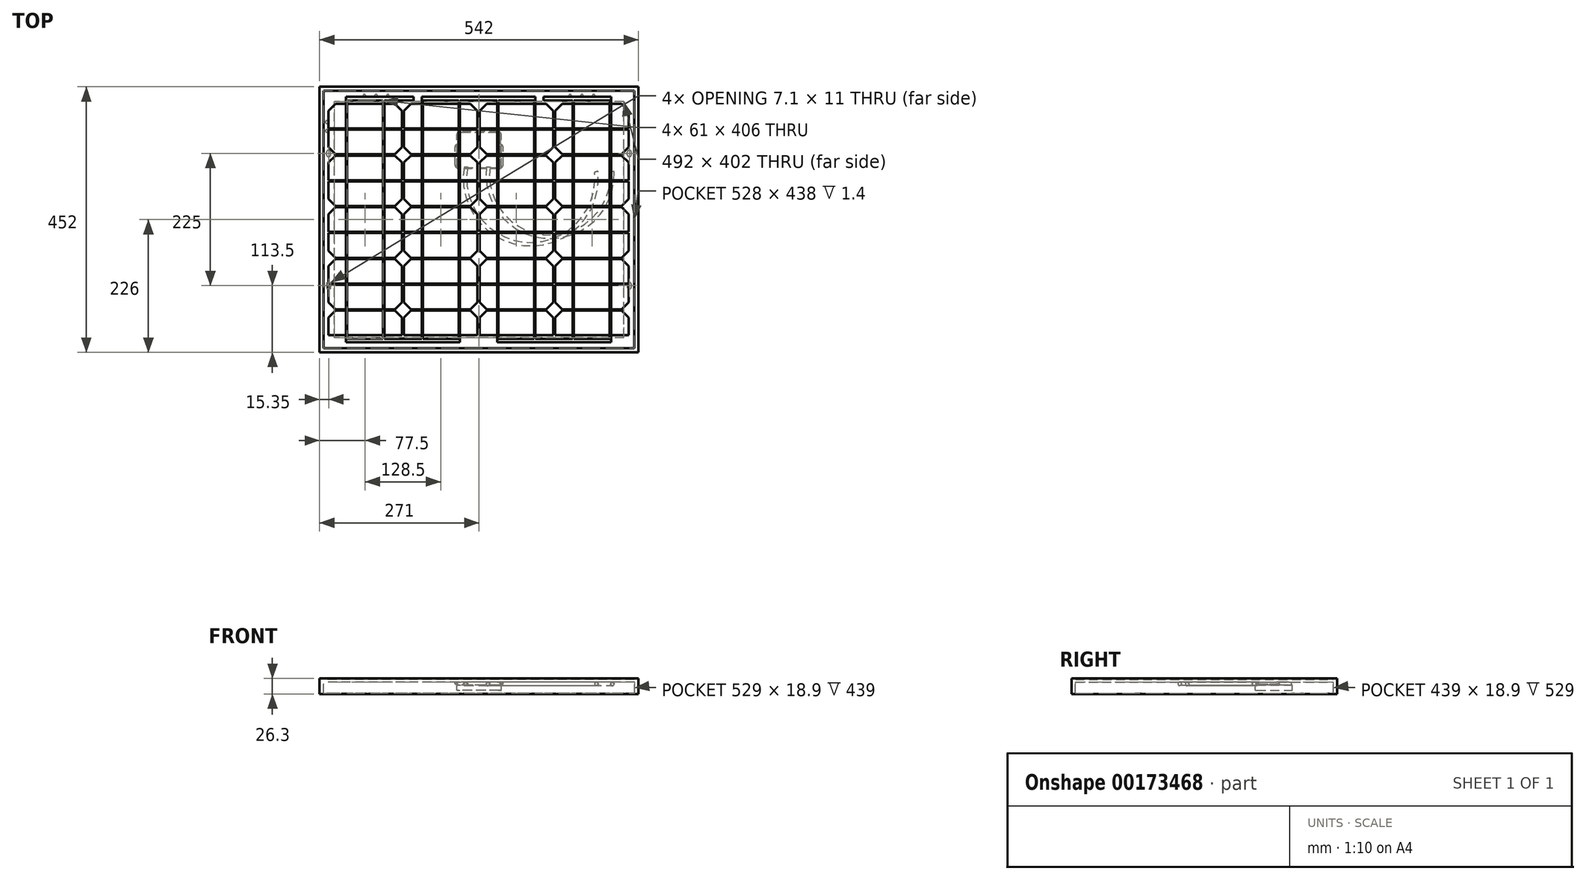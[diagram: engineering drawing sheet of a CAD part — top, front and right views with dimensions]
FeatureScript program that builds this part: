
annotation { "Feature Type Name" : "Feature", "Feature Type Description" : "" }
export const myFeature = defineFeature(function(context is Context, id is Id, definition is map)
    precondition{}
    {
        {
            var Q0;
            Q0=qCreatedBy(makeId("Top.planeOp"),FACE);
            var sketch = newSketch(context, id + "F0", { "sketchPlane" : qUnion([Q0])});
            skLineSegment(sketch, "E0.bottom", {"start": v(271, -226) * mm, "end": v(-271, -226) * mm});
            skLineSegment(sketch, "E0.top", {"start": v(271, 226) * mm, "end": v(-271, 226) * mm});
            skLineSegment(sketch, "E0.left", {"start": v(271, -226) * mm, "end": v(271, 226) * mm});
            skLineSegment(sketch, "E0.right", {"start": v(-271, -226) * mm, "end": v(-271, 226) * mm});
            skPoint(sketch, "E0.middle", {"position": v(0, 0) * mm});
            skSolve(sketch);
        }
        {
            var Q0;
            Q0 = qSketchRegion(id + "F0", true);
            extrude(context, id + "F1", {"entities" : qUnion([Q0]), "endBound" : BoundingType.SYMMETRIC, "depth" : 6.1 * mm});
        }
        {
            var Q0;
            Q0=makeQuery(id+"F1.opExtrude","CAP_FACE",FACE,{"disambiguationData":[OSD([sQuery(id+"F0.wireOp",EDGE,"E0.bottom"),sQuery(id+"F0.wireOp",EDGE,"E0.top"),sQuery(id+"F0.wireOp",EDGE,"E0.left"),sQuery(id+"F0.wireOp",EDGE,"E0.right")])],"isStart":false});
            var sketch = newSketch(context, id + "F2", { "sketchPlane" : qUnion([Q0])});
            skLineSegment(sketch, "E1.0", {"start": v(-271, -226) * mm, "end": v(-271, 226) * mm});
            skLineSegment(sketch, "E1.1", {"start": v(271, -226) * mm, "end": v(-271, -226) * mm});
            skLineSegment(sketch, "E1.2", {"start": v(271, 226) * mm, "end": v(-271, 226) * mm});
            skLineSegment(sketch, "E1.3", {"start": v(271, -226) * mm, "end": v(271, 226) * mm});
            skLineSegment(sketch, "E1.4", {"start": v(271, -226) * mm, "end": v(271, 226) * mm});
            skLineSegment(sketch, "E1.5", {"start": v(271, -226) * mm, "end": v(-271, -226) * mm});
            skLineSegment(sketch, "E1.6", {"start": v(271, 226) * mm, "end": v(-271, 226) * mm});
            skLineSegment(sketch, "E1.7", {"start": v(-271, -226) * mm, "end": v(-271, 226) * mm});
            skLineSegment(sketch, "E1.9", {"start": v(271, -226) * mm, "end": v(271, 226) * mm});
            skLineSegment(sketch, "E1.11", {"start": v(271, 226) * mm, "end": v(-271, 226) * mm});
            skLineSegment(sketch, "E1.12", {"start": v(271, -226) * mm, "end": v(-271, -226) * mm});
            skLineSegment(sketch, "E1.15", {"start": v(-271, -226) * mm, "end": v(-271, 226) * mm});
            skLineSegment(sketch, "E2.0", {"start": v(264, 219) * mm, "end": v(-264, 219) * mm});
            skLineSegment(sketch, "E2.1", {"start": v(264, -219) * mm, "end": v(264, 219) * mm});
            skLineSegment(sketch, "E2.2", {"start": v(264, -219) * mm, "end": v(-264, -219) * mm});
            skLineSegment(sketch, "E2.3", {"start": v(-264, -219) * mm, "end": v(-264, 219) * mm});
            skSolve(sketch);
        }
        {
            var Q0;
            Q0=makeQuery(id+"F2.imprint","IMPRINT",FACE,{"disambiguationData":[TD([[makeQuery(id+"F2.imprint","IMPRINT",EDGE,{"derivedFrom":sQuery(id+"F2.wireOp",EDGE,"E2.0")}),1.0]])]});
            extrude(context, id + "F3", {"entities" : qUnion([Q0]), "operationType" : NewBodyOperationType.REMOVE, "oppositeDirection" : true, "depth" : 1.4 * mm});
        }
        {
            var Q0;
            Q0=makeQuery(id+"F1.opExtrude","CAP_FACE",FACE,{"disambiguationData":[OSD([sQuery(id+"F0.wireOp",EDGE,"E0.bottom"),sQuery(id+"F0.wireOp",EDGE,"E0.top"),sQuery(id+"F0.wireOp",EDGE,"E0.left"),sQuery(id+"F0.wireOp",EDGE,"E0.right")])],"isStart":true});
            var sketch = newSketch(context, id + "F4", { "sketchPlane" : qUnion([Q0])});
            skLineSegment(sketch, "E3.0", {"start": v(-271, 226) * mm, "end": v(-271, -226) * mm});
            skLineSegment(sketch, "E3.1", {"start": v(271, 226) * mm, "end": v(-271, 226) * mm});
            skLineSegment(sketch, "E3.2", {"start": v(271, -226) * mm, "end": v(-271, -226) * mm});
            skLineSegment(sketch, "E3.3", {"start": v(271, 226) * mm, "end": v(271, -226) * mm});
            skLineSegment(sketch, "E3.4", {"start": v(271, 226) * mm, "end": v(271, -226) * mm});
            skLineSegment(sketch, "E3.5", {"start": v(-271, 226) * mm, "end": v(-271, -226) * mm});
            skLineSegment(sketch, "E3.6", {"start": v(271, -226) * mm, "end": v(-271, -226) * mm});
            skLineSegment(sketch, "E3.7", {"start": v(271, 226) * mm, "end": v(-271, 226) * mm});
            skLineSegment(sketch, "E3.8", {"start": v(-271, 226) * mm, "end": v(-271, -226) * mm});
            skLineSegment(sketch, "E3.9", {"start": v(271, -226) * mm, "end": v(-271, -226) * mm});
            skLineSegment(sketch, "E3.11", {"start": v(271, 226) * mm, "end": v(271, -226) * mm});
            skLineSegment(sketch, "E3.17", {"start": v(271, 226) * mm, "end": v(-271, 226) * mm});
            skLineSegment(sketch, "E4.0", {"start": v(264.5, 219.5) * mm, "end": v(-264.5, 219.5) * mm});
            skLineSegment(sketch, "E4.1", {"start": v(264.5, 219.5) * mm, "end": v(264.5, -219.5) * mm});
            skLineSegment(sketch, "E4.2", {"start": v(264.5, -219.5) * mm, "end": v(-264.5, -219.5) * mm});
            skLineSegment(sketch, "E4.3", {"start": v(-264.5, 219.5) * mm, "end": v(-264.5, -219.5) * mm});
            skSolve(sketch);
        }
        {
            var Q0;
            Q0 = qSketchRegion(id + "F4", true);
            extrude(context, id + "F5", {"entities" : qUnion([Q0]), "operationType" : NewBodyOperationType.ADD, "depth" : 18.9 * mm});
        }
        {
            var Q0;
            Q0=makeQuery(id+"F5.opExtrude","CAP_FACE",FACE,{"disambiguationData":[OSD([sQuery(id+"F4.wireOp",EDGE,"E3.8"),sQuery(id+"F4.wireOp",EDGE,"E3.9"),sQuery(id+"F4.wireOp",EDGE,"E3.11"),sQuery(id+"F4.wireOp",EDGE,"E3.17"),sQuery(id+"F4.wireOp",EDGE,"E4.0"),sQuery(id+"F4.wireOp",EDGE,"E4.1"),sQuery(id+"F4.wireOp",EDGE,"E4.2"),sQuery(id+"F4.wireOp",EDGE,"E4.3")])],"isStart":false});
            var sketch = newSketch(context, id + "F6", { "sketchPlane" : qUnion([Q0])});
            skLineSegment(sketch, "E5.0", {"start": v(271, 226) * mm, "end": v(-271, 226) * mm});
            skLineSegment(sketch, "E6.0", {"start": v(-271, 226) * mm, "end": v(-271, -226) * mm});
            skLineSegment(sketch, "E7.0", {"start": v(271, 226) * mm, "end": v(271, -226) * mm});
            skLineSegment(sketch, "E8.0", {"start": v(271, -226) * mm, "end": v(-271, -226) * mm});
            skLineSegment(sketch, "E9.0", {"start": v(246, 201) * mm, "end": v(-246, 201) * mm});
            skLineSegment(sketch, "E9.1", {"start": v(246, 201) * mm, "end": v(246, -201) * mm});
            skLineSegment(sketch, "E9.2", {"start": v(246, -201) * mm, "end": v(-246, -201) * mm});
            skLineSegment(sketch, "E9.3", {"start": v(-246, 201) * mm, "end": v(-246, -201) * mm});
            skSolve(sketch);
        }
        {
            var Q0;
            Q0 = qSketchRegion(id + "F6", true);
            extrude(context, id + "F7", {"entities" : qUnion([Q0]), "operationType" : NewBodyOperationType.ADD, "depth" : 1.1 * mm});
        }
        {
            var Q0;
            Q0=makeQuery(id+"F1.opExtrude","CAP_FACE",FACE,{"disambiguationData":[OSD([sQuery(id+"F0.wireOp",EDGE,"E0.bottom"),sQuery(id+"F0.wireOp",EDGE,"E0.top"),sQuery(id+"F0.wireOp",EDGE,"E0.left"),sQuery(id+"F0.wireOp",EDGE,"E0.right")])],"isStart":true});
            var sketch = newSketch(context, id + "F8", { "sketchPlane" : qUnion([Q0])});
            skLineSegment(sketch, "E10", {"start": v(0, 0) * mm, "end": v(0, -313.5) * mm, "construction": true});
            skPoint(sketch, "E10.endSnap0", {"position": v(0, -264.5) * mm});
            skLineSegment(sketch, "E11", {"start": v(31, -148) * mm, "end": v(-31, -148) * mm});
            skLineSegment(sketch, "E12", {"start": v(36, -88) * mm, "end": v(-36, -88) * mm});
            skLineSegment(sketch, "E13", {"start": v(41, -93) * mm, "end": v(41, -123) * mm});
            skLineSegment(sketch, "E14", {"start": v(173, 36) * mm, "end": v(173, 36) * mm});
            skLineSegment(sketch, "E15", {"start": v(36, -143) * mm, "end": v(36, -128.92) * mm});
            skPoint(sketch, "E16.visualSharp", {"position": v(41, -88) * mm});
            skArc(sketch, "E16.filletArc", {"start": v(41, -93) * mm, "mid": v(39.54, -89.46) * mm, "end": v(36, -88) * mm});
            skPoint(sketch, "E17.visualSharp", {"position": v(41, -128) * mm});
            skArc(sketch, "E17.filletArc", {"start": v(36.83, -127.93) * mm, "mid": v(39.82, -126.23) * mm, "end": v(41, -123) * mm});
            skPoint(sketch, "E18.visualSharp", {"position": v(36, -128) * mm});
            skArc(sketch, "E18.filletArc", {"start": v(36.83, -127.93) * mm, "mid": v(36.24, -128.27) * mm, "end": v(36, -128.92) * mm});
            skPoint(sketch, "E19.visualSharp", {"position": v(36, -148) * mm});
            skArc(sketch, "E19.filletArc", {"start": v(31, -148) * mm, "mid": v(34.54, -146.54) * mm, "end": v(36, -143) * mm});
            skArc(sketch, "E20.MirrorCS", {"start": v(-41, -93) * mm, "mid": v(-39.54, -89.46) * mm, "end": v(-36, -88) * mm});
            skLineSegment(sketch, "E21.MirrorCS", {"start": v(-41, -93) * mm, "end": v(-41, -123) * mm});
            skArc(sketch, "E22.MirrorCS", {"start": v(-36.83, -127.93) * mm, "mid": v(-39.82, -126.23) * mm, "end": v(-41, -123) * mm});
            skLineSegment(sketch, "E23.MirrorCS", {"start": v(-36, -143) * mm, "end": v(-36, -128.92) * mm});
            skArc(sketch, "E24.MirrorCS", {"start": v(-31, -148) * mm, "mid": v(-34.54, -146.54) * mm, "end": v(-36, -143) * mm});
            skPoint(sketch, "E25.orphan", {"position": v(-41, -88) * mm});
            skPoint(sketch, "E26.orphan", {"position": v(-36, -148) * mm});
            skArc(sketch, "E27.MirrorCS", {"start": v(-36.83, -127.93) * mm, "mid": v(-36.24, -128.27) * mm, "end": v(-36, -128.92) * mm});
            skSolve(sketch);
        }
        {
            var Q0;
            Q0 = qSketchRegion(id + "F8", true);
            extrude(context, id + "F9", {"entities" : qUnion([Q0]), "depth" : 5 * mm});
        }
        {
            var Q0;
            Q0=makeQuery(id+"F9.opExtrude","CAP_FACE",FACE,{"disambiguationData":[OSD([sQuery(id+"F8.wireOp",EDGE,"E11"),sQuery(id+"F8.wireOp",EDGE,"E12"),sQuery(id+"F8.wireOp",EDGE,"E13"),sQuery(id+"F8.wireOp",EDGE,"E15"),sQuery(id+"F8.wireOp",EDGE,"E16.filletArc"),sQuery(id+"F8.wireOp",EDGE,"E17.filletArc"),sQuery(id+"F8.wireOp",EDGE,"E18.filletArc"),sQuery(id+"F8.wireOp",EDGE,"E19.filletArc"),sQuery(id+"F8.wireOp",EDGE,"E20.MirrorCS"),sQuery(id+"F8.wireOp",EDGE,"E21.MirrorCS"),sQuery(id+"F8.wireOp",EDGE,"E22.MirrorCS"),sQuery(id+"F8.wireOp",EDGE,"E23.MirrorCS"),sQuery(id+"F8.wireOp",EDGE,"E24.MirrorCS"),sQuery(id+"F8.wireOp",EDGE,"E27.MirrorCS")])],"isStart":false});
            var sketch = newSketch(context, id + "F10", { "sketchPlane" : qUnion([Q0])});
            skLineSegment(sketch, "E28", {"start": v(0, -88) * mm, "end": v(0, -148) * mm, "construction": true});
            skLineSegment(sketch, "E29", {"start": v(-41, -118) * mm, "end": v(41, -118) * mm, "construction": true});
            skPoint(sketch, "E29.startSnap0", {"position": v(0, -118) * mm});
            skLineSegment(sketch, "E30.bottom", {"start": v(34.75, -86.35) * mm, "end": v(-34.75, -86.35) * mm});
            skLineSegment(sketch, "E30.top", {"start": v(32.75, -149.65) * mm, "end": v(-32.75, -149.65) * mm});
            skLineSegment(sketch, "E30.left", {"start": v(37.75, -89.35) * mm, "end": v(37.75, -144.65) * mm});
            skLineSegment(sketch, "E30.right", {"start": v(-37.75, -89.35) * mm, "end": v(-37.75, -144.65) * mm});
            skPoint(sketch, "E31.visualSharp", {"position": v(-37.75, -149.65) * mm});
            skArc(sketch, "E31.filletArc", {"start": v(-37.75, -144.65) * mm, "mid": v(-36.29, -148.19) * mm, "end": v(-32.75, -149.65) * mm});
            skPoint(sketch, "E32.visualSharp", {"position": v(37.75, -149.65) * mm});
            skArc(sketch, "E32.filletArc", {"start": v(32.75, -149.65) * mm, "mid": v(36.29, -148.19) * mm, "end": v(37.75, -144.65) * mm});
            skPoint(sketch, "E33.visualSharp", {"position": v(-37.75, -86.35) * mm});
            skArc(sketch, "E33.filletArc", {"start": v(-34.75, -86.35) * mm, "mid": v(-36.87, -87.23) * mm, "end": v(-37.75, -89.35) * mm});
            skPoint(sketch, "E34.visualSharp", {"position": v(37.75, -86.35) * mm});
            skArc(sketch, "E34.filletArc", {"start": v(37.75, -89.35) * mm, "mid": v(36.87, -87.23) * mm, "end": v(34.75, -86.35) * mm});
            skSolve(sketch);
        }
        {
            var Q0;
            Q0 = qSketchRegion(id + "F10", true);
            extrude(context, id + "F11", {"entities" : qUnion([Q0]), "operationType" : NewBodyOperationType.ADD, "depth" : 8.9 * mm});
        }
        {
            var Q0;
            Q0=makeQuery(id+"F7.opExtrude","CAP_FACE",FACE,{"disambiguationData":[OSD([sQuery(id+"F6.wireOp",EDGE,"E5.0"),sQuery(id+"F6.wireOp",EDGE,"E6.0"),sQuery(id+"F6.wireOp",EDGE,"E7.0"),sQuery(id+"F6.wireOp",EDGE,"E8.0"),sQuery(id+"F6.wireOp",EDGE,"E9.0"),sQuery(id+"F6.wireOp",EDGE,"E9.1"),sQuery(id+"F6.wireOp",EDGE,"E9.2"),sQuery(id+"F6.wireOp",EDGE,"E9.3")])],"isStart":false});
            var sketch = newSketch(context, id + "F12", { "sketchPlane" : qUnion([Q0])});
            skLineSegment(sketch, "E35", {"start": v(-271, -210.7) * mm, "end": v(271, -210.7) * mm, "construction": true});
            skLineSegment(sketch, "E36", {"start": v(-206, -201) * mm, "end": v(-206, -226) * mm, "construction": true});
            skLineSegment(sketch, "E37", {"start": v(0, -226) * mm, "end": v(0, -185.65) * mm, "construction": true});
            skPoint(sketch, "E37.endSnap0", {"position": v(0, -201) * mm});
            skCircle(sketch, "E38", {"center": v(-195, -210.7) * mm, "radius": 2.25 * mm});
            skCircle(sketch, "E39", {"center": v(-175, -210.7) * mm, "radius": 2.25 * mm});
            skCircle(sketch, "E40", {"center": v(-155, -210.7) * mm, "radius": 2.25 * mm});
            skLineSegment(sketch, "E41", {"start": v(-144, -201) * mm, "end": v(-144, -226) * mm, "construction": true});
            skLineSegment(sketch, "E42.MirrorCS", {"start": v(144, -201) * mm, "end": v(144, -226) * mm, "construction": true});
            skCircle(sketch, "E43.MirrorC", {"center": v(155, -210.7) * mm, "radius": 2.25 * mm});
            skCircle(sketch, "E44.MirrorC", {"center": v(175, -210.7) * mm, "radius": 2.25 * mm});
            skCircle(sketch, "E45.MirrorC", {"center": v(195, -210.7) * mm, "radius": 2.25 * mm});
            skLineSegment(sketch, "E46.MirrorCS", {"start": v(206, -201) * mm, "end": v(206, -226) * mm, "construction": true});
            skLineSegment(sketch, "E47", {"start": v(255.65, 226) * mm, "end": v(255.65, -226) * mm, "construction": true});
            skLineSegment(sketch, "E48.bottom", {"start": v(255.66, 107) * mm, "end": v(255.64, 107) * mm});
            skLineSegment(sketch, "E48.top", {"start": v(255.66, 118) * mm, "end": v(255.64, 118) * mm});
            skLineSegment(sketch, "E48.left", {"start": v(259.2, 110.54) * mm, "end": v(259.2, 114.46) * mm});
            skLineSegment(sketch, "E48.right", {"start": v(252.1, 110.54) * mm, "end": v(252.1, 114.46) * mm});
            skPoint(sketch, "E48.middle", {"position": v(255.65, 112.5) * mm});
            skLineSegment(sketch, "E49", {"start": v(0, 0) * mm, "end": v(148.89, 0) * mm, "construction": true});
            skPoint(sketch, "E50.visualSharp", {"position": v(252.1, 118) * mm});
            skArc(sketch, "E50.filletArc", {"start": v(255.64, 118) * mm, "mid": v(253.14, 116.96) * mm, "end": v(252.1, 114.46) * mm});
            skPoint(sketch, "E51.visualSharp", {"position": v(259.2, 118) * mm});
            skArc(sketch, "E51.filletArc", {"start": v(259.2, 114.46) * mm, "mid": v(258.16, 116.96) * mm, "end": v(255.66, 118) * mm});
            skPoint(sketch, "E52.visualSharp", {"position": v(259.2, 107) * mm});
            skArc(sketch, "E52.filletArc", {"start": v(255.66, 107) * mm, "mid": v(258.16, 108.04) * mm, "end": v(259.2, 110.54) * mm});
            skPoint(sketch, "E53.visualSharp", {"position": v(252.1, 107) * mm});
            skArc(sketch, "E53.filletArc", {"start": v(252.1, 110.54) * mm, "mid": v(253.14, 108.04) * mm, "end": v(255.64, 107) * mm});
            skLineSegment(sketch, "E54.MirrorCS", {"start": v(252.1, -110.54) * mm, "end": v(252.1, -114.46) * mm});
            skArc(sketch, "E55.MirrorCS", {"start": v(255.64, -118) * mm, "mid": v(253.14, -116.96) * mm, "end": v(252.1, -114.46) * mm});
            skArc(sketch, "E56.MirrorCS", {"start": v(259.2, -114.46) * mm, "mid": v(258.16, -116.96) * mm, "end": v(255.66, -118) * mm});
            skLineSegment(sketch, "E57.MirrorCS", {"start": v(259.2, -110.54) * mm, "end": v(259.2, -114.46) * mm});
            skArc(sketch, "E58.MirrorCS", {"start": v(255.66, -107) * mm, "mid": v(258.16, -108.04) * mm, "end": v(259.2, -110.54) * mm});
            skArc(sketch, "E59.MirrorCS", {"start": v(252.1, -110.54) * mm, "mid": v(253.14, -108.04) * mm, "end": v(255.64, -107) * mm});
            skArc(sketch, "E60.MirrorCS", {"start": v(-252.1, -110.54) * mm, "mid": v(-253.14, -108.04) * mm, "end": v(-255.64, -107) * mm});
            skArc(sketch, "E61.MirrorCS", {"start": v(-259.2, -114.46) * mm, "mid": v(-258.16, -116.96) * mm, "end": v(-255.66, -118) * mm});
            skLineSegment(sketch, "E62.MirrorCS", {"start": v(-252.1, -110.54) * mm, "end": v(-252.1, -114.46) * mm});
            skArc(sketch, "E63.MirrorCS", {"start": v(-255.66, -107) * mm, "mid": v(-258.16, -108.04) * mm, "end": v(-259.2, -110.54) * mm});
            skArc(sketch, "E64.MirrorCS", {"start": v(-255.64, -118) * mm, "mid": v(-253.14, -116.96) * mm, "end": v(-252.1, -114.46) * mm});
            skLineSegment(sketch, "E65.MirrorCS", {"start": v(-259.2, -110.54) * mm, "end": v(-259.2, -114.46) * mm});
            skLineSegment(sketch, "E66.MirrorCS", {"start": v(-255.66, 107) * mm, "end": v(-255.64, 107) * mm});
            skLineSegment(sketch, "E67.MirrorCS", {"start": v(-255.66, 118) * mm, "end": v(-255.64, 118) * mm});
            skLineSegment(sketch, "E68.MirrorCS", {"start": v(-252.1, 110.54) * mm, "end": v(-252.1, 114.46) * mm});
            skArc(sketch, "E69.MirrorCS", {"start": v(-255.66, 107) * mm, "mid": v(-258.16, 108.04) * mm, "end": v(-259.2, 110.54) * mm});
            skPoint(sketch, "E70.MirrorP", {"position": v(-255.65, 112.5) * mm});
            skPoint(sketch, "E71.MirrorP", {"position": v(-252.1, 118) * mm});
            skPoint(sketch, "E72.MirrorP", {"position": v(-259.2, 107) * mm});
            skPoint(sketch, "E73.MirrorP", {"position": v(-259.2, 118) * mm});
            skArc(sketch, "E74.MirrorCS", {"start": v(-255.64, 118) * mm, "mid": v(-253.14, 116.96) * mm, "end": v(-252.1, 114.46) * mm});
            skArc(sketch, "E75.MirrorCS", {"start": v(-259.2, 114.46) * mm, "mid": v(-258.16, 116.96) * mm, "end": v(-255.66, 118) * mm});
            skPoint(sketch, "E76.MirrorP", {"position": v(-252.1, 107) * mm});
            skLineSegment(sketch, "E77.MirrorCS", {"start": v(-259.2, 110.54) * mm, "end": v(-259.2, 114.46) * mm});
            skArc(sketch, "E78.MirrorCS", {"start": v(-252.1, 110.54) * mm, "mid": v(-253.14, 108.04) * mm, "end": v(-255.64, 107) * mm});
            skLineSegment(sketch, "E79", {"start": v(-271, -166) * mm, "end": v(-246, -166) * mm, "construction": true});
            skLineSegment(sketch, "E80", {"start": v(-258.5, -226) * mm, "end": v(-258.5, -121.19) * mm, "construction": true});
            skPoint(sketch, "E80.startSnap0", {"position": v(-258.5, -166) * mm});
            skCircle(sketch, "E81", {"center": v(-258.5, -166) * mm, "radius": 2.5 * mm});
            skCircle(sketch, "E82", {"center": v(-258.5, -151) * mm, "radius": 2.5 * mm});
            skLineSegment(sketch, "E83.MirrorCS", {"start": v(-255.66, -107) * mm, "end": v(-255.64, -107) * mm});
            skLineSegment(sketch, "E84.MirrorCS", {"start": v(-255.66, -118) * mm, "end": v(-255.64, -118) * mm});
            skPoint(sketch, "E85.MirrorP", {"position": v(-259.2, -107) * mm});
            skPoint(sketch, "E86.MirrorP", {"position": v(-259.2, -118) * mm});
            skPoint(sketch, "E87.MirrorP", {"position": v(-252.1, -107) * mm});
            skPoint(sketch, "E88.MirrorP", {"position": v(-252.1, -118) * mm});
            skPoint(sketch, "E89.MirrorP", {"position": v(-255.65, -112.5) * mm});
            skLineSegment(sketch, "E90.MirrorCS", {"start": v(255.66, -107) * mm, "end": v(255.64, -107) * mm});
            skLineSegment(sketch, "E91.MirrorCS", {"start": v(255.66, -118) * mm, "end": v(255.64, -118) * mm});
            skPoint(sketch, "E92.MirrorP", {"position": v(259.2, -118) * mm});
            skPoint(sketch, "E93.MirrorP", {"position": v(252.1, -118) * mm});
            skPoint(sketch, "E94.MirrorP", {"position": v(259.2, -107) * mm});
            skPoint(sketch, "E95.MirrorP", {"position": v(255.65, -112.5) * mm});
            skPoint(sketch, "E96.MirrorP", {"position": v(252.1, -107) * mm});
            skSolve(sketch);
        }
        {
            var Q0;
            Q0 = qSketchRegion(id + "F12", true);
            extrude(context, id + "F13", {"entities" : qUnion([Q0]), "operationType" : NewBodyOperationType.REMOVE, "oppositeDirection" : true, "depth" : 3 * mm});
        }
        {
            var Q0;
            {var subQ2=sQuery(id+"F8.wireOp",EDGE,"E22.MirrorCS");var subQ3=sQuery(id+"F8.wireOp",EDGE,"E21.MirrorCS");var subQ4=sQuery(id+"F8.wireOp",EDGE,"E20.MirrorCS");Q0=makeQuery(id+"F11.boolean.opBoolean","SPLIT",FACE,{"disambiguationData":[TD([makeQuery(id+"F9.opExtrude","SWEPT_FACE",FACE,{"disambiguationData":[OSD([subQ4])]})])],"derivedFrom":makeQuery(id+"F9.opExtrude","CAP_FACE",FACE,{"disambiguationData":[OSD([sQuery(id+"F8.wireOp",EDGE,"E11"),sQuery(id+"F8.wireOp",EDGE,"E12"),sQuery(id+"F8.wireOp",EDGE,"E13"),sQuery(id+"F8.wireOp",EDGE,"E15"),sQuery(id+"F8.wireOp",EDGE,"E16.filletArc"),sQuery(id+"F8.wireOp",EDGE,"E17.filletArc"),sQuery(id+"F8.wireOp",EDGE,"E18.filletArc"),sQuery(id+"F8.wireOp",EDGE,"E19.filletArc"),subQ4,subQ3,subQ2,sQuery(id+"F8.wireOp",EDGE,"E23.MirrorCS"),sQuery(id+"F8.wireOp",EDGE,"E24.MirrorCS"),sQuery(id+"F8.wireOp",EDGE,"E27.MirrorCS")])],"isStart":false})});}
            var sketch = newSketch(context, id + "F14", { "sketchPlane" : qUnion([Q0])});
            skLineSegment(sketch, "E97.0", {"start": v(-41, -93) * mm, "end": v(-41, -123) * mm});
            skArc(sketch, "E98.0", {"start": v(-41, -93) * mm, "mid": v(-39.54, -89.46) * mm, "end": v(-36, -88) * mm});
            skArc(sketch, "E99.0", {"start": v(-36.83, -127.93) * mm, "mid": v(-39.82, -126.23) * mm, "end": v(-41, -123) * mm});
            skArc(sketch, "E100.0", {"start": v(41, -93) * mm, "mid": v(39.54, -89.46) * mm, "end": v(36, -88) * mm});
            skLineSegment(sketch, "E101.0", {"start": v(41, -93) * mm, "end": v(41, -123) * mm});
            skArc(sketch, "E102.0", {"start": v(36.83, -127.93) * mm, "mid": v(39.82, -126.23) * mm, "end": v(41, -123) * mm});
            skPoint(sketch, "E103.0", {"position": v(36.24, -128.27) * mm});
            skArc(sketch, "E104.0", {"start": v(36.83, -127.93) * mm, "mid": v(36.24, -128.27) * mm, "end": v(36, -128.92) * mm});
            skArc(sketch, "E105.0", {"start": v(-36.83, -127.93) * mm, "mid": v(-36.24, -128.27) * mm, "end": v(-36, -128.92) * mm});
            skLineSegment(sketch, "E106", {"start": v(-36, -88) * mm, "end": v(-36, -128.92) * mm});
            skLineSegment(sketch, "E107", {"start": v(36, -88) * mm, "end": v(36, -128.92) * mm});
            skSolve(sketch);
        }
        {
            var Q0;
            Q0 = qSketchRegion(id + "F14", true);
            extrude(context, id + "F15", {"entities" : qUnion([Q0]), "operationType" : NewBodyOperationType.REMOVE, "oppositeDirection" : true, "depth" : 1.9 * mm});
        }
        {
            var Q0;
            Q0=makeQuery(id+"F15.boolean.opBoolean","COPY",FACE,{"derivedFrom":makeQuery(id+"F15.opExtrude","CAP_FACE",FACE,{"disambiguationData":[OSD([sQuery(id+"F14.wireOp",EDGE,"E100.0"),sQuery(id+"F14.wireOp",EDGE,"E101.0"),sQuery(id+"F14.wireOp",EDGE,"E102.0"),sQuery(id+"F14.wireOp",EDGE,"E104.0"),sQuery(id+"F14.wireOp",EDGE,"E107")])],"isStart":false})});
            var sketch = newSketch(context, id + "F16", { "sketchPlane" : qUnion([Q0])});
            skArc(sketch, "E108", {"start": v(199.7, -81.44) * mm, "mid": v(83.96, 42.04) * mm, "end": v(-22.28, -89.7) * mm});
            skArc(sketch, "E109", {"start": v(226.85, -81.44) * mm, "mid": v(116.67, 29.56) * mm, "end": v(15.5, -89.7) * mm});
            skSolve(sketch);
        }
        {
            var Q0;
            Q0=qCreatedBy(makeId("Front.planeOp"),FACE);
            var Q1;
            Q1=makeQuery(id+"F11.opExtrude","CAP_EDGE",EDGE,{"disambiguationData":[OSD([sQuery(id+"F10.wireOp",EDGE,"E30.bottom")])],"isStart":false});
            cPlane(context, id + "F17", {"entities" : qUnion([Q0, Q1]), "cplaneType" : CPlaneType.LINE_ANGLE, "offset" : 25 * mm, "angle" : 0 * degree, "width" : 150 * mm, "height" : 150 * mm});
        }
        {
            var Q0;
            Q0=qCreatedBy(id+"F17.planeOp",FACE);
            var sketch = newSketch(context, id + "F18", { "sketchPlane" : qUnion([Q0])});
            skCircle(sketch, "E110", {"center": v(22.63, -6.06) * mm, "radius": 2.95 * mm});
            skCircle(sketch, "E111", {"center": v(-15.33, -6.24) * mm, "radius": 2.95 * mm});
            skSolve(sketch);
        }
        {
            var Q0;
            Q0=makeQuery(id+"F18.imprint","IMPRINT",FACE,{"disambiguationData":[TD([[makeQuery(id+"F18.imprint","IMPRINT",EDGE,{"derivedFrom":sQuery(id+"F18.wireOp",EDGE,"E110")}),1.0]])]});
            var Q1;
            Q1=sQuery(id+"F16.wireOp",EDGE,"E108");
            sweep(context, id + "F19", {"profiles" : qUnion([Q0]), "path" : qUnion([Q1])});
        }
        {
            var Q0;
            Q0=makeQuery(id+"F18.imprint","IMPRINT",FACE,{"disambiguationData":[TD([[makeQuery(id+"F18.imprint","IMPRINT",EDGE,{"derivedFrom":sQuery(id+"F18.wireOp",EDGE,"E111")}),1.0]])]});
            var Q1;
            Q1=sQuery(id+"F16.wireOp",EDGE,"E109");
            sweep(context, id + "F20", {"profiles" : qUnion([Q0]), "path" : qUnion([Q1])});
        }
        {
            var Q0;
            Q0=makeQuery(id+"F3.boolean.opBoolean","COPY",FACE,{"derivedFrom":makeQuery(id+"F3.opExtrude","CAP_FACE",FACE,{"disambiguationData":[OSD([sQuery(id+"F2.wireOp",EDGE,"E2.0"),sQuery(id+"F2.wireOp",EDGE,"E2.1"),sQuery(id+"F2.wireOp",EDGE,"E2.2"),sQuery(id+"F2.wireOp",EDGE,"E2.3")])],"isStart":false})});
            var sketch = newSketch(context, id + "F21", { "sketchPlane" : qUnion([Q0])});
            skLineSegment(sketch, "E112.0", {"start": v(264, 219) * mm, "end": v(-264, 219) * mm});
            skLineSegment(sketch, "E113.0", {"start": v(-264, -219) * mm, "end": v(-264, 219) * mm});
            skLineSegment(sketch, "E114.0", {"start": v(264, -219) * mm, "end": v(-264, -219) * mm});
            skLineSegment(sketch, "E115.0", {"start": v(264, -219) * mm, "end": v(264, 219) * mm});
            skSolve(sketch);
        }
        {
            var Q0;
            Q0 = qSketchRegion(id + "F21", true);
            extrude(context, id + "F22", {"entities" : qUnion([Q0]), "depth" : 1 * mm});
        }
        {
            var Q0;
            Q0=makeQuery(id+"F22.opExtrude","CAP_FACE",FACE,{"disambiguationData":[OSD([sQuery(id+"F21.wireOp",EDGE,"E112.0"),sQuery(id+"F21.wireOp",EDGE,"E113.0"),sQuery(id+"F21.wireOp",EDGE,"E114.0"),sQuery(id+"F21.wireOp",EDGE,"E115.0")])],"isStart":false});
            var sketch = newSketch(context, id + "F23", { "sketchPlane" : qUnion([Q0])});
            skLineSegment(sketch, "E116.bottom", {"start": v(-244, 197) * mm, "end": v(-143, 197) * mm});
            skLineSegment(sketch, "E116.top", {"start": v(-244, 111) * mm, "end": v(-143, 111) * mm});
            skLineSegment(sketch, "E116.left", {"start": v(-256, 185) * mm, "end": v(-256, 155) * mm});
            skLineSegment(sketch, "E116.right", {"start": v(-131, 185) * mm, "end": v(-131, 155) * mm});
            skLineSegment(sketch, "E117", {"start": v(-244, 197) * mm, "end": v(-256, 185) * mm});
            skLineSegment(sketch, "E118", {"start": v(-143, 197) * mm, "end": v(-131, 185) * mm});
            skLineSegment(sketch, "E119", {"start": v(-131, 123) * mm, "end": v(-143, 111) * mm});
            skLineSegment(sketch, "E120", {"start": v(-244, 111) * mm, "end": v(-256, 123) * mm});
            skPoint(sketch, "E121.orphan", {"position": v(-131, 197) * mm});
            skPoint(sketch, "E122.orphan", {"position": v(-131, 111) * mm});
            skLineSegment(sketch, "E123", {"start": v(-256, 155) * mm, "end": v(-131, 155) * mm});
            skLineSegment(sketch, "E124", {"start": v(-256, 153) * mm, "end": v(-131, 153) * mm});
            skLineSegment(sketch, "E125.trimOffspring", {"start": v(-131, 153) * mm, "end": v(-131, 123) * mm});
            skLineSegment(sketch, "E126.trimOffspring", {"start": v(-256, 153) * mm, "end": v(-256, 123) * mm});
            skLineSegment(sketch, "E127", {"start": v(-129.25, 235.4) * mm, "end": v(-129.25, -233.44) * mm, "construction": true});
            skLineSegment(sketch, "E128", {"start": v(-282.26, 110) * mm, "end": v(303.4, 110) * mm, "construction": true});
            skLineSegment(sketch, "E129.MirrorCS", {"start": v(-14.5, 197) * mm, "end": v(-2.5, 185) * mm});
            skLineSegment(sketch, "E130.MirrorCS", {"start": v(-14.5, 197) * mm, "end": v(-115.5, 197) * mm});
            skLineSegment(sketch, "E131.MirrorCS", {"start": v(-115.5, 197) * mm, "end": v(-127.5, 185) * mm});
            skLineSegment(sketch, "E132.MirrorCS", {"start": v(-127.5, 185) * mm, "end": v(-127.5, 155) * mm});
            skLineSegment(sketch, "E133.MirrorCS", {"start": v(-2.5, 153) * mm, "end": v(-127.5, 153) * mm});
            skLineSegment(sketch, "E134.MirrorCS", {"start": v(-2.5, 155) * mm, "end": v(-127.5, 155) * mm});
            skLineSegment(sketch, "E135.MirrorCS", {"start": v(-2.5, 185) * mm, "end": v(-2.5, 155) * mm});
            skLineSegment(sketch, "E136.MirrorCS", {"start": v(-2.5, 153) * mm, "end": v(-2.5, 123) * mm});
            skLineSegment(sketch, "E137.MirrorCS", {"start": v(-14.5, 111) * mm, "end": v(-2.5, 123) * mm});
            skLineSegment(sketch, "E138.MirrorCS", {"start": v(-14.5, 111) * mm, "end": v(-115.5, 111) * mm});
            skLineSegment(sketch, "E139.MirrorCS", {"start": v(-127.5, 123) * mm, "end": v(-115.5, 111) * mm});
            skLineSegment(sketch, "E140.MirrorCS", {"start": v(-127.5, 153) * mm, "end": v(-127.5, 123) * mm});
            skLineSegment(sketch, "E141", {"start": v(-0.75, 235.4) * mm, "end": v(-0.75, -250.7) * mm, "construction": true});
            skLineSegment(sketch, "E142.MirrorCS", {"start": v(13, 197) * mm, "end": v(1, 185) * mm});
            skLineSegment(sketch, "E143.MirrorCS", {"start": v(1, 185) * mm, "end": v(1, 155) * mm});
            skLineSegment(sketch, "E144.MirrorCS", {"start": v(1, 155) * mm, "end": v(126, 155) * mm});
            skLineSegment(sketch, "E145.MirrorCS", {"start": v(1, 153) * mm, "end": v(1, 123) * mm});
            skLineSegment(sketch, "E146.MirrorCS", {"start": v(13, 111) * mm, "end": v(1, 123) * mm});
            skLineSegment(sketch, "E147.MirrorCS", {"start": v(13, 111) * mm, "end": v(114, 111) * mm});
            skLineSegment(sketch, "E148.MirrorCS", {"start": v(126, 123) * mm, "end": v(114, 111) * mm});
            skLineSegment(sketch, "E149.MirrorCS", {"start": v(126, 153) * mm, "end": v(126, 123) * mm});
            skLineSegment(sketch, "E150.MirrorCS", {"start": v(1, 153) * mm, "end": v(126, 153) * mm});
            skLineSegment(sketch, "E151.MirrorCS", {"start": v(126, 185) * mm, "end": v(126, 155) * mm});
            skLineSegment(sketch, "E152.MirrorCS", {"start": v(114, 197) * mm, "end": v(126, 185) * mm});
            skLineSegment(sketch, "E153.MirrorCS", {"start": v(13, 197) * mm, "end": v(114, 197) * mm});
            skLineSegment(sketch, "E154.MirrorCS", {"start": v(127.75, 235.4) * mm, "end": v(127.75, -233.44) * mm, "construction": true});
            skLineSegment(sketch, "E155.MirrorCS", {"start": v(141.5, 197) * mm, "end": v(129.5, 185) * mm});
            skLineSegment(sketch, "E156.MirrorCS", {"start": v(129.5, 185) * mm, "end": v(129.5, 155) * mm});
            skLineSegment(sketch, "E157.MirrorCS", {"start": v(254.5, 155) * mm, "end": v(129.5, 155) * mm});
            skLineSegment(sketch, "E158.MirrorCS", {"start": v(254.5, 153) * mm, "end": v(129.5, 153) * mm});
            skLineSegment(sketch, "E159.MirrorCS", {"start": v(129.5, 153) * mm, "end": v(129.5, 123) * mm});
            skLineSegment(sketch, "E160.MirrorCS", {"start": v(129.5, 123) * mm, "end": v(141.5, 111) * mm});
            skLineSegment(sketch, "E161.MirrorCS", {"start": v(242.5, 111) * mm, "end": v(141.5, 111) * mm});
            skLineSegment(sketch, "E162.MirrorCS", {"start": v(242.5, 197) * mm, "end": v(141.5, 197) * mm});
            skLineSegment(sketch, "E163.MirrorCS", {"start": v(242.5, 197) * mm, "end": v(254.5, 185) * mm});
            skLineSegment(sketch, "E164.MirrorCS", {"start": v(242.5, 111) * mm, "end": v(254.5, 123) * mm});
            skLineSegment(sketch, "E165.MirrorCS", {"start": v(254.5, 153) * mm, "end": v(254.5, 123) * mm});
            skLineSegment(sketch, "E166.MirrorCS", {"start": v(254.5, 185) * mm, "end": v(254.5, 155) * mm});
            skLineSegment(sketch, "E167.MirrorCS", {"start": v(-244, 109) * mm, "end": v(-256, 97) * mm});
            skLineSegment(sketch, "E168.MirrorCS", {"start": v(-131, 97) * mm, "end": v(-143, 109) * mm});
            skLineSegment(sketch, "E169.MirrorCS", {"start": v(-143, 23) * mm, "end": v(-131, 35) * mm});
            skLineSegment(sketch, "E170.MirrorCS", {"start": v(-244, 23) * mm, "end": v(-256, 35) * mm});
            skLineSegment(sketch, "E171.MirrorCS", {"start": v(-115.5, 23) * mm, "end": v(-127.5, 35) * mm});
            skLineSegment(sketch, "E172.MirrorCS", {"start": v(-14.5, 23) * mm, "end": v(-2.5, 35) * mm});
            skLineSegment(sketch, "E173.MirrorCS", {"start": v(-127.5, 97) * mm, "end": v(-115.5, 109) * mm});
            skLineSegment(sketch, "E174.MirrorCS", {"start": v(1, 65) * mm, "end": v(126, 65) * mm});
            skLineSegment(sketch, "E175.MirrorCS", {"start": v(129.5, 97) * mm, "end": v(141.5, 109) * mm});
            skLineSegment(sketch, "E176.MirrorCS", {"start": v(242.5, 23) * mm, "end": v(254.5, 35) * mm});
            skLineSegment(sketch, "E177.MirrorCS", {"start": v(-14.5, 109) * mm, "end": v(-2.5, 97) * mm});
            skLineSegment(sketch, "E178.MirrorCS", {"start": v(-256, 65) * mm, "end": v(-131, 65) * mm});
            skLineSegment(sketch, "E179.MirrorCS", {"start": v(-256, 67) * mm, "end": v(-131, 67) * mm});
            skPoint(sketch, "E180.MirrorP", {"position": v(-131, 109) * mm});
            skLineSegment(sketch, "E181.MirrorCS", {"start": v(114, 23) * mm, "end": v(126, 35) * mm});
            skLineSegment(sketch, "E182.MirrorCS", {"start": v(-14.5, 109) * mm, "end": v(-115.5, 109) * mm});
            skLineSegment(sketch, "E183.MirrorCS", {"start": v(-131, 67) * mm, "end": v(-131, 97) * mm});
            skLineSegment(sketch, "E184.MirrorCS", {"start": v(-256, 67) * mm, "end": v(-256, 97) * mm});
            skLineSegment(sketch, "E185.MirrorCS", {"start": v(-131, 35) * mm, "end": v(-131, 65) * mm});
            skLineSegment(sketch, "E186.MirrorCS", {"start": v(242.5, 109) * mm, "end": v(141.5, 109) * mm});
            skLineSegment(sketch, "E187.MirrorCS", {"start": v(-256, 35) * mm, "end": v(-256, 65) * mm});
            skLineSegment(sketch, "E188.MirrorCS", {"start": v(-244, 109) * mm, "end": v(-143, 109) * mm});
            skLineSegment(sketch, "E189.MirrorCS", {"start": v(13, 109) * mm, "end": v(114, 109) * mm});
            skLineSegment(sketch, "E190.MirrorCS", {"start": v(129.5, 35) * mm, "end": v(129.5, 65) * mm});
            skLineSegment(sketch, "E191.MirrorCS", {"start": v(13, 23) * mm, "end": v(1, 35) * mm});
            skLineSegment(sketch, "E192.MirrorCS", {"start": v(-244, 23) * mm, "end": v(-143, 23) * mm});
            skLineSegment(sketch, "E193.MirrorCS", {"start": v(254.5, 67) * mm, "end": v(254.5, 97) * mm});
            skLineSegment(sketch, "E194.MirrorCS", {"start": v(254.5, 67) * mm, "end": v(129.5, 67) * mm});
            skLineSegment(sketch, "E195.MirrorCS", {"start": v(-2.5, 67) * mm, "end": v(-2.5, 97) * mm});
            skPoint(sketch, "E196.MirrorP", {"position": v(-131, 23) * mm});
            skLineSegment(sketch, "E197.MirrorCS", {"start": v(254.5, 35) * mm, "end": v(254.5, 65) * mm});
            skLineSegment(sketch, "E198.MirrorCS", {"start": v(-14.5, 23) * mm, "end": v(-115.5, 23) * mm});
            skLineSegment(sketch, "E199.MirrorCS", {"start": v(-2.5, 35) * mm, "end": v(-2.5, 65) * mm});
            skLineSegment(sketch, "E200.MirrorCS", {"start": v(129.5, 67) * mm, "end": v(129.5, 97) * mm});
            skLineSegment(sketch, "E201.MirrorCS", {"start": v(1, 67) * mm, "end": v(1, 97) * mm});
            skLineSegment(sketch, "E202.MirrorCS", {"start": v(1, 67) * mm, "end": v(126, 67) * mm});
            skLineSegment(sketch, "E203.MirrorCS", {"start": v(-2.5, 67) * mm, "end": v(-127.5, 67) * mm});
            skLineSegment(sketch, "E204.MirrorCS", {"start": v(141.5, 23) * mm, "end": v(129.5, 35) * mm});
            skLineSegment(sketch, "E205.MirrorCS", {"start": v(13, 23) * mm, "end": v(114, 23) * mm});
            skLineSegment(sketch, "E206.MirrorCS", {"start": v(-127.5, 35) * mm, "end": v(-127.5, 65) * mm});
            skLineSegment(sketch, "E207.MirrorCS", {"start": v(13, 109) * mm, "end": v(1, 97) * mm});
            skLineSegment(sketch, "E208.MirrorCS", {"start": v(242.5, 109) * mm, "end": v(254.5, 97) * mm});
            skLineSegment(sketch, "E209.MirrorCS", {"start": v(254.5, 65) * mm, "end": v(129.5, 65) * mm});
            skLineSegment(sketch, "E210.MirrorCS", {"start": v(-127.5, 67) * mm, "end": v(-127.5, 97) * mm});
            skLineSegment(sketch, "E211.MirrorCS", {"start": v(-2.5, 65) * mm, "end": v(-127.5, 65) * mm});
            skLineSegment(sketch, "E212.MirrorCS", {"start": v(126, 67) * mm, "end": v(126, 97) * mm});
            skLineSegment(sketch, "E213.MirrorCS", {"start": v(242.5, 23) * mm, "end": v(141.5, 23) * mm});
            skLineSegment(sketch, "E214.MirrorCS", {"start": v(126, 35) * mm, "end": v(126, 65) * mm});
            skLineSegment(sketch, "E215.MirrorCS", {"start": v(126, 97) * mm, "end": v(114, 109) * mm});
            skLineSegment(sketch, "E216.MirrorCS", {"start": v(1, 35) * mm, "end": v(1, 65) * mm});
            skLineSegment(sketch, "E217.0", {"start": v(-282.26, 22) * mm, "end": v(303.4, 22) * mm, "construction": true});
            skLineSegment(sketch, "E218.MirrorCS", {"start": v(-131, -79) * mm, "end": v(-143, -67) * mm});
            skLineSegment(sketch, "E219.MirrorCS", {"start": v(-143, -153) * mm, "end": v(-131, -141) * mm});
            skLineSegment(sketch, "E220.MirrorCS", {"start": v(-244, -153) * mm, "end": v(-256, -141) * mm});
            skLineSegment(sketch, "E221.MirrorCS", {"start": v(-14.5, -153) * mm, "end": v(-2.5, -141) * mm});
            skLineSegment(sketch, "E222.MirrorCS", {"start": v(126, -53) * mm, "end": v(114, -65) * mm});
            skLineSegment(sketch, "E223.MirrorCS", {"start": v(242.5, -65) * mm, "end": v(254.5, -53) * mm});
            skLineSegment(sketch, "E224.MirrorCS", {"start": v(13, -67) * mm, "end": v(1, -79) * mm});
            skLineSegment(sketch, "E225.MirrorCS", {"start": v(129.5, -79) * mm, "end": v(141.5, -67) * mm});
            skLineSegment(sketch, "E226.MirrorCS", {"start": v(242.5, 21) * mm, "end": v(254.5, 9) * mm});
            skLineSegment(sketch, "E227.MirrorCS", {"start": v(13, 21) * mm, "end": v(1, 9) * mm});
            skLineSegment(sketch, "E228.MirrorCS", {"start": v(-14.5, -67) * mm, "end": v(-2.5, -79) * mm});
            skLineSegment(sketch, "E229.MirrorCS", {"start": v(-127.5, -53) * mm, "end": v(-115.5, -65) * mm});
            skLineSegment(sketch, "E230.MirrorCS", {"start": v(13, -65) * mm, "end": v(1, -53) * mm});
            skLineSegment(sketch, "E231.MirrorCS", {"start": v(129.5, -53) * mm, "end": v(141.5, -65) * mm});
            skLineSegment(sketch, "E232.MirrorCS", {"start": v(141.5, 21) * mm, "end": v(129.5, 9) * mm});
            skLineSegment(sketch, "E233.MirrorCS", {"start": v(13, -153) * mm, "end": v(1, -141) * mm});
            skLineSegment(sketch, "E234.MirrorCS", {"start": v(-14.5, 21) * mm, "end": v(-2.5, 9) * mm});
            skLineSegment(sketch, "E235.MirrorCS", {"start": v(126, -79) * mm, "end": v(114, -67) * mm});
            skLineSegment(sketch, "E236.MirrorCS", {"start": v(114, 21) * mm, "end": v(126, 9) * mm});
            skLineSegment(sketch, "E237.MirrorCS", {"start": v(-131, -53) * mm, "end": v(-143, -65) * mm});
            skLineSegment(sketch, "E238.MirrorCS", {"start": v(114, -153) * mm, "end": v(126, -141) * mm});
            skLineSegment(sketch, "E239.MirrorCS", {"start": v(141.5, -153) * mm, "end": v(129.5, -141) * mm});
            skLineSegment(sketch, "E240.MirrorCS", {"start": v(-115.5, 21) * mm, "end": v(-127.5, 9) * mm});
            skLineSegment(sketch, "E241.MirrorCS", {"start": v(1, -21) * mm, "end": v(126, -21) * mm});
            skLineSegment(sketch, "E242.MirrorCS", {"start": v(-115.5, -153) * mm, "end": v(-127.5, -141) * mm});
            skLineSegment(sketch, "E243.MirrorCS", {"start": v(-127.5, -79) * mm, "end": v(-115.5, -67) * mm});
            skLineSegment(sketch, "E244.MirrorCS", {"start": v(-143, 21) * mm, "end": v(-131, 9) * mm});
            skLineSegment(sketch, "E245.MirrorCS", {"start": v(-14.5, -65) * mm, "end": v(-2.5, -53) * mm});
            skLineSegment(sketch, "E246.MirrorCS", {"start": v(1, -111) * mm, "end": v(126, -111) * mm});
            skLineSegment(sketch, "E247.MirrorCS", {"start": v(242.5, -67) * mm, "end": v(254.5, -79) * mm});
            skLineSegment(sketch, "E248.MirrorCS", {"start": v(242.5, -153) * mm, "end": v(254.5, -141) * mm});
            skLineSegment(sketch, "E249.MirrorCS", {"start": v(-127.5, 9) * mm, "end": v(-127.5, -21) * mm});
            skLineSegment(sketch, "E250.MirrorCS", {"start": v(-131, 9) * mm, "end": v(-131, -21) * mm});
            skPoint(sketch, "E251.MirrorP", {"position": v(-131, -67) * mm});
            skLineSegment(sketch, "E252.MirrorCS", {"start": v(-131, -141) * mm, "end": v(-131, -111) * mm});
            skLineSegment(sketch, "E253.MirrorCS", {"start": v(-256, -141) * mm, "end": v(-256, -111) * mm});
            skLineSegment(sketch, "E254.MirrorCS", {"start": v(-244, -67) * mm, "end": v(-143, -67) * mm});
            skLineSegment(sketch, "E255.MirrorCS", {"start": v(-244, -153) * mm, "end": v(-143, -153) * mm});
            skLineSegment(sketch, "E256.MirrorCS", {"start": v(-14.5, -153) * mm, "end": v(-115.5, -153) * mm});
            skLineSegment(sketch, "E257.MirrorCS", {"start": v(-256, -111) * mm, "end": v(-131, -111) * mm});
            skLineSegment(sketch, "E258.MirrorCS", {"start": v(126, -141) * mm, "end": v(126, -111) * mm});
            skLineSegment(sketch, "E259.MirrorCS", {"start": v(-244, -65) * mm, "end": v(-256, -53) * mm});
            skLineSegment(sketch, "E260.MirrorCS", {"start": v(-131, -23) * mm, "end": v(-131, -53) * mm});
            skLineSegment(sketch, "E261.MirrorCS", {"start": v(-2.5, 9) * mm, "end": v(-2.5, -21) * mm});
            skLineSegment(sketch, "E262.MirrorCS", {"start": v(1, -141) * mm, "end": v(1, -111) * mm});
            skLineSegment(sketch, "E263.MirrorCS", {"start": v(13, 21) * mm, "end": v(114, 21) * mm});
            skLineSegment(sketch, "E264.MirrorCS", {"start": v(254.5, -111) * mm, "end": v(129.5, -111) * mm});
            skLineSegment(sketch, "E265.MirrorCS", {"start": v(126, 9) * mm, "end": v(126, -21) * mm});
            skLineSegment(sketch, "E266.MirrorCS", {"start": v(1, -109) * mm, "end": v(1, -79) * mm});
            skLineSegment(sketch, "E267.MirrorCS", {"start": v(1, -109) * mm, "end": v(126, -109) * mm});
            skLineSegment(sketch, "E268.MirrorCS", {"start": v(129.5, -109) * mm, "end": v(129.5, -79) * mm});
            skLineSegment(sketch, "E269.MirrorCS", {"start": v(254.5, -141) * mm, "end": v(254.5, -111) * mm});
            skLineSegment(sketch, "E270.MirrorCS", {"start": v(-14.5, -65) * mm, "end": v(-115.5, -65) * mm});
            skLineSegment(sketch, "E271.MirrorCS", {"start": v(-14.5, 21) * mm, "end": v(-115.5, 21) * mm});
            skLineSegment(sketch, "E272.MirrorCS", {"start": v(129.5, 9) * mm, "end": v(129.5, -21) * mm});
            skLineSegment(sketch, "E273.MirrorCS", {"start": v(-2.5, -109) * mm, "end": v(-2.5, -79) * mm});
            skPoint(sketch, "E274.MirrorP", {"position": v(-131, 21) * mm});
            skLineSegment(sketch, "E275.MirrorCS", {"start": v(-244, -65) * mm, "end": v(-143, -65) * mm});
            skLineSegment(sketch, "E276.MirrorCS", {"start": v(129.5, -141) * mm, "end": v(129.5, -111) * mm});
            skLineSegment(sketch, "E277.MirrorCS", {"start": v(242.5, 21) * mm, "end": v(141.5, 21) * mm});
            skLineSegment(sketch, "E278.MirrorCS", {"start": v(254.5, -109) * mm, "end": v(254.5, -79) * mm});
            skLineSegment(sketch, "E279.MirrorCS", {"start": v(254.5, -109) * mm, "end": v(129.5, -109) * mm});
            skLineSegment(sketch, "E280.MirrorCS", {"start": v(13, -65) * mm, "end": v(114, -65) * mm});
            skLineSegment(sketch, "E281.MirrorCS", {"start": v(254.5, 9) * mm, "end": v(254.5, -21) * mm});
            skLineSegment(sketch, "E282.MirrorCS", {"start": v(-2.5, -141) * mm, "end": v(-2.5, -111) * mm});
            skLineSegment(sketch, "E283.MirrorCS", {"start": v(-256, -109) * mm, "end": v(-131, -109) * mm});
            skLineSegment(sketch, "E284.MirrorCS", {"start": v(-127.5, -23) * mm, "end": v(-127.5, -53) * mm});
            skPoint(sketch, "E285.MirrorP", {"position": v(-131, -65) * mm});
            skLineSegment(sketch, "E286.MirrorCS", {"start": v(-2.5, -23) * mm, "end": v(-127.5, -23) * mm});
            skLineSegment(sketch, "E287.MirrorCS", {"start": v(-14.5, -67) * mm, "end": v(-115.5, -67) * mm});
            skLineSegment(sketch, "E288.MirrorCS", {"start": v(-131, -109) * mm, "end": v(-131, -79) * mm});
            skLineSegment(sketch, "E289.MirrorCS", {"start": v(1, 9) * mm, "end": v(1, -21) * mm});
            skLineSegment(sketch, "E290.MirrorCS", {"start": v(129.5, -23) * mm, "end": v(129.5, -53) * mm});
            skLineSegment(sketch, "E291.MirrorCS", {"start": v(126, -23) * mm, "end": v(126, -53) * mm});
            skLineSegment(sketch, "E292.MirrorCS", {"start": v(-256, -109) * mm, "end": v(-256, -79) * mm});
            skLineSegment(sketch, "E293.MirrorCS", {"start": v(242.5, -153) * mm, "end": v(141.5, -153) * mm});
            skPoint(sketch, "E294.MirrorP", {"position": v(-131, -153) * mm});
            skLineSegment(sketch, "E295.MirrorCS", {"start": v(254.5, -23) * mm, "end": v(254.5, -53) * mm});
            skLineSegment(sketch, "E296.MirrorCS", {"start": v(-127.5, -141) * mm, "end": v(-127.5, -111) * mm});
            skLineSegment(sketch, "E297.MirrorCS", {"start": v(1, -23) * mm, "end": v(1, -53) * mm});
            skLineSegment(sketch, "E298.MirrorCS", {"start": v(13, -153) * mm, "end": v(114, -153) * mm});
            skLineSegment(sketch, "E299.MirrorCS", {"start": v(-244, 21) * mm, "end": v(-143, 21) * mm});
            skLineSegment(sketch, "E300.MirrorCS", {"start": v(-244, -67) * mm, "end": v(-256, -79) * mm});
            skLineSegment(sketch, "E301.MirrorCS", {"start": v(-2.5, -109) * mm, "end": v(-127.5, -109) * mm});
            skLineSegment(sketch, "E302.MirrorCS", {"start": v(242.5, -65) * mm, "end": v(141.5, -65) * mm});
            skLineSegment(sketch, "E303.MirrorCS", {"start": v(1, -23) * mm, "end": v(126, -23) * mm});
            skLineSegment(sketch, "E304.MirrorCS", {"start": v(254.5, -21) * mm, "end": v(129.5, -21) * mm});
            skLineSegment(sketch, "E305.MirrorCS", {"start": v(254.5, -23) * mm, "end": v(129.5, -23) * mm});
            skLineSegment(sketch, "E306.MirrorCS", {"start": v(-2.5, -111) * mm, "end": v(-127.5, -111) * mm});
            skLineSegment(sketch, "E307.MirrorCS", {"start": v(-256, -23) * mm, "end": v(-131, -23) * mm});
            skLineSegment(sketch, "E308.MirrorCS", {"start": v(-256, -21) * mm, "end": v(-131, -21) * mm});
            skLineSegment(sketch, "E309.MirrorCS", {"start": v(13, -67) * mm, "end": v(114, -67) * mm});
            skLineSegment(sketch, "E310.MirrorCS", {"start": v(-2.5, -21) * mm, "end": v(-127.5, -21) * mm});
            skLineSegment(sketch, "E311.MirrorCS", {"start": v(-127.5, -109) * mm, "end": v(-127.5, -79) * mm});
            skLineSegment(sketch, "E312.MirrorCS", {"start": v(126, -109) * mm, "end": v(126, -79) * mm});
            skLineSegment(sketch, "E313.MirrorCS", {"start": v(-2.5, -23) * mm, "end": v(-2.5, -53) * mm});
            skLineSegment(sketch, "E314.MirrorCS", {"start": v(242.5, -67) * mm, "end": v(141.5, -67) * mm});
            skLineSegment(sketch, "E315.MirrorCS", {"start": v(-244, 21) * mm, "end": v(-256, 9) * mm});
            skLineSegment(sketch, "E316.MirrorCS", {"start": v(-256, 9) * mm, "end": v(-256, -21) * mm});
            skLineSegment(sketch, "E317.MirrorCS", {"start": v(-256, -23) * mm, "end": v(-256, -53) * mm});
            skLineSegment(sketch, "E318.MirrorCS", {"start": v(-282.26, -66) * mm, "end": v(303.4, -66) * mm, "construction": true});
            skLineSegment(sketch, "E319.0", {"start": v(-282.26, -154) * mm, "end": v(303.4, -154) * mm, "construction": true});
            skLineSegment(sketch, "E320.MirrorCS", {"start": v(-256, -167) * mm, "end": v(-256, -197) * mm});
            skLineSegment(sketch, "E321.MirrorCS", {"start": v(-244, -155) * mm, "end": v(-256, -167) * mm});
            skLineSegment(sketch, "E322.MirrorCS", {"start": v(-256, -197) * mm, "end": v(-131, -197) * mm});
            skLineSegment(sketch, "E323.MirrorCS", {"start": v(-244, -155) * mm, "end": v(-143, -155) * mm});
            skLineSegment(sketch, "E324.MirrorCS", {"start": v(-143, -155) * mm, "end": v(-131, -167) * mm});
            skLineSegment(sketch, "E325.MirrorCS", {"start": v(1, -197) * mm, "end": v(126, -197) * mm});
            skLineSegment(sketch, "E326.MirrorCS", {"start": v(1, -167) * mm, "end": v(1, -197) * mm});
            skLineSegment(sketch, "E327.MirrorCS", {"start": v(242.5, -155) * mm, "end": v(254.5, -167) * mm});
            skLineSegment(sketch, "E328.MirrorCS", {"start": v(13, -155) * mm, "end": v(1, -167) * mm});
            skLineSegment(sketch, "E329.MirrorCS", {"start": v(13, -155) * mm, "end": v(114, -155) * mm});
            skLineSegment(sketch, "E330.MirrorCS", {"start": v(254.5, -197) * mm, "end": v(129.5, -197) * mm});
            skLineSegment(sketch, "E331.MirrorCS", {"start": v(114, -155) * mm, "end": v(126, -167) * mm});
            skLineSegment(sketch, "E332.MirrorCS", {"start": v(-2.5, -167) * mm, "end": v(-2.5, -197) * mm});
            skLineSegment(sketch, "E333.MirrorCS", {"start": v(141.5, -155) * mm, "end": v(129.5, -167) * mm});
            skLineSegment(sketch, "E334.MirrorCS", {"start": v(254.5, -167) * mm, "end": v(254.5, -197) * mm});
            skLineSegment(sketch, "E335.MirrorCS", {"start": v(-127.5, -167) * mm, "end": v(-127.5, -197) * mm});
            skLineSegment(sketch, "E336.MirrorCS", {"start": v(-14.5, -155) * mm, "end": v(-2.5, -167) * mm});
            skLineSegment(sketch, "E337.MirrorCS", {"start": v(-131, -167) * mm, "end": v(-131, -197) * mm});
            skLineSegment(sketch, "E338.MirrorCS", {"start": v(-2.5, -197) * mm, "end": v(-127.5, -197) * mm});
            skLineSegment(sketch, "E339.MirrorCS", {"start": v(-115.5, -155) * mm, "end": v(-127.5, -167) * mm});
            skPoint(sketch, "E340.MirrorP", {"position": v(-131, -155) * mm});
            skLineSegment(sketch, "E341.MirrorCS", {"start": v(242.5, -155) * mm, "end": v(141.5, -155) * mm});
            skLineSegment(sketch, "E342.MirrorCS", {"start": v(-14.5, -155) * mm, "end": v(-115.5, -155) * mm});
            skLineSegment(sketch, "E343.MirrorCS", {"start": v(129.5, -167) * mm, "end": v(129.5, -197) * mm});
            skLineSegment(sketch, "E344.MirrorCS", {"start": v(126, -167) * mm, "end": v(126, -197) * mm});
            skPoint(sketch, "E345.MirrorCS.end.orphan", {"position": v(-256, -229) * mm});
            skPoint(sketch, "E345.MirrorCS.start.orphan", {"position": v(-256, -199) * mm});
            skPoint(sketch, "E346.MirrorCS.end.orphan", {"position": v(-127.5, -199) * mm});
            skPoint(sketch, "E346.MirrorCS.start.orphan", {"position": v(-2.5, -199) * mm});
            skPoint(sketch, "E347.MirrorCS.end.orphan", {"position": v(126, -199) * mm});
            skPoint(sketch, "E347.MirrorCS.start.orphan", {"position": v(1, -199) * mm});
            skPoint(sketch, "E348.MirrorCS.end.orphan", {"position": v(129.5, -199) * mm});
            skPoint(sketch, "E348.MirrorCS.start.orphan", {"position": v(254.5, -199) * mm});
            skSolve(sketch);
        }
        {
            var Q0;
            Q0 = qSketchRegion(id + "F23", true);
            extrude(context, id + "F24", {"entities" : qUnion([Q0]), "depth" : .5 * mm});
        }
        {
            var Q0;
            Q0=makeQuery(id+"F24.opExtrude","CAP_FACE",FACE,{"disambiguationData":[OSD([sQuery(id+"F23.wireOp",EDGE,"E116.bottom"),sQuery(id+"F23.wireOp",EDGE,"E116.left"),sQuery(id+"F23.wireOp",EDGE,"E116.right"),sQuery(id+"F23.wireOp",EDGE,"E117"),sQuery(id+"F23.wireOp",EDGE,"E118"),sQuery(id+"F23.wireOp",EDGE,"E123")])],"isStart":false});
            var sketch = newSketch(context, id + "F25", { "sketchPlane" : qUnion([Q0])});
            skLineSegment(sketch, "E349.0", {"start": v(-244, 197) * mm, "end": v(-143, 197) * mm});
            skLineSegment(sketch, "E350.0", {"start": v(-244, 197) * mm, "end": v(-256, 185) * mm});
            skLineSegment(sketch, "E351.0", {"start": v(-256, 185) * mm, "end": v(-256, 155) * mm});
            skLineSegment(sketch, "E352.0", {"start": v(-143, 197) * mm, "end": v(-131, 185) * mm});
            skLineSegment(sketch, "E353.0", {"start": v(-131, 185) * mm, "end": v(-131, 155) * mm});
            skLineSegment(sketch, "E354.0", {"start": v(-255.8, 155) * mm, "end": v(-255.75, 155) * mm});
            skLineSegment(sketch, "E355.0", {"start": v(-243.92, 196.8) * mm, "end": v(-246.02, 194.7) * mm});
            skLineSegment(sketch, "E356.0", {"start": v(-243.92, 196.8) * mm, "end": v(-143.08, 196.8) * mm});
            skLineSegment(sketch, "E357.0", {"start": v(-255.8, 184.7) * mm, "end": v(-255.8, 182.7) * mm});
            skLineSegment(sketch, "E358.0", {"start": v(-131.2, 184.92) * mm, "end": v(-131.2, 184.7) * mm});
            skLineSegment(sketch, "E358.1", {"start": v(-143.08, 196.8) * mm, "end": v(-138.98, 192.7) * mm});
            skLineSegment(sketch, "E359.0", {"start": v(-255.75, 184.7) * mm, "end": v(-255.75, 182.75) * mm});
            skLineSegment(sketch, "E360.0", {"start": v(-243.9, 196.75) * mm, "end": v(-143.1, 196.75) * mm});
            skLineSegment(sketch, "E361.trimOffspring", {"start": v(-243.9, 196.75) * mm, "end": v(-245.9, 194.75) * mm});
            skLineSegment(sketch, "E362.0", {"start": v(-143.1, 196.75) * mm, "end": v(-141.1, 194.75) * mm});
            skLineSegment(sketch, "E363.0", {"start": v(-131.25, 184.9) * mm, "end": v(-131.25, 184.75) * mm});
            skLineSegment(sketch, "E364", {"start": v(-245.9, 194.75) * mm, "end": v(-141.1, 194.75) * mm});
            skLineSegment(sketch, "E365.0", {"start": v(-246.02, 194.7) * mm, "end": v(-141.05, 194.7) * mm});
            skLineSegment(sketch, "E366.0", {"start": v(-247.97, 192.75) * mm, "end": v(-139.1, 192.75) * mm});
            skLineSegment(sketch, "E367.1.0.0", {"start": v(-249.9, 190.75) * mm, "end": v(-137.03, 190.75) * mm});
            skLineSegment(sketch, "E367.1.0.1", {"start": v(-250.02, 190.7) * mm, "end": v(-137.05, 190.7) * mm});
            skLineSegment(sketch, "E367.2.0.0", {"start": v(-251.97, 188.75) * mm, "end": v(-135.1, 188.75) * mm});
            skLineSegment(sketch, "E367.2.0.1", {"start": v(-251.95, 188.7) * mm, "end": v(-134.98, 188.7) * mm});
            skLineSegment(sketch, "E367.3.0.0", {"start": v(-253.9, 186.75) * mm, "end": v(-133.03, 186.75) * mm});
            skLineSegment(sketch, "E367.3.0.1", {"start": v(-254.02, 186.7) * mm, "end": v(-133.05, 186.7) * mm});
            skLineSegment(sketch, "E367.4.0.0", {"start": v(-255.75, 184.75) * mm, "end": v(-131.25, 184.75) * mm});
            skLineSegment(sketch, "E367.4.0.1", {"start": v(-255.75, 184.7) * mm, "end": v(-131.2, 184.7) * mm});
            skLineSegment(sketch, "E367.5.0.0", {"start": v(-255.75, 182.75) * mm, "end": v(-131.2, 182.75) * mm});
            skLineSegment(sketch, "E367.5.0.1", {"start": v(-255.8, 182.7) * mm, "end": v(-131.25, 182.7) * mm});
            skLineSegment(sketch, "E367.6.0.0", {"start": v(-255.8, 180.75) * mm, "end": v(-131.25, 180.75) * mm});
            skLineSegment(sketch, "E367.6.0.1", {"start": v(-255.75, 180.7) * mm, "end": v(-131.2, 180.7) * mm});
            skLineSegment(sketch, "E367.7.0.0", {"start": v(-255.75, 178.75) * mm, "end": v(-131.2, 178.75) * mm});
            skLineSegment(sketch, "E367.7.0.1", {"start": v(-255.8, 178.7) * mm, "end": v(-131.25, 178.7) * mm});
            skLineSegment(sketch, "E367.8.0.0", {"start": v(-255.8, 176.75) * mm, "end": v(-131.25, 176.75) * mm});
            skLineSegment(sketch, "E367.8.0.1", {"start": v(-255.75, 176.7) * mm, "end": v(-131.2, 176.7) * mm});
            skLineSegment(sketch, "E367.9.0.0", {"start": v(-255.75, 174.75) * mm, "end": v(-131.2, 174.75) * mm});
            skLineSegment(sketch, "E367.9.0.1", {"start": v(-255.8, 174.7) * mm, "end": v(-131.25, 174.7) * mm});
            skLineSegment(sketch, "E367.10.0.0", {"start": v(-255.8, 172.75) * mm, "end": v(-131.25, 172.75) * mm});
            skLineSegment(sketch, "E367.10.0.1", {"start": v(-255.75, 172.7) * mm, "end": v(-131.2, 172.7) * mm});
            skLineSegment(sketch, "E367.11.0.0", {"start": v(-255.75, 170.75) * mm, "end": v(-131.2, 170.75) * mm});
            skLineSegment(sketch, "E367.11.0.1", {"start": v(-255.8, 170.7) * mm, "end": v(-131.25, 170.7) * mm});
            skLineSegment(sketch, "E367.12.0.0", {"start": v(-255.8, 168.75) * mm, "end": v(-131.25, 168.75) * mm});
            skLineSegment(sketch, "E367.12.0.1", {"start": v(-255.75, 168.7) * mm, "end": v(-131.2, 168.7) * mm});
            skLineSegment(sketch, "E367.13.0.0", {"start": v(-255.75, 166.75) * mm, "end": v(-131.2, 166.75) * mm});
            skLineSegment(sketch, "E367.13.0.1", {"start": v(-255.8, 166.7) * mm, "end": v(-131.25, 166.7) * mm});
            skLineSegment(sketch, "E367.14.0.0", {"start": v(-255.8, 164.75) * mm, "end": v(-131.25, 164.75) * mm});
            skLineSegment(sketch, "E367.14.0.1", {"start": v(-255.75, 164.7) * mm, "end": v(-131.2, 164.7) * mm});
            skLineSegment(sketch, "E367.15.0.0", {"start": v(-255.75, 162.75) * mm, "end": v(-131.2, 162.75) * mm});
            skLineSegment(sketch, "E367.15.0.1", {"start": v(-255.8, 162.7) * mm, "end": v(-131.25, 162.7) * mm});
            skLineSegment(sketch, "E367.16.0.0", {"start": v(-255.8, 160.75) * mm, "end": v(-131.25, 160.75) * mm});
            skLineSegment(sketch, "E367.16.0.1", {"start": v(-255.75, 160.7) * mm, "end": v(-131.25, 160.7) * mm});
            skLineSegment(sketch, "E367.17.0.0", {"start": v(-255.75, 158.75) * mm, "end": v(-131.2, 158.75) * mm});
            skLineSegment(sketch, "E367.17.0.1", {"start": v(-255.8, 158.7) * mm, "end": v(-131.25, 158.7) * mm});
            skLineSegment(sketch, "E367.18.0.0", {"start": v(-255.8, 156.75) * mm, "end": v(-131.25, 156.75) * mm});
            skLineSegment(sketch, "E367.18.0.1", {"start": v(-255.75, 156.7) * mm, "end": v(-131.2, 156.7) * mm});
            skLineSegment(sketch, "E368.trimOffspring", {"start": v(-247.95, 192.7) * mm, "end": v(-138.98, 192.7) * mm});
            skLineSegment(sketch, "E369.trimOffspring", {"start": v(-141.05, 194.7) * mm, "end": v(-139.1, 192.75) * mm});
            skLineSegment(sketch, "E370.trimOffspring", {"start": v(-137.05, 190.7) * mm, "end": v(-135.1, 188.75) * mm});
            skLineSegment(sketch, "E371.trimOffspring", {"start": v(-137.03, 190.75) * mm, "end": v(-134.98, 188.7) * mm});
            skLineSegment(sketch, "E372.trimOffspring", {"start": v(-133.05, 186.7) * mm, "end": v(-131.25, 184.9) * mm});
            skLineSegment(sketch, "E373.trimOffspring", {"start": v(-133.03, 186.75) * mm, "end": v(-131.2, 184.92) * mm});
            skLineSegment(sketch, "E374.trimOffspring", {"start": v(-131.2, 182.75) * mm, "end": v(-131.2, 180.7) * mm});
            skLineSegment(sketch, "E375.trimOffspring", {"start": v(-131.25, 182.7) * mm, "end": v(-131.25, 180.75) * mm});
            skLineSegment(sketch, "E376.trimOffspring", {"start": v(-131.2, 178.75) * mm, "end": v(-131.2, 176.7) * mm});
            skLineSegment(sketch, "E377.trimOffspring", {"start": v(-131.25, 178.7) * mm, "end": v(-131.25, 176.75) * mm});
            skLineSegment(sketch, "E378.trimOffspring", {"start": v(-131.2, 174.75) * mm, "end": v(-131.2, 172.7) * mm});
            skLineSegment(sketch, "E379.trimOffspring", {"start": v(-131.25, 174.7) * mm, "end": v(-131.25, 172.75) * mm});
            skLineSegment(sketch, "E380.trimOffspring", {"start": v(-131.25, 170.7) * mm, "end": v(-131.25, 168.75) * mm});
            skLineSegment(sketch, "E381.trimOffspring", {"start": v(-131.2, 170.75) * mm, "end": v(-131.2, 168.7) * mm});
            skLineSegment(sketch, "E382.trimOffspring", {"start": v(-131.2, 166.75) * mm, "end": v(-131.2, 164.7) * mm});
            skLineSegment(sketch, "E383.trimOffspring", {"start": v(-131.25, 166.7) * mm, "end": v(-131.25, 164.75) * mm});
            skLineSegment(sketch, "E384.trimOffspring", {"start": v(-131.2, 162.75) * mm, "end": v(-131.2, 160.75) * mm});
            skLineSegment(sketch, "E385.trimOffspring", {"start": v(-131.25, 162.7) * mm, "end": v(-131.25, 160.75) * mm});
            skLineSegment(sketch, "E386.trimOffspring", {"start": v(-131.25, 158.7) * mm, "end": v(-131.25, 156.75) * mm});
            skLineSegment(sketch, "E387.trimOffspring", {"start": v(-131.2, 158.75) * mm, "end": v(-131.2, 156.7) * mm});
            skLineSegment(sketch, "E388", {"start": v(-131.2, 160.75) * mm, "end": v(-131.2, 160.7) * mm});
            skLineSegment(sketch, "E389", {"start": v(-131.2, 160.7) * mm, "end": v(-131.25, 160.7) * mm});
            skLineSegment(sketch, "E390.trimOffspring", {"start": v(-255.75, 156.7) * mm, "end": v(-255.75, 155) * mm});
            skLineSegment(sketch, "E391.trimOffspring", {"start": v(-255.8, 156.75) * mm, "end": v(-255.8, 155) * mm});
            skLineSegment(sketch, "E392.trimOffspring", {"start": v(-255.75, 160.7) * mm, "end": v(-255.75, 158.75) * mm});
            skLineSegment(sketch, "E393.trimOffspring", {"start": v(-255.8, 160.75) * mm, "end": v(-255.8, 158.7) * mm});
            skLineSegment(sketch, "E394.trimOffspring", {"start": v(-255.75, 164.7) * mm, "end": v(-255.75, 162.75) * mm});
            skLineSegment(sketch, "E395.trimOffspring", {"start": v(-255.8, 164.75) * mm, "end": v(-255.8, 162.75) * mm});
            skLineSegment(sketch, "E396.trimOffspring", {"start": v(-255.8, 168.75) * mm, "end": v(-255.8, 166.75) * mm});
            skLineSegment(sketch, "E397.trimOffspring", {"start": v(-255.75, 168.7) * mm, "end": v(-255.75, 166.75) * mm});
            skLineSegment(sketch, "E398.trimOffspring", {"start": v(-255.75, 172.7) * mm, "end": v(-255.75, 170.75) * mm});
            skLineSegment(sketch, "E399.trimOffspring", {"start": v(-255.8, 172.75) * mm, "end": v(-255.8, 170.7) * mm});
            skLineSegment(sketch, "E400.trimOffspring", {"start": v(-255.75, 176.7) * mm, "end": v(-255.75, 174.7) * mm});
            skLineSegment(sketch, "E401.trimOffspring", {"start": v(-255.8, 176.75) * mm, "end": v(-255.8, 174.7) * mm});
            skLineSegment(sketch, "E402.trimOffspring", {"start": v(-255.75, 180.7) * mm, "end": v(-255.75, 178.75) * mm});
            skLineSegment(sketch, "E403.trimOffspring", {"start": v(-255.8, 180.75) * mm, "end": v(-255.8, 178.75) * mm});
            skLineSegment(sketch, "E404", {"start": v(-255.8, 184.7) * mm, "end": v(-255.8, 184.75) * mm});
            skLineSegment(sketch, "E405", {"start": v(-255.8, 184.75) * mm, "end": v(-255.75, 184.75) * mm});
            skLineSegment(sketch, "E406.trimOffspring", {"start": v(-251.97, 188.75) * mm, "end": v(-254.02, 186.7) * mm});
            skLineSegment(sketch, "E407.trimOffspring", {"start": v(-251.95, 188.7) * mm, "end": v(-253.9, 186.75) * mm});
            skLineSegment(sketch, "E408.trimOffspring", {"start": v(-247.95, 192.7) * mm, "end": v(-249.9, 190.75) * mm});
            skLineSegment(sketch, "E409.trimOffspring", {"start": v(-247.97, 192.75) * mm, "end": v(-250.02, 190.7) * mm});
            skLineSegment(sketch, "E410", {"start": v(-255.8, 166.75) * mm, "end": v(-255.8, 166.7) * mm});
            skLineSegment(sketch, "E411", {"start": v(-255.8, 162.75) * mm, "end": v(-255.8, 162.7) * mm});
            skLineSegment(sketch, "E412", {"start": v(-255.8, 178.75) * mm, "end": v(-255.8, 178.7) * mm});
            skLineSegment(sketch, "E413.0.1.0", {"start": v(-255.75, 96.7) * mm, "end": v(-131.2, 96.7) * mm});
            skLineSegment(sketch, "E413.0.1.1", {"start": v(-255.8, 82.7) * mm, "end": v(-131.25, 82.7) * mm});
            skLineSegment(sketch, "E413.0.1.2", {"start": v(-255.8, 94.7) * mm, "end": v(-131.25, 94.7) * mm});
            skLineSegment(sketch, "E413.0.1.3", {"start": v(-255.75, 80.7) * mm, "end": v(-131.2, 80.7) * mm});
            skLineSegment(sketch, "E413.0.1.4", {"start": v(-255.8, 78.7) * mm, "end": v(-131.25, 78.7) * mm});
            skLineSegment(sketch, "E413.0.1.5", {"start": v(-254.02, 98.7) * mm, "end": v(-133.05, 98.7) * mm});
            skLineSegment(sketch, "E413.0.1.6", {"start": v(-255.75, 92.7) * mm, "end": v(-131.2, 92.7) * mm});
            skLineSegment(sketch, "E413.0.1.7", {"start": v(-246.02, 106.7) * mm, "end": v(-141.05, 106.7) * mm});
            skLineSegment(sketch, "E413.0.1.8", {"start": v(-255.75, 72.7) * mm, "end": v(-131.25, 72.7) * mm});
            skLineSegment(sketch, "E413.0.1.9", {"start": v(-251.95, 100.7) * mm, "end": v(-134.98, 100.7) * mm});
            skLineSegment(sketch, "E413.0.1.10", {"start": v(-247.95, 104.7) * mm, "end": v(-138.98, 104.7) * mm});
            skLineSegment(sketch, "E413.0.1.11", {"start": v(-255.75, 76.7) * mm, "end": v(-131.2, 76.7) * mm});
            skLineSegment(sketch, "E413.0.1.12", {"start": v(-255.8, 74.7) * mm, "end": v(-131.25, 74.7) * mm});
            skLineSegment(sketch, "E413.0.1.13", {"start": v(-255.8, 90.7) * mm, "end": v(-131.25, 90.7) * mm});
            skLineSegment(sketch, "E413.0.1.14", {"start": v(-255.75, 88.7) * mm, "end": v(-131.2, 88.7) * mm});
            skLineSegment(sketch, "E413.0.1.15", {"start": v(-255.8, 86.7) * mm, "end": v(-131.25, 86.7) * mm});
            skLineSegment(sketch, "E413.0.1.16", {"start": v(-255.8, 70.7) * mm, "end": v(-131.25, 70.7) * mm});
            skLineSegment(sketch, "E413.0.1.17", {"start": v(-250.02, 102.7) * mm, "end": v(-137.05, 102.7) * mm});
            skLineSegment(sketch, "E413.0.1.18", {"start": v(-255.75, 68.7) * mm, "end": v(-131.2, 68.7) * mm});
            skLineSegment(sketch, "E413.0.1.19", {"start": v(-255.75, 84.7) * mm, "end": v(-131.2, 84.7) * mm});
            skLineSegment(sketch, "E413.0.1.20", {"start": v(-243.9, 108.75) * mm, "end": v(-143.1, 108.75) * mm});
            skLineSegment(sketch, "E413.0.1.21", {"start": v(-255.75, 82.75) * mm, "end": v(-131.2, 82.75) * mm});
            skLineSegment(sketch, "E413.0.1.22", {"start": v(-255.8, 80.75) * mm, "end": v(-131.25, 80.75) * mm});
            skLineSegment(sketch, "E413.0.1.23", {"start": v(-255.75, 78.75) * mm, "end": v(-131.2, 78.75) * mm});
            skLineSegment(sketch, "E413.0.1.24", {"start": v(-255.75, 96.75) * mm, "end": v(-131.25, 96.75) * mm});
            skLineSegment(sketch, "E413.0.1.25", {"start": v(-255.75, 94.75) * mm, "end": v(-131.2, 94.75) * mm});
            skLineSegment(sketch, "E413.0.1.26", {"start": v(-255.8, 92.75) * mm, "end": v(-131.25, 92.75) * mm});
            skLineSegment(sketch, "E413.0.1.27", {"start": v(-255.8, 72.75) * mm, "end": v(-131.25, 72.75) * mm});
            skLineSegment(sketch, "E413.0.1.28", {"start": v(-255.8, 88.75) * mm, "end": v(-131.25, 88.75) * mm});
            skLineSegment(sketch, "E413.0.1.29", {"start": v(-249.9, 102.75) * mm, "end": v(-137.03, 102.75) * mm});
            skLineSegment(sketch, "E413.0.1.30", {"start": v(-255.75, 86.75) * mm, "end": v(-131.2, 86.75) * mm});
            skLineSegment(sketch, "E413.0.1.31", {"start": v(-255.8, 68.75) * mm, "end": v(-131.25, 68.75) * mm});
            skLineSegment(sketch, "E413.0.1.32", {"start": v(-253.9, 98.75) * mm, "end": v(-133.03, 98.75) * mm});
            skLineSegment(sketch, "E413.0.1.33", {"start": v(-255.8, 76.75) * mm, "end": v(-131.25, 76.75) * mm});
            skLineSegment(sketch, "E413.0.1.34", {"start": v(-255.75, 90.75) * mm, "end": v(-131.2, 90.75) * mm});
            skLineSegment(sketch, "E413.0.1.35", {"start": v(-255.75, 74.75) * mm, "end": v(-131.2, 74.75) * mm});
            skLineSegment(sketch, "E413.0.1.36", {"start": v(-245.9, 106.75) * mm, "end": v(-141.1, 106.75) * mm});
            skLineSegment(sketch, "E413.0.1.37", {"start": v(-255.75, 70.75) * mm, "end": v(-131.2, 70.75) * mm});
            skLineSegment(sketch, "E413.0.1.38", {"start": v(-247.97, 104.75) * mm, "end": v(-139.1, 104.75) * mm});
            skLineSegment(sketch, "E413.0.1.39", {"start": v(-243.92, 108.8) * mm, "end": v(-143.08, 108.8) * mm});
            skLineSegment(sketch, "E413.0.1.40", {"start": v(-131, 97) * mm, "end": v(-131, 67) * mm});
            skLineSegment(sketch, "E413.0.1.41", {"start": v(-251.97, 100.75) * mm, "end": v(-135.1, 100.75) * mm});
            skLineSegment(sketch, "E413.0.1.42", {"start": v(-255.8, 84.75) * mm, "end": v(-131.25, 84.75) * mm});
            skLineSegment(sketch, "E413.0.1.43", {"start": v(-137.03, 102.75) * mm, "end": v(-134.98, 100.7) * mm});
            skLineSegment(sketch, "E413.0.1.44", {"start": v(-137.05, 102.7) * mm, "end": v(-135.1, 100.75) * mm});
            skLineSegment(sketch, "E413.0.1.45", {"start": v(-247.97, 104.75) * mm, "end": v(-250.02, 102.7) * mm});
            skLineSegment(sketch, "E413.0.1.46", {"start": v(-244, 109) * mm, "end": v(-256, 97) * mm});
            skLineSegment(sketch, "E413.0.1.47", {"start": v(-244, 109) * mm, "end": v(-143, 109) * mm});
            skLineSegment(sketch, "E413.0.1.48", {"start": v(-143, 109) * mm, "end": v(-131, 97) * mm});
            skLineSegment(sketch, "E413.0.1.49", {"start": v(-247.95, 104.7) * mm, "end": v(-249.9, 102.75) * mm});
            skLineSegment(sketch, "E413.0.1.50", {"start": v(-255.8, 92.75) * mm, "end": v(-255.8, 90.75) * mm});
            skLineSegment(sketch, "E413.0.1.51", {"start": v(-251.97, 100.75) * mm, "end": v(-254.02, 98.7) * mm});
            skLineSegment(sketch, "E413.0.1.52", {"start": v(-141.05, 106.7) * mm, "end": v(-139.1, 104.75) * mm});
            skLineSegment(sketch, "E413.0.1.53", {"start": v(-255.8, 88.75) * mm, "end": v(-255.8, 86.7) * mm});
            skLineSegment(sketch, "E413.0.1.54", {"start": v(-133.03, 98.75) * mm, "end": v(-131.2, 96.92) * mm});
            skLineSegment(sketch, "E413.0.1.55", {"start": v(-131.2, 70.75) * mm, "end": v(-131.2, 68.7) * mm});
            skLineSegment(sketch, "E413.0.1.56", {"start": v(-131.25, 74.7) * mm, "end": v(-131.25, 72.75) * mm});
            skLineSegment(sketch, "E413.0.1.57", {"start": v(-133.05, 98.7) * mm, "end": v(-131.25, 96.9) * mm});
            skLineSegment(sketch, "E413.0.1.58", {"start": v(-251.95, 100.7) * mm, "end": v(-253.9, 98.75) * mm});
            skLineSegment(sketch, "E413.0.1.59", {"start": v(-131.25, 94.7) * mm, "end": v(-131.25, 92.75) * mm});
            skLineSegment(sketch, "E413.0.1.60", {"start": v(-255.8, 68.75) * mm, "end": v(-255.8, 67) * mm});
            skLineSegment(sketch, "E413.0.1.61", {"start": v(-255.8, 72.75) * mm, "end": v(-255.8, 70.7) * mm});
            skLineSegment(sketch, "E413.0.1.62", {"start": v(-131.25, 86.7) * mm, "end": v(-131.25, 84.75) * mm});
            skLineSegment(sketch, "E413.0.1.63", {"start": v(-243.92, 108.8) * mm, "end": v(-246.02, 106.7) * mm});
            skLineSegment(sketch, "E413.0.1.64", {"start": v(-143.08, 108.8) * mm, "end": v(-138.98, 104.7) * mm});
            skLineSegment(sketch, "E413.0.1.65", {"start": v(-131.25, 78.7) * mm, "end": v(-131.25, 76.75) * mm});
            skLineSegment(sketch, "E413.0.1.66", {"start": v(-255.8, 84.75) * mm, "end": v(-255.8, 82.7) * mm});
            skLineSegment(sketch, "E413.0.1.67", {"start": v(-131.25, 90.7) * mm, "end": v(-131.25, 88.75) * mm});
            skLineSegment(sketch, "E413.0.1.68", {"start": v(-131.25, 82.7) * mm, "end": v(-131.25, 80.75) * mm});
            skLineSegment(sketch, "E413.0.1.69", {"start": v(-255.8, 76.75) * mm, "end": v(-255.8, 74.75) * mm});
            skLineSegment(sketch, "E413.0.1.70", {"start": v(-131.2, 82.75) * mm, "end": v(-131.2, 80.7) * mm});
            skLineSegment(sketch, "E413.0.1.71", {"start": v(-255.8, 67) * mm, "end": v(-255.75, 67) * mm});
            skLineSegment(sketch, "E413.0.1.72", {"start": v(-256, 97) * mm, "end": v(-256, 67) * mm});
            skLineSegment(sketch, "E413.0.1.73", {"start": v(-255.75, 96.7) * mm, "end": v(-255.75, 94.75) * mm});
            skLineSegment(sketch, "E413.0.1.74", {"start": v(-131.25, 70.7) * mm, "end": v(-131.25, 68.75) * mm});
            skLineSegment(sketch, "E413.0.1.75", {"start": v(-255.75, 92.7) * mm, "end": v(-255.75, 90.75) * mm});
            skLineSegment(sketch, "E413.0.1.76", {"start": v(-131.2, 74.75) * mm, "end": v(-131.2, 72.75) * mm});
            skLineSegment(sketch, "E413.0.1.77", {"start": v(-255.75, 88.7) * mm, "end": v(-255.75, 86.7) * mm});
            skLineSegment(sketch, "E413.0.1.78", {"start": v(-255.75, 68.7) * mm, "end": v(-255.75, 67) * mm});
            skLineSegment(sketch, "E413.0.1.79", {"start": v(-131.2, 90.75) * mm, "end": v(-131.2, 88.7) * mm});
            skLineSegment(sketch, "E413.0.1.80", {"start": v(-255.75, 76.7) * mm, "end": v(-255.75, 74.75) * mm});
            skLineSegment(sketch, "E413.0.1.81", {"start": v(-131.2, 86.75) * mm, "end": v(-131.2, 84.7) * mm});
            skLineSegment(sketch, "E413.0.1.82", {"start": v(-143.1, 108.75) * mm, "end": v(-141.1, 106.75) * mm});
            skLineSegment(sketch, "E413.0.1.83", {"start": v(-255.75, 84.7) * mm, "end": v(-255.75, 82.75) * mm});
            skLineSegment(sketch, "E413.0.1.84", {"start": v(-131.2, 94.75) * mm, "end": v(-131.2, 92.7) * mm});
            skLineSegment(sketch, "E413.0.1.85", {"start": v(-255.75, 72.7) * mm, "end": v(-255.75, 70.75) * mm});
            skLineSegment(sketch, "E413.0.1.86", {"start": v(-255.8, 80.75) * mm, "end": v(-255.8, 78.75) * mm});
            skLineSegment(sketch, "E413.0.1.87", {"start": v(-255.8, 96.7) * mm, "end": v(-255.8, 94.7) * mm});
            skLineSegment(sketch, "E413.0.1.88", {"start": v(-243.9, 108.75) * mm, "end": v(-245.9, 106.75) * mm});
            skLineSegment(sketch, "E413.0.1.89", {"start": v(-131.2, 78.75) * mm, "end": v(-131.2, 76.7) * mm});
            skLineSegment(sketch, "E413.0.1.90", {"start": v(-255.8, 74.75) * mm, "end": v(-255.8, 74.7) * mm});
            skLineSegment(sketch, "E413.0.1.91", {"start": v(-255.8, 90.75) * mm, "end": v(-255.8, 90.7) * mm});
            skLineSegment(sketch, "E413.0.1.92", {"start": v(-255.75, 80.7) * mm, "end": v(-255.75, 78.75) * mm});
            skLineSegment(sketch, "E413.0.1.93", {"start": v(-255.8, 78.75) * mm, "end": v(-255.8, 78.7) * mm});
            skLineSegment(sketch, "E413.0.1.94", {"start": v(-131.2, 96.92) * mm, "end": v(-131.2, 96.7) * mm});
            skLineSegment(sketch, "E413.0.1.95", {"start": v(-255.8, 96.75) * mm, "end": v(-255.75, 96.75) * mm});
            skLineSegment(sketch, "E413.0.1.96", {"start": v(-131.2, 72.7) * mm, "end": v(-131.25, 72.7) * mm});
            skLineSegment(sketch, "E413.0.1.97", {"start": v(-131.25, 96.9) * mm, "end": v(-131.25, 96.75) * mm});
            skLineSegment(sketch, "E413.0.1.98", {"start": v(-255.8, 96.7) * mm, "end": v(-255.8, 96.75) * mm});
            skLineSegment(sketch, "E413.0.1.99", {"start": v(-131.2, 72.75) * mm, "end": v(-131.2, 72.7) * mm});
            skLineSegment(sketch, "E413.0.2.0", {"start": v(-255.75, 8.7) * mm, "end": v(-131.2, 8.7) * mm});
            skLineSegment(sketch, "E413.0.2.1", {"start": v(-255.8, -5.3) * mm, "end": v(-131.25, -5.3) * mm});
            skLineSegment(sketch, "E413.0.2.2", {"start": v(-255.8, 6.7) * mm, "end": v(-131.25, 6.7) * mm});
            skLineSegment(sketch, "E413.0.2.3", {"start": v(-255.75, -7.3) * mm, "end": v(-131.2, -7.3) * mm});
            skLineSegment(sketch, "E413.0.2.4", {"start": v(-255.8, -9.3) * mm, "end": v(-131.25, -9.3) * mm});
            skLineSegment(sketch, "E413.0.2.5", {"start": v(-254.02, 10.7) * mm, "end": v(-133.05, 10.7) * mm});
            skLineSegment(sketch, "E413.0.2.6", {"start": v(-255.75, 4.7) * mm, "end": v(-131.2, 4.7) * mm});
            skLineSegment(sketch, "E413.0.2.7", {"start": v(-246.02, 18.7) * mm, "end": v(-141.05, 18.7) * mm});
            skLineSegment(sketch, "E413.0.2.8", {"start": v(-255.75, -15.3) * mm, "end": v(-131.25, -15.3) * mm});
            skLineSegment(sketch, "E413.0.2.9", {"start": v(-251.95, 12.7) * mm, "end": v(-134.98, 12.7) * mm});
            skLineSegment(sketch, "E413.0.2.10", {"start": v(-247.95, 16.7) * mm, "end": v(-138.98, 16.7) * mm});
            skLineSegment(sketch, "E413.0.2.11", {"start": v(-255.75, -11.3) * mm, "end": v(-131.2, -11.3) * mm});
            skLineSegment(sketch, "E413.0.2.12", {"start": v(-255.8, -13.3) * mm, "end": v(-131.25, -13.3) * mm});
            skLineSegment(sketch, "E413.0.2.13", {"start": v(-255.8, 2.7) * mm, "end": v(-131.25, 2.7) * mm});
            skLineSegment(sketch, "E413.0.2.14", {"start": v(-255.75, 0.7) * mm, "end": v(-131.2, 0.7) * mm});
            skLineSegment(sketch, "E413.0.2.15", {"start": v(-255.8, -1.3) * mm, "end": v(-131.25, -1.3) * mm});
            skLineSegment(sketch, "E413.0.2.16", {"start": v(-255.8, -17.3) * mm, "end": v(-131.25, -17.3) * mm});
            skLineSegment(sketch, "E413.0.2.17", {"start": v(-250.02, 14.7) * mm, "end": v(-137.05, 14.7) * mm});
            skLineSegment(sketch, "E413.0.2.18", {"start": v(-255.75, -19.3) * mm, "end": v(-131.2, -19.3) * mm});
            skLineSegment(sketch, "E413.0.2.19", {"start": v(-255.75, -3.3) * mm, "end": v(-131.2, -3.3) * mm});
            skLineSegment(sketch, "E413.0.2.20", {"start": v(-243.9, 20.75) * mm, "end": v(-143.1, 20.75) * mm});
            skLineSegment(sketch, "E413.0.2.21", {"start": v(-255.75, -5.25) * mm, "end": v(-131.2, -5.25) * mm});
            skLineSegment(sketch, "E413.0.2.22", {"start": v(-255.8, -7.25) * mm, "end": v(-131.25, -7.25) * mm});
            skLineSegment(sketch, "E413.0.2.23", {"start": v(-255.75, -9.25) * mm, "end": v(-131.2, -9.25) * mm});
            skLineSegment(sketch, "E413.0.2.24", {"start": v(-255.75, 8.75) * mm, "end": v(-131.25, 8.75) * mm});
            skLineSegment(sketch, "E413.0.2.25", {"start": v(-255.75, 6.75) * mm, "end": v(-131.2, 6.75) * mm});
            skLineSegment(sketch, "E413.0.2.26", {"start": v(-255.8, 4.75) * mm, "end": v(-131.25, 4.75) * mm});
            skLineSegment(sketch, "E413.0.2.27", {"start": v(-255.8, -15.25) * mm, "end": v(-131.25, -15.25) * mm});
            skLineSegment(sketch, "E413.0.2.28", {"start": v(-255.8, 0.75) * mm, "end": v(-131.25, 0.75) * mm});
            skLineSegment(sketch, "E413.0.2.29", {"start": v(-249.9, 14.75) * mm, "end": v(-137.03, 14.75) * mm});
            skLineSegment(sketch, "E413.0.2.30", {"start": v(-255.75, -1.25) * mm, "end": v(-131.2, -1.25) * mm});
            skLineSegment(sketch, "E413.0.2.31", {"start": v(-255.8, -19.25) * mm, "end": v(-131.25, -19.25) * mm});
            skLineSegment(sketch, "E413.0.2.32", {"start": v(-253.9, 10.75) * mm, "end": v(-133.03, 10.75) * mm});
            skLineSegment(sketch, "E413.0.2.33", {"start": v(-255.8, -11.25) * mm, "end": v(-131.25, -11.25) * mm});
            skLineSegment(sketch, "E413.0.2.34", {"start": v(-255.75, 2.75) * mm, "end": v(-131.2, 2.75) * mm});
            skLineSegment(sketch, "E413.0.2.35", {"start": v(-255.75, -13.25) * mm, "end": v(-131.2, -13.25) * mm});
            skLineSegment(sketch, "E413.0.2.36", {"start": v(-245.9, 18.75) * mm, "end": v(-141.1, 18.75) * mm});
            skLineSegment(sketch, "E413.0.2.37", {"start": v(-255.75, -17.25) * mm, "end": v(-131.2, -17.25) * mm});
            skLineSegment(sketch, "E413.0.2.38", {"start": v(-247.97, 16.75) * mm, "end": v(-139.1, 16.75) * mm});
            skLineSegment(sketch, "E413.0.2.39", {"start": v(-243.92, 20.8) * mm, "end": v(-143.08, 20.8) * mm});
            skLineSegment(sketch, "E413.0.2.40", {"start": v(-131, 9) * mm, "end": v(-131, -21) * mm});
            skLineSegment(sketch, "E413.0.2.41", {"start": v(-251.97, 12.75) * mm, "end": v(-135.1, 12.75) * mm});
            skLineSegment(sketch, "E413.0.2.42", {"start": v(-255.8, -3.25) * mm, "end": v(-131.25, -3.25) * mm});
            skLineSegment(sketch, "E413.0.2.43", {"start": v(-137.03, 14.75) * mm, "end": v(-134.98, 12.7) * mm});
            skLineSegment(sketch, "E413.0.2.44", {"start": v(-137.05, 14.7) * mm, "end": v(-135.1, 12.75) * mm});
            skLineSegment(sketch, "E413.0.2.45", {"start": v(-247.97, 16.75) * mm, "end": v(-250.02, 14.7) * mm});
            skLineSegment(sketch, "E413.0.2.46", {"start": v(-244, 21) * mm, "end": v(-256, 9) * mm});
            skLineSegment(sketch, "E413.0.2.47", {"start": v(-244, 21) * mm, "end": v(-143, 21) * mm});
            skLineSegment(sketch, "E413.0.2.48", {"start": v(-143, 21) * mm, "end": v(-131, 9) * mm});
            skLineSegment(sketch, "E413.0.2.49", {"start": v(-247.95, 16.7) * mm, "end": v(-249.9, 14.75) * mm});
            skLineSegment(sketch, "E413.0.2.50", {"start": v(-255.8, 4.75) * mm, "end": v(-255.8, 2.75) * mm});
            skLineSegment(sketch, "E413.0.2.51", {"start": v(-251.97, 12.75) * mm, "end": v(-254.02, 10.7) * mm});
            skLineSegment(sketch, "E413.0.2.52", {"start": v(-141.05, 18.7) * mm, "end": v(-139.1, 16.75) * mm});
            skLineSegment(sketch, "E413.0.2.53", {"start": v(-255.8, 0.75) * mm, "end": v(-255.8, -1.3) * mm});
            skLineSegment(sketch, "E413.0.2.54", {"start": v(-133.03, 10.75) * mm, "end": v(-131.2, 8.92) * mm});
            skLineSegment(sketch, "E413.0.2.55", {"start": v(-131.2, -17.25) * mm, "end": v(-131.2, -19.3) * mm});
            skLineSegment(sketch, "E413.0.2.56", {"start": v(-131.25, -13.3) * mm, "end": v(-131.25, -15.25) * mm});
            skLineSegment(sketch, "E413.0.2.57", {"start": v(-133.05, 10.7) * mm, "end": v(-131.25, 8.9) * mm});
            skLineSegment(sketch, "E413.0.2.58", {"start": v(-251.95, 12.7) * mm, "end": v(-253.9, 10.75) * mm});
            skLineSegment(sketch, "E413.0.2.59", {"start": v(-131.25, 6.7) * mm, "end": v(-131.25, 4.75) * mm});
            skLineSegment(sketch, "E413.0.2.60", {"start": v(-255.8, -19.25) * mm, "end": v(-255.8, -21) * mm});
            skLineSegment(sketch, "E413.0.2.61", {"start": v(-255.8, -15.25) * mm, "end": v(-255.8, -17.3) * mm});
            skLineSegment(sketch, "E413.0.2.62", {"start": v(-131.25, -1.3) * mm, "end": v(-131.25, -3.25) * mm});
            skLineSegment(sketch, "E413.0.2.63", {"start": v(-243.92, 20.8) * mm, "end": v(-246.02, 18.7) * mm});
            skLineSegment(sketch, "E413.0.2.64", {"start": v(-143.08, 20.8) * mm, "end": v(-138.98, 16.7) * mm});
            skLineSegment(sketch, "E413.0.2.65", {"start": v(-131.25, -9.3) * mm, "end": v(-131.25, -11.25) * mm});
            skLineSegment(sketch, "E413.0.2.66", {"start": v(-255.8, -3.25) * mm, "end": v(-255.8, -5.3) * mm});
            skLineSegment(sketch, "E413.0.2.67", {"start": v(-131.25, 2.7) * mm, "end": v(-131.25, 0.75) * mm});
            skLineSegment(sketch, "E413.0.2.68", {"start": v(-131.25, -5.3) * mm, "end": v(-131.25, -7.25) * mm});
            skLineSegment(sketch, "E413.0.2.69", {"start": v(-255.8, -11.25) * mm, "end": v(-255.8, -13.25) * mm});
            skLineSegment(sketch, "E413.0.2.70", {"start": v(-131.2, -5.25) * mm, "end": v(-131.2, -7.3) * mm});
            skLineSegment(sketch, "E413.0.2.71", {"start": v(-255.8, -21) * mm, "end": v(-255.75, -21) * mm});
            skLineSegment(sketch, "E413.0.2.72", {"start": v(-256, 9) * mm, "end": v(-256, -21) * mm});
            skLineSegment(sketch, "E413.0.2.73", {"start": v(-255.75, 8.7) * mm, "end": v(-255.75, 6.75) * mm});
            skLineSegment(sketch, "E413.0.2.74", {"start": v(-131.25, -17.3) * mm, "end": v(-131.25, -19.25) * mm});
            skLineSegment(sketch, "E413.0.2.75", {"start": v(-255.75, 4.7) * mm, "end": v(-255.75, 2.75) * mm});
            skLineSegment(sketch, "E413.0.2.76", {"start": v(-131.2, -13.25) * mm, "end": v(-131.2, -15.25) * mm});
            skLineSegment(sketch, "E413.0.2.77", {"start": v(-255.75, 0.7) * mm, "end": v(-255.75, -1.3) * mm});
            skLineSegment(sketch, "E413.0.2.78", {"start": v(-255.75, -19.3) * mm, "end": v(-255.75, -21) * mm});
            skLineSegment(sketch, "E413.0.2.79", {"start": v(-131.2, 2.75) * mm, "end": v(-131.2, 0.7) * mm});
            skLineSegment(sketch, "E413.0.2.80", {"start": v(-255.75, -11.3) * mm, "end": v(-255.75, -13.25) * mm});
            skLineSegment(sketch, "E413.0.2.81", {"start": v(-131.2, -1.25) * mm, "end": v(-131.2, -3.3) * mm});
            skLineSegment(sketch, "E413.0.2.82", {"start": v(-143.1, 20.75) * mm, "end": v(-141.1, 18.75) * mm});
            skLineSegment(sketch, "E413.0.2.83", {"start": v(-255.75, -3.3) * mm, "end": v(-255.75, -5.25) * mm});
            skLineSegment(sketch, "E413.0.2.84", {"start": v(-131.2, 6.75) * mm, "end": v(-131.2, 4.7) * mm});
            skLineSegment(sketch, "E413.0.2.85", {"start": v(-255.75, -15.3) * mm, "end": v(-255.75, -17.25) * mm});
            skLineSegment(sketch, "E413.0.2.86", {"start": v(-255.8, -7.25) * mm, "end": v(-255.8, -9.25) * mm});
            skLineSegment(sketch, "E413.0.2.87", {"start": v(-255.8, 8.7) * mm, "end": v(-255.8, 6.7) * mm});
            skLineSegment(sketch, "E413.0.2.88", {"start": v(-243.9, 20.75) * mm, "end": v(-245.9, 18.75) * mm});
            skLineSegment(sketch, "E413.0.2.89", {"start": v(-131.2, -9.25) * mm, "end": v(-131.2, -11.3) * mm});
            skLineSegment(sketch, "E413.0.2.90", {"start": v(-255.8, -13.25) * mm, "end": v(-255.8, -13.3) * mm});
            skLineSegment(sketch, "E413.0.2.91", {"start": v(-255.8, 2.75) * mm, "end": v(-255.8, 2.7) * mm});
            skLineSegment(sketch, "E413.0.2.92", {"start": v(-255.75, -7.3) * mm, "end": v(-255.75, -9.25) * mm});
            skLineSegment(sketch, "E413.0.2.93", {"start": v(-255.8, -9.25) * mm, "end": v(-255.8, -9.3) * mm});
            skLineSegment(sketch, "E413.0.2.94", {"start": v(-131.2, 8.92) * mm, "end": v(-131.2, 8.7) * mm});
            skLineSegment(sketch, "E413.0.2.95", {"start": v(-255.8, 8.75) * mm, "end": v(-255.75, 8.75) * mm});
            skLineSegment(sketch, "E413.0.2.96", {"start": v(-131.2, -15.3) * mm, "end": v(-131.25, -15.3) * mm});
            skLineSegment(sketch, "E413.0.2.97", {"start": v(-131.25, 8.9) * mm, "end": v(-131.25, 8.75) * mm});
            skLineSegment(sketch, "E413.0.2.98", {"start": v(-255.8, 8.7) * mm, "end": v(-255.8, 8.75) * mm});
            skLineSegment(sketch, "E413.0.2.99", {"start": v(-131.2, -15.25) * mm, "end": v(-131.2, -15.3) * mm});
            skLineSegment(sketch, "E413.0.3.0", {"start": v(-255.75, -79.3) * mm, "end": v(-131.2, -79.3) * mm});
            skLineSegment(sketch, "E413.0.3.1", {"start": v(-255.8, -93.3) * mm, "end": v(-131.25, -93.3) * mm});
            skLineSegment(sketch, "E413.0.3.2", {"start": v(-255.8, -81.3) * mm, "end": v(-131.25, -81.3) * mm});
            skLineSegment(sketch, "E413.0.3.3", {"start": v(-255.75, -95.3) * mm, "end": v(-131.2, -95.3) * mm});
            skLineSegment(sketch, "E413.0.3.4", {"start": v(-255.8, -97.3) * mm, "end": v(-131.25, -97.3) * mm});
            skLineSegment(sketch, "E413.0.3.5", {"start": v(-254.02, -77.3) * mm, "end": v(-133.05, -77.3) * mm});
            skLineSegment(sketch, "E413.0.3.6", {"start": v(-255.75, -83.3) * mm, "end": v(-131.2, -83.3) * mm});
            skLineSegment(sketch, "E413.0.3.7", {"start": v(-246.02, -69.3) * mm, "end": v(-141.05, -69.3) * mm});
            skLineSegment(sketch, "E413.0.3.8", {"start": v(-255.75, -103.3) * mm, "end": v(-131.25, -103.3) * mm});
            skLineSegment(sketch, "E413.0.3.9", {"start": v(-251.95, -75.3) * mm, "end": v(-134.98, -75.3) * mm});
            skLineSegment(sketch, "E413.0.3.10", {"start": v(-247.95, -71.3) * mm, "end": v(-138.98, -71.3) * mm});
            skLineSegment(sketch, "E413.0.3.11", {"start": v(-255.75, -99.3) * mm, "end": v(-131.2, -99.3) * mm});
            skLineSegment(sketch, "E413.0.3.12", {"start": v(-255.8, -101.3) * mm, "end": v(-131.25, -101.3) * mm});
            skLineSegment(sketch, "E413.0.3.13", {"start": v(-255.8, -85.3) * mm, "end": v(-131.25, -85.3) * mm});
            skLineSegment(sketch, "E413.0.3.14", {"start": v(-255.75, -87.3) * mm, "end": v(-131.2, -87.3) * mm});
            skLineSegment(sketch, "E413.0.3.15", {"start": v(-255.8, -89.3) * mm, "end": v(-131.25, -89.3) * mm});
            skLineSegment(sketch, "E413.0.3.16", {"start": v(-255.8, -105.3) * mm, "end": v(-131.25, -105.3) * mm});
            skLineSegment(sketch, "E413.0.3.17", {"start": v(-250.02, -73.3) * mm, "end": v(-137.05, -73.3) * mm});
            skLineSegment(sketch, "E413.0.3.18", {"start": v(-255.75, -107.3) * mm, "end": v(-131.2, -107.3) * mm});
            skLineSegment(sketch, "E413.0.3.19", {"start": v(-255.75, -91.3) * mm, "end": v(-131.2, -91.3) * mm});
            skLineSegment(sketch, "E413.0.3.20", {"start": v(-243.9, -67.25) * mm, "end": v(-143.1, -67.25) * mm});
            skLineSegment(sketch, "E413.0.3.21", {"start": v(-255.75, -93.25) * mm, "end": v(-131.2, -93.25) * mm});
            skLineSegment(sketch, "E413.0.3.22", {"start": v(-255.8, -95.25) * mm, "end": v(-131.25, -95.25) * mm});
            skLineSegment(sketch, "E413.0.3.23", {"start": v(-255.75, -97.25) * mm, "end": v(-131.2, -97.25) * mm});
            skLineSegment(sketch, "E413.0.3.24", {"start": v(-255.75, -79.25) * mm, "end": v(-131.25, -79.25) * mm});
            skLineSegment(sketch, "E413.0.3.25", {"start": v(-255.75, -81.25) * mm, "end": v(-131.2, -81.25) * mm});
            skLineSegment(sketch, "E413.0.3.26", {"start": v(-255.8, -83.25) * mm, "end": v(-131.25, -83.25) * mm});
            skLineSegment(sketch, "E413.0.3.27", {"start": v(-255.8, -103.25) * mm, "end": v(-131.25, -103.25) * mm});
            skLineSegment(sketch, "E413.0.3.28", {"start": v(-255.8, -87.25) * mm, "end": v(-131.25, -87.25) * mm});
            skLineSegment(sketch, "E413.0.3.29", {"start": v(-249.9, -73.25) * mm, "end": v(-137.03, -73.25) * mm});
            skLineSegment(sketch, "E413.0.3.30", {"start": v(-255.75, -89.25) * mm, "end": v(-131.2, -89.25) * mm});
            skLineSegment(sketch, "E413.0.3.31", {"start": v(-255.8, -107.25) * mm, "end": v(-131.25, -107.25) * mm});
            skLineSegment(sketch, "E413.0.3.32", {"start": v(-253.9, -77.25) * mm, "end": v(-133.03, -77.25) * mm});
            skLineSegment(sketch, "E413.0.3.33", {"start": v(-255.8, -99.25) * mm, "end": v(-131.25, -99.25) * mm});
            skLineSegment(sketch, "E413.0.3.34", {"start": v(-255.75, -85.25) * mm, "end": v(-131.2, -85.25) * mm});
            skLineSegment(sketch, "E413.0.3.35", {"start": v(-255.75, -101.25) * mm, "end": v(-131.2, -101.25) * mm});
            skLineSegment(sketch, "E413.0.3.36", {"start": v(-245.9, -69.25) * mm, "end": v(-141.1, -69.25) * mm});
            skLineSegment(sketch, "E413.0.3.37", {"start": v(-255.75, -105.25) * mm, "end": v(-131.2, -105.25) * mm});
            skLineSegment(sketch, "E413.0.3.38", {"start": v(-247.97, -71.25) * mm, "end": v(-139.1, -71.25) * mm});
            skLineSegment(sketch, "E413.0.3.39", {"start": v(-243.92, -67.2) * mm, "end": v(-143.08, -67.2) * mm});
            skLineSegment(sketch, "E413.0.3.40", {"start": v(-131, -79) * mm, "end": v(-131, -109) * mm});
            skLineSegment(sketch, "E413.0.3.41", {"start": v(-251.97, -75.25) * mm, "end": v(-135.1, -75.25) * mm});
            skLineSegment(sketch, "E413.0.3.42", {"start": v(-255.8, -91.25) * mm, "end": v(-131.25, -91.25) * mm});
            skLineSegment(sketch, "E413.0.3.43", {"start": v(-137.03, -73.25) * mm, "end": v(-134.98, -75.3) * mm});
            skLineSegment(sketch, "E413.0.3.44", {"start": v(-137.05, -73.3) * mm, "end": v(-135.1, -75.25) * mm});
            skLineSegment(sketch, "E413.0.3.45", {"start": v(-247.97, -71.25) * mm, "end": v(-250.02, -73.3) * mm});
            skLineSegment(sketch, "E413.0.3.46", {"start": v(-244, -67) * mm, "end": v(-256, -79) * mm});
            skLineSegment(sketch, "E413.0.3.47", {"start": v(-244, -67) * mm, "end": v(-143, -67) * mm});
            skLineSegment(sketch, "E413.0.3.48", {"start": v(-143, -67) * mm, "end": v(-131, -79) * mm});
            skLineSegment(sketch, "E413.0.3.49", {"start": v(-247.95, -71.3) * mm, "end": v(-249.9, -73.25) * mm});
            skLineSegment(sketch, "E413.0.3.50", {"start": v(-255.8, -83.25) * mm, "end": v(-255.8, -85.25) * mm});
            skLineSegment(sketch, "E413.0.3.51", {"start": v(-251.97, -75.25) * mm, "end": v(-254.02, -77.3) * mm});
            skLineSegment(sketch, "E413.0.3.52", {"start": v(-141.05, -69.3) * mm, "end": v(-139.1, -71.25) * mm});
            skLineSegment(sketch, "E413.0.3.53", {"start": v(-255.8, -87.25) * mm, "end": v(-255.8, -89.3) * mm});
            skLineSegment(sketch, "E413.0.3.54", {"start": v(-133.03, -77.25) * mm, "end": v(-131.2, -79.08) * mm});
            skLineSegment(sketch, "E413.0.3.55", {"start": v(-131.2, -105.25) * mm, "end": v(-131.2, -107.3) * mm});
            skLineSegment(sketch, "E413.0.3.56", {"start": v(-131.25, -101.3) * mm, "end": v(-131.25, -103.25) * mm});
            skLineSegment(sketch, "E413.0.3.57", {"start": v(-133.05, -77.3) * mm, "end": v(-131.25, -79.1) * mm});
            skLineSegment(sketch, "E413.0.3.58", {"start": v(-251.95, -75.3) * mm, "end": v(-253.9, -77.25) * mm});
            skLineSegment(sketch, "E413.0.3.59", {"start": v(-131.25, -81.3) * mm, "end": v(-131.25, -83.25) * mm});
            skLineSegment(sketch, "E413.0.3.60", {"start": v(-255.8, -107.25) * mm, "end": v(-255.8, -109) * mm});
            skLineSegment(sketch, "E413.0.3.61", {"start": v(-255.8, -103.25) * mm, "end": v(-255.8, -105.3) * mm});
            skLineSegment(sketch, "E413.0.3.62", {"start": v(-131.25, -89.3) * mm, "end": v(-131.25, -91.25) * mm});
            skLineSegment(sketch, "E413.0.3.63", {"start": v(-243.92, -67.2) * mm, "end": v(-246.02, -69.3) * mm});
            skLineSegment(sketch, "E413.0.3.64", {"start": v(-143.08, -67.2) * mm, "end": v(-138.98, -71.3) * mm});
            skLineSegment(sketch, "E413.0.3.65", {"start": v(-131.25, -97.3) * mm, "end": v(-131.25, -99.25) * mm});
            skLineSegment(sketch, "E413.0.3.66", {"start": v(-255.8, -91.25) * mm, "end": v(-255.8, -93.3) * mm});
            skLineSegment(sketch, "E413.0.3.67", {"start": v(-131.25, -85.3) * mm, "end": v(-131.25, -87.25) * mm});
            skLineSegment(sketch, "E413.0.3.68", {"start": v(-131.25, -93.3) * mm, "end": v(-131.25, -95.25) * mm});
            skLineSegment(sketch, "E413.0.3.69", {"start": v(-255.8, -99.25) * mm, "end": v(-255.8, -101.25) * mm});
            skLineSegment(sketch, "E413.0.3.70", {"start": v(-131.2, -93.25) * mm, "end": v(-131.2, -95.3) * mm});
            skLineSegment(sketch, "E413.0.3.71", {"start": v(-255.8, -109) * mm, "end": v(-255.75, -109) * mm});
            skLineSegment(sketch, "E413.0.3.72", {"start": v(-256, -79) * mm, "end": v(-256, -109) * mm});
            skLineSegment(sketch, "E413.0.3.73", {"start": v(-255.75, -79.3) * mm, "end": v(-255.75, -81.25) * mm});
            skLineSegment(sketch, "E413.0.3.74", {"start": v(-131.25, -105.3) * mm, "end": v(-131.25, -107.25) * mm});
            skLineSegment(sketch, "E413.0.3.75", {"start": v(-255.75, -83.3) * mm, "end": v(-255.75, -85.25) * mm});
            skLineSegment(sketch, "E413.0.3.76", {"start": v(-131.2, -101.25) * mm, "end": v(-131.2, -103.25) * mm});
            skLineSegment(sketch, "E413.0.3.77", {"start": v(-255.75, -87.3) * mm, "end": v(-255.75, -89.3) * mm});
            skLineSegment(sketch, "E413.0.3.78", {"start": v(-255.75, -107.3) * mm, "end": v(-255.75, -109) * mm});
            skLineSegment(sketch, "E413.0.3.79", {"start": v(-131.2, -85.25) * mm, "end": v(-131.2, -87.3) * mm});
            skLineSegment(sketch, "E413.0.3.80", {"start": v(-255.75, -99.3) * mm, "end": v(-255.75, -101.25) * mm});
            skLineSegment(sketch, "E413.0.3.81", {"start": v(-131.2, -89.25) * mm, "end": v(-131.2, -91.3) * mm});
            skLineSegment(sketch, "E413.0.3.82", {"start": v(-143.1, -67.25) * mm, "end": v(-141.1, -69.25) * mm});
            skLineSegment(sketch, "E413.0.3.83", {"start": v(-255.75, -91.3) * mm, "end": v(-255.75, -93.25) * mm});
            skLineSegment(sketch, "E413.0.3.84", {"start": v(-131.2, -81.25) * mm, "end": v(-131.2, -83.3) * mm});
            skLineSegment(sketch, "E413.0.3.85", {"start": v(-255.75, -103.3) * mm, "end": v(-255.75, -105.25) * mm});
            skLineSegment(sketch, "E413.0.3.86", {"start": v(-255.8, -95.25) * mm, "end": v(-255.8, -97.25) * mm});
            skLineSegment(sketch, "E413.0.3.87", {"start": v(-255.8, -79.3) * mm, "end": v(-255.8, -81.3) * mm});
            skLineSegment(sketch, "E413.0.3.88", {"start": v(-243.9, -67.25) * mm, "end": v(-245.9, -69.25) * mm});
            skLineSegment(sketch, "E413.0.3.89", {"start": v(-131.2, -97.25) * mm, "end": v(-131.2, -99.3) * mm});
            skLineSegment(sketch, "E413.0.3.90", {"start": v(-255.8, -101.25) * mm, "end": v(-255.8, -101.3) * mm});
            skLineSegment(sketch, "E413.0.3.91", {"start": v(-255.8, -85.25) * mm, "end": v(-255.8, -85.3) * mm});
            skLineSegment(sketch, "E413.0.3.92", {"start": v(-255.75, -95.3) * mm, "end": v(-255.75, -97.25) * mm});
            skLineSegment(sketch, "E413.0.3.93", {"start": v(-255.8, -97.25) * mm, "end": v(-255.8, -97.3) * mm});
            skLineSegment(sketch, "E413.0.3.94", {"start": v(-131.2, -79.08) * mm, "end": v(-131.2, -79.3) * mm});
            skLineSegment(sketch, "E413.0.3.95", {"start": v(-255.8, -79.25) * mm, "end": v(-255.75, -79.25) * mm});
            skLineSegment(sketch, "E413.0.3.96", {"start": v(-131.2, -103.3) * mm, "end": v(-131.25, -103.3) * mm});
            skLineSegment(sketch, "E413.0.3.97", {"start": v(-131.25, -79.1) * mm, "end": v(-131.25, -79.25) * mm});
            skLineSegment(sketch, "E413.0.3.98", {"start": v(-255.8, -79.3) * mm, "end": v(-255.8, -79.25) * mm});
            skLineSegment(sketch, "E413.0.3.99", {"start": v(-131.2, -103.25) * mm, "end": v(-131.2, -103.3) * mm});
            skLineSegment(sketch, "E413.0.4.0", {"start": v(-255.75, -167.3) * mm, "end": v(-131.2, -167.3) * mm});
            skLineSegment(sketch, "E413.0.4.1", {"start": v(-255.8, -181.3) * mm, "end": v(-131.25, -181.3) * mm});
            skLineSegment(sketch, "E413.0.4.2", {"start": v(-255.8, -169.3) * mm, "end": v(-131.25, -169.3) * mm});
            skLineSegment(sketch, "E413.0.4.3", {"start": v(-255.75, -183.3) * mm, "end": v(-131.2, -183.3) * mm});
            skLineSegment(sketch, "E413.0.4.4", {"start": v(-255.8, -185.3) * mm, "end": v(-131.25, -185.3) * mm});
            skLineSegment(sketch, "E413.0.4.5", {"start": v(-254.02, -165.3) * mm, "end": v(-133.05, -165.3) * mm});
            skLineSegment(sketch, "E413.0.4.6", {"start": v(-255.75, -171.3) * mm, "end": v(-131.2, -171.3) * mm});
            skLineSegment(sketch, "E413.0.4.7", {"start": v(-246.02, -157.3) * mm, "end": v(-141.05, -157.3) * mm});
            skLineSegment(sketch, "E413.0.4.8", {"start": v(-255.75, -191.3) * mm, "end": v(-131.25, -191.3) * mm});
            skLineSegment(sketch, "E413.0.4.9", {"start": v(-251.95, -163.3) * mm, "end": v(-134.98, -163.3) * mm});
            skLineSegment(sketch, "E413.0.4.10", {"start": v(-247.95, -159.3) * mm, "end": v(-138.98, -159.3) * mm});
            skLineSegment(sketch, "E413.0.4.11", {"start": v(-255.75, -187.3) * mm, "end": v(-131.2, -187.3) * mm});
            skLineSegment(sketch, "E413.0.4.12", {"start": v(-255.8, -189.3) * mm, "end": v(-131.25, -189.3) * mm});
            skLineSegment(sketch, "E413.0.4.13", {"start": v(-255.8, -173.3) * mm, "end": v(-131.25, -173.3) * mm});
            skLineSegment(sketch, "E413.0.4.14", {"start": v(-255.75, -175.3) * mm, "end": v(-131.2, -175.3) * mm});
            skLineSegment(sketch, "E413.0.4.15", {"start": v(-255.8, -177.3) * mm, "end": v(-131.25, -177.3) * mm});
            skLineSegment(sketch, "E413.0.4.16", {"start": v(-255.8, -193.3) * mm, "end": v(-131.25, -193.3) * mm});
            skLineSegment(sketch, "E413.0.4.17", {"start": v(-250.02, -161.3) * mm, "end": v(-137.05, -161.3) * mm});
            skLineSegment(sketch, "E413.0.4.18", {"start": v(-255.75, -195.3) * mm, "end": v(-131.2, -195.3) * mm});
            skLineSegment(sketch, "E413.0.4.19", {"start": v(-255.75, -179.3) * mm, "end": v(-131.2, -179.3) * mm});
            skLineSegment(sketch, "E413.0.4.20", {"start": v(-243.9, -155.25) * mm, "end": v(-143.1, -155.25) * mm});
            skLineSegment(sketch, "E413.0.4.21", {"start": v(-255.75, -181.25) * mm, "end": v(-131.2, -181.25) * mm});
            skLineSegment(sketch, "E413.0.4.22", {"start": v(-255.8, -183.25) * mm, "end": v(-131.25, -183.25) * mm});
            skLineSegment(sketch, "E413.0.4.23", {"start": v(-255.75, -185.25) * mm, "end": v(-131.2, -185.25) * mm});
            skLineSegment(sketch, "E413.0.4.24", {"start": v(-255.75, -167.25) * mm, "end": v(-131.25, -167.25) * mm});
            skLineSegment(sketch, "E413.0.4.25", {"start": v(-255.75, -169.25) * mm, "end": v(-131.2, -169.25) * mm});
            skLineSegment(sketch, "E413.0.4.26", {"start": v(-255.8, -171.25) * mm, "end": v(-131.25, -171.25) * mm});
            skLineSegment(sketch, "E413.0.4.27", {"start": v(-255.8, -191.25) * mm, "end": v(-131.25, -191.25) * mm});
            skLineSegment(sketch, "E413.0.4.28", {"start": v(-255.8, -175.25) * mm, "end": v(-131.25, -175.25) * mm});
            skLineSegment(sketch, "E413.0.4.29", {"start": v(-249.9, -161.25) * mm, "end": v(-137.03, -161.25) * mm});
            skLineSegment(sketch, "E413.0.4.30", {"start": v(-255.75, -177.25) * mm, "end": v(-131.2, -177.25) * mm});
            skLineSegment(sketch, "E413.0.4.31", {"start": v(-255.8, -195.25) * mm, "end": v(-131.25, -195.25) * mm});
            skLineSegment(sketch, "E413.0.4.32", {"start": v(-253.9, -165.25) * mm, "end": v(-133.03, -165.25) * mm});
            skLineSegment(sketch, "E413.0.4.33", {"start": v(-255.8, -187.25) * mm, "end": v(-131.25, -187.25) * mm});
            skLineSegment(sketch, "E413.0.4.34", {"start": v(-255.75, -173.25) * mm, "end": v(-131.2, -173.25) * mm});
            skLineSegment(sketch, "E413.0.4.35", {"start": v(-255.75, -189.25) * mm, "end": v(-131.2, -189.25) * mm});
            skLineSegment(sketch, "E413.0.4.36", {"start": v(-245.9, -157.25) * mm, "end": v(-141.1, -157.25) * mm});
            skLineSegment(sketch, "E413.0.4.37", {"start": v(-255.75, -193.25) * mm, "end": v(-131.2, -193.25) * mm});
            skLineSegment(sketch, "E413.0.4.38", {"start": v(-247.97, -159.25) * mm, "end": v(-139.1, -159.25) * mm});
            skLineSegment(sketch, "E413.0.4.39", {"start": v(-243.92, -155.2) * mm, "end": v(-143.08, -155.2) * mm});
            skLineSegment(sketch, "E413.0.4.40", {"start": v(-131, -167) * mm, "end": v(-131, -197) * mm});
            skLineSegment(sketch, "E413.0.4.41", {"start": v(-251.97, -163.25) * mm, "end": v(-135.1, -163.25) * mm});
            skLineSegment(sketch, "E413.0.4.42", {"start": v(-255.8, -179.25) * mm, "end": v(-131.25, -179.25) * mm});
            skLineSegment(sketch, "E413.0.4.43", {"start": v(-137.03, -161.25) * mm, "end": v(-134.98, -163.3) * mm});
            skLineSegment(sketch, "E413.0.4.44", {"start": v(-137.05, -161.3) * mm, "end": v(-135.1, -163.25) * mm});
            skLineSegment(sketch, "E413.0.4.45", {"start": v(-247.97, -159.25) * mm, "end": v(-250.02, -161.3) * mm});
            skLineSegment(sketch, "E413.0.4.46", {"start": v(-244, -155) * mm, "end": v(-256, -167) * mm});
            skLineSegment(sketch, "E413.0.4.47", {"start": v(-244, -155) * mm, "end": v(-143, -155) * mm});
            skLineSegment(sketch, "E413.0.4.48", {"start": v(-143, -155) * mm, "end": v(-131, -167) * mm});
            skLineSegment(sketch, "E413.0.4.49", {"start": v(-247.95, -159.3) * mm, "end": v(-249.9, -161.25) * mm});
            skLineSegment(sketch, "E413.0.4.50", {"start": v(-255.8, -171.25) * mm, "end": v(-255.8, -173.25) * mm});
            skLineSegment(sketch, "E413.0.4.51", {"start": v(-251.97, -163.25) * mm, "end": v(-254.02, -165.3) * mm});
            skLineSegment(sketch, "E413.0.4.52", {"start": v(-141.05, -157.3) * mm, "end": v(-139.1, -159.25) * mm});
            skLineSegment(sketch, "E413.0.4.53", {"start": v(-255.8, -175.25) * mm, "end": v(-255.8, -177.3) * mm});
            skLineSegment(sketch, "E413.0.4.54", {"start": v(-133.03, -165.25) * mm, "end": v(-131.2, -167.08) * mm});
            skLineSegment(sketch, "E413.0.4.55", {"start": v(-131.2, -193.25) * mm, "end": v(-131.2, -195.3) * mm});
            skLineSegment(sketch, "E413.0.4.56", {"start": v(-131.25, -189.3) * mm, "end": v(-131.25, -191.25) * mm});
            skLineSegment(sketch, "E413.0.4.57", {"start": v(-133.05, -165.3) * mm, "end": v(-131.25, -167.1) * mm});
            skLineSegment(sketch, "E413.0.4.58", {"start": v(-251.95, -163.3) * mm, "end": v(-253.9, -165.25) * mm});
            skLineSegment(sketch, "E413.0.4.59", {"start": v(-131.25, -169.3) * mm, "end": v(-131.25, -171.25) * mm});
            skLineSegment(sketch, "E413.0.4.60", {"start": v(-255.8, -195.25) * mm, "end": v(-255.8, -197) * mm});
            skLineSegment(sketch, "E413.0.4.61", {"start": v(-255.8, -191.25) * mm, "end": v(-255.8, -193.3) * mm});
            skLineSegment(sketch, "E413.0.4.62", {"start": v(-131.25, -177.3) * mm, "end": v(-131.25, -179.25) * mm});
            skLineSegment(sketch, "E413.0.4.63", {"start": v(-243.92, -155.2) * mm, "end": v(-246.02, -157.3) * mm});
            skLineSegment(sketch, "E413.0.4.64", {"start": v(-143.08, -155.2) * mm, "end": v(-138.98, -159.3) * mm});
            skLineSegment(sketch, "E413.0.4.65", {"start": v(-131.25, -185.3) * mm, "end": v(-131.25, -187.25) * mm});
            skLineSegment(sketch, "E413.0.4.66", {"start": v(-255.8, -179.25) * mm, "end": v(-255.8, -181.3) * mm});
            skLineSegment(sketch, "E413.0.4.67", {"start": v(-131.25, -173.3) * mm, "end": v(-131.25, -175.25) * mm});
            skLineSegment(sketch, "E413.0.4.68", {"start": v(-131.25, -181.3) * mm, "end": v(-131.25, -183.25) * mm});
            skLineSegment(sketch, "E413.0.4.69", {"start": v(-255.8, -187.25) * mm, "end": v(-255.8, -189.25) * mm});
            skLineSegment(sketch, "E413.0.4.70", {"start": v(-131.2, -181.25) * mm, "end": v(-131.2, -183.3) * mm});
            skLineSegment(sketch, "E413.0.4.71", {"start": v(-255.8, -197) * mm, "end": v(-255.75, -197) * mm});
            skLineSegment(sketch, "E413.0.4.72", {"start": v(-256, -167) * mm, "end": v(-256, -197) * mm});
            skLineSegment(sketch, "E413.0.4.73", {"start": v(-255.75, -167.3) * mm, "end": v(-255.75, -169.25) * mm});
            skLineSegment(sketch, "E413.0.4.74", {"start": v(-131.25, -193.3) * mm, "end": v(-131.25, -195.25) * mm});
            skLineSegment(sketch, "E413.0.4.75", {"start": v(-255.75, -171.3) * mm, "end": v(-255.75, -173.25) * mm});
            skLineSegment(sketch, "E413.0.4.76", {"start": v(-131.2, -189.25) * mm, "end": v(-131.2, -191.25) * mm});
            skLineSegment(sketch, "E413.0.4.77", {"start": v(-255.75, -175.3) * mm, "end": v(-255.75, -177.3) * mm});
            skLineSegment(sketch, "E413.0.4.78", {"start": v(-255.75, -195.3) * mm, "end": v(-255.75, -197) * mm});
            skLineSegment(sketch, "E413.0.4.79", {"start": v(-131.2, -173.25) * mm, "end": v(-131.2, -175.3) * mm});
            skLineSegment(sketch, "E413.0.4.80", {"start": v(-255.75, -187.3) * mm, "end": v(-255.75, -189.25) * mm});
            skLineSegment(sketch, "E413.0.4.81", {"start": v(-131.2, -177.25) * mm, "end": v(-131.2, -179.3) * mm});
            skLineSegment(sketch, "E413.0.4.82", {"start": v(-143.1, -155.25) * mm, "end": v(-141.1, -157.25) * mm});
            skLineSegment(sketch, "E413.0.4.83", {"start": v(-255.75, -179.3) * mm, "end": v(-255.75, -181.25) * mm});
            skLineSegment(sketch, "E413.0.4.84", {"start": v(-131.2, -169.25) * mm, "end": v(-131.2, -171.3) * mm});
            skLineSegment(sketch, "E413.0.4.85", {"start": v(-255.75, -191.3) * mm, "end": v(-255.75, -193.25) * mm});
            skLineSegment(sketch, "E413.0.4.86", {"start": v(-255.8, -183.25) * mm, "end": v(-255.8, -185.25) * mm});
            skLineSegment(sketch, "E413.0.4.87", {"start": v(-255.8, -167.3) * mm, "end": v(-255.8, -169.3) * mm});
            skLineSegment(sketch, "E413.0.4.88", {"start": v(-243.9, -155.25) * mm, "end": v(-245.9, -157.25) * mm});
            skLineSegment(sketch, "E413.0.4.89", {"start": v(-131.2, -185.25) * mm, "end": v(-131.2, -187.3) * mm});
            skLineSegment(sketch, "E413.0.4.90", {"start": v(-255.8, -189.25) * mm, "end": v(-255.8, -189.3) * mm});
            skLineSegment(sketch, "E413.0.4.91", {"start": v(-255.8, -173.25) * mm, "end": v(-255.8, -173.3) * mm});
            skLineSegment(sketch, "E413.0.4.92", {"start": v(-255.75, -183.3) * mm, "end": v(-255.75, -185.25) * mm});
            skLineSegment(sketch, "E413.0.4.93", {"start": v(-255.8, -185.25) * mm, "end": v(-255.8, -185.3) * mm});
            skLineSegment(sketch, "E413.0.4.94", {"start": v(-131.2, -167.08) * mm, "end": v(-131.2, -167.3) * mm});
            skLineSegment(sketch, "E413.0.4.95", {"start": v(-255.8, -167.25) * mm, "end": v(-255.75, -167.25) * mm});
            skLineSegment(sketch, "E413.0.4.96", {"start": v(-131.2, -191.3) * mm, "end": v(-131.25, -191.3) * mm});
            skLineSegment(sketch, "E413.0.4.97", {"start": v(-131.25, -167.1) * mm, "end": v(-131.25, -167.25) * mm});
            skLineSegment(sketch, "E413.0.4.98", {"start": v(-255.8, -167.3) * mm, "end": v(-255.8, -167.25) * mm});
            skLineSegment(sketch, "E413.0.4.99", {"start": v(-131.2, -191.25) * mm, "end": v(-131.2, -191.3) * mm});
            skLineSegment(sketch, "E413.1.0.0", {"start": v(-127.25, 184.7) * mm, "end": v(-2.7, 184.7) * mm});
            skLineSegment(sketch, "E413.1.0.1", {"start": v(-127.3, 170.7) * mm, "end": v(-2.75, 170.7) * mm});
            skLineSegment(sketch, "E413.1.0.2", {"start": v(-127.3, 182.7) * mm, "end": v(-2.75, 182.7) * mm});
            skLineSegment(sketch, "E413.1.0.3", {"start": v(-127.25, 168.7) * mm, "end": v(-2.7, 168.7) * mm});
            skLineSegment(sketch, "E413.1.0.4", {"start": v(-127.3, 166.7) * mm, "end": v(-2.75, 166.7) * mm});
            skLineSegment(sketch, "E413.1.0.5", {"start": v(-125.52, 186.7) * mm, "end": v(-4.55, 186.7) * mm});
            skLineSegment(sketch, "E413.1.0.6", {"start": v(-127.25, 180.7) * mm, "end": v(-2.7, 180.7) * mm});
            skLineSegment(sketch, "E413.1.0.7", {"start": v(-117.52, 194.7) * mm, "end": v(-12.55, 194.7) * mm});
            skLineSegment(sketch, "E413.1.0.8", {"start": v(-127.25, 160.7) * mm, "end": v(-2.75, 160.7) * mm});
            skLineSegment(sketch, "E413.1.0.9", {"start": v(-123.45, 188.7) * mm, "end": v(-6.48, 188.7) * mm});
            skLineSegment(sketch, "E413.1.0.10", {"start": v(-119.45, 192.7) * mm, "end": v(-10.48, 192.7) * mm});
            skLineSegment(sketch, "E413.1.0.11", {"start": v(-127.25, 164.7) * mm, "end": v(-2.7, 164.7) * mm});
            skLineSegment(sketch, "E413.1.0.12", {"start": v(-127.3, 162.7) * mm, "end": v(-2.75, 162.7) * mm});
            skLineSegment(sketch, "E413.1.0.13", {"start": v(-127.3, 178.7) * mm, "end": v(-2.75, 178.7) * mm});
            skLineSegment(sketch, "E413.1.0.14", {"start": v(-127.25, 176.7) * mm, "end": v(-2.7, 176.7) * mm});
            skLineSegment(sketch, "E413.1.0.15", {"start": v(-127.3, 174.7) * mm, "end": v(-2.75, 174.7) * mm});
            skLineSegment(sketch, "E413.1.0.16", {"start": v(-127.3, 158.7) * mm, "end": v(-2.75, 158.7) * mm});
            skLineSegment(sketch, "E413.1.0.17", {"start": v(-121.52, 190.7) * mm, "end": v(-8.55, 190.7) * mm});
            skLineSegment(sketch, "E413.1.0.18", {"start": v(-127.25, 156.7) * mm, "end": v(-2.7, 156.7) * mm});
            skLineSegment(sketch, "E413.1.0.19", {"start": v(-127.25, 172.7) * mm, "end": v(-2.7, 172.7) * mm});
            skLineSegment(sketch, "E413.1.0.20", {"start": v(-115.4, 196.75) * mm, "end": v(-14.6, 196.75) * mm});
            skLineSegment(sketch, "E413.1.0.21", {"start": v(-127.25, 170.75) * mm, "end": v(-2.7, 170.75) * mm});
            skLineSegment(sketch, "E413.1.0.22", {"start": v(-127.3, 168.75) * mm, "end": v(-2.75, 168.75) * mm});
            skLineSegment(sketch, "E413.1.0.23", {"start": v(-127.25, 166.75) * mm, "end": v(-2.7, 166.75) * mm});
            skLineSegment(sketch, "E413.1.0.24", {"start": v(-127.25, 184.75) * mm, "end": v(-2.75, 184.75) * mm});
            skLineSegment(sketch, "E413.1.0.25", {"start": v(-127.25, 182.75) * mm, "end": v(-2.7, 182.75) * mm});
            skLineSegment(sketch, "E413.1.0.26", {"start": v(-127.3, 180.75) * mm, "end": v(-2.75, 180.75) * mm});
            skLineSegment(sketch, "E413.1.0.27", {"start": v(-127.3, 160.75) * mm, "end": v(-2.75, 160.75) * mm});
            skLineSegment(sketch, "E413.1.0.28", {"start": v(-127.3, 176.75) * mm, "end": v(-2.75, 176.75) * mm});
            skLineSegment(sketch, "E413.1.0.29", {"start": v(-121.4, 190.75) * mm, "end": v(-8.53, 190.75) * mm});
            skLineSegment(sketch, "E413.1.0.30", {"start": v(-127.25, 174.75) * mm, "end": v(-2.7, 174.75) * mm});
            skLineSegment(sketch, "E413.1.0.31", {"start": v(-127.3, 156.75) * mm, "end": v(-2.75, 156.75) * mm});
            skLineSegment(sketch, "E413.1.0.32", {"start": v(-125.4, 186.75) * mm, "end": v(-4.53, 186.75) * mm});
            skLineSegment(sketch, "E413.1.0.33", {"start": v(-127.3, 164.75) * mm, "end": v(-2.75, 164.75) * mm});
            skLineSegment(sketch, "E413.1.0.34", {"start": v(-127.25, 178.75) * mm, "end": v(-2.7, 178.75) * mm});
            skLineSegment(sketch, "E413.1.0.35", {"start": v(-127.25, 162.75) * mm, "end": v(-2.7, 162.75) * mm});
            skLineSegment(sketch, "E413.1.0.36", {"start": v(-117.4, 194.75) * mm, "end": v(-12.6, 194.75) * mm});
            skLineSegment(sketch, "E413.1.0.37", {"start": v(-127.25, 158.75) * mm, "end": v(-2.7, 158.75) * mm});
            skLineSegment(sketch, "E413.1.0.38", {"start": v(-119.47, 192.75) * mm, "end": v(-10.6, 192.75) * mm});
            skLineSegment(sketch, "E413.1.0.39", {"start": v(-115.42, 196.8) * mm, "end": v(-14.58, 196.8) * mm});
            skLineSegment(sketch, "E413.1.0.40", {"start": v(-2.5, 185) * mm, "end": v(-2.5, 155) * mm});
            skLineSegment(sketch, "E413.1.0.41", {"start": v(-123.47, 188.75) * mm, "end": v(-6.6, 188.75) * mm});
            skLineSegment(sketch, "E413.1.0.42", {"start": v(-127.3, 172.75) * mm, "end": v(-2.75, 172.75) * mm});
            skLineSegment(sketch, "E413.1.0.43", {"start": v(-8.53, 190.75) * mm, "end": v(-6.48, 188.7) * mm});
            skLineSegment(sketch, "E413.1.0.44", {"start": v(-8.55, 190.7) * mm, "end": v(-6.6, 188.75) * mm});
            skLineSegment(sketch, "E413.1.0.45", {"start": v(-119.47, 192.75) * mm, "end": v(-121.52, 190.7) * mm});
            skLineSegment(sketch, "E413.1.0.46", {"start": v(-115.5, 197) * mm, "end": v(-127.5, 185) * mm});
            skLineSegment(sketch, "E413.1.0.47", {"start": v(-115.5, 197) * mm, "end": v(-14.5, 197) * mm});
            skLineSegment(sketch, "E413.1.0.48", {"start": v(-14.5, 197) * mm, "end": v(-2.5, 185) * mm});
            skLineSegment(sketch, "E413.1.0.49", {"start": v(-119.45, 192.7) * mm, "end": v(-121.4, 190.75) * mm});
            skLineSegment(sketch, "E413.1.0.50", {"start": v(-127.3, 180.75) * mm, "end": v(-127.3, 178.75) * mm});
            skLineSegment(sketch, "E413.1.0.51", {"start": v(-123.47, 188.75) * mm, "end": v(-125.52, 186.7) * mm});
            skLineSegment(sketch, "E413.1.0.52", {"start": v(-12.55, 194.7) * mm, "end": v(-10.6, 192.75) * mm});
            skLineSegment(sketch, "E413.1.0.53", {"start": v(-127.3, 176.75) * mm, "end": v(-127.3, 174.7) * mm});
            skLineSegment(sketch, "E413.1.0.54", {"start": v(-4.53, 186.75) * mm, "end": v(-2.7, 184.92) * mm});
            skLineSegment(sketch, "E413.1.0.55", {"start": v(-2.7, 158.75) * mm, "end": v(-2.7, 156.7) * mm});
            skLineSegment(sketch, "E413.1.0.56", {"start": v(-2.75, 162.7) * mm, "end": v(-2.75, 160.75) * mm});
            skLineSegment(sketch, "E413.1.0.57", {"start": v(-4.55, 186.7) * mm, "end": v(-2.75, 184.9) * mm});
            skLineSegment(sketch, "E413.1.0.58", {"start": v(-123.45, 188.7) * mm, "end": v(-125.4, 186.75) * mm});
            skLineSegment(sketch, "E413.1.0.59", {"start": v(-2.75, 182.7) * mm, "end": v(-2.75, 180.75) * mm});
            skLineSegment(sketch, "E413.1.0.60", {"start": v(-127.3, 156.75) * mm, "end": v(-127.3, 155) * mm});
            skLineSegment(sketch, "E413.1.0.61", {"start": v(-127.3, 160.75) * mm, "end": v(-127.3, 158.7) * mm});
            skLineSegment(sketch, "E413.1.0.62", {"start": v(-2.75, 174.7) * mm, "end": v(-2.75, 172.75) * mm});
            skLineSegment(sketch, "E413.1.0.63", {"start": v(-115.42, 196.8) * mm, "end": v(-117.52, 194.7) * mm});
            skLineSegment(sketch, "E413.1.0.64", {"start": v(-14.58, 196.8) * mm, "end": v(-10.48, 192.7) * mm});
            skLineSegment(sketch, "E413.1.0.65", {"start": v(-2.75, 166.7) * mm, "end": v(-2.75, 164.75) * mm});
            skLineSegment(sketch, "E413.1.0.66", {"start": v(-127.3, 172.75) * mm, "end": v(-127.3, 170.7) * mm});
            skLineSegment(sketch, "E413.1.0.67", {"start": v(-2.75, 178.7) * mm, "end": v(-2.75, 176.75) * mm});
            skLineSegment(sketch, "E413.1.0.68", {"start": v(-2.75, 170.7) * mm, "end": v(-2.75, 168.75) * mm});
            skLineSegment(sketch, "E413.1.0.69", {"start": v(-127.3, 164.75) * mm, "end": v(-127.3, 162.75) * mm});
            skLineSegment(sketch, "E413.1.0.70", {"start": v(-2.7, 170.75) * mm, "end": v(-2.7, 168.7) * mm});
            skLineSegment(sketch, "E413.1.0.71", {"start": v(-127.3, 155) * mm, "end": v(-127.25, 155) * mm});
            skLineSegment(sketch, "E413.1.0.72", {"start": v(-127.5, 185) * mm, "end": v(-127.5, 155) * mm});
            skLineSegment(sketch, "E413.1.0.73", {"start": v(-127.25, 184.7) * mm, "end": v(-127.25, 182.75) * mm});
            skLineSegment(sketch, "E413.1.0.74", {"start": v(-2.75, 158.7) * mm, "end": v(-2.75, 156.75) * mm});
            skLineSegment(sketch, "E413.1.0.75", {"start": v(-127.25, 180.7) * mm, "end": v(-127.25, 178.75) * mm});
            skLineSegment(sketch, "E413.1.0.76", {"start": v(-2.7, 162.75) * mm, "end": v(-2.7, 160.75) * mm});
            skLineSegment(sketch, "E413.1.0.77", {"start": v(-127.25, 176.7) * mm, "end": v(-127.25, 174.7) * mm});
            skLineSegment(sketch, "E413.1.0.78", {"start": v(-127.25, 156.7) * mm, "end": v(-127.25, 155) * mm});
            skLineSegment(sketch, "E413.1.0.79", {"start": v(-2.7, 178.75) * mm, "end": v(-2.7, 176.7) * mm});
            skLineSegment(sketch, "E413.1.0.80", {"start": v(-127.25, 164.7) * mm, "end": v(-127.25, 162.75) * mm});
            skLineSegment(sketch, "E413.1.0.81", {"start": v(-2.7, 174.75) * mm, "end": v(-2.7, 172.7) * mm});
            skLineSegment(sketch, "E413.1.0.82", {"start": v(-14.6, 196.75) * mm, "end": v(-12.6, 194.75) * mm});
            skLineSegment(sketch, "E413.1.0.83", {"start": v(-127.25, 172.7) * mm, "end": v(-127.25, 170.75) * mm});
            skLineSegment(sketch, "E413.1.0.84", {"start": v(-2.7, 182.75) * mm, "end": v(-2.7, 180.7) * mm});
            skLineSegment(sketch, "E413.1.0.85", {"start": v(-127.25, 160.7) * mm, "end": v(-127.25, 158.75) * mm});
            skLineSegment(sketch, "E413.1.0.86", {"start": v(-127.3, 168.75) * mm, "end": v(-127.3, 166.75) * mm});
            skLineSegment(sketch, "E413.1.0.87", {"start": v(-127.3, 184.7) * mm, "end": v(-127.3, 182.7) * mm});
            skLineSegment(sketch, "E413.1.0.88", {"start": v(-115.4, 196.75) * mm, "end": v(-117.4, 194.75) * mm});
            skLineSegment(sketch, "E413.1.0.89", {"start": v(-2.7, 166.75) * mm, "end": v(-2.7, 164.7) * mm});
            skLineSegment(sketch, "E413.1.0.90", {"start": v(-127.3, 162.75) * mm, "end": v(-127.3, 162.7) * mm});
            skLineSegment(sketch, "E413.1.0.91", {"start": v(-127.3, 178.75) * mm, "end": v(-127.3, 178.7) * mm});
            skLineSegment(sketch, "E413.1.0.92", {"start": v(-127.25, 168.7) * mm, "end": v(-127.25, 166.75) * mm});
            skLineSegment(sketch, "E413.1.0.93", {"start": v(-127.3, 166.75) * mm, "end": v(-127.3, 166.7) * mm});
            skLineSegment(sketch, "E413.1.0.94", {"start": v(-2.7, 184.92) * mm, "end": v(-2.7, 184.7) * mm});
            skLineSegment(sketch, "E413.1.0.95", {"start": v(-127.3, 184.75) * mm, "end": v(-127.25, 184.75) * mm});
            skLineSegment(sketch, "E413.1.0.96", {"start": v(-2.7, 160.7) * mm, "end": v(-2.75, 160.7) * mm});
            skLineSegment(sketch, "E413.1.0.97", {"start": v(-2.75, 184.9) * mm, "end": v(-2.75, 184.75) * mm});
            skLineSegment(sketch, "E413.1.0.98", {"start": v(-127.3, 184.7) * mm, "end": v(-127.3, 184.75) * mm});
            skLineSegment(sketch, "E413.1.0.99", {"start": v(-2.7, 160.75) * mm, "end": v(-2.7, 160.7) * mm});
            skLineSegment(sketch, "E413.1.1.0", {"start": v(-127.25, 96.7) * mm, "end": v(-2.7, 96.7) * mm});
            skLineSegment(sketch, "E413.1.1.1", {"start": v(-127.3, 82.7) * mm, "end": v(-2.75, 82.7) * mm});
            skLineSegment(sketch, "E413.1.1.2", {"start": v(-127.3, 94.7) * mm, "end": v(-2.75, 94.7) * mm});
            skLineSegment(sketch, "E413.1.1.3", {"start": v(-127.25, 80.7) * mm, "end": v(-2.7, 80.7) * mm});
            skLineSegment(sketch, "E413.1.1.4", {"start": v(-127.3, 78.7) * mm, "end": v(-2.75, 78.7) * mm});
            skLineSegment(sketch, "E413.1.1.5", {"start": v(-125.52, 98.7) * mm, "end": v(-4.55, 98.7) * mm});
            skLineSegment(sketch, "E413.1.1.6", {"start": v(-127.25, 92.7) * mm, "end": v(-2.7, 92.7) * mm});
            skLineSegment(sketch, "E413.1.1.7", {"start": v(-117.52, 106.7) * mm, "end": v(-12.55, 106.7) * mm});
            skLineSegment(sketch, "E413.1.1.8", {"start": v(-127.25, 72.7) * mm, "end": v(-2.75, 72.7) * mm});
            skLineSegment(sketch, "E413.1.1.9", {"start": v(-123.45, 100.7) * mm, "end": v(-6.48, 100.7) * mm});
            skLineSegment(sketch, "E413.1.1.10", {"start": v(-119.45, 104.7) * mm, "end": v(-10.48, 104.7) * mm});
            skLineSegment(sketch, "E413.1.1.11", {"start": v(-127.25, 76.7) * mm, "end": v(-2.7, 76.7) * mm});
            skLineSegment(sketch, "E413.1.1.12", {"start": v(-127.3, 74.7) * mm, "end": v(-2.75, 74.7) * mm});
            skLineSegment(sketch, "E413.1.1.13", {"start": v(-127.3, 90.7) * mm, "end": v(-2.75, 90.7) * mm});
            skLineSegment(sketch, "E413.1.1.14", {"start": v(-127.25, 88.7) * mm, "end": v(-2.7, 88.7) * mm});
            skLineSegment(sketch, "E413.1.1.15", {"start": v(-127.3, 86.7) * mm, "end": v(-2.75, 86.7) * mm});
            skLineSegment(sketch, "E413.1.1.16", {"start": v(-127.3, 70.7) * mm, "end": v(-2.75, 70.7) * mm});
            skLineSegment(sketch, "E413.1.1.17", {"start": v(-121.52, 102.7) * mm, "end": v(-8.55, 102.7) * mm});
            skLineSegment(sketch, "E413.1.1.18", {"start": v(-127.25, 68.7) * mm, "end": v(-2.7, 68.7) * mm});
            skLineSegment(sketch, "E413.1.1.19", {"start": v(-127.25, 84.7) * mm, "end": v(-2.7, 84.7) * mm});
            skLineSegment(sketch, "E413.1.1.20", {"start": v(-115.4, 108.75) * mm, "end": v(-14.6, 108.75) * mm});
            skLineSegment(sketch, "E413.1.1.21", {"start": v(-127.25, 82.75) * mm, "end": v(-2.7, 82.75) * mm});
            skLineSegment(sketch, "E413.1.1.22", {"start": v(-127.3, 80.75) * mm, "end": v(-2.75, 80.75) * mm});
            skLineSegment(sketch, "E413.1.1.23", {"start": v(-127.25, 78.75) * mm, "end": v(-2.7, 78.75) * mm});
            skLineSegment(sketch, "E413.1.1.24", {"start": v(-127.25, 96.75) * mm, "end": v(-2.75, 96.75) * mm});
            skLineSegment(sketch, "E413.1.1.25", {"start": v(-127.25, 94.75) * mm, "end": v(-2.7, 94.75) * mm});
            skLineSegment(sketch, "E413.1.1.26", {"start": v(-127.3, 92.75) * mm, "end": v(-2.75, 92.75) * mm});
            skLineSegment(sketch, "E413.1.1.27", {"start": v(-127.3, 72.75) * mm, "end": v(-2.75, 72.75) * mm});
            skLineSegment(sketch, "E413.1.1.28", {"start": v(-127.3, 88.75) * mm, "end": v(-2.75, 88.75) * mm});
            skLineSegment(sketch, "E413.1.1.29", {"start": v(-121.4, 102.75) * mm, "end": v(-8.53, 102.75) * mm});
            skLineSegment(sketch, "E413.1.1.30", {"start": v(-127.25, 86.75) * mm, "end": v(-2.7, 86.75) * mm});
            skLineSegment(sketch, "E413.1.1.31", {"start": v(-127.3, 68.75) * mm, "end": v(-2.75, 68.75) * mm});
            skLineSegment(sketch, "E413.1.1.32", {"start": v(-125.4, 98.75) * mm, "end": v(-4.53, 98.75) * mm});
            skLineSegment(sketch, "E413.1.1.33", {"start": v(-127.3, 76.75) * mm, "end": v(-2.75, 76.75) * mm});
            skLineSegment(sketch, "E413.1.1.34", {"start": v(-127.25, 90.75) * mm, "end": v(-2.7, 90.75) * mm});
            skLineSegment(sketch, "E413.1.1.35", {"start": v(-127.25, 74.75) * mm, "end": v(-2.7, 74.75) * mm});
            skLineSegment(sketch, "E413.1.1.36", {"start": v(-117.4, 106.75) * mm, "end": v(-12.6, 106.75) * mm});
            skLineSegment(sketch, "E413.1.1.37", {"start": v(-127.25, 70.75) * mm, "end": v(-2.7, 70.75) * mm});
            skLineSegment(sketch, "E413.1.1.38", {"start": v(-119.47, 104.75) * mm, "end": v(-10.6, 104.75) * mm});
            skLineSegment(sketch, "E413.1.1.39", {"start": v(-115.42, 108.8) * mm, "end": v(-14.58, 108.8) * mm});
            skLineSegment(sketch, "E413.1.1.40", {"start": v(-2.5, 97) * mm, "end": v(-2.5, 67) * mm});
            skLineSegment(sketch, "E413.1.1.41", {"start": v(-123.47, 100.75) * mm, "end": v(-6.6, 100.75) * mm});
            skLineSegment(sketch, "E413.1.1.42", {"start": v(-127.3, 84.75) * mm, "end": v(-2.75, 84.75) * mm});
            skLineSegment(sketch, "E413.1.1.43", {"start": v(-8.53, 102.75) * mm, "end": v(-6.48, 100.7) * mm});
            skLineSegment(sketch, "E413.1.1.44", {"start": v(-8.55, 102.7) * mm, "end": v(-6.6, 100.75) * mm});
            skLineSegment(sketch, "E413.1.1.45", {"start": v(-119.47, 104.75) * mm, "end": v(-121.52, 102.7) * mm});
            skLineSegment(sketch, "E413.1.1.46", {"start": v(-115.5, 109) * mm, "end": v(-127.5, 97) * mm});
            skLineSegment(sketch, "E413.1.1.47", {"start": v(-115.5, 109) * mm, "end": v(-14.5, 109) * mm});
            skLineSegment(sketch, "E413.1.1.48", {"start": v(-14.5, 109) * mm, "end": v(-2.5, 97) * mm});
            skLineSegment(sketch, "E413.1.1.49", {"start": v(-119.45, 104.7) * mm, "end": v(-121.4, 102.75) * mm});
            skLineSegment(sketch, "E413.1.1.50", {"start": v(-127.3, 92.75) * mm, "end": v(-127.3, 90.75) * mm});
            skLineSegment(sketch, "E413.1.1.51", {"start": v(-123.47, 100.75) * mm, "end": v(-125.52, 98.7) * mm});
            skLineSegment(sketch, "E413.1.1.52", {"start": v(-12.55, 106.7) * mm, "end": v(-10.6, 104.75) * mm});
            skLineSegment(sketch, "E413.1.1.53", {"start": v(-127.3, 88.75) * mm, "end": v(-127.3, 86.7) * mm});
            skLineSegment(sketch, "E413.1.1.54", {"start": v(-4.53, 98.75) * mm, "end": v(-2.7, 96.92) * mm});
            skLineSegment(sketch, "E413.1.1.55", {"start": v(-2.7, 70.75) * mm, "end": v(-2.7, 68.7) * mm});
            skLineSegment(sketch, "E413.1.1.56", {"start": v(-2.75, 74.7) * mm, "end": v(-2.75, 72.75) * mm});
            skLineSegment(sketch, "E413.1.1.57", {"start": v(-4.55, 98.7) * mm, "end": v(-2.75, 96.9) * mm});
            skLineSegment(sketch, "E413.1.1.58", {"start": v(-123.45, 100.7) * mm, "end": v(-125.4, 98.75) * mm});
            skLineSegment(sketch, "E413.1.1.59", {"start": v(-2.75, 94.7) * mm, "end": v(-2.75, 92.75) * mm});
            skLineSegment(sketch, "E413.1.1.60", {"start": v(-127.3, 68.75) * mm, "end": v(-127.3, 67) * mm});
            skLineSegment(sketch, "E413.1.1.61", {"start": v(-127.3, 72.75) * mm, "end": v(-127.3, 70.7) * mm});
            skLineSegment(sketch, "E413.1.1.62", {"start": v(-2.75, 86.7) * mm, "end": v(-2.75, 84.75) * mm});
            skLineSegment(sketch, "E413.1.1.63", {"start": v(-115.42, 108.8) * mm, "end": v(-117.52, 106.7) * mm});
            skLineSegment(sketch, "E413.1.1.64", {"start": v(-14.58, 108.8) * mm, "end": v(-10.48, 104.7) * mm});
            skLineSegment(sketch, "E413.1.1.65", {"start": v(-2.75, 78.7) * mm, "end": v(-2.75, 76.75) * mm});
            skLineSegment(sketch, "E413.1.1.66", {"start": v(-127.3, 84.75) * mm, "end": v(-127.3, 82.7) * mm});
            skLineSegment(sketch, "E413.1.1.67", {"start": v(-2.75, 90.7) * mm, "end": v(-2.75, 88.75) * mm});
            skLineSegment(sketch, "E413.1.1.68", {"start": v(-2.75, 82.7) * mm, "end": v(-2.75, 80.75) * mm});
            skLineSegment(sketch, "E413.1.1.69", {"start": v(-127.3, 76.75) * mm, "end": v(-127.3, 74.75) * mm});
            skLineSegment(sketch, "E413.1.1.70", {"start": v(-2.7, 82.75) * mm, "end": v(-2.7, 80.7) * mm});
            skLineSegment(sketch, "E413.1.1.71", {"start": v(-127.3, 67) * mm, "end": v(-127.25, 67) * mm});
            skLineSegment(sketch, "E413.1.1.72", {"start": v(-127.5, 97) * mm, "end": v(-127.5, 67) * mm});
            skLineSegment(sketch, "E413.1.1.73", {"start": v(-127.25, 96.7) * mm, "end": v(-127.25, 94.75) * mm});
            skLineSegment(sketch, "E413.1.1.74", {"start": v(-2.75, 70.7) * mm, "end": v(-2.75, 68.75) * mm});
            skLineSegment(sketch, "E413.1.1.75", {"start": v(-127.25, 92.7) * mm, "end": v(-127.25, 90.75) * mm});
            skLineSegment(sketch, "E413.1.1.76", {"start": v(-2.7, 74.75) * mm, "end": v(-2.7, 72.75) * mm});
            skLineSegment(sketch, "E413.1.1.77", {"start": v(-127.25, 88.7) * mm, "end": v(-127.25, 86.7) * mm});
            skLineSegment(sketch, "E413.1.1.78", {"start": v(-127.25, 68.7) * mm, "end": v(-127.25, 67) * mm});
            skLineSegment(sketch, "E413.1.1.79", {"start": v(-2.7, 90.75) * mm, "end": v(-2.7, 88.7) * mm});
            skLineSegment(sketch, "E413.1.1.80", {"start": v(-127.25, 76.7) * mm, "end": v(-127.25, 74.75) * mm});
            skLineSegment(sketch, "E413.1.1.81", {"start": v(-2.7, 86.75) * mm, "end": v(-2.7, 84.7) * mm});
            skLineSegment(sketch, "E413.1.1.82", {"start": v(-14.6, 108.75) * mm, "end": v(-12.6, 106.75) * mm});
            skLineSegment(sketch, "E413.1.1.83", {"start": v(-127.25, 84.7) * mm, "end": v(-127.25, 82.75) * mm});
            skLineSegment(sketch, "E413.1.1.84", {"start": v(-2.7, 94.75) * mm, "end": v(-2.7, 92.7) * mm});
            skLineSegment(sketch, "E413.1.1.85", {"start": v(-127.25, 72.7) * mm, "end": v(-127.25, 70.75) * mm});
            skLineSegment(sketch, "E413.1.1.86", {"start": v(-127.3, 80.75) * mm, "end": v(-127.3, 78.75) * mm});
            skLineSegment(sketch, "E413.1.1.87", {"start": v(-127.3, 96.7) * mm, "end": v(-127.3, 94.7) * mm});
            skLineSegment(sketch, "E413.1.1.88", {"start": v(-115.4, 108.75) * mm, "end": v(-117.4, 106.75) * mm});
            skLineSegment(sketch, "E413.1.1.89", {"start": v(-2.7, 78.75) * mm, "end": v(-2.7, 76.7) * mm});
            skLineSegment(sketch, "E413.1.1.90", {"start": v(-127.3, 74.75) * mm, "end": v(-127.3, 74.7) * mm});
            skLineSegment(sketch, "E413.1.1.91", {"start": v(-127.3, 90.75) * mm, "end": v(-127.3, 90.7) * mm});
            skLineSegment(sketch, "E413.1.1.92", {"start": v(-127.25, 80.7) * mm, "end": v(-127.25, 78.75) * mm});
            skLineSegment(sketch, "E413.1.1.93", {"start": v(-127.3, 78.75) * mm, "end": v(-127.3, 78.7) * mm});
            skLineSegment(sketch, "E413.1.1.94", {"start": v(-2.7, 96.92) * mm, "end": v(-2.7, 96.7) * mm});
            skLineSegment(sketch, "E413.1.1.95", {"start": v(-127.3, 96.75) * mm, "end": v(-127.25, 96.75) * mm});
            skLineSegment(sketch, "E413.1.1.96", {"start": v(-2.7, 72.7) * mm, "end": v(-2.75, 72.7) * mm});
            skLineSegment(sketch, "E413.1.1.97", {"start": v(-2.75, 96.9) * mm, "end": v(-2.75, 96.75) * mm});
            skLineSegment(sketch, "E413.1.1.98", {"start": v(-127.3, 96.7) * mm, "end": v(-127.3, 96.75) * mm});
            skLineSegment(sketch, "E413.1.1.99", {"start": v(-2.7, 72.75) * mm, "end": v(-2.7, 72.7) * mm});
            skLineSegment(sketch, "E413.1.2.0", {"start": v(-127.25, 8.7) * mm, "end": v(-2.7, 8.7) * mm});
            skLineSegment(sketch, "E413.1.2.1", {"start": v(-127.3, -5.3) * mm, "end": v(-2.75, -5.3) * mm});
            skLineSegment(sketch, "E413.1.2.2", {"start": v(-127.3, 6.7) * mm, "end": v(-2.75, 6.7) * mm});
            skLineSegment(sketch, "E413.1.2.3", {"start": v(-127.25, -7.3) * mm, "end": v(-2.7, -7.3) * mm});
            skLineSegment(sketch, "E413.1.2.4", {"start": v(-127.3, -9.3) * mm, "end": v(-2.75, -9.3) * mm});
            skLineSegment(sketch, "E413.1.2.5", {"start": v(-125.52, 10.7) * mm, "end": v(-4.55, 10.7) * mm});
            skLineSegment(sketch, "E413.1.2.6", {"start": v(-127.25, 4.7) * mm, "end": v(-2.7, 4.7) * mm});
            skLineSegment(sketch, "E413.1.2.7", {"start": v(-117.52, 18.7) * mm, "end": v(-12.55, 18.7) * mm});
            skLineSegment(sketch, "E413.1.2.8", {"start": v(-127.25, -15.3) * mm, "end": v(-2.75, -15.3) * mm});
            skLineSegment(sketch, "E413.1.2.9", {"start": v(-123.45, 12.7) * mm, "end": v(-6.48, 12.7) * mm});
            skLineSegment(sketch, "E413.1.2.10", {"start": v(-119.45, 16.7) * mm, "end": v(-10.48, 16.7) * mm});
            skLineSegment(sketch, "E413.1.2.11", {"start": v(-127.25, -11.3) * mm, "end": v(-2.7, -11.3) * mm});
            skLineSegment(sketch, "E413.1.2.12", {"start": v(-127.3, -13.3) * mm, "end": v(-2.75, -13.3) * mm});
            skLineSegment(sketch, "E413.1.2.13", {"start": v(-127.3, 2.7) * mm, "end": v(-2.75, 2.7) * mm});
            skLineSegment(sketch, "E413.1.2.14", {"start": v(-127.25, 0.7) * mm, "end": v(-2.7, 0.7) * mm});
            skLineSegment(sketch, "E413.1.2.15", {"start": v(-127.3, -1.3) * mm, "end": v(-2.75, -1.3) * mm});
            skLineSegment(sketch, "E413.1.2.16", {"start": v(-127.3, -17.3) * mm, "end": v(-2.75, -17.3) * mm});
            skLineSegment(sketch, "E413.1.2.17", {"start": v(-121.52, 14.7) * mm, "end": v(-8.55, 14.7) * mm});
            skLineSegment(sketch, "E413.1.2.18", {"start": v(-127.25, -19.3) * mm, "end": v(-2.7, -19.3) * mm});
            skLineSegment(sketch, "E413.1.2.19", {"start": v(-127.25, -3.3) * mm, "end": v(-2.7, -3.3) * mm});
            skLineSegment(sketch, "E413.1.2.20", {"start": v(-115.4, 20.75) * mm, "end": v(-14.6, 20.75) * mm});
            skLineSegment(sketch, "E413.1.2.21", {"start": v(-127.25, -5.25) * mm, "end": v(-2.7, -5.25) * mm});
            skLineSegment(sketch, "E413.1.2.22", {"start": v(-127.3, -7.25) * mm, "end": v(-2.75, -7.25) * mm});
            skLineSegment(sketch, "E413.1.2.23", {"start": v(-127.25, -9.25) * mm, "end": v(-2.7, -9.25) * mm});
            skLineSegment(sketch, "E413.1.2.24", {"start": v(-127.25, 8.75) * mm, "end": v(-2.75, 8.75) * mm});
            skLineSegment(sketch, "E413.1.2.25", {"start": v(-127.25, 6.75) * mm, "end": v(-2.7, 6.75) * mm});
            skLineSegment(sketch, "E413.1.2.26", {"start": v(-127.3, 4.75) * mm, "end": v(-2.75, 4.75) * mm});
            skLineSegment(sketch, "E413.1.2.27", {"start": v(-127.3, -15.25) * mm, "end": v(-2.75, -15.25) * mm});
            skLineSegment(sketch, "E413.1.2.28", {"start": v(-127.3, 0.75) * mm, "end": v(-2.75, 0.75) * mm});
            skLineSegment(sketch, "E413.1.2.29", {"start": v(-121.4, 14.75) * mm, "end": v(-8.53, 14.75) * mm});
            skLineSegment(sketch, "E413.1.2.30", {"start": v(-127.25, -1.25) * mm, "end": v(-2.7, -1.25) * mm});
            skLineSegment(sketch, "E413.1.2.31", {"start": v(-127.3, -19.25) * mm, "end": v(-2.75, -19.25) * mm});
            skLineSegment(sketch, "E413.1.2.32", {"start": v(-125.4, 10.75) * mm, "end": v(-4.53, 10.75) * mm});
            skLineSegment(sketch, "E413.1.2.33", {"start": v(-127.3, -11.25) * mm, "end": v(-2.75, -11.25) * mm});
            skLineSegment(sketch, "E413.1.2.34", {"start": v(-127.25, 2.75) * mm, "end": v(-2.7, 2.75) * mm});
            skLineSegment(sketch, "E413.1.2.35", {"start": v(-127.25, -13.25) * mm, "end": v(-2.7, -13.25) * mm});
            skLineSegment(sketch, "E413.1.2.36", {"start": v(-117.4, 18.75) * mm, "end": v(-12.6, 18.75) * mm});
            skLineSegment(sketch, "E413.1.2.37", {"start": v(-127.25, -17.25) * mm, "end": v(-2.7, -17.25) * mm});
            skLineSegment(sketch, "E413.1.2.38", {"start": v(-119.47, 16.75) * mm, "end": v(-10.6, 16.75) * mm});
            skLineSegment(sketch, "E413.1.2.39", {"start": v(-115.42, 20.8) * mm, "end": v(-14.58, 20.8) * mm});
            skLineSegment(sketch, "E413.1.2.40", {"start": v(-2.5, 9) * mm, "end": v(-2.5, -21) * mm});
            skLineSegment(sketch, "E413.1.2.41", {"start": v(-123.47, 12.75) * mm, "end": v(-6.6, 12.75) * mm});
            skLineSegment(sketch, "E413.1.2.42", {"start": v(-127.3, -3.25) * mm, "end": v(-2.75, -3.25) * mm});
            skLineSegment(sketch, "E413.1.2.43", {"start": v(-8.53, 14.75) * mm, "end": v(-6.48, 12.7) * mm});
            skLineSegment(sketch, "E413.1.2.44", {"start": v(-8.55, 14.7) * mm, "end": v(-6.6, 12.75) * mm});
            skLineSegment(sketch, "E413.1.2.45", {"start": v(-119.47, 16.75) * mm, "end": v(-121.52, 14.7) * mm});
            skLineSegment(sketch, "E413.1.2.46", {"start": v(-115.5, 21) * mm, "end": v(-127.5, 9) * mm});
            skLineSegment(sketch, "E413.1.2.47", {"start": v(-115.5, 21) * mm, "end": v(-14.5, 21) * mm});
            skLineSegment(sketch, "E413.1.2.48", {"start": v(-14.5, 21) * mm, "end": v(-2.5, 9) * mm});
            skLineSegment(sketch, "E413.1.2.49", {"start": v(-119.45, 16.7) * mm, "end": v(-121.4, 14.75) * mm});
            skLineSegment(sketch, "E413.1.2.50", {"start": v(-127.3, 4.75) * mm, "end": v(-127.3, 2.75) * mm});
            skLineSegment(sketch, "E413.1.2.51", {"start": v(-123.47, 12.75) * mm, "end": v(-125.52, 10.7) * mm});
            skLineSegment(sketch, "E413.1.2.52", {"start": v(-12.55, 18.7) * mm, "end": v(-10.6, 16.75) * mm});
            skLineSegment(sketch, "E413.1.2.53", {"start": v(-127.3, 0.75) * mm, "end": v(-127.3, -1.3) * mm});
            skLineSegment(sketch, "E413.1.2.54", {"start": v(-4.53, 10.75) * mm, "end": v(-2.7, 8.92) * mm});
            skLineSegment(sketch, "E413.1.2.55", {"start": v(-2.7, -17.25) * mm, "end": v(-2.7, -19.3) * mm});
            skLineSegment(sketch, "E413.1.2.56", {"start": v(-2.75, -13.3) * mm, "end": v(-2.75, -15.25) * mm});
            skLineSegment(sketch, "E413.1.2.57", {"start": v(-4.55, 10.7) * mm, "end": v(-2.75, 8.9) * mm});
            skLineSegment(sketch, "E413.1.2.58", {"start": v(-123.45, 12.7) * mm, "end": v(-125.4, 10.75) * mm});
            skLineSegment(sketch, "E413.1.2.59", {"start": v(-2.75, 6.7) * mm, "end": v(-2.75, 4.75) * mm});
            skLineSegment(sketch, "E413.1.2.60", {"start": v(-127.3, -19.25) * mm, "end": v(-127.3, -21) * mm});
            skLineSegment(sketch, "E413.1.2.61", {"start": v(-127.3, -15.25) * mm, "end": v(-127.3, -17.3) * mm});
            skLineSegment(sketch, "E413.1.2.62", {"start": v(-2.75, -1.3) * mm, "end": v(-2.75, -3.25) * mm});
            skLineSegment(sketch, "E413.1.2.63", {"start": v(-115.42, 20.8) * mm, "end": v(-117.52, 18.7) * mm});
            skLineSegment(sketch, "E413.1.2.64", {"start": v(-14.58, 20.8) * mm, "end": v(-10.48, 16.7) * mm});
            skLineSegment(sketch, "E413.1.2.65", {"start": v(-2.75, -9.3) * mm, "end": v(-2.75, -11.25) * mm});
            skLineSegment(sketch, "E413.1.2.66", {"start": v(-127.3, -3.25) * mm, "end": v(-127.3, -5.3) * mm});
            skLineSegment(sketch, "E413.1.2.67", {"start": v(-2.75, 2.7) * mm, "end": v(-2.75, 0.75) * mm});
            skLineSegment(sketch, "E413.1.2.68", {"start": v(-2.75, -5.3) * mm, "end": v(-2.75, -7.25) * mm});
            skLineSegment(sketch, "E413.1.2.69", {"start": v(-127.3, -11.25) * mm, "end": v(-127.3, -13.25) * mm});
            skLineSegment(sketch, "E413.1.2.70", {"start": v(-2.7, -5.25) * mm, "end": v(-2.7, -7.3) * mm});
            skLineSegment(sketch, "E413.1.2.71", {"start": v(-127.3, -21) * mm, "end": v(-127.25, -21) * mm});
            skLineSegment(sketch, "E413.1.2.72", {"start": v(-127.5, 9) * mm, "end": v(-127.5, -21) * mm});
            skLineSegment(sketch, "E413.1.2.73", {"start": v(-127.25, 8.7) * mm, "end": v(-127.25, 6.75) * mm});
            skLineSegment(sketch, "E413.1.2.74", {"start": v(-2.75, -17.3) * mm, "end": v(-2.75, -19.25) * mm});
            skLineSegment(sketch, "E413.1.2.75", {"start": v(-127.25, 4.7) * mm, "end": v(-127.25, 2.75) * mm});
            skLineSegment(sketch, "E413.1.2.76", {"start": v(-2.7, -13.25) * mm, "end": v(-2.7, -15.25) * mm});
            skLineSegment(sketch, "E413.1.2.77", {"start": v(-127.25, 0.7) * mm, "end": v(-127.25, -1.3) * mm});
            skLineSegment(sketch, "E413.1.2.78", {"start": v(-127.25, -19.3) * mm, "end": v(-127.25, -21) * mm});
            skLineSegment(sketch, "E413.1.2.79", {"start": v(-2.7, 2.75) * mm, "end": v(-2.7, 0.7) * mm});
            skLineSegment(sketch, "E413.1.2.80", {"start": v(-127.25, -11.3) * mm, "end": v(-127.25, -13.25) * mm});
            skLineSegment(sketch, "E413.1.2.81", {"start": v(-2.7, -1.25) * mm, "end": v(-2.7, -3.3) * mm});
            skLineSegment(sketch, "E413.1.2.82", {"start": v(-14.6, 20.75) * mm, "end": v(-12.6, 18.75) * mm});
            skLineSegment(sketch, "E413.1.2.83", {"start": v(-127.25, -3.3) * mm, "end": v(-127.25, -5.25) * mm});
            skLineSegment(sketch, "E413.1.2.84", {"start": v(-2.7, 6.75) * mm, "end": v(-2.7, 4.7) * mm});
            skLineSegment(sketch, "E413.1.2.85", {"start": v(-127.25, -15.3) * mm, "end": v(-127.25, -17.25) * mm});
            skLineSegment(sketch, "E413.1.2.86", {"start": v(-127.3, -7.25) * mm, "end": v(-127.3, -9.25) * mm});
            skLineSegment(sketch, "E413.1.2.87", {"start": v(-127.3, 8.7) * mm, "end": v(-127.3, 6.7) * mm});
            skLineSegment(sketch, "E413.1.2.88", {"start": v(-115.4, 20.75) * mm, "end": v(-117.4, 18.75) * mm});
            skLineSegment(sketch, "E413.1.2.89", {"start": v(-2.7, -9.25) * mm, "end": v(-2.7, -11.3) * mm});
            skLineSegment(sketch, "E413.1.2.90", {"start": v(-127.3, -13.25) * mm, "end": v(-127.3, -13.3) * mm});
            skLineSegment(sketch, "E413.1.2.91", {"start": v(-127.3, 2.75) * mm, "end": v(-127.3, 2.7) * mm});
            skLineSegment(sketch, "E413.1.2.92", {"start": v(-127.25, -7.3) * mm, "end": v(-127.25, -9.25) * mm});
            skLineSegment(sketch, "E413.1.2.93", {"start": v(-127.3, -9.25) * mm, "end": v(-127.3, -9.3) * mm});
            skLineSegment(sketch, "E413.1.2.94", {"start": v(-2.7, 8.92) * mm, "end": v(-2.7, 8.7) * mm});
            skLineSegment(sketch, "E413.1.2.95", {"start": v(-127.3, 8.75) * mm, "end": v(-127.25, 8.75) * mm});
            skLineSegment(sketch, "E413.1.2.96", {"start": v(-2.7, -15.3) * mm, "end": v(-2.75, -15.3) * mm});
            skLineSegment(sketch, "E413.1.2.97", {"start": v(-2.75, 8.9) * mm, "end": v(-2.75, 8.75) * mm});
            skLineSegment(sketch, "E413.1.2.98", {"start": v(-127.3, 8.7) * mm, "end": v(-127.3, 8.75) * mm});
            skLineSegment(sketch, "E413.1.2.99", {"start": v(-2.7, -15.25) * mm, "end": v(-2.7, -15.3) * mm});
            skLineSegment(sketch, "E413.1.3.0", {"start": v(-127.25, -79.3) * mm, "end": v(-2.7, -79.3) * mm});
            skLineSegment(sketch, "E413.1.3.1", {"start": v(-127.3, -93.3) * mm, "end": v(-2.75, -93.3) * mm});
            skLineSegment(sketch, "E413.1.3.2", {"start": v(-127.3, -81.3) * mm, "end": v(-2.75, -81.3) * mm});
            skLineSegment(sketch, "E413.1.3.3", {"start": v(-127.25, -95.3) * mm, "end": v(-2.7, -95.3) * mm});
            skLineSegment(sketch, "E413.1.3.4", {"start": v(-127.3, -97.3) * mm, "end": v(-2.75, -97.3) * mm});
            skLineSegment(sketch, "E413.1.3.5", {"start": v(-125.52, -77.3) * mm, "end": v(-4.55, -77.3) * mm});
            skLineSegment(sketch, "E413.1.3.6", {"start": v(-127.25, -83.3) * mm, "end": v(-2.7, -83.3) * mm});
            skLineSegment(sketch, "E413.1.3.7", {"start": v(-117.52, -69.3) * mm, "end": v(-12.55, -69.3) * mm});
            skLineSegment(sketch, "E413.1.3.8", {"start": v(-127.25, -103.3) * mm, "end": v(-2.75, -103.3) * mm});
            skLineSegment(sketch, "E413.1.3.9", {"start": v(-123.45, -75.3) * mm, "end": v(-6.48, -75.3) * mm});
            skLineSegment(sketch, "E413.1.3.10", {"start": v(-119.45, -71.3) * mm, "end": v(-10.48, -71.3) * mm});
            skLineSegment(sketch, "E413.1.3.11", {"start": v(-127.25, -99.3) * mm, "end": v(-2.7, -99.3) * mm});
            skLineSegment(sketch, "E413.1.3.12", {"start": v(-127.3, -101.3) * mm, "end": v(-2.75, -101.3) * mm});
            skLineSegment(sketch, "E413.1.3.13", {"start": v(-127.3, -85.3) * mm, "end": v(-2.75, -85.3) * mm});
            skLineSegment(sketch, "E413.1.3.14", {"start": v(-127.25, -87.3) * mm, "end": v(-2.7, -87.3) * mm});
            skLineSegment(sketch, "E413.1.3.15", {"start": v(-127.3, -89.3) * mm, "end": v(-2.75, -89.3) * mm});
            skLineSegment(sketch, "E413.1.3.16", {"start": v(-127.3, -105.3) * mm, "end": v(-2.75, -105.3) * mm});
            skLineSegment(sketch, "E413.1.3.17", {"start": v(-121.52, -73.3) * mm, "end": v(-8.55, -73.3) * mm});
            skLineSegment(sketch, "E413.1.3.18", {"start": v(-127.25, -107.3) * mm, "end": v(-2.7, -107.3) * mm});
            skLineSegment(sketch, "E413.1.3.19", {"start": v(-127.25, -91.3) * mm, "end": v(-2.7, -91.3) * mm});
            skLineSegment(sketch, "E413.1.3.20", {"start": v(-115.4, -67.25) * mm, "end": v(-14.6, -67.25) * mm});
            skLineSegment(sketch, "E413.1.3.21", {"start": v(-127.25, -93.25) * mm, "end": v(-2.7, -93.25) * mm});
            skLineSegment(sketch, "E413.1.3.22", {"start": v(-127.3, -95.25) * mm, "end": v(-2.75, -95.25) * mm});
            skLineSegment(sketch, "E413.1.3.23", {"start": v(-127.25, -97.25) * mm, "end": v(-2.7, -97.25) * mm});
            skLineSegment(sketch, "E413.1.3.24", {"start": v(-127.25, -79.25) * mm, "end": v(-2.75, -79.25) * mm});
            skLineSegment(sketch, "E413.1.3.25", {"start": v(-127.25, -81.25) * mm, "end": v(-2.7, -81.25) * mm});
            skLineSegment(sketch, "E413.1.3.26", {"start": v(-127.3, -83.25) * mm, "end": v(-2.75, -83.25) * mm});
            skLineSegment(sketch, "E413.1.3.27", {"start": v(-127.3, -103.25) * mm, "end": v(-2.75, -103.25) * mm});
            skLineSegment(sketch, "E413.1.3.28", {"start": v(-127.3, -87.25) * mm, "end": v(-2.75, -87.25) * mm});
            skLineSegment(sketch, "E413.1.3.29", {"start": v(-121.4, -73.25) * mm, "end": v(-8.53, -73.25) * mm});
            skLineSegment(sketch, "E413.1.3.30", {"start": v(-127.25, -89.25) * mm, "end": v(-2.7, -89.25) * mm});
            skLineSegment(sketch, "E413.1.3.31", {"start": v(-127.3, -107.25) * mm, "end": v(-2.75, -107.25) * mm});
            skLineSegment(sketch, "E413.1.3.32", {"start": v(-125.4, -77.25) * mm, "end": v(-4.53, -77.25) * mm});
            skLineSegment(sketch, "E413.1.3.33", {"start": v(-127.3, -99.25) * mm, "end": v(-2.75, -99.25) * mm});
            skLineSegment(sketch, "E413.1.3.34", {"start": v(-127.25, -85.25) * mm, "end": v(-2.7, -85.25) * mm});
            skLineSegment(sketch, "E413.1.3.35", {"start": v(-127.25, -101.25) * mm, "end": v(-2.7, -101.25) * mm});
            skLineSegment(sketch, "E413.1.3.36", {"start": v(-117.4, -69.25) * mm, "end": v(-12.6, -69.25) * mm});
            skLineSegment(sketch, "E413.1.3.37", {"start": v(-127.25, -105.25) * mm, "end": v(-2.7, -105.25) * mm});
            skLineSegment(sketch, "E413.1.3.38", {"start": v(-119.47, -71.25) * mm, "end": v(-10.6, -71.25) * mm});
            skLineSegment(sketch, "E413.1.3.39", {"start": v(-115.42, -67.2) * mm, "end": v(-14.58, -67.2) * mm});
            skLineSegment(sketch, "E413.1.3.40", {"start": v(-2.5, -79) * mm, "end": v(-2.5, -109) * mm});
            skLineSegment(sketch, "E413.1.3.41", {"start": v(-123.47, -75.25) * mm, "end": v(-6.6, -75.25) * mm});
            skLineSegment(sketch, "E413.1.3.42", {"start": v(-127.3, -91.25) * mm, "end": v(-2.75, -91.25) * mm});
            skLineSegment(sketch, "E413.1.3.43", {"start": v(-8.53, -73.25) * mm, "end": v(-6.48, -75.3) * mm});
            skLineSegment(sketch, "E413.1.3.44", {"start": v(-8.55, -73.3) * mm, "end": v(-6.6, -75.25) * mm});
            skLineSegment(sketch, "E413.1.3.45", {"start": v(-119.47, -71.25) * mm, "end": v(-121.52, -73.3) * mm});
            skLineSegment(sketch, "E413.1.3.46", {"start": v(-115.5, -67) * mm, "end": v(-127.5, -79) * mm});
            skLineSegment(sketch, "E413.1.3.47", {"start": v(-115.5, -67) * mm, "end": v(-14.5, -67) * mm});
            skLineSegment(sketch, "E413.1.3.48", {"start": v(-14.5, -67) * mm, "end": v(-2.5, -79) * mm});
            skLineSegment(sketch, "E413.1.3.49", {"start": v(-119.45, -71.3) * mm, "end": v(-121.4, -73.25) * mm});
            skLineSegment(sketch, "E413.1.3.50", {"start": v(-127.3, -83.25) * mm, "end": v(-127.3, -85.25) * mm});
            skLineSegment(sketch, "E413.1.3.51", {"start": v(-123.47, -75.25) * mm, "end": v(-125.52, -77.3) * mm});
            skLineSegment(sketch, "E413.1.3.52", {"start": v(-12.55, -69.3) * mm, "end": v(-10.6, -71.25) * mm});
            skLineSegment(sketch, "E413.1.3.53", {"start": v(-127.3, -87.25) * mm, "end": v(-127.3, -89.3) * mm});
            skLineSegment(sketch, "E413.1.3.54", {"start": v(-4.53, -77.25) * mm, "end": v(-2.7, -79.08) * mm});
            skLineSegment(sketch, "E413.1.3.55", {"start": v(-2.7, -105.25) * mm, "end": v(-2.7, -107.3) * mm});
            skLineSegment(sketch, "E413.1.3.56", {"start": v(-2.75, -101.3) * mm, "end": v(-2.75, -103.25) * mm});
            skLineSegment(sketch, "E413.1.3.57", {"start": v(-4.55, -77.3) * mm, "end": v(-2.75, -79.1) * mm});
            skLineSegment(sketch, "E413.1.3.58", {"start": v(-123.45, -75.3) * mm, "end": v(-125.4, -77.25) * mm});
            skLineSegment(sketch, "E413.1.3.59", {"start": v(-2.75, -81.3) * mm, "end": v(-2.75, -83.25) * mm});
            skLineSegment(sketch, "E413.1.3.60", {"start": v(-127.3, -107.25) * mm, "end": v(-127.3, -109) * mm});
            skLineSegment(sketch, "E413.1.3.61", {"start": v(-127.3, -103.25) * mm, "end": v(-127.3, -105.3) * mm});
            skLineSegment(sketch, "E413.1.3.62", {"start": v(-2.75, -89.3) * mm, "end": v(-2.75, -91.25) * mm});
            skLineSegment(sketch, "E413.1.3.63", {"start": v(-115.42, -67.2) * mm, "end": v(-117.52, -69.3) * mm});
            skLineSegment(sketch, "E413.1.3.64", {"start": v(-14.58, -67.2) * mm, "end": v(-10.48, -71.3) * mm});
            skLineSegment(sketch, "E413.1.3.65", {"start": v(-2.75, -97.3) * mm, "end": v(-2.75, -99.25) * mm});
            skLineSegment(sketch, "E413.1.3.66", {"start": v(-127.3, -91.25) * mm, "end": v(-127.3, -93.3) * mm});
            skLineSegment(sketch, "E413.1.3.67", {"start": v(-2.75, -85.3) * mm, "end": v(-2.75, -87.25) * mm});
            skLineSegment(sketch, "E413.1.3.68", {"start": v(-2.75, -93.3) * mm, "end": v(-2.75, -95.25) * mm});
            skLineSegment(sketch, "E413.1.3.69", {"start": v(-127.3, -99.25) * mm, "end": v(-127.3, -101.25) * mm});
            skLineSegment(sketch, "E413.1.3.70", {"start": v(-2.7, -93.25) * mm, "end": v(-2.7, -95.3) * mm});
            skLineSegment(sketch, "E413.1.3.71", {"start": v(-127.3, -109) * mm, "end": v(-127.25, -109) * mm});
            skLineSegment(sketch, "E413.1.3.72", {"start": v(-127.5, -79) * mm, "end": v(-127.5, -109) * mm});
            skLineSegment(sketch, "E413.1.3.73", {"start": v(-127.25, -79.3) * mm, "end": v(-127.25, -81.25) * mm});
            skLineSegment(sketch, "E413.1.3.74", {"start": v(-2.75, -105.3) * mm, "end": v(-2.75, -107.25) * mm});
            skLineSegment(sketch, "E413.1.3.75", {"start": v(-127.25, -83.3) * mm, "end": v(-127.25, -85.25) * mm});
            skLineSegment(sketch, "E413.1.3.76", {"start": v(-2.7, -101.25) * mm, "end": v(-2.7, -103.25) * mm});
            skLineSegment(sketch, "E413.1.3.77", {"start": v(-127.25, -87.3) * mm, "end": v(-127.25, -89.3) * mm});
            skLineSegment(sketch, "E413.1.3.78", {"start": v(-127.25, -107.3) * mm, "end": v(-127.25, -109) * mm});
            skLineSegment(sketch, "E413.1.3.79", {"start": v(-2.7, -85.25) * mm, "end": v(-2.7, -87.3) * mm});
            skLineSegment(sketch, "E413.1.3.80", {"start": v(-127.25, -99.3) * mm, "end": v(-127.25, -101.25) * mm});
            skLineSegment(sketch, "E413.1.3.81", {"start": v(-2.7, -89.25) * mm, "end": v(-2.7, -91.3) * mm});
            skLineSegment(sketch, "E413.1.3.82", {"start": v(-14.6, -67.25) * mm, "end": v(-12.6, -69.25) * mm});
            skLineSegment(sketch, "E413.1.3.83", {"start": v(-127.25, -91.3) * mm, "end": v(-127.25, -93.25) * mm});
            skLineSegment(sketch, "E413.1.3.84", {"start": v(-2.7, -81.25) * mm, "end": v(-2.7, -83.3) * mm});
            skLineSegment(sketch, "E413.1.3.85", {"start": v(-127.25, -103.3) * mm, "end": v(-127.25, -105.25) * mm});
            skLineSegment(sketch, "E413.1.3.86", {"start": v(-127.3, -95.25) * mm, "end": v(-127.3, -97.25) * mm});
            skLineSegment(sketch, "E413.1.3.87", {"start": v(-127.3, -79.3) * mm, "end": v(-127.3, -81.3) * mm});
            skLineSegment(sketch, "E413.1.3.88", {"start": v(-115.4, -67.25) * mm, "end": v(-117.4, -69.25) * mm});
            skLineSegment(sketch, "E413.1.3.89", {"start": v(-2.7, -97.25) * mm, "end": v(-2.7, -99.3) * mm});
            skLineSegment(sketch, "E413.1.3.90", {"start": v(-127.3, -101.25) * mm, "end": v(-127.3, -101.3) * mm});
            skLineSegment(sketch, "E413.1.3.91", {"start": v(-127.3, -85.25) * mm, "end": v(-127.3, -85.3) * mm});
            skLineSegment(sketch, "E413.1.3.92", {"start": v(-127.25, -95.3) * mm, "end": v(-127.25, -97.25) * mm});
            skLineSegment(sketch, "E413.1.3.93", {"start": v(-127.3, -97.25) * mm, "end": v(-127.3, -97.3) * mm});
            skLineSegment(sketch, "E413.1.3.94", {"start": v(-2.7, -79.08) * mm, "end": v(-2.7, -79.3) * mm});
            skLineSegment(sketch, "E413.1.3.95", {"start": v(-127.3, -79.25) * mm, "end": v(-127.25, -79.25) * mm});
            skLineSegment(sketch, "E413.1.3.96", {"start": v(-2.7, -103.3) * mm, "end": v(-2.75, -103.3) * mm});
            skLineSegment(sketch, "E413.1.3.97", {"start": v(-2.75, -79.1) * mm, "end": v(-2.75, -79.25) * mm});
            skLineSegment(sketch, "E413.1.3.98", {"start": v(-127.3, -79.3) * mm, "end": v(-127.3, -79.25) * mm});
            skLineSegment(sketch, "E413.1.3.99", {"start": v(-2.7, -103.25) * mm, "end": v(-2.7, -103.3) * mm});
            skLineSegment(sketch, "E413.1.4.0", {"start": v(-127.25, -167.3) * mm, "end": v(-2.7, -167.3) * mm});
            skLineSegment(sketch, "E413.1.4.1", {"start": v(-127.3, -181.3) * mm, "end": v(-2.75, -181.3) * mm});
            skLineSegment(sketch, "E413.1.4.2", {"start": v(-127.3, -169.3) * mm, "end": v(-2.75, -169.3) * mm});
            skLineSegment(sketch, "E413.1.4.3", {"start": v(-127.25, -183.3) * mm, "end": v(-2.7, -183.3) * mm});
            skLineSegment(sketch, "E413.1.4.4", {"start": v(-127.3, -185.3) * mm, "end": v(-2.75, -185.3) * mm});
            skLineSegment(sketch, "E413.1.4.5", {"start": v(-125.52, -165.3) * mm, "end": v(-4.55, -165.3) * mm});
            skLineSegment(sketch, "E413.1.4.6", {"start": v(-127.25, -171.3) * mm, "end": v(-2.7, -171.3) * mm});
            skLineSegment(sketch, "E413.1.4.7", {"start": v(-117.52, -157.3) * mm, "end": v(-12.55, -157.3) * mm});
            skLineSegment(sketch, "E413.1.4.8", {"start": v(-127.25, -191.3) * mm, "end": v(-2.75, -191.3) * mm});
            skLineSegment(sketch, "E413.1.4.9", {"start": v(-123.45, -163.3) * mm, "end": v(-6.48, -163.3) * mm});
            skLineSegment(sketch, "E413.1.4.10", {"start": v(-119.45, -159.3) * mm, "end": v(-10.48, -159.3) * mm});
            skLineSegment(sketch, "E413.1.4.11", {"start": v(-127.25, -187.3) * mm, "end": v(-2.7, -187.3) * mm});
            skLineSegment(sketch, "E413.1.4.12", {"start": v(-127.3, -189.3) * mm, "end": v(-2.75, -189.3) * mm});
            skLineSegment(sketch, "E413.1.4.13", {"start": v(-127.3, -173.3) * mm, "end": v(-2.75, -173.3) * mm});
            skLineSegment(sketch, "E413.1.4.14", {"start": v(-127.25, -175.3) * mm, "end": v(-2.7, -175.3) * mm});
            skLineSegment(sketch, "E413.1.4.15", {"start": v(-127.3, -177.3) * mm, "end": v(-2.75, -177.3) * mm});
            skLineSegment(sketch, "E413.1.4.16", {"start": v(-127.3, -193.3) * mm, "end": v(-2.75, -193.3) * mm});
            skLineSegment(sketch, "E413.1.4.17", {"start": v(-121.52, -161.3) * mm, "end": v(-8.55, -161.3) * mm});
            skLineSegment(sketch, "E413.1.4.18", {"start": v(-127.25, -195.3) * mm, "end": v(-2.7, -195.3) * mm});
            skLineSegment(sketch, "E413.1.4.19", {"start": v(-127.25, -179.3) * mm, "end": v(-2.7, -179.3) * mm});
            skLineSegment(sketch, "E413.1.4.20", {"start": v(-115.4, -155.25) * mm, "end": v(-14.6, -155.25) * mm});
            skLineSegment(sketch, "E413.1.4.21", {"start": v(-127.25, -181.25) * mm, "end": v(-2.7, -181.25) * mm});
            skLineSegment(sketch, "E413.1.4.22", {"start": v(-127.3, -183.25) * mm, "end": v(-2.75, -183.25) * mm});
            skLineSegment(sketch, "E413.1.4.23", {"start": v(-127.25, -185.25) * mm, "end": v(-2.7, -185.25) * mm});
            skLineSegment(sketch, "E413.1.4.24", {"start": v(-127.25, -167.25) * mm, "end": v(-2.75, -167.25) * mm});
            skLineSegment(sketch, "E413.1.4.25", {"start": v(-127.25, -169.25) * mm, "end": v(-2.7, -169.25) * mm});
            skLineSegment(sketch, "E413.1.4.26", {"start": v(-127.3, -171.25) * mm, "end": v(-2.75, -171.25) * mm});
            skLineSegment(sketch, "E413.1.4.27", {"start": v(-127.3, -191.25) * mm, "end": v(-2.75, -191.25) * mm});
            skLineSegment(sketch, "E413.1.4.28", {"start": v(-127.3, -175.25) * mm, "end": v(-2.75, -175.25) * mm});
            skLineSegment(sketch, "E413.1.4.29", {"start": v(-121.4, -161.25) * mm, "end": v(-8.53, -161.25) * mm});
            skLineSegment(sketch, "E413.1.4.30", {"start": v(-127.25, -177.25) * mm, "end": v(-2.7, -177.25) * mm});
            skLineSegment(sketch, "E413.1.4.31", {"start": v(-127.3, -195.25) * mm, "end": v(-2.75, -195.25) * mm});
            skLineSegment(sketch, "E413.1.4.32", {"start": v(-125.4, -165.25) * mm, "end": v(-4.53, -165.25) * mm});
            skLineSegment(sketch, "E413.1.4.33", {"start": v(-127.3, -187.25) * mm, "end": v(-2.75, -187.25) * mm});
            skLineSegment(sketch, "E413.1.4.34", {"start": v(-127.25, -173.25) * mm, "end": v(-2.7, -173.25) * mm});
            skLineSegment(sketch, "E413.1.4.35", {"start": v(-127.25, -189.25) * mm, "end": v(-2.7, -189.25) * mm});
            skLineSegment(sketch, "E413.1.4.36", {"start": v(-117.4, -157.25) * mm, "end": v(-12.6, -157.25) * mm});
            skLineSegment(sketch, "E413.1.4.37", {"start": v(-127.25, -193.25) * mm, "end": v(-2.7, -193.25) * mm});
            skLineSegment(sketch, "E413.1.4.38", {"start": v(-119.47, -159.25) * mm, "end": v(-10.6, -159.25) * mm});
            skLineSegment(sketch, "E413.1.4.39", {"start": v(-115.42, -155.2) * mm, "end": v(-14.58, -155.2) * mm});
            skLineSegment(sketch, "E413.1.4.40", {"start": v(-2.5, -167) * mm, "end": v(-2.5, -197) * mm});
            skLineSegment(sketch, "E413.1.4.41", {"start": v(-123.47, -163.25) * mm, "end": v(-6.6, -163.25) * mm});
            skLineSegment(sketch, "E413.1.4.42", {"start": v(-127.3, -179.25) * mm, "end": v(-2.75, -179.25) * mm});
            skLineSegment(sketch, "E413.1.4.43", {"start": v(-8.53, -161.25) * mm, "end": v(-6.48, -163.3) * mm});
            skLineSegment(sketch, "E413.1.4.44", {"start": v(-8.55, -161.3) * mm, "end": v(-6.6, -163.25) * mm});
            skLineSegment(sketch, "E413.1.4.45", {"start": v(-119.47, -159.25) * mm, "end": v(-121.52, -161.3) * mm});
            skLineSegment(sketch, "E413.1.4.46", {"start": v(-115.5, -155) * mm, "end": v(-127.5, -167) * mm});
            skLineSegment(sketch, "E413.1.4.47", {"start": v(-115.5, -155) * mm, "end": v(-14.5, -155) * mm});
            skLineSegment(sketch, "E413.1.4.48", {"start": v(-14.5, -155) * mm, "end": v(-2.5, -167) * mm});
            skLineSegment(sketch, "E413.1.4.49", {"start": v(-119.45, -159.3) * mm, "end": v(-121.4, -161.25) * mm});
            skLineSegment(sketch, "E413.1.4.50", {"start": v(-127.3, -171.25) * mm, "end": v(-127.3, -173.25) * mm});
            skLineSegment(sketch, "E413.1.4.51", {"start": v(-123.47, -163.25) * mm, "end": v(-125.52, -165.3) * mm});
            skLineSegment(sketch, "E413.1.4.52", {"start": v(-12.55, -157.3) * mm, "end": v(-10.6, -159.25) * mm});
            skLineSegment(sketch, "E413.1.4.53", {"start": v(-127.3, -175.25) * mm, "end": v(-127.3, -177.3) * mm});
            skLineSegment(sketch, "E413.1.4.54", {"start": v(-4.53, -165.25) * mm, "end": v(-2.7, -167.08) * mm});
            skLineSegment(sketch, "E413.1.4.55", {"start": v(-2.7, -193.25) * mm, "end": v(-2.7, -195.3) * mm});
            skLineSegment(sketch, "E413.1.4.56", {"start": v(-2.75, -189.3) * mm, "end": v(-2.75, -191.25) * mm});
            skLineSegment(sketch, "E413.1.4.57", {"start": v(-4.55, -165.3) * mm, "end": v(-2.75, -167.1) * mm});
            skLineSegment(sketch, "E413.1.4.58", {"start": v(-123.45, -163.3) * mm, "end": v(-125.4, -165.25) * mm});
            skLineSegment(sketch, "E413.1.4.59", {"start": v(-2.75, -169.3) * mm, "end": v(-2.75, -171.25) * mm});
            skLineSegment(sketch, "E413.1.4.60", {"start": v(-127.3, -195.25) * mm, "end": v(-127.3, -197) * mm});
            skLineSegment(sketch, "E413.1.4.61", {"start": v(-127.3, -191.25) * mm, "end": v(-127.3, -193.3) * mm});
            skLineSegment(sketch, "E413.1.4.62", {"start": v(-2.75, -177.3) * mm, "end": v(-2.75, -179.25) * mm});
            skLineSegment(sketch, "E413.1.4.63", {"start": v(-115.42, -155.2) * mm, "end": v(-117.52, -157.3) * mm});
            skLineSegment(sketch, "E413.1.4.64", {"start": v(-14.58, -155.2) * mm, "end": v(-10.48, -159.3) * mm});
            skLineSegment(sketch, "E413.1.4.65", {"start": v(-2.75, -185.3) * mm, "end": v(-2.75, -187.25) * mm});
            skLineSegment(sketch, "E413.1.4.66", {"start": v(-127.3, -179.25) * mm, "end": v(-127.3, -181.3) * mm});
            skLineSegment(sketch, "E413.1.4.67", {"start": v(-2.75, -173.3) * mm, "end": v(-2.75, -175.25) * mm});
            skLineSegment(sketch, "E413.1.4.68", {"start": v(-2.75, -181.3) * mm, "end": v(-2.75, -183.25) * mm});
            skLineSegment(sketch, "E413.1.4.69", {"start": v(-127.3, -187.25) * mm, "end": v(-127.3, -189.25) * mm});
            skLineSegment(sketch, "E413.1.4.70", {"start": v(-2.7, -181.25) * mm, "end": v(-2.7, -183.3) * mm});
            skLineSegment(sketch, "E413.1.4.71", {"start": v(-127.3, -197) * mm, "end": v(-127.25, -197) * mm});
            skLineSegment(sketch, "E413.1.4.72", {"start": v(-127.5, -167) * mm, "end": v(-127.5, -197) * mm});
            skLineSegment(sketch, "E413.1.4.73", {"start": v(-127.25, -167.3) * mm, "end": v(-127.25, -169.25) * mm});
            skLineSegment(sketch, "E413.1.4.74", {"start": v(-2.75, -193.3) * mm, "end": v(-2.75, -195.25) * mm});
            skLineSegment(sketch, "E413.1.4.75", {"start": v(-127.25, -171.3) * mm, "end": v(-127.25, -173.25) * mm});
            skLineSegment(sketch, "E413.1.4.76", {"start": v(-2.7, -189.25) * mm, "end": v(-2.7, -191.25) * mm});
            skLineSegment(sketch, "E413.1.4.77", {"start": v(-127.25, -175.3) * mm, "end": v(-127.25, -177.3) * mm});
            skLineSegment(sketch, "E413.1.4.78", {"start": v(-127.25, -195.3) * mm, "end": v(-127.25, -197) * mm});
            skLineSegment(sketch, "E413.1.4.79", {"start": v(-2.7, -173.25) * mm, "end": v(-2.7, -175.3) * mm});
            skLineSegment(sketch, "E413.1.4.80", {"start": v(-127.25, -187.3) * mm, "end": v(-127.25, -189.25) * mm});
            skLineSegment(sketch, "E413.1.4.81", {"start": v(-2.7, -177.25) * mm, "end": v(-2.7, -179.3) * mm});
            skLineSegment(sketch, "E413.1.4.82", {"start": v(-14.6, -155.25) * mm, "end": v(-12.6, -157.25) * mm});
            skLineSegment(sketch, "E413.1.4.83", {"start": v(-127.25, -179.3) * mm, "end": v(-127.25, -181.25) * mm});
            skLineSegment(sketch, "E413.1.4.84", {"start": v(-2.7, -169.25) * mm, "end": v(-2.7, -171.3) * mm});
            skLineSegment(sketch, "E413.1.4.85", {"start": v(-127.25, -191.3) * mm, "end": v(-127.25, -193.25) * mm});
            skLineSegment(sketch, "E413.1.4.86", {"start": v(-127.3, -183.25) * mm, "end": v(-127.3, -185.25) * mm});
            skLineSegment(sketch, "E413.1.4.87", {"start": v(-127.3, -167.3) * mm, "end": v(-127.3, -169.3) * mm});
            skLineSegment(sketch, "E413.1.4.88", {"start": v(-115.4, -155.25) * mm, "end": v(-117.4, -157.25) * mm});
            skLineSegment(sketch, "E413.1.4.89", {"start": v(-2.7, -185.25) * mm, "end": v(-2.7, -187.3) * mm});
            skLineSegment(sketch, "E413.1.4.90", {"start": v(-127.3, -189.25) * mm, "end": v(-127.3, -189.3) * mm});
            skLineSegment(sketch, "E413.1.4.91", {"start": v(-127.3, -173.25) * mm, "end": v(-127.3, -173.3) * mm});
            skLineSegment(sketch, "E413.1.4.92", {"start": v(-127.25, -183.3) * mm, "end": v(-127.25, -185.25) * mm});
            skLineSegment(sketch, "E413.1.4.93", {"start": v(-127.3, -185.25) * mm, "end": v(-127.3, -185.3) * mm});
            skLineSegment(sketch, "E413.1.4.94", {"start": v(-2.7, -167.08) * mm, "end": v(-2.7, -167.3) * mm});
            skLineSegment(sketch, "E413.1.4.95", {"start": v(-127.3, -167.25) * mm, "end": v(-127.25, -167.25) * mm});
            skLineSegment(sketch, "E413.1.4.96", {"start": v(-2.7, -191.3) * mm, "end": v(-2.75, -191.3) * mm});
            skLineSegment(sketch, "E413.1.4.97", {"start": v(-2.75, -167.1) * mm, "end": v(-2.75, -167.25) * mm});
            skLineSegment(sketch, "E413.1.4.98", {"start": v(-127.3, -167.3) * mm, "end": v(-127.3, -167.25) * mm});
            skLineSegment(sketch, "E413.1.4.99", {"start": v(-2.7, -191.25) * mm, "end": v(-2.7, -191.3) * mm});
            skLineSegment(sketch, "E413.2.0.0", {"start": v(1.25, 184.7) * mm, "end": v(125.8, 184.7) * mm});
            skLineSegment(sketch, "E413.2.0.1", {"start": v(1.2, 170.7) * mm, "end": v(125.75, 170.7) * mm});
            skLineSegment(sketch, "E413.2.0.2", {"start": v(1.2, 182.7) * mm, "end": v(125.75, 182.7) * mm});
            skLineSegment(sketch, "E413.2.0.3", {"start": v(1.25, 168.7) * mm, "end": v(125.8, 168.7) * mm});
            skLineSegment(sketch, "E413.2.0.4", {"start": v(1.2, 166.7) * mm, "end": v(125.75, 166.7) * mm});
            skLineSegment(sketch, "E413.2.0.5", {"start": v(2.98, 186.7) * mm, "end": v(123.95, 186.7) * mm});
            skLineSegment(sketch, "E413.2.0.6", {"start": v(1.25, 180.7) * mm, "end": v(125.8, 180.7) * mm});
            skLineSegment(sketch, "E413.2.0.7", {"start": v(10.98, 194.7) * mm, "end": v(115.95, 194.7) * mm});
            skLineSegment(sketch, "E413.2.0.8", {"start": v(1.25, 160.7) * mm, "end": v(125.75, 160.7) * mm});
            skLineSegment(sketch, "E413.2.0.9", {"start": v(5.05, 188.7) * mm, "end": v(122.02, 188.7) * mm});
            skLineSegment(sketch, "E413.2.0.10", {"start": v(9.05, 192.7) * mm, "end": v(118.02, 192.7) * mm});
            skLineSegment(sketch, "E413.2.0.11", {"start": v(1.25, 164.7) * mm, "end": v(125.8, 164.7) * mm});
            skLineSegment(sketch, "E413.2.0.12", {"start": v(1.2, 162.7) * mm, "end": v(125.75, 162.7) * mm});
            skLineSegment(sketch, "E413.2.0.13", {"start": v(1.2, 178.7) * mm, "end": v(125.75, 178.7) * mm});
            skLineSegment(sketch, "E413.2.0.14", {"start": v(1.25, 176.7) * mm, "end": v(125.8, 176.7) * mm});
            skLineSegment(sketch, "E413.2.0.15", {"start": v(1.2, 174.7) * mm, "end": v(125.75, 174.7) * mm});
            skLineSegment(sketch, "E413.2.0.16", {"start": v(1.2, 158.7) * mm, "end": v(125.75, 158.7) * mm});
            skLineSegment(sketch, "E413.2.0.17", {"start": v(6.98, 190.7) * mm, "end": v(119.95, 190.7) * mm});
            skLineSegment(sketch, "E413.2.0.18", {"start": v(1.25, 156.7) * mm, "end": v(125.8, 156.7) * mm});
            skLineSegment(sketch, "E413.2.0.19", {"start": v(1.25, 172.7) * mm, "end": v(125.8, 172.7) * mm});
            skLineSegment(sketch, "E413.2.0.20", {"start": v(13.1, 196.75) * mm, "end": v(113.9, 196.75) * mm});
            skLineSegment(sketch, "E413.2.0.21", {"start": v(1.25, 170.75) * mm, "end": v(125.8, 170.75) * mm});
            skLineSegment(sketch, "E413.2.0.22", {"start": v(1.2, 168.75) * mm, "end": v(125.75, 168.75) * mm});
            skLineSegment(sketch, "E413.2.0.23", {"start": v(1.25, 166.75) * mm, "end": v(125.8, 166.75) * mm});
            skLineSegment(sketch, "E413.2.0.24", {"start": v(1.25, 184.75) * mm, "end": v(125.75, 184.75) * mm});
            skLineSegment(sketch, "E413.2.0.25", {"start": v(1.25, 182.75) * mm, "end": v(125.8, 182.75) * mm});
            skLineSegment(sketch, "E413.2.0.26", {"start": v(1.2, 180.75) * mm, "end": v(125.75, 180.75) * mm});
            skLineSegment(sketch, "E413.2.0.27", {"start": v(1.2, 160.75) * mm, "end": v(125.75, 160.75) * mm});
            skLineSegment(sketch, "E413.2.0.28", {"start": v(1.2, 176.75) * mm, "end": v(125.75, 176.75) * mm});
            skLineSegment(sketch, "E413.2.0.29", {"start": v(7.1, 190.75) * mm, "end": v(119.97, 190.75) * mm});
            skLineSegment(sketch, "E413.2.0.30", {"start": v(1.25, 174.75) * mm, "end": v(125.8, 174.75) * mm});
            skLineSegment(sketch, "E413.2.0.31", {"start": v(1.2, 156.75) * mm, "end": v(125.75, 156.75) * mm});
            skLineSegment(sketch, "E413.2.0.32", {"start": v(3.1, 186.75) * mm, "end": v(123.97, 186.75) * mm});
            skLineSegment(sketch, "E413.2.0.33", {"start": v(1.2, 164.75) * mm, "end": v(125.75, 164.75) * mm});
            skLineSegment(sketch, "E413.2.0.34", {"start": v(1.25, 178.75) * mm, "end": v(125.8, 178.75) * mm});
            skLineSegment(sketch, "E413.2.0.35", {"start": v(1.25, 162.75) * mm, "end": v(125.8, 162.75) * mm});
            skLineSegment(sketch, "E413.2.0.36", {"start": v(11.1, 194.75) * mm, "end": v(115.9, 194.75) * mm});
            skLineSegment(sketch, "E413.2.0.37", {"start": v(1.25, 158.75) * mm, "end": v(125.8, 158.75) * mm});
            skLineSegment(sketch, "E413.2.0.38", {"start": v(9.03, 192.75) * mm, "end": v(117.9, 192.75) * mm});
            skLineSegment(sketch, "E413.2.0.39", {"start": v(13.08, 196.8) * mm, "end": v(113.92, 196.8) * mm});
            skLineSegment(sketch, "E413.2.0.40", {"start": v(126, 185) * mm, "end": v(126, 155) * mm});
            skLineSegment(sketch, "E413.2.0.41", {"start": v(5.03, 188.75) * mm, "end": v(121.9, 188.75) * mm});
            skLineSegment(sketch, "E413.2.0.42", {"start": v(1.2, 172.75) * mm, "end": v(125.75, 172.75) * mm});
            skLineSegment(sketch, "E413.2.0.43", {"start": v(119.97, 190.75) * mm, "end": v(122.02, 188.7) * mm});
            skLineSegment(sketch, "E413.2.0.44", {"start": v(119.95, 190.7) * mm, "end": v(121.9, 188.75) * mm});
            skLineSegment(sketch, "E413.2.0.45", {"start": v(9.03, 192.75) * mm, "end": v(6.98, 190.7) * mm});
            skLineSegment(sketch, "E413.2.0.46", {"start": v(13, 197) * mm, "end": v(1, 185) * mm});
            skLineSegment(sketch, "E413.2.0.47", {"start": v(13, 197) * mm, "end": v(114, 197) * mm});
            skLineSegment(sketch, "E413.2.0.48", {"start": v(114, 197) * mm, "end": v(126, 185) * mm});
            skLineSegment(sketch, "E413.2.0.49", {"start": v(9.05, 192.7) * mm, "end": v(7.1, 190.75) * mm});
            skLineSegment(sketch, "E413.2.0.50", {"start": v(1.2, 180.75) * mm, "end": v(1.2, 178.75) * mm});
            skLineSegment(sketch, "E413.2.0.51", {"start": v(5.03, 188.75) * mm, "end": v(2.98, 186.7) * mm});
            skLineSegment(sketch, "E413.2.0.52", {"start": v(115.95, 194.7) * mm, "end": v(117.9, 192.75) * mm});
            skLineSegment(sketch, "E413.2.0.53", {"start": v(1.2, 176.75) * mm, "end": v(1.2, 174.7) * mm});
            skLineSegment(sketch, "E413.2.0.54", {"start": v(123.97, 186.75) * mm, "end": v(125.8, 184.92) * mm});
            skLineSegment(sketch, "E413.2.0.55", {"start": v(125.8, 158.75) * mm, "end": v(125.8, 156.7) * mm});
            skLineSegment(sketch, "E413.2.0.56", {"start": v(125.75, 162.7) * mm, "end": v(125.75, 160.75) * mm});
            skLineSegment(sketch, "E413.2.0.57", {"start": v(123.95, 186.7) * mm, "end": v(125.75, 184.9) * mm});
            skLineSegment(sketch, "E413.2.0.58", {"start": v(5.05, 188.7) * mm, "end": v(3.1, 186.75) * mm});
            skLineSegment(sketch, "E413.2.0.59", {"start": v(125.75, 182.7) * mm, "end": v(125.75, 180.75) * mm});
            skLineSegment(sketch, "E413.2.0.60", {"start": v(1.2, 156.75) * mm, "end": v(1.2, 155) * mm});
            skLineSegment(sketch, "E413.2.0.61", {"start": v(1.2, 160.75) * mm, "end": v(1.2, 158.7) * mm});
            skLineSegment(sketch, "E413.2.0.62", {"start": v(125.75, 174.7) * mm, "end": v(125.75, 172.75) * mm});
            skLineSegment(sketch, "E413.2.0.63", {"start": v(13.08, 196.8) * mm, "end": v(10.98, 194.7) * mm});
            skLineSegment(sketch, "E413.2.0.64", {"start": v(113.92, 196.8) * mm, "end": v(118.02, 192.7) * mm});
            skLineSegment(sketch, "E413.2.0.65", {"start": v(125.75, 166.7) * mm, "end": v(125.75, 164.75) * mm});
            skLineSegment(sketch, "E413.2.0.66", {"start": v(1.2, 172.75) * mm, "end": v(1.2, 170.7) * mm});
            skLineSegment(sketch, "E413.2.0.67", {"start": v(125.75, 178.7) * mm, "end": v(125.75, 176.75) * mm});
            skLineSegment(sketch, "E413.2.0.68", {"start": v(125.75, 170.7) * mm, "end": v(125.75, 168.75) * mm});
            skLineSegment(sketch, "E413.2.0.69", {"start": v(1.2, 164.75) * mm, "end": v(1.2, 162.75) * mm});
            skLineSegment(sketch, "E413.2.0.70", {"start": v(125.8, 170.75) * mm, "end": v(125.8, 168.7) * mm});
            skLineSegment(sketch, "E413.2.0.71", {"start": v(1.2, 155) * mm, "end": v(1.25, 155) * mm});
            skLineSegment(sketch, "E413.2.0.72", {"start": v(1, 185) * mm, "end": v(1, 155) * mm});
            skLineSegment(sketch, "E413.2.0.73", {"start": v(1.25, 184.7) * mm, "end": v(1.25, 182.75) * mm});
            skLineSegment(sketch, "E413.2.0.74", {"start": v(125.75, 158.7) * mm, "end": v(125.75, 156.75) * mm});
            skLineSegment(sketch, "E413.2.0.75", {"start": v(1.25, 180.7) * mm, "end": v(1.25, 178.75) * mm});
            skLineSegment(sketch, "E413.2.0.76", {"start": v(125.8, 162.75) * mm, "end": v(125.8, 160.75) * mm});
            skLineSegment(sketch, "E413.2.0.77", {"start": v(1.25, 176.7) * mm, "end": v(1.25, 174.7) * mm});
            skLineSegment(sketch, "E413.2.0.78", {"start": v(1.25, 156.7) * mm, "end": v(1.25, 155) * mm});
            skLineSegment(sketch, "E413.2.0.79", {"start": v(125.8, 178.75) * mm, "end": v(125.8, 176.7) * mm});
            skLineSegment(sketch, "E413.2.0.80", {"start": v(1.25, 164.7) * mm, "end": v(1.25, 162.75) * mm});
            skLineSegment(sketch, "E413.2.0.81", {"start": v(125.8, 174.75) * mm, "end": v(125.8, 172.7) * mm});
            skLineSegment(sketch, "E413.2.0.82", {"start": v(113.9, 196.75) * mm, "end": v(115.9, 194.75) * mm});
            skLineSegment(sketch, "E413.2.0.83", {"start": v(1.25, 172.7) * mm, "end": v(1.25, 170.75) * mm});
            skLineSegment(sketch, "E413.2.0.84", {"start": v(125.8, 182.75) * mm, "end": v(125.8, 180.7) * mm});
            skLineSegment(sketch, "E413.2.0.85", {"start": v(1.25, 160.7) * mm, "end": v(1.25, 158.75) * mm});
            skLineSegment(sketch, "E413.2.0.86", {"start": v(1.2, 168.75) * mm, "end": v(1.2, 166.75) * mm});
            skLineSegment(sketch, "E413.2.0.87", {"start": v(1.2, 184.7) * mm, "end": v(1.2, 182.7) * mm});
            skLineSegment(sketch, "E413.2.0.88", {"start": v(13.1, 196.75) * mm, "end": v(11.1, 194.75) * mm});
            skLineSegment(sketch, "E413.2.0.89", {"start": v(125.8, 166.75) * mm, "end": v(125.8, 164.7) * mm});
            skLineSegment(sketch, "E413.2.0.90", {"start": v(1.2, 162.75) * mm, "end": v(1.2, 162.7) * mm});
            skLineSegment(sketch, "E413.2.0.91", {"start": v(1.2, 178.75) * mm, "end": v(1.2, 178.7) * mm});
            skLineSegment(sketch, "E413.2.0.92", {"start": v(1.25, 168.7) * mm, "end": v(1.25, 166.75) * mm});
            skLineSegment(sketch, "E413.2.0.93", {"start": v(1.2, 166.75) * mm, "end": v(1.2, 166.7) * mm});
            skLineSegment(sketch, "E413.2.0.94", {"start": v(125.8, 184.92) * mm, "end": v(125.8, 184.7) * mm});
            skLineSegment(sketch, "E413.2.0.95", {"start": v(1.2, 184.75) * mm, "end": v(1.25, 184.75) * mm});
            skLineSegment(sketch, "E413.2.0.96", {"start": v(125.8, 160.7) * mm, "end": v(125.75, 160.7) * mm});
            skLineSegment(sketch, "E413.2.0.97", {"start": v(125.75, 184.9) * mm, "end": v(125.75, 184.75) * mm});
            skLineSegment(sketch, "E413.2.0.98", {"start": v(1.2, 184.7) * mm, "end": v(1.2, 184.75) * mm});
            skLineSegment(sketch, "E413.2.0.99", {"start": v(125.8, 160.75) * mm, "end": v(125.8, 160.7) * mm});
            skLineSegment(sketch, "E413.2.1.0", {"start": v(1.25, 96.7) * mm, "end": v(125.8, 96.7) * mm});
            skLineSegment(sketch, "E413.2.1.1", {"start": v(1.2, 82.7) * mm, "end": v(125.75, 82.7) * mm});
            skLineSegment(sketch, "E413.2.1.2", {"start": v(1.2, 94.7) * mm, "end": v(125.75, 94.7) * mm});
            skLineSegment(sketch, "E413.2.1.3", {"start": v(1.25, 80.7) * mm, "end": v(125.8, 80.7) * mm});
            skLineSegment(sketch, "E413.2.1.4", {"start": v(1.2, 78.7) * mm, "end": v(125.75, 78.7) * mm});
            skLineSegment(sketch, "E413.2.1.5", {"start": v(2.98, 98.7) * mm, "end": v(123.95, 98.7) * mm});
            skLineSegment(sketch, "E413.2.1.6", {"start": v(1.25, 92.7) * mm, "end": v(125.8, 92.7) * mm});
            skLineSegment(sketch, "E413.2.1.7", {"start": v(10.98, 106.7) * mm, "end": v(115.95, 106.7) * mm});
            skLineSegment(sketch, "E413.2.1.8", {"start": v(1.25, 72.7) * mm, "end": v(125.75, 72.7) * mm});
            skLineSegment(sketch, "E413.2.1.9", {"start": v(5.05, 100.7) * mm, "end": v(122.02, 100.7) * mm});
            skLineSegment(sketch, "E413.2.1.10", {"start": v(9.05, 104.7) * mm, "end": v(118.02, 104.7) * mm});
            skLineSegment(sketch, "E413.2.1.11", {"start": v(1.25, 76.7) * mm, "end": v(125.8, 76.7) * mm});
            skLineSegment(sketch, "E413.2.1.12", {"start": v(1.2, 74.7) * mm, "end": v(125.75, 74.7) * mm});
            skLineSegment(sketch, "E413.2.1.13", {"start": v(1.2, 90.7) * mm, "end": v(125.75, 90.7) * mm});
            skLineSegment(sketch, "E413.2.1.14", {"start": v(1.25, 88.7) * mm, "end": v(125.8, 88.7) * mm});
            skLineSegment(sketch, "E413.2.1.15", {"start": v(1.2, 86.7) * mm, "end": v(125.75, 86.7) * mm});
            skLineSegment(sketch, "E413.2.1.16", {"start": v(1.2, 70.7) * mm, "end": v(125.75, 70.7) * mm});
            skLineSegment(sketch, "E413.2.1.17", {"start": v(6.98, 102.7) * mm, "end": v(119.95, 102.7) * mm});
            skLineSegment(sketch, "E413.2.1.18", {"start": v(1.25, 68.7) * mm, "end": v(125.8, 68.7) * mm});
            skLineSegment(sketch, "E413.2.1.19", {"start": v(1.25, 84.7) * mm, "end": v(125.8, 84.7) * mm});
            skLineSegment(sketch, "E413.2.1.20", {"start": v(13.1, 108.75) * mm, "end": v(113.9, 108.75) * mm});
            skLineSegment(sketch, "E413.2.1.21", {"start": v(1.25, 82.75) * mm, "end": v(125.8, 82.75) * mm});
            skLineSegment(sketch, "E413.2.1.22", {"start": v(1.2, 80.75) * mm, "end": v(125.75, 80.75) * mm});
            skLineSegment(sketch, "E413.2.1.23", {"start": v(1.25, 78.75) * mm, "end": v(125.8, 78.75) * mm});
            skLineSegment(sketch, "E413.2.1.24", {"start": v(1.25, 96.75) * mm, "end": v(125.75, 96.75) * mm});
            skLineSegment(sketch, "E413.2.1.25", {"start": v(1.25, 94.75) * mm, "end": v(125.8, 94.75) * mm});
            skLineSegment(sketch, "E413.2.1.26", {"start": v(1.2, 92.75) * mm, "end": v(125.75, 92.75) * mm});
            skLineSegment(sketch, "E413.2.1.27", {"start": v(1.2, 72.75) * mm, "end": v(125.75, 72.75) * mm});
            skLineSegment(sketch, "E413.2.1.28", {"start": v(1.2, 88.75) * mm, "end": v(125.75, 88.75) * mm});
            skLineSegment(sketch, "E413.2.1.29", {"start": v(7.1, 102.75) * mm, "end": v(119.97, 102.75) * mm});
            skLineSegment(sketch, "E413.2.1.30", {"start": v(1.25, 86.75) * mm, "end": v(125.8, 86.75) * mm});
            skLineSegment(sketch, "E413.2.1.31", {"start": v(1.2, 68.75) * mm, "end": v(125.75, 68.75) * mm});
            skLineSegment(sketch, "E413.2.1.32", {"start": v(3.1, 98.75) * mm, "end": v(123.97, 98.75) * mm});
            skLineSegment(sketch, "E413.2.1.33", {"start": v(1.2, 76.75) * mm, "end": v(125.75, 76.75) * mm});
            skLineSegment(sketch, "E413.2.1.34", {"start": v(1.25, 90.75) * mm, "end": v(125.8, 90.75) * mm});
            skLineSegment(sketch, "E413.2.1.35", {"start": v(1.25, 74.75) * mm, "end": v(125.8, 74.75) * mm});
            skLineSegment(sketch, "E413.2.1.36", {"start": v(11.1, 106.75) * mm, "end": v(115.9, 106.75) * mm});
            skLineSegment(sketch, "E413.2.1.37", {"start": v(1.25, 70.75) * mm, "end": v(125.8, 70.75) * mm});
            skLineSegment(sketch, "E413.2.1.38", {"start": v(9.03, 104.75) * mm, "end": v(117.9, 104.75) * mm});
            skLineSegment(sketch, "E413.2.1.39", {"start": v(13.08, 108.8) * mm, "end": v(113.92, 108.8) * mm});
            skLineSegment(sketch, "E413.2.1.40", {"start": v(126, 97) * mm, "end": v(126, 67) * mm});
            skLineSegment(sketch, "E413.2.1.41", {"start": v(5.03, 100.75) * mm, "end": v(121.9, 100.75) * mm});
            skLineSegment(sketch, "E413.2.1.42", {"start": v(1.2, 84.75) * mm, "end": v(125.75, 84.75) * mm});
            skLineSegment(sketch, "E413.2.1.43", {"start": v(119.97, 102.75) * mm, "end": v(122.02, 100.7) * mm});
            skLineSegment(sketch, "E413.2.1.44", {"start": v(119.95, 102.7) * mm, "end": v(121.9, 100.75) * mm});
            skLineSegment(sketch, "E413.2.1.45", {"start": v(9.03, 104.75) * mm, "end": v(6.98, 102.7) * mm});
            skLineSegment(sketch, "E413.2.1.46", {"start": v(13, 109) * mm, "end": v(1, 97) * mm});
            skLineSegment(sketch, "E413.2.1.47", {"start": v(13, 109) * mm, "end": v(114, 109) * mm});
            skLineSegment(sketch, "E413.2.1.48", {"start": v(114, 109) * mm, "end": v(126, 97) * mm});
            skLineSegment(sketch, "E413.2.1.49", {"start": v(9.05, 104.7) * mm, "end": v(7.1, 102.75) * mm});
            skLineSegment(sketch, "E413.2.1.50", {"start": v(1.2, 92.75) * mm, "end": v(1.2, 90.75) * mm});
            skLineSegment(sketch, "E413.2.1.51", {"start": v(5.03, 100.75) * mm, "end": v(2.98, 98.7) * mm});
            skLineSegment(sketch, "E413.2.1.52", {"start": v(115.95, 106.7) * mm, "end": v(117.9, 104.75) * mm});
            skLineSegment(sketch, "E413.2.1.53", {"start": v(1.2, 88.75) * mm, "end": v(1.2, 86.7) * mm});
            skLineSegment(sketch, "E413.2.1.54", {"start": v(123.97, 98.75) * mm, "end": v(125.8, 96.92) * mm});
            skLineSegment(sketch, "E413.2.1.55", {"start": v(125.8, 70.75) * mm, "end": v(125.8, 68.7) * mm});
            skLineSegment(sketch, "E413.2.1.56", {"start": v(125.75, 74.7) * mm, "end": v(125.75, 72.75) * mm});
            skLineSegment(sketch, "E413.2.1.57", {"start": v(123.95, 98.7) * mm, "end": v(125.75, 96.9) * mm});
            skLineSegment(sketch, "E413.2.1.58", {"start": v(5.05, 100.7) * mm, "end": v(3.1, 98.75) * mm});
            skLineSegment(sketch, "E413.2.1.59", {"start": v(125.75, 94.7) * mm, "end": v(125.75, 92.75) * mm});
            skLineSegment(sketch, "E413.2.1.60", {"start": v(1.2, 68.75) * mm, "end": v(1.2, 67) * mm});
            skLineSegment(sketch, "E413.2.1.61", {"start": v(1.2, 72.75) * mm, "end": v(1.2, 70.7) * mm});
            skLineSegment(sketch, "E413.2.1.62", {"start": v(125.75, 86.7) * mm, "end": v(125.75, 84.75) * mm});
            skLineSegment(sketch, "E413.2.1.63", {"start": v(13.08, 108.8) * mm, "end": v(10.98, 106.7) * mm});
            skLineSegment(sketch, "E413.2.1.64", {"start": v(113.92, 108.8) * mm, "end": v(118.02, 104.7) * mm});
            skLineSegment(sketch, "E413.2.1.65", {"start": v(125.75, 78.7) * mm, "end": v(125.75, 76.75) * mm});
            skLineSegment(sketch, "E413.2.1.66", {"start": v(1.2, 84.75) * mm, "end": v(1.2, 82.7) * mm});
            skLineSegment(sketch, "E413.2.1.67", {"start": v(125.75, 90.7) * mm, "end": v(125.75, 88.75) * mm});
            skLineSegment(sketch, "E413.2.1.68", {"start": v(125.75, 82.7) * mm, "end": v(125.75, 80.75) * mm});
            skLineSegment(sketch, "E413.2.1.69", {"start": v(1.2, 76.75) * mm, "end": v(1.2, 74.75) * mm});
            skLineSegment(sketch, "E413.2.1.70", {"start": v(125.8, 82.75) * mm, "end": v(125.8, 80.7) * mm});
            skLineSegment(sketch, "E413.2.1.71", {"start": v(1.2, 67) * mm, "end": v(1.25, 67) * mm});
            skLineSegment(sketch, "E413.2.1.72", {"start": v(1, 97) * mm, "end": v(1, 67) * mm});
            skLineSegment(sketch, "E413.2.1.73", {"start": v(1.25, 96.7) * mm, "end": v(1.25, 94.75) * mm});
            skLineSegment(sketch, "E413.2.1.74", {"start": v(125.75, 70.7) * mm, "end": v(125.75, 68.75) * mm});
            skLineSegment(sketch, "E413.2.1.75", {"start": v(1.25, 92.7) * mm, "end": v(1.25, 90.75) * mm});
            skLineSegment(sketch, "E413.2.1.76", {"start": v(125.8, 74.75) * mm, "end": v(125.8, 72.75) * mm});
            skLineSegment(sketch, "E413.2.1.77", {"start": v(1.25, 88.7) * mm, "end": v(1.25, 86.7) * mm});
            skLineSegment(sketch, "E413.2.1.78", {"start": v(1.25, 68.7) * mm, "end": v(1.25, 67) * mm});
            skLineSegment(sketch, "E413.2.1.79", {"start": v(125.8, 90.75) * mm, "end": v(125.8, 88.7) * mm});
            skLineSegment(sketch, "E413.2.1.80", {"start": v(1.25, 76.7) * mm, "end": v(1.25, 74.75) * mm});
            skLineSegment(sketch, "E413.2.1.81", {"start": v(125.8, 86.75) * mm, "end": v(125.8, 84.7) * mm});
            skLineSegment(sketch, "E413.2.1.82", {"start": v(113.9, 108.75) * mm, "end": v(115.9, 106.75) * mm});
            skLineSegment(sketch, "E413.2.1.83", {"start": v(1.25, 84.7) * mm, "end": v(1.25, 82.75) * mm});
            skLineSegment(sketch, "E413.2.1.84", {"start": v(125.8, 94.75) * mm, "end": v(125.8, 92.7) * mm});
            skLineSegment(sketch, "E413.2.1.85", {"start": v(1.25, 72.7) * mm, "end": v(1.25, 70.75) * mm});
            skLineSegment(sketch, "E413.2.1.86", {"start": v(1.2, 80.75) * mm, "end": v(1.2, 78.75) * mm});
            skLineSegment(sketch, "E413.2.1.87", {"start": v(1.2, 96.7) * mm, "end": v(1.2, 94.7) * mm});
            skLineSegment(sketch, "E413.2.1.88", {"start": v(13.1, 108.75) * mm, "end": v(11.1, 106.75) * mm});
            skLineSegment(sketch, "E413.2.1.89", {"start": v(125.8, 78.75) * mm, "end": v(125.8, 76.7) * mm});
            skLineSegment(sketch, "E413.2.1.90", {"start": v(1.2, 74.75) * mm, "end": v(1.2, 74.7) * mm});
            skLineSegment(sketch, "E413.2.1.91", {"start": v(1.2, 90.75) * mm, "end": v(1.2, 90.7) * mm});
            skLineSegment(sketch, "E413.2.1.92", {"start": v(1.25, 80.7) * mm, "end": v(1.25, 78.75) * mm});
            skLineSegment(sketch, "E413.2.1.93", {"start": v(1.2, 78.75) * mm, "end": v(1.2, 78.7) * mm});
            skLineSegment(sketch, "E413.2.1.94", {"start": v(125.8, 96.92) * mm, "end": v(125.8, 96.7) * mm});
            skLineSegment(sketch, "E413.2.1.95", {"start": v(1.2, 96.75) * mm, "end": v(1.25, 96.75) * mm});
            skLineSegment(sketch, "E413.2.1.96", {"start": v(125.8, 72.7) * mm, "end": v(125.75, 72.7) * mm});
            skLineSegment(sketch, "E413.2.1.97", {"start": v(125.75, 96.9) * mm, "end": v(125.75, 96.75) * mm});
            skLineSegment(sketch, "E413.2.1.98", {"start": v(1.2, 96.7) * mm, "end": v(1.2, 96.75) * mm});
            skLineSegment(sketch, "E413.2.1.99", {"start": v(125.8, 72.75) * mm, "end": v(125.8, 72.7) * mm});
            skLineSegment(sketch, "E413.2.2.0", {"start": v(1.25, 8.7) * mm, "end": v(125.8, 8.7) * mm});
            skLineSegment(sketch, "E413.2.2.1", {"start": v(1.2, -5.3) * mm, "end": v(125.75, -5.3) * mm});
            skLineSegment(sketch, "E413.2.2.2", {"start": v(1.2, 6.7) * mm, "end": v(125.75, 6.7) * mm});
            skLineSegment(sketch, "E413.2.2.3", {"start": v(1.25, -7.3) * mm, "end": v(125.8, -7.3) * mm});
            skLineSegment(sketch, "E413.2.2.4", {"start": v(1.2, -9.3) * mm, "end": v(125.75, -9.3) * mm});
            skLineSegment(sketch, "E413.2.2.5", {"start": v(2.98, 10.7) * mm, "end": v(123.95, 10.7) * mm});
            skLineSegment(sketch, "E413.2.2.6", {"start": v(1.25, 4.7) * mm, "end": v(125.8, 4.7) * mm});
            skLineSegment(sketch, "E413.2.2.7", {"start": v(10.98, 18.7) * mm, "end": v(115.95, 18.7) * mm});
            skLineSegment(sketch, "E413.2.2.8", {"start": v(1.25, -15.3) * mm, "end": v(125.75, -15.3) * mm});
            skLineSegment(sketch, "E413.2.2.9", {"start": v(5.05, 12.7) * mm, "end": v(122.02, 12.7) * mm});
            skLineSegment(sketch, "E413.2.2.10", {"start": v(9.05, 16.7) * mm, "end": v(118.02, 16.7) * mm});
            skLineSegment(sketch, "E413.2.2.11", {"start": v(1.25, -11.3) * mm, "end": v(125.8, -11.3) * mm});
            skLineSegment(sketch, "E413.2.2.12", {"start": v(1.2, -13.3) * mm, "end": v(125.75, -13.3) * mm});
            skLineSegment(sketch, "E413.2.2.13", {"start": v(1.2, 2.7) * mm, "end": v(125.75, 2.7) * mm});
            skLineSegment(sketch, "E413.2.2.14", {"start": v(1.25, 0.7) * mm, "end": v(125.8, 0.7) * mm});
            skLineSegment(sketch, "E413.2.2.15", {"start": v(1.2, -1.3) * mm, "end": v(125.75, -1.3) * mm});
            skLineSegment(sketch, "E413.2.2.16", {"start": v(1.2, -17.3) * mm, "end": v(125.75, -17.3) * mm});
            skLineSegment(sketch, "E413.2.2.17", {"start": v(6.98, 14.7) * mm, "end": v(119.95, 14.7) * mm});
            skLineSegment(sketch, "E413.2.2.18", {"start": v(1.25, -19.3) * mm, "end": v(125.8, -19.3) * mm});
            skLineSegment(sketch, "E413.2.2.19", {"start": v(1.25, -3.3) * mm, "end": v(125.8, -3.3) * mm});
            skLineSegment(sketch, "E413.2.2.20", {"start": v(13.1, 20.75) * mm, "end": v(113.9, 20.75) * mm});
            skLineSegment(sketch, "E413.2.2.21", {"start": v(1.25, -5.25) * mm, "end": v(125.8, -5.25) * mm});
            skLineSegment(sketch, "E413.2.2.22", {"start": v(1.2, -7.25) * mm, "end": v(125.75, -7.25) * mm});
            skLineSegment(sketch, "E413.2.2.23", {"start": v(1.25, -9.25) * mm, "end": v(125.8, -9.25) * mm});
            skLineSegment(sketch, "E413.2.2.24", {"start": v(1.25, 8.75) * mm, "end": v(125.75, 8.75) * mm});
            skLineSegment(sketch, "E413.2.2.25", {"start": v(1.25, 6.75) * mm, "end": v(125.8, 6.75) * mm});
            skLineSegment(sketch, "E413.2.2.26", {"start": v(1.2, 4.75) * mm, "end": v(125.75, 4.75) * mm});
            skLineSegment(sketch, "E413.2.2.27", {"start": v(1.2, -15.25) * mm, "end": v(125.75, -15.25) * mm});
            skLineSegment(sketch, "E413.2.2.28", {"start": v(1.2, 0.75) * mm, "end": v(125.75, 0.75) * mm});
            skLineSegment(sketch, "E413.2.2.29", {"start": v(7.1, 14.75) * mm, "end": v(119.97, 14.75) * mm});
            skLineSegment(sketch, "E413.2.2.30", {"start": v(1.25, -1.25) * mm, "end": v(125.8, -1.25) * mm});
            skLineSegment(sketch, "E413.2.2.31", {"start": v(1.2, -19.25) * mm, "end": v(125.75, -19.25) * mm});
            skLineSegment(sketch, "E413.2.2.32", {"start": v(3.1, 10.75) * mm, "end": v(123.97, 10.75) * mm});
            skLineSegment(sketch, "E413.2.2.33", {"start": v(1.2, -11.25) * mm, "end": v(125.75, -11.25) * mm});
            skLineSegment(sketch, "E413.2.2.34", {"start": v(1.25, 2.75) * mm, "end": v(125.8, 2.75) * mm});
            skLineSegment(sketch, "E413.2.2.35", {"start": v(1.25, -13.25) * mm, "end": v(125.8, -13.25) * mm});
            skLineSegment(sketch, "E413.2.2.36", {"start": v(11.1, 18.75) * mm, "end": v(115.9, 18.75) * mm});
            skLineSegment(sketch, "E413.2.2.37", {"start": v(1.25, -17.25) * mm, "end": v(125.8, -17.25) * mm});
            skLineSegment(sketch, "E413.2.2.38", {"start": v(9.03, 16.75) * mm, "end": v(117.9, 16.75) * mm});
            skLineSegment(sketch, "E413.2.2.39", {"start": v(13.08, 20.8) * mm, "end": v(113.92, 20.8) * mm});
            skLineSegment(sketch, "E413.2.2.40", {"start": v(126, 9) * mm, "end": v(126, -21) * mm});
            skLineSegment(sketch, "E413.2.2.41", {"start": v(5.03, 12.75) * mm, "end": v(121.9, 12.75) * mm});
            skLineSegment(sketch, "E413.2.2.42", {"start": v(1.2, -3.25) * mm, "end": v(125.75, -3.25) * mm});
            skLineSegment(sketch, "E413.2.2.43", {"start": v(119.97, 14.75) * mm, "end": v(122.02, 12.7) * mm});
            skLineSegment(sketch, "E413.2.2.44", {"start": v(119.95, 14.7) * mm, "end": v(121.9, 12.75) * mm});
            skLineSegment(sketch, "E413.2.2.45", {"start": v(9.03, 16.75) * mm, "end": v(6.98, 14.7) * mm});
            skLineSegment(sketch, "E413.2.2.46", {"start": v(13, 21) * mm, "end": v(1, 9) * mm});
            skLineSegment(sketch, "E413.2.2.47", {"start": v(13, 21) * mm, "end": v(114, 21) * mm});
            skLineSegment(sketch, "E413.2.2.48", {"start": v(114, 21) * mm, "end": v(126, 9) * mm});
            skLineSegment(sketch, "E413.2.2.49", {"start": v(9.05, 16.7) * mm, "end": v(7.1, 14.75) * mm});
            skLineSegment(sketch, "E413.2.2.50", {"start": v(1.2, 4.75) * mm, "end": v(1.2, 2.75) * mm});
            skLineSegment(sketch, "E413.2.2.51", {"start": v(5.03, 12.75) * mm, "end": v(2.98, 10.7) * mm});
            skLineSegment(sketch, "E413.2.2.52", {"start": v(115.95, 18.7) * mm, "end": v(117.9, 16.75) * mm});
            skLineSegment(sketch, "E413.2.2.53", {"start": v(1.2, 0.75) * mm, "end": v(1.2, -1.3) * mm});
            skLineSegment(sketch, "E413.2.2.54", {"start": v(123.97, 10.75) * mm, "end": v(125.8, 8.92) * mm});
            skLineSegment(sketch, "E413.2.2.55", {"start": v(125.8, -17.25) * mm, "end": v(125.8, -19.3) * mm});
            skLineSegment(sketch, "E413.2.2.56", {"start": v(125.75, -13.3) * mm, "end": v(125.75, -15.25) * mm});
            skLineSegment(sketch, "E413.2.2.57", {"start": v(123.95, 10.7) * mm, "end": v(125.75, 8.9) * mm});
            skLineSegment(sketch, "E413.2.2.58", {"start": v(5.05, 12.7) * mm, "end": v(3.1, 10.75) * mm});
            skLineSegment(sketch, "E413.2.2.59", {"start": v(125.75, 6.7) * mm, "end": v(125.75, 4.75) * mm});
            skLineSegment(sketch, "E413.2.2.60", {"start": v(1.2, -19.25) * mm, "end": v(1.2, -21) * mm});
            skLineSegment(sketch, "E413.2.2.61", {"start": v(1.2, -15.25) * mm, "end": v(1.2, -17.3) * mm});
            skLineSegment(sketch, "E413.2.2.62", {"start": v(125.75, -1.3) * mm, "end": v(125.75, -3.25) * mm});
            skLineSegment(sketch, "E413.2.2.63", {"start": v(13.08, 20.8) * mm, "end": v(10.98, 18.7) * mm});
            skLineSegment(sketch, "E413.2.2.64", {"start": v(113.92, 20.8) * mm, "end": v(118.02, 16.7) * mm});
            skLineSegment(sketch, "E413.2.2.65", {"start": v(125.75, -9.3) * mm, "end": v(125.75, -11.25) * mm});
            skLineSegment(sketch, "E413.2.2.66", {"start": v(1.2, -3.25) * mm, "end": v(1.2, -5.3) * mm});
            skLineSegment(sketch, "E413.2.2.67", {"start": v(125.75, 2.7) * mm, "end": v(125.75, 0.75) * mm});
            skLineSegment(sketch, "E413.2.2.68", {"start": v(125.75, -5.3) * mm, "end": v(125.75, -7.25) * mm});
            skLineSegment(sketch, "E413.2.2.69", {"start": v(1.2, -11.25) * mm, "end": v(1.2, -13.25) * mm});
            skLineSegment(sketch, "E413.2.2.70", {"start": v(125.8, -5.25) * mm, "end": v(125.8, -7.3) * mm});
            skLineSegment(sketch, "E413.2.2.71", {"start": v(1.2, -21) * mm, "end": v(1.25, -21) * mm});
            skLineSegment(sketch, "E413.2.2.72", {"start": v(1, 9) * mm, "end": v(1, -21) * mm});
            skLineSegment(sketch, "E413.2.2.73", {"start": v(1.25, 8.7) * mm, "end": v(1.25, 6.75) * mm});
            skLineSegment(sketch, "E413.2.2.74", {"start": v(125.75, -17.3) * mm, "end": v(125.75, -19.25) * mm});
            skLineSegment(sketch, "E413.2.2.75", {"start": v(1.25, 4.7) * mm, "end": v(1.25, 2.75) * mm});
            skLineSegment(sketch, "E413.2.2.76", {"start": v(125.8, -13.25) * mm, "end": v(125.8, -15.25) * mm});
            skLineSegment(sketch, "E413.2.2.77", {"start": v(1.25, 0.7) * mm, "end": v(1.25, -1.3) * mm});
            skLineSegment(sketch, "E413.2.2.78", {"start": v(1.25, -19.3) * mm, "end": v(1.25, -21) * mm});
            skLineSegment(sketch, "E413.2.2.79", {"start": v(125.8, 2.75) * mm, "end": v(125.8, 0.7) * mm});
            skLineSegment(sketch, "E413.2.2.80", {"start": v(1.25, -11.3) * mm, "end": v(1.25, -13.25) * mm});
            skLineSegment(sketch, "E413.2.2.81", {"start": v(125.8, -1.25) * mm, "end": v(125.8, -3.3) * mm});
            skLineSegment(sketch, "E413.2.2.82", {"start": v(113.9, 20.75) * mm, "end": v(115.9, 18.75) * mm});
            skLineSegment(sketch, "E413.2.2.83", {"start": v(1.25, -3.3) * mm, "end": v(1.25, -5.25) * mm});
            skLineSegment(sketch, "E413.2.2.84", {"start": v(125.8, 6.75) * mm, "end": v(125.8, 4.7) * mm});
            skLineSegment(sketch, "E413.2.2.85", {"start": v(1.25, -15.3) * mm, "end": v(1.25, -17.25) * mm});
            skLineSegment(sketch, "E413.2.2.86", {"start": v(1.2, -7.25) * mm, "end": v(1.2, -9.25) * mm});
            skLineSegment(sketch, "E413.2.2.87", {"start": v(1.2, 8.7) * mm, "end": v(1.2, 6.7) * mm});
            skLineSegment(sketch, "E413.2.2.88", {"start": v(13.1, 20.75) * mm, "end": v(11.1, 18.75) * mm});
            skLineSegment(sketch, "E413.2.2.89", {"start": v(125.8, -9.25) * mm, "end": v(125.8, -11.3) * mm});
            skLineSegment(sketch, "E413.2.2.90", {"start": v(1.2, -13.25) * mm, "end": v(1.2, -13.3) * mm});
            skLineSegment(sketch, "E413.2.2.91", {"start": v(1.2, 2.75) * mm, "end": v(1.2, 2.7) * mm});
            skLineSegment(sketch, "E413.2.2.92", {"start": v(1.25, -7.3) * mm, "end": v(1.25, -9.25) * mm});
            skLineSegment(sketch, "E413.2.2.93", {"start": v(1.2, -9.25) * mm, "end": v(1.2, -9.3) * mm});
            skLineSegment(sketch, "E413.2.2.94", {"start": v(125.8, 8.92) * mm, "end": v(125.8, 8.7) * mm});
            skLineSegment(sketch, "E413.2.2.95", {"start": v(1.2, 8.75) * mm, "end": v(1.25, 8.75) * mm});
            skLineSegment(sketch, "E413.2.2.96", {"start": v(125.8, -15.3) * mm, "end": v(125.75, -15.3) * mm});
            skLineSegment(sketch, "E413.2.2.97", {"start": v(125.75, 8.9) * mm, "end": v(125.75, 8.75) * mm});
            skLineSegment(sketch, "E413.2.2.98", {"start": v(1.2, 8.7) * mm, "end": v(1.2, 8.75) * mm});
            skLineSegment(sketch, "E413.2.2.99", {"start": v(125.8, -15.25) * mm, "end": v(125.8, -15.3) * mm});
            skLineSegment(sketch, "E413.2.3.0", {"start": v(1.25, -79.3) * mm, "end": v(125.8, -79.3) * mm});
            skLineSegment(sketch, "E413.2.3.1", {"start": v(1.2, -93.3) * mm, "end": v(125.75, -93.3) * mm});
            skLineSegment(sketch, "E413.2.3.2", {"start": v(1.2, -81.3) * mm, "end": v(125.75, -81.3) * mm});
            skLineSegment(sketch, "E413.2.3.3", {"start": v(1.25, -95.3) * mm, "end": v(125.8, -95.3) * mm});
            skLineSegment(sketch, "E413.2.3.4", {"start": v(1.2, -97.3) * mm, "end": v(125.75, -97.3) * mm});
            skLineSegment(sketch, "E413.2.3.5", {"start": v(2.98, -77.3) * mm, "end": v(123.95, -77.3) * mm});
            skLineSegment(sketch, "E413.2.3.6", {"start": v(1.25, -83.3) * mm, "end": v(125.8, -83.3) * mm});
            skLineSegment(sketch, "E413.2.3.7", {"start": v(10.98, -69.3) * mm, "end": v(115.95, -69.3) * mm});
            skLineSegment(sketch, "E413.2.3.8", {"start": v(1.25, -103.3) * mm, "end": v(125.75, -103.3) * mm});
            skLineSegment(sketch, "E413.2.3.9", {"start": v(5.05, -75.3) * mm, "end": v(122.02, -75.3) * mm});
            skLineSegment(sketch, "E413.2.3.10", {"start": v(9.05, -71.3) * mm, "end": v(118.02, -71.3) * mm});
            skLineSegment(sketch, "E413.2.3.11", {"start": v(1.25, -99.3) * mm, "end": v(125.8, -99.3) * mm});
            skLineSegment(sketch, "E413.2.3.12", {"start": v(1.2, -101.3) * mm, "end": v(125.75, -101.3) * mm});
            skLineSegment(sketch, "E413.2.3.13", {"start": v(1.2, -85.3) * mm, "end": v(125.75, -85.3) * mm});
            skLineSegment(sketch, "E413.2.3.14", {"start": v(1.25, -87.3) * mm, "end": v(125.8, -87.3) * mm});
            skLineSegment(sketch, "E413.2.3.15", {"start": v(1.2, -89.3) * mm, "end": v(125.75, -89.3) * mm});
            skLineSegment(sketch, "E413.2.3.16", {"start": v(1.2, -105.3) * mm, "end": v(125.75, -105.3) * mm});
            skLineSegment(sketch, "E413.2.3.17", {"start": v(6.98, -73.3) * mm, "end": v(119.95, -73.3) * mm});
            skLineSegment(sketch, "E413.2.3.18", {"start": v(1.25, -107.3) * mm, "end": v(125.8, -107.3) * mm});
            skLineSegment(sketch, "E413.2.3.19", {"start": v(1.25, -91.3) * mm, "end": v(125.8, -91.3) * mm});
            skLineSegment(sketch, "E413.2.3.20", {"start": v(13.1, -67.25) * mm, "end": v(113.9, -67.25) * mm});
            skLineSegment(sketch, "E413.2.3.21", {"start": v(1.25, -93.25) * mm, "end": v(125.8, -93.25) * mm});
            skLineSegment(sketch, "E413.2.3.22", {"start": v(1.2, -95.25) * mm, "end": v(125.75, -95.25) * mm});
            skLineSegment(sketch, "E413.2.3.23", {"start": v(1.25, -97.25) * mm, "end": v(125.8, -97.25) * mm});
            skLineSegment(sketch, "E413.2.3.24", {"start": v(1.25, -79.25) * mm, "end": v(125.75, -79.25) * mm});
            skLineSegment(sketch, "E413.2.3.25", {"start": v(1.25, -81.25) * mm, "end": v(125.8, -81.25) * mm});
            skLineSegment(sketch, "E413.2.3.26", {"start": v(1.2, -83.25) * mm, "end": v(125.75, -83.25) * mm});
            skLineSegment(sketch, "E413.2.3.27", {"start": v(1.2, -103.25) * mm, "end": v(125.75, -103.25) * mm});
            skLineSegment(sketch, "E413.2.3.28", {"start": v(1.2, -87.25) * mm, "end": v(125.75, -87.25) * mm});
            skLineSegment(sketch, "E413.2.3.29", {"start": v(7.1, -73.25) * mm, "end": v(119.97, -73.25) * mm});
            skLineSegment(sketch, "E413.2.3.30", {"start": v(1.25, -89.25) * mm, "end": v(125.8, -89.25) * mm});
            skLineSegment(sketch, "E413.2.3.31", {"start": v(1.2, -107.25) * mm, "end": v(125.75, -107.25) * mm});
            skLineSegment(sketch, "E413.2.3.32", {"start": v(3.1, -77.25) * mm, "end": v(123.97, -77.25) * mm});
            skLineSegment(sketch, "E413.2.3.33", {"start": v(1.2, -99.25) * mm, "end": v(125.75, -99.25) * mm});
            skLineSegment(sketch, "E413.2.3.34", {"start": v(1.25, -85.25) * mm, "end": v(125.8, -85.25) * mm});
            skLineSegment(sketch, "E413.2.3.35", {"start": v(1.25, -101.25) * mm, "end": v(125.8, -101.25) * mm});
            skLineSegment(sketch, "E413.2.3.36", {"start": v(11.1, -69.25) * mm, "end": v(115.9, -69.25) * mm});
            skLineSegment(sketch, "E413.2.3.37", {"start": v(1.25, -105.25) * mm, "end": v(125.8, -105.25) * mm});
            skLineSegment(sketch, "E413.2.3.38", {"start": v(9.03, -71.25) * mm, "end": v(117.9, -71.25) * mm});
            skLineSegment(sketch, "E413.2.3.39", {"start": v(13.08, -67.2) * mm, "end": v(113.92, -67.2) * mm});
            skLineSegment(sketch, "E413.2.3.40", {"start": v(126, -79) * mm, "end": v(126, -109) * mm});
            skLineSegment(sketch, "E413.2.3.41", {"start": v(5.03, -75.25) * mm, "end": v(121.9, -75.25) * mm});
            skLineSegment(sketch, "E413.2.3.42", {"start": v(1.2, -91.25) * mm, "end": v(125.75, -91.25) * mm});
            skLineSegment(sketch, "E413.2.3.43", {"start": v(119.97, -73.25) * mm, "end": v(122.02, -75.3) * mm});
            skLineSegment(sketch, "E413.2.3.44", {"start": v(119.95, -73.3) * mm, "end": v(121.9, -75.25) * mm});
            skLineSegment(sketch, "E413.2.3.45", {"start": v(9.03, -71.25) * mm, "end": v(6.98, -73.3) * mm});
            skLineSegment(sketch, "E413.2.3.46", {"start": v(13, -67) * mm, "end": v(1, -79) * mm});
            skLineSegment(sketch, "E413.2.3.47", {"start": v(13, -67) * mm, "end": v(114, -67) * mm});
            skLineSegment(sketch, "E413.2.3.48", {"start": v(114, -67) * mm, "end": v(126, -79) * mm});
            skLineSegment(sketch, "E413.2.3.49", {"start": v(9.05, -71.3) * mm, "end": v(7.1, -73.25) * mm});
            skLineSegment(sketch, "E413.2.3.50", {"start": v(1.2, -83.25) * mm, "end": v(1.2, -85.25) * mm});
            skLineSegment(sketch, "E413.2.3.51", {"start": v(5.03, -75.25) * mm, "end": v(2.98, -77.3) * mm});
            skLineSegment(sketch, "E413.2.3.52", {"start": v(115.95, -69.3) * mm, "end": v(117.9, -71.25) * mm});
            skLineSegment(sketch, "E413.2.3.53", {"start": v(1.2, -87.25) * mm, "end": v(1.2, -89.3) * mm});
            skLineSegment(sketch, "E413.2.3.54", {"start": v(123.97, -77.25) * mm, "end": v(125.8, -79.08) * mm});
            skLineSegment(sketch, "E413.2.3.55", {"start": v(125.8, -105.25) * mm, "end": v(125.8, -107.3) * mm});
            skLineSegment(sketch, "E413.2.3.56", {"start": v(125.75, -101.3) * mm, "end": v(125.75, -103.25) * mm});
            skLineSegment(sketch, "E413.2.3.57", {"start": v(123.95, -77.3) * mm, "end": v(125.75, -79.1) * mm});
            skLineSegment(sketch, "E413.2.3.58", {"start": v(5.05, -75.3) * mm, "end": v(3.1, -77.25) * mm});
            skLineSegment(sketch, "E413.2.3.59", {"start": v(125.75, -81.3) * mm, "end": v(125.75, -83.25) * mm});
            skLineSegment(sketch, "E413.2.3.60", {"start": v(1.2, -107.25) * mm, "end": v(1.2, -109) * mm});
            skLineSegment(sketch, "E413.2.3.61", {"start": v(1.2, -103.25) * mm, "end": v(1.2, -105.3) * mm});
            skLineSegment(sketch, "E413.2.3.62", {"start": v(125.75, -89.3) * mm, "end": v(125.75, -91.25) * mm});
            skLineSegment(sketch, "E413.2.3.63", {"start": v(13.08, -67.2) * mm, "end": v(10.98, -69.3) * mm});
            skLineSegment(sketch, "E413.2.3.64", {"start": v(113.92, -67.2) * mm, "end": v(118.02, -71.3) * mm});
            skLineSegment(sketch, "E413.2.3.65", {"start": v(125.75, -97.3) * mm, "end": v(125.75, -99.25) * mm});
            skLineSegment(sketch, "E413.2.3.66", {"start": v(1.2, -91.25) * mm, "end": v(1.2, -93.3) * mm});
            skLineSegment(sketch, "E413.2.3.67", {"start": v(125.75, -85.3) * mm, "end": v(125.75, -87.25) * mm});
            skLineSegment(sketch, "E413.2.3.68", {"start": v(125.75, -93.3) * mm, "end": v(125.75, -95.25) * mm});
            skLineSegment(sketch, "E413.2.3.69", {"start": v(1.2, -99.25) * mm, "end": v(1.2, -101.25) * mm});
            skLineSegment(sketch, "E413.2.3.70", {"start": v(125.8, -93.25) * mm, "end": v(125.8, -95.3) * mm});
            skLineSegment(sketch, "E413.2.3.71", {"start": v(1.2, -109) * mm, "end": v(1.25, -109) * mm});
            skLineSegment(sketch, "E413.2.3.72", {"start": v(1, -79) * mm, "end": v(1, -109) * mm});
            skLineSegment(sketch, "E413.2.3.73", {"start": v(1.25, -79.3) * mm, "end": v(1.25, -81.25) * mm});
            skLineSegment(sketch, "E413.2.3.74", {"start": v(125.75, -105.3) * mm, "end": v(125.75, -107.25) * mm});
            skLineSegment(sketch, "E413.2.3.75", {"start": v(1.25, -83.3) * mm, "end": v(1.25, -85.25) * mm});
            skLineSegment(sketch, "E413.2.3.76", {"start": v(125.8, -101.25) * mm, "end": v(125.8, -103.25) * mm});
            skLineSegment(sketch, "E413.2.3.77", {"start": v(1.25, -87.3) * mm, "end": v(1.25, -89.3) * mm});
            skLineSegment(sketch, "E413.2.3.78", {"start": v(1.25, -107.3) * mm, "end": v(1.25, -109) * mm});
            skLineSegment(sketch, "E413.2.3.79", {"start": v(125.8, -85.25) * mm, "end": v(125.8, -87.3) * mm});
            skLineSegment(sketch, "E413.2.3.80", {"start": v(1.25, -99.3) * mm, "end": v(1.25, -101.25) * mm});
            skLineSegment(sketch, "E413.2.3.81", {"start": v(125.8, -89.25) * mm, "end": v(125.8, -91.3) * mm});
            skLineSegment(sketch, "E413.2.3.82", {"start": v(113.9, -67.25) * mm, "end": v(115.9, -69.25) * mm});
            skLineSegment(sketch, "E413.2.3.83", {"start": v(1.25, -91.3) * mm, "end": v(1.25, -93.25) * mm});
            skLineSegment(sketch, "E413.2.3.84", {"start": v(125.8, -81.25) * mm, "end": v(125.8, -83.3) * mm});
            skLineSegment(sketch, "E413.2.3.85", {"start": v(1.25, -103.3) * mm, "end": v(1.25, -105.25) * mm});
            skLineSegment(sketch, "E413.2.3.86", {"start": v(1.2, -95.25) * mm, "end": v(1.2, -97.25) * mm});
            skLineSegment(sketch, "E413.2.3.87", {"start": v(1.2, -79.3) * mm, "end": v(1.2, -81.3) * mm});
            skLineSegment(sketch, "E413.2.3.88", {"start": v(13.1, -67.25) * mm, "end": v(11.1, -69.25) * mm});
            skLineSegment(sketch, "E413.2.3.89", {"start": v(125.8, -97.25) * mm, "end": v(125.8, -99.3) * mm});
            skLineSegment(sketch, "E413.2.3.90", {"start": v(1.2, -101.25) * mm, "end": v(1.2, -101.3) * mm});
            skLineSegment(sketch, "E413.2.3.91", {"start": v(1.2, -85.25) * mm, "end": v(1.2, -85.3) * mm});
            skLineSegment(sketch, "E413.2.3.92", {"start": v(1.25, -95.3) * mm, "end": v(1.25, -97.25) * mm});
            skLineSegment(sketch, "E413.2.3.93", {"start": v(1.2, -97.25) * mm, "end": v(1.2, -97.3) * mm});
            skLineSegment(sketch, "E413.2.3.94", {"start": v(125.8, -79.08) * mm, "end": v(125.8, -79.3) * mm});
            skLineSegment(sketch, "E413.2.3.95", {"start": v(1.2, -79.25) * mm, "end": v(1.25, -79.25) * mm});
            skLineSegment(sketch, "E413.2.3.96", {"start": v(125.8, -103.3) * mm, "end": v(125.75, -103.3) * mm});
            skLineSegment(sketch, "E413.2.3.97", {"start": v(125.75, -79.1) * mm, "end": v(125.75, -79.25) * mm});
            skLineSegment(sketch, "E413.2.3.98", {"start": v(1.2, -79.3) * mm, "end": v(1.2, -79.25) * mm});
            skLineSegment(sketch, "E413.2.3.99", {"start": v(125.8, -103.25) * mm, "end": v(125.8, -103.3) * mm});
            skLineSegment(sketch, "E413.2.4.0", {"start": v(1.25, -167.3) * mm, "end": v(125.8, -167.3) * mm});
            skLineSegment(sketch, "E413.2.4.1", {"start": v(1.2, -181.3) * mm, "end": v(125.75, -181.3) * mm});
            skLineSegment(sketch, "E413.2.4.2", {"start": v(1.2, -169.3) * mm, "end": v(125.75, -169.3) * mm});
            skLineSegment(sketch, "E413.2.4.3", {"start": v(1.25, -183.3) * mm, "end": v(125.8, -183.3) * mm});
            skLineSegment(sketch, "E413.2.4.4", {"start": v(1.2, -185.3) * mm, "end": v(125.75, -185.3) * mm});
            skLineSegment(sketch, "E413.2.4.5", {"start": v(2.98, -165.3) * mm, "end": v(123.95, -165.3) * mm});
            skLineSegment(sketch, "E413.2.4.6", {"start": v(1.25, -171.3) * mm, "end": v(125.8, -171.3) * mm});
            skLineSegment(sketch, "E413.2.4.7", {"start": v(10.98, -157.3) * mm, "end": v(115.95, -157.3) * mm});
            skLineSegment(sketch, "E413.2.4.8", {"start": v(1.25, -191.3) * mm, "end": v(125.75, -191.3) * mm});
            skLineSegment(sketch, "E413.2.4.9", {"start": v(5.05, -163.3) * mm, "end": v(122.02, -163.3) * mm});
            skLineSegment(sketch, "E413.2.4.10", {"start": v(9.05, -159.3) * mm, "end": v(118.02, -159.3) * mm});
            skLineSegment(sketch, "E413.2.4.11", {"start": v(1.25, -187.3) * mm, "end": v(125.8, -187.3) * mm});
            skLineSegment(sketch, "E413.2.4.12", {"start": v(1.2, -189.3) * mm, "end": v(125.75, -189.3) * mm});
            skLineSegment(sketch, "E413.2.4.13", {"start": v(1.2, -173.3) * mm, "end": v(125.75, -173.3) * mm});
            skLineSegment(sketch, "E413.2.4.14", {"start": v(1.25, -175.3) * mm, "end": v(125.8, -175.3) * mm});
            skLineSegment(sketch, "E413.2.4.15", {"start": v(1.2, -177.3) * mm, "end": v(125.75, -177.3) * mm});
            skLineSegment(sketch, "E413.2.4.16", {"start": v(1.2, -193.3) * mm, "end": v(125.75, -193.3) * mm});
            skLineSegment(sketch, "E413.2.4.17", {"start": v(6.98, -161.3) * mm, "end": v(119.95, -161.3) * mm});
            skLineSegment(sketch, "E413.2.4.18", {"start": v(1.25, -195.3) * mm, "end": v(125.8, -195.3) * mm});
            skLineSegment(sketch, "E413.2.4.19", {"start": v(1.25, -179.3) * mm, "end": v(125.8, -179.3) * mm});
            skLineSegment(sketch, "E413.2.4.20", {"start": v(13.1, -155.25) * mm, "end": v(113.9, -155.25) * mm});
            skLineSegment(sketch, "E413.2.4.21", {"start": v(1.25, -181.25) * mm, "end": v(125.8, -181.25) * mm});
            skLineSegment(sketch, "E413.2.4.22", {"start": v(1.2, -183.25) * mm, "end": v(125.75, -183.25) * mm});
            skLineSegment(sketch, "E413.2.4.23", {"start": v(1.25, -185.25) * mm, "end": v(125.8, -185.25) * mm});
            skLineSegment(sketch, "E413.2.4.24", {"start": v(1.25, -167.25) * mm, "end": v(125.75, -167.25) * mm});
            skLineSegment(sketch, "E413.2.4.25", {"start": v(1.25, -169.25) * mm, "end": v(125.8, -169.25) * mm});
            skLineSegment(sketch, "E413.2.4.26", {"start": v(1.2, -171.25) * mm, "end": v(125.75, -171.25) * mm});
            skLineSegment(sketch, "E413.2.4.27", {"start": v(1.2, -191.25) * mm, "end": v(125.75, -191.25) * mm});
            skLineSegment(sketch, "E413.2.4.28", {"start": v(1.2, -175.25) * mm, "end": v(125.75, -175.25) * mm});
            skLineSegment(sketch, "E413.2.4.29", {"start": v(7.1, -161.25) * mm, "end": v(119.97, -161.25) * mm});
            skLineSegment(sketch, "E413.2.4.30", {"start": v(1.25, -177.25) * mm, "end": v(125.8, -177.25) * mm});
            skLineSegment(sketch, "E413.2.4.31", {"start": v(1.2, -195.25) * mm, "end": v(125.75, -195.25) * mm});
            skLineSegment(sketch, "E413.2.4.32", {"start": v(3.1, -165.25) * mm, "end": v(123.97, -165.25) * mm});
            skLineSegment(sketch, "E413.2.4.33", {"start": v(1.2, -187.25) * mm, "end": v(125.75, -187.25) * mm});
            skLineSegment(sketch, "E413.2.4.34", {"start": v(1.25, -173.25) * mm, "end": v(125.8, -173.25) * mm});
            skLineSegment(sketch, "E413.2.4.35", {"start": v(1.25, -189.25) * mm, "end": v(125.8, -189.25) * mm});
            skLineSegment(sketch, "E413.2.4.36", {"start": v(11.1, -157.25) * mm, "end": v(115.9, -157.25) * mm});
            skLineSegment(sketch, "E413.2.4.37", {"start": v(1.25, -193.25) * mm, "end": v(125.8, -193.25) * mm});
            skLineSegment(sketch, "E413.2.4.38", {"start": v(9.03, -159.25) * mm, "end": v(117.9, -159.25) * mm});
            skLineSegment(sketch, "E413.2.4.39", {"start": v(13.08, -155.2) * mm, "end": v(113.92, -155.2) * mm});
            skLineSegment(sketch, "E413.2.4.40", {"start": v(126, -167) * mm, "end": v(126, -197) * mm});
            skLineSegment(sketch, "E413.2.4.41", {"start": v(5.03, -163.25) * mm, "end": v(121.9, -163.25) * mm});
            skLineSegment(sketch, "E413.2.4.42", {"start": v(1.2, -179.25) * mm, "end": v(125.75, -179.25) * mm});
            skLineSegment(sketch, "E413.2.4.43", {"start": v(119.97, -161.25) * mm, "end": v(122.02, -163.3) * mm});
            skLineSegment(sketch, "E413.2.4.44", {"start": v(119.95, -161.3) * mm, "end": v(121.9, -163.25) * mm});
            skLineSegment(sketch, "E413.2.4.45", {"start": v(9.03, -159.25) * mm, "end": v(6.98, -161.3) * mm});
            skLineSegment(sketch, "E413.2.4.46", {"start": v(13, -155) * mm, "end": v(1, -167) * mm});
            skLineSegment(sketch, "E413.2.4.47", {"start": v(13, -155) * mm, "end": v(114, -155) * mm});
            skLineSegment(sketch, "E413.2.4.48", {"start": v(114, -155) * mm, "end": v(126, -167) * mm});
            skLineSegment(sketch, "E413.2.4.49", {"start": v(9.05, -159.3) * mm, "end": v(7.1, -161.25) * mm});
            skLineSegment(sketch, "E413.2.4.50", {"start": v(1.2, -171.25) * mm, "end": v(1.2, -173.25) * mm});
            skLineSegment(sketch, "E413.2.4.51", {"start": v(5.03, -163.25) * mm, "end": v(2.98, -165.3) * mm});
            skLineSegment(sketch, "E413.2.4.52", {"start": v(115.95, -157.3) * mm, "end": v(117.9, -159.25) * mm});
            skLineSegment(sketch, "E413.2.4.53", {"start": v(1.2, -175.25) * mm, "end": v(1.2, -177.3) * mm});
            skLineSegment(sketch, "E413.2.4.54", {"start": v(123.97, -165.25) * mm, "end": v(125.8, -167.08) * mm});
            skLineSegment(sketch, "E413.2.4.55", {"start": v(125.8, -193.25) * mm, "end": v(125.8, -195.3) * mm});
            skLineSegment(sketch, "E413.2.4.56", {"start": v(125.75, -189.3) * mm, "end": v(125.75, -191.25) * mm});
            skLineSegment(sketch, "E413.2.4.57", {"start": v(123.95, -165.3) * mm, "end": v(125.75, -167.1) * mm});
            skLineSegment(sketch, "E413.2.4.58", {"start": v(5.05, -163.3) * mm, "end": v(3.1, -165.25) * mm});
            skLineSegment(sketch, "E413.2.4.59", {"start": v(125.75, -169.3) * mm, "end": v(125.75, -171.25) * mm});
            skLineSegment(sketch, "E413.2.4.60", {"start": v(1.2, -195.25) * mm, "end": v(1.2, -197) * mm});
            skLineSegment(sketch, "E413.2.4.61", {"start": v(1.2, -191.25) * mm, "end": v(1.2, -193.3) * mm});
            skLineSegment(sketch, "E413.2.4.62", {"start": v(125.75, -177.3) * mm, "end": v(125.75, -179.25) * mm});
            skLineSegment(sketch, "E413.2.4.63", {"start": v(13.08, -155.2) * mm, "end": v(10.98, -157.3) * mm});
            skLineSegment(sketch, "E413.2.4.64", {"start": v(113.92, -155.2) * mm, "end": v(118.02, -159.3) * mm});
            skLineSegment(sketch, "E413.2.4.65", {"start": v(125.75, -185.3) * mm, "end": v(125.75, -187.25) * mm});
            skLineSegment(sketch, "E413.2.4.66", {"start": v(1.2, -179.25) * mm, "end": v(1.2, -181.3) * mm});
            skLineSegment(sketch, "E413.2.4.67", {"start": v(125.75, -173.3) * mm, "end": v(125.75, -175.25) * mm});
            skLineSegment(sketch, "E413.2.4.68", {"start": v(125.75, -181.3) * mm, "end": v(125.75, -183.25) * mm});
            skLineSegment(sketch, "E413.2.4.69", {"start": v(1.2, -187.25) * mm, "end": v(1.2, -189.25) * mm});
            skLineSegment(sketch, "E413.2.4.70", {"start": v(125.8, -181.25) * mm, "end": v(125.8, -183.3) * mm});
            skLineSegment(sketch, "E413.2.4.71", {"start": v(1.2, -197) * mm, "end": v(1.25, -197) * mm});
            skLineSegment(sketch, "E413.2.4.72", {"start": v(1, -167) * mm, "end": v(1, -197) * mm});
            skLineSegment(sketch, "E413.2.4.73", {"start": v(1.25, -167.3) * mm, "end": v(1.25, -169.25) * mm});
            skLineSegment(sketch, "E413.2.4.74", {"start": v(125.75, -193.3) * mm, "end": v(125.75, -195.25) * mm});
            skLineSegment(sketch, "E413.2.4.75", {"start": v(1.25, -171.3) * mm, "end": v(1.25, -173.25) * mm});
            skLineSegment(sketch, "E413.2.4.76", {"start": v(125.8, -189.25) * mm, "end": v(125.8, -191.25) * mm});
            skLineSegment(sketch, "E413.2.4.77", {"start": v(1.25, -175.3) * mm, "end": v(1.25, -177.3) * mm});
            skLineSegment(sketch, "E413.2.4.78", {"start": v(1.25, -195.3) * mm, "end": v(1.25, -197) * mm});
            skLineSegment(sketch, "E413.2.4.79", {"start": v(125.8, -173.25) * mm, "end": v(125.8, -175.3) * mm});
            skLineSegment(sketch, "E413.2.4.80", {"start": v(1.25, -187.3) * mm, "end": v(1.25, -189.25) * mm});
            skLineSegment(sketch, "E413.2.4.81", {"start": v(125.8, -177.25) * mm, "end": v(125.8, -179.3) * mm});
            skLineSegment(sketch, "E413.2.4.82", {"start": v(113.9, -155.25) * mm, "end": v(115.9, -157.25) * mm});
            skLineSegment(sketch, "E413.2.4.83", {"start": v(1.25, -179.3) * mm, "end": v(1.25, -181.25) * mm});
            skLineSegment(sketch, "E413.2.4.84", {"start": v(125.8, -169.25) * mm, "end": v(125.8, -171.3) * mm});
            skLineSegment(sketch, "E413.2.4.85", {"start": v(1.25, -191.3) * mm, "end": v(1.25, -193.25) * mm});
            skLineSegment(sketch, "E413.2.4.86", {"start": v(1.2, -183.25) * mm, "end": v(1.2, -185.25) * mm});
            skLineSegment(sketch, "E413.2.4.87", {"start": v(1.2, -167.3) * mm, "end": v(1.2, -169.3) * mm});
            skLineSegment(sketch, "E413.2.4.88", {"start": v(13.1, -155.25) * mm, "end": v(11.1, -157.25) * mm});
            skLineSegment(sketch, "E413.2.4.89", {"start": v(125.8, -185.25) * mm, "end": v(125.8, -187.3) * mm});
            skLineSegment(sketch, "E413.2.4.90", {"start": v(1.2, -189.25) * mm, "end": v(1.2, -189.3) * mm});
            skLineSegment(sketch, "E413.2.4.91", {"start": v(1.2, -173.25) * mm, "end": v(1.2, -173.3) * mm});
            skLineSegment(sketch, "E413.2.4.92", {"start": v(1.25, -183.3) * mm, "end": v(1.25, -185.25) * mm});
            skLineSegment(sketch, "E413.2.4.93", {"start": v(1.2, -185.25) * mm, "end": v(1.2, -185.3) * mm});
            skLineSegment(sketch, "E413.2.4.94", {"start": v(125.8, -167.08) * mm, "end": v(125.8, -167.3) * mm});
            skLineSegment(sketch, "E413.2.4.95", {"start": v(1.2, -167.25) * mm, "end": v(1.25, -167.25) * mm});
            skLineSegment(sketch, "E413.2.4.96", {"start": v(125.8, -191.3) * mm, "end": v(125.75, -191.3) * mm});
            skLineSegment(sketch, "E413.2.4.97", {"start": v(125.75, -167.1) * mm, "end": v(125.75, -167.25) * mm});
            skLineSegment(sketch, "E413.2.4.98", {"start": v(1.2, -167.3) * mm, "end": v(1.2, -167.25) * mm});
            skLineSegment(sketch, "E413.2.4.99", {"start": v(125.8, -191.25) * mm, "end": v(125.8, -191.3) * mm});
            skLineSegment(sketch, "E413.3.0.0", {"start": v(129.75, 184.7) * mm, "end": v(254.3, 184.7) * mm});
            skLineSegment(sketch, "E413.3.0.1", {"start": v(129.7, 170.7) * mm, "end": v(254.25, 170.7) * mm});
            skLineSegment(sketch, "E413.3.0.2", {"start": v(129.7, 182.7) * mm, "end": v(254.25, 182.7) * mm});
            skLineSegment(sketch, "E413.3.0.3", {"start": v(129.75, 168.7) * mm, "end": v(254.3, 168.7) * mm});
            skLineSegment(sketch, "E413.3.0.4", {"start": v(129.7, 166.7) * mm, "end": v(254.25, 166.7) * mm});
            skLineSegment(sketch, "E413.3.0.5", {"start": v(131.48, 186.7) * mm, "end": v(252.45, 186.7) * mm});
            skLineSegment(sketch, "E413.3.0.6", {"start": v(129.75, 180.7) * mm, "end": v(254.3, 180.7) * mm});
            skLineSegment(sketch, "E413.3.0.7", {"start": v(139.48, 194.7) * mm, "end": v(244.45, 194.7) * mm});
            skLineSegment(sketch, "E413.3.0.8", {"start": v(129.75, 160.7) * mm, "end": v(254.25, 160.7) * mm});
            skLineSegment(sketch, "E413.3.0.9", {"start": v(133.55, 188.7) * mm, "end": v(250.52, 188.7) * mm});
            skLineSegment(sketch, "E413.3.0.10", {"start": v(137.55, 192.7) * mm, "end": v(246.52, 192.7) * mm});
            skLineSegment(sketch, "E413.3.0.11", {"start": v(129.75, 164.7) * mm, "end": v(254.3, 164.7) * mm});
            skLineSegment(sketch, "E413.3.0.12", {"start": v(129.7, 162.7) * mm, "end": v(254.25, 162.7) * mm});
            skLineSegment(sketch, "E413.3.0.13", {"start": v(129.7, 178.7) * mm, "end": v(254.25, 178.7) * mm});
            skLineSegment(sketch, "E413.3.0.14", {"start": v(129.75, 176.7) * mm, "end": v(254.3, 176.7) * mm});
            skLineSegment(sketch, "E413.3.0.15", {"start": v(129.7, 174.7) * mm, "end": v(254.25, 174.7) * mm});
            skLineSegment(sketch, "E413.3.0.16", {"start": v(129.7, 158.7) * mm, "end": v(254.25, 158.7) * mm});
            skLineSegment(sketch, "E413.3.0.17", {"start": v(135.48, 190.7) * mm, "end": v(248.45, 190.7) * mm});
            skLineSegment(sketch, "E413.3.0.18", {"start": v(129.75, 156.7) * mm, "end": v(254.3, 156.7) * mm});
            skLineSegment(sketch, "E413.3.0.19", {"start": v(129.75, 172.7) * mm, "end": v(254.3, 172.7) * mm});
            skLineSegment(sketch, "E413.3.0.20", {"start": v(141.6, 196.75) * mm, "end": v(242.4, 196.75) * mm});
            skLineSegment(sketch, "E413.3.0.21", {"start": v(129.75, 170.75) * mm, "end": v(254.3, 170.75) * mm});
            skLineSegment(sketch, "E413.3.0.22", {"start": v(129.7, 168.75) * mm, "end": v(254.25, 168.75) * mm});
            skLineSegment(sketch, "E413.3.0.23", {"start": v(129.75, 166.75) * mm, "end": v(254.3, 166.75) * mm});
            skLineSegment(sketch, "E413.3.0.24", {"start": v(129.75, 184.75) * mm, "end": v(254.25, 184.75) * mm});
            skLineSegment(sketch, "E413.3.0.25", {"start": v(129.75, 182.75) * mm, "end": v(254.3, 182.75) * mm});
            skLineSegment(sketch, "E413.3.0.26", {"start": v(129.7, 180.75) * mm, "end": v(254.25, 180.75) * mm});
            skLineSegment(sketch, "E413.3.0.27", {"start": v(129.7, 160.75) * mm, "end": v(254.25, 160.75) * mm});
            skLineSegment(sketch, "E413.3.0.28", {"start": v(129.7, 176.75) * mm, "end": v(254.25, 176.75) * mm});
            skLineSegment(sketch, "E413.3.0.29", {"start": v(135.6, 190.75) * mm, "end": v(248.47, 190.75) * mm});
            skLineSegment(sketch, "E413.3.0.30", {"start": v(129.75, 174.75) * mm, "end": v(254.3, 174.75) * mm});
            skLineSegment(sketch, "E413.3.0.31", {"start": v(129.7, 156.75) * mm, "end": v(254.25, 156.75) * mm});
            skLineSegment(sketch, "E413.3.0.32", {"start": v(131.6, 186.75) * mm, "end": v(252.47, 186.75) * mm});
            skLineSegment(sketch, "E413.3.0.33", {"start": v(129.7, 164.75) * mm, "end": v(254.25, 164.75) * mm});
            skLineSegment(sketch, "E413.3.0.34", {"start": v(129.75, 178.75) * mm, "end": v(254.3, 178.75) * mm});
            skLineSegment(sketch, "E413.3.0.35", {"start": v(129.75, 162.75) * mm, "end": v(254.3, 162.75) * mm});
            skLineSegment(sketch, "E413.3.0.36", {"start": v(139.6, 194.75) * mm, "end": v(244.4, 194.75) * mm});
            skLineSegment(sketch, "E413.3.0.37", {"start": v(129.75, 158.75) * mm, "end": v(254.3, 158.75) * mm});
            skLineSegment(sketch, "E413.3.0.38", {"start": v(137.53, 192.75) * mm, "end": v(246.4, 192.75) * mm});
            skLineSegment(sketch, "E413.3.0.39", {"start": v(141.58, 196.8) * mm, "end": v(242.42, 196.8) * mm});
            skLineSegment(sketch, "E413.3.0.40", {"start": v(254.5, 185) * mm, "end": v(254.5, 155) * mm});
            skLineSegment(sketch, "E413.3.0.41", {"start": v(133.53, 188.75) * mm, "end": v(250.4, 188.75) * mm});
            skLineSegment(sketch, "E413.3.0.42", {"start": v(129.7, 172.75) * mm, "end": v(254.25, 172.75) * mm});
            skLineSegment(sketch, "E413.3.0.43", {"start": v(248.47, 190.75) * mm, "end": v(250.52, 188.7) * mm});
            skLineSegment(sketch, "E413.3.0.44", {"start": v(248.45, 190.7) * mm, "end": v(250.4, 188.75) * mm});
            skLineSegment(sketch, "E413.3.0.45", {"start": v(137.53, 192.75) * mm, "end": v(135.48, 190.7) * mm});
            skLineSegment(sketch, "E413.3.0.46", {"start": v(141.5, 197) * mm, "end": v(129.5, 185) * mm});
            skLineSegment(sketch, "E413.3.0.47", {"start": v(141.5, 197) * mm, "end": v(242.5, 197) * mm});
            skLineSegment(sketch, "E413.3.0.48", {"start": v(242.5, 197) * mm, "end": v(254.5, 185) * mm});
            skLineSegment(sketch, "E413.3.0.49", {"start": v(137.55, 192.7) * mm, "end": v(135.6, 190.75) * mm});
            skLineSegment(sketch, "E413.3.0.50", {"start": v(129.7, 180.75) * mm, "end": v(129.7, 178.75) * mm});
            skLineSegment(sketch, "E413.3.0.51", {"start": v(133.53, 188.75) * mm, "end": v(131.48, 186.7) * mm});
            skLineSegment(sketch, "E413.3.0.52", {"start": v(244.45, 194.7) * mm, "end": v(246.4, 192.75) * mm});
            skLineSegment(sketch, "E413.3.0.53", {"start": v(129.7, 176.75) * mm, "end": v(129.7, 174.7) * mm});
            skLineSegment(sketch, "E413.3.0.54", {"start": v(252.47, 186.75) * mm, "end": v(254.3, 184.92) * mm});
            skLineSegment(sketch, "E413.3.0.55", {"start": v(254.3, 158.75) * mm, "end": v(254.3, 156.7) * mm});
            skLineSegment(sketch, "E413.3.0.56", {"start": v(254.25, 162.7) * mm, "end": v(254.25, 160.75) * mm});
            skLineSegment(sketch, "E413.3.0.57", {"start": v(252.45, 186.7) * mm, "end": v(254.25, 184.9) * mm});
            skLineSegment(sketch, "E413.3.0.58", {"start": v(133.55, 188.7) * mm, "end": v(131.6, 186.75) * mm});
            skLineSegment(sketch, "E413.3.0.59", {"start": v(254.25, 182.7) * mm, "end": v(254.25, 180.75) * mm});
            skLineSegment(sketch, "E413.3.0.60", {"start": v(129.7, 156.75) * mm, "end": v(129.7, 155) * mm});
            skLineSegment(sketch, "E413.3.0.61", {"start": v(129.7, 160.75) * mm, "end": v(129.7, 158.7) * mm});
            skLineSegment(sketch, "E413.3.0.62", {"start": v(254.25, 174.7) * mm, "end": v(254.25, 172.75) * mm});
            skLineSegment(sketch, "E413.3.0.63", {"start": v(141.58, 196.8) * mm, "end": v(139.48, 194.7) * mm});
            skLineSegment(sketch, "E413.3.0.64", {"start": v(242.42, 196.8) * mm, "end": v(246.52, 192.7) * mm});
            skLineSegment(sketch, "E413.3.0.65", {"start": v(254.25, 166.7) * mm, "end": v(254.25, 164.75) * mm});
            skLineSegment(sketch, "E413.3.0.66", {"start": v(129.7, 172.75) * mm, "end": v(129.7, 170.7) * mm});
            skLineSegment(sketch, "E413.3.0.67", {"start": v(254.25, 178.7) * mm, "end": v(254.25, 176.75) * mm});
            skLineSegment(sketch, "E413.3.0.68", {"start": v(254.25, 170.7) * mm, "end": v(254.25, 168.75) * mm});
            skLineSegment(sketch, "E413.3.0.69", {"start": v(129.7, 164.75) * mm, "end": v(129.7, 162.75) * mm});
            skLineSegment(sketch, "E413.3.0.70", {"start": v(254.3, 170.75) * mm, "end": v(254.3, 168.7) * mm});
            skLineSegment(sketch, "E413.3.0.71", {"start": v(129.7, 155) * mm, "end": v(129.75, 155) * mm});
            skLineSegment(sketch, "E413.3.0.72", {"start": v(129.5, 185) * mm, "end": v(129.5, 155) * mm});
            skLineSegment(sketch, "E413.3.0.73", {"start": v(129.75, 184.7) * mm, "end": v(129.75, 182.75) * mm});
            skLineSegment(sketch, "E413.3.0.74", {"start": v(254.25, 158.7) * mm, "end": v(254.25, 156.75) * mm});
            skLineSegment(sketch, "E413.3.0.75", {"start": v(129.75, 180.7) * mm, "end": v(129.75, 178.75) * mm});
            skLineSegment(sketch, "E413.3.0.76", {"start": v(254.3, 162.75) * mm, "end": v(254.3, 160.75) * mm});
            skLineSegment(sketch, "E413.3.0.77", {"start": v(129.75, 176.7) * mm, "end": v(129.75, 174.7) * mm});
            skLineSegment(sketch, "E413.3.0.78", {"start": v(129.75, 156.7) * mm, "end": v(129.75, 155) * mm});
            skLineSegment(sketch, "E413.3.0.79", {"start": v(254.3, 178.75) * mm, "end": v(254.3, 176.7) * mm});
            skLineSegment(sketch, "E413.3.0.80", {"start": v(129.75, 164.7) * mm, "end": v(129.75, 162.75) * mm});
            skLineSegment(sketch, "E413.3.0.81", {"start": v(254.3, 174.75) * mm, "end": v(254.3, 172.7) * mm});
            skLineSegment(sketch, "E413.3.0.82", {"start": v(242.4, 196.75) * mm, "end": v(244.4, 194.75) * mm});
            skLineSegment(sketch, "E413.3.0.83", {"start": v(129.75, 172.7) * mm, "end": v(129.75, 170.75) * mm});
            skLineSegment(sketch, "E413.3.0.84", {"start": v(254.3, 182.75) * mm, "end": v(254.3, 180.7) * mm});
            skLineSegment(sketch, "E413.3.0.85", {"start": v(129.75, 160.7) * mm, "end": v(129.75, 158.75) * mm});
            skLineSegment(sketch, "E413.3.0.86", {"start": v(129.7, 168.75) * mm, "end": v(129.7, 166.75) * mm});
            skLineSegment(sketch, "E413.3.0.87", {"start": v(129.7, 184.7) * mm, "end": v(129.7, 182.7) * mm});
            skLineSegment(sketch, "E413.3.0.88", {"start": v(141.6, 196.75) * mm, "end": v(139.6, 194.75) * mm});
            skLineSegment(sketch, "E413.3.0.89", {"start": v(254.3, 166.75) * mm, "end": v(254.3, 164.7) * mm});
            skLineSegment(sketch, "E413.3.0.90", {"start": v(129.7, 162.75) * mm, "end": v(129.7, 162.7) * mm});
            skLineSegment(sketch, "E413.3.0.91", {"start": v(129.7, 178.75) * mm, "end": v(129.7, 178.7) * mm});
            skLineSegment(sketch, "E413.3.0.92", {"start": v(129.75, 168.7) * mm, "end": v(129.75, 166.75) * mm});
            skLineSegment(sketch, "E413.3.0.93", {"start": v(129.7, 166.75) * mm, "end": v(129.7, 166.7) * mm});
            skLineSegment(sketch, "E413.3.0.94", {"start": v(254.3, 184.92) * mm, "end": v(254.3, 184.7) * mm});
            skLineSegment(sketch, "E413.3.0.95", {"start": v(129.7, 184.75) * mm, "end": v(129.75, 184.75) * mm});
            skLineSegment(sketch, "E413.3.0.96", {"start": v(254.3, 160.7) * mm, "end": v(254.25, 160.7) * mm});
            skLineSegment(sketch, "E413.3.0.97", {"start": v(254.25, 184.9) * mm, "end": v(254.25, 184.75) * mm});
            skLineSegment(sketch, "E413.3.0.98", {"start": v(129.7, 184.7) * mm, "end": v(129.7, 184.75) * mm});
            skLineSegment(sketch, "E413.3.0.99", {"start": v(254.3, 160.75) * mm, "end": v(254.3, 160.7) * mm});
            skLineSegment(sketch, "E413.3.1.0", {"start": v(129.75, 96.7) * mm, "end": v(254.3, 96.7) * mm});
            skLineSegment(sketch, "E413.3.1.1", {"start": v(129.7, 82.7) * mm, "end": v(254.25, 82.7) * mm});
            skLineSegment(sketch, "E413.3.1.2", {"start": v(129.7, 94.7) * mm, "end": v(254.25, 94.7) * mm});
            skLineSegment(sketch, "E413.3.1.3", {"start": v(129.75, 80.7) * mm, "end": v(254.3, 80.7) * mm});
            skLineSegment(sketch, "E413.3.1.4", {"start": v(129.7, 78.7) * mm, "end": v(254.25, 78.7) * mm});
            skLineSegment(sketch, "E413.3.1.5", {"start": v(131.48, 98.7) * mm, "end": v(252.45, 98.7) * mm});
            skLineSegment(sketch, "E413.3.1.6", {"start": v(129.75, 92.7) * mm, "end": v(254.3, 92.7) * mm});
            skLineSegment(sketch, "E413.3.1.7", {"start": v(139.48, 106.7) * mm, "end": v(244.45, 106.7) * mm});
            skLineSegment(sketch, "E413.3.1.8", {"start": v(129.75, 72.7) * mm, "end": v(254.25, 72.7) * mm});
            skLineSegment(sketch, "E413.3.1.9", {"start": v(133.55, 100.7) * mm, "end": v(250.52, 100.7) * mm});
            skLineSegment(sketch, "E413.3.1.10", {"start": v(137.55, 104.7) * mm, "end": v(246.52, 104.7) * mm});
            skLineSegment(sketch, "E413.3.1.11", {"start": v(129.75, 76.7) * mm, "end": v(254.3, 76.7) * mm});
            skLineSegment(sketch, "E413.3.1.12", {"start": v(129.7, 74.7) * mm, "end": v(254.25, 74.7) * mm});
            skLineSegment(sketch, "E413.3.1.13", {"start": v(129.7, 90.7) * mm, "end": v(254.25, 90.7) * mm});
            skLineSegment(sketch, "E413.3.1.14", {"start": v(129.75, 88.7) * mm, "end": v(254.3, 88.7) * mm});
            skLineSegment(sketch, "E413.3.1.15", {"start": v(129.7, 86.7) * mm, "end": v(254.25, 86.7) * mm});
            skLineSegment(sketch, "E413.3.1.16", {"start": v(129.7, 70.7) * mm, "end": v(254.25, 70.7) * mm});
            skLineSegment(sketch, "E413.3.1.17", {"start": v(135.48, 102.7) * mm, "end": v(248.45, 102.7) * mm});
            skLineSegment(sketch, "E413.3.1.18", {"start": v(129.75, 68.7) * mm, "end": v(254.3, 68.7) * mm});
            skLineSegment(sketch, "E413.3.1.19", {"start": v(129.75, 84.7) * mm, "end": v(254.3, 84.7) * mm});
            skLineSegment(sketch, "E413.3.1.20", {"start": v(141.6, 108.75) * mm, "end": v(242.4, 108.75) * mm});
            skLineSegment(sketch, "E413.3.1.21", {"start": v(129.75, 82.75) * mm, "end": v(254.3, 82.75) * mm});
            skLineSegment(sketch, "E413.3.1.22", {"start": v(129.7, 80.75) * mm, "end": v(254.25, 80.75) * mm});
            skLineSegment(sketch, "E413.3.1.23", {"start": v(129.75, 78.75) * mm, "end": v(254.3, 78.75) * mm});
            skLineSegment(sketch, "E413.3.1.24", {"start": v(129.75, 96.75) * mm, "end": v(254.25, 96.75) * mm});
            skLineSegment(sketch, "E413.3.1.25", {"start": v(129.75, 94.75) * mm, "end": v(254.3, 94.75) * mm});
            skLineSegment(sketch, "E413.3.1.26", {"start": v(129.7, 92.75) * mm, "end": v(254.25, 92.75) * mm});
            skLineSegment(sketch, "E413.3.1.27", {"start": v(129.7, 72.75) * mm, "end": v(254.25, 72.75) * mm});
            skLineSegment(sketch, "E413.3.1.28", {"start": v(129.7, 88.75) * mm, "end": v(254.25, 88.75) * mm});
            skLineSegment(sketch, "E413.3.1.29", {"start": v(135.6, 102.75) * mm, "end": v(248.47, 102.75) * mm});
            skLineSegment(sketch, "E413.3.1.30", {"start": v(129.75, 86.75) * mm, "end": v(254.3, 86.75) * mm});
            skLineSegment(sketch, "E413.3.1.31", {"start": v(129.7, 68.75) * mm, "end": v(254.25, 68.75) * mm});
            skLineSegment(sketch, "E413.3.1.32", {"start": v(131.6, 98.75) * mm, "end": v(252.47, 98.75) * mm});
            skLineSegment(sketch, "E413.3.1.33", {"start": v(129.7, 76.75) * mm, "end": v(254.25, 76.75) * mm});
            skLineSegment(sketch, "E413.3.1.34", {"start": v(129.75, 90.75) * mm, "end": v(254.3, 90.75) * mm});
            skLineSegment(sketch, "E413.3.1.35", {"start": v(129.75, 74.75) * mm, "end": v(254.3, 74.75) * mm});
            skLineSegment(sketch, "E413.3.1.36", {"start": v(139.6, 106.75) * mm, "end": v(244.4, 106.75) * mm});
            skLineSegment(sketch, "E413.3.1.37", {"start": v(129.75, 70.75) * mm, "end": v(254.3, 70.75) * mm});
            skLineSegment(sketch, "E413.3.1.38", {"start": v(137.53, 104.75) * mm, "end": v(246.4, 104.75) * mm});
            skLineSegment(sketch, "E413.3.1.39", {"start": v(141.58, 108.8) * mm, "end": v(242.42, 108.8) * mm});
            skLineSegment(sketch, "E413.3.1.40", {"start": v(254.5, 97) * mm, "end": v(254.5, 67) * mm});
            skLineSegment(sketch, "E413.3.1.41", {"start": v(133.53, 100.75) * mm, "end": v(250.4, 100.75) * mm});
            skLineSegment(sketch, "E413.3.1.42", {"start": v(129.7, 84.75) * mm, "end": v(254.25, 84.75) * mm});
            skLineSegment(sketch, "E413.3.1.43", {"start": v(248.47, 102.75) * mm, "end": v(250.52, 100.7) * mm});
            skLineSegment(sketch, "E413.3.1.44", {"start": v(248.45, 102.7) * mm, "end": v(250.4, 100.75) * mm});
            skLineSegment(sketch, "E413.3.1.45", {"start": v(137.53, 104.75) * mm, "end": v(135.48, 102.7) * mm});
            skLineSegment(sketch, "E413.3.1.46", {"start": v(141.5, 109) * mm, "end": v(129.5, 97) * mm});
            skLineSegment(sketch, "E413.3.1.47", {"start": v(141.5, 109) * mm, "end": v(242.5, 109) * mm});
            skLineSegment(sketch, "E413.3.1.48", {"start": v(242.5, 109) * mm, "end": v(254.5, 97) * mm});
            skLineSegment(sketch, "E413.3.1.49", {"start": v(137.55, 104.7) * mm, "end": v(135.6, 102.75) * mm});
            skLineSegment(sketch, "E413.3.1.50", {"start": v(129.7, 92.75) * mm, "end": v(129.7, 90.75) * mm});
            skLineSegment(sketch, "E413.3.1.51", {"start": v(133.53, 100.75) * mm, "end": v(131.48, 98.7) * mm});
            skLineSegment(sketch, "E413.3.1.52", {"start": v(244.45, 106.7) * mm, "end": v(246.4, 104.75) * mm});
            skLineSegment(sketch, "E413.3.1.53", {"start": v(129.7, 88.75) * mm, "end": v(129.7, 86.7) * mm});
            skLineSegment(sketch, "E413.3.1.54", {"start": v(252.47, 98.75) * mm, "end": v(254.3, 96.92) * mm});
            skLineSegment(sketch, "E413.3.1.55", {"start": v(254.3, 70.75) * mm, "end": v(254.3, 68.7) * mm});
            skLineSegment(sketch, "E413.3.1.56", {"start": v(254.25, 74.7) * mm, "end": v(254.25, 72.75) * mm});
            skLineSegment(sketch, "E413.3.1.57", {"start": v(252.45, 98.7) * mm, "end": v(254.25, 96.9) * mm});
            skLineSegment(sketch, "E413.3.1.58", {"start": v(133.55, 100.7) * mm, "end": v(131.6, 98.75) * mm});
            skLineSegment(sketch, "E413.3.1.59", {"start": v(254.25, 94.7) * mm, "end": v(254.25, 92.75) * mm});
            skLineSegment(sketch, "E413.3.1.60", {"start": v(129.7, 68.75) * mm, "end": v(129.7, 67) * mm});
            skLineSegment(sketch, "E413.3.1.61", {"start": v(129.7, 72.75) * mm, "end": v(129.7, 70.7) * mm});
            skLineSegment(sketch, "E413.3.1.62", {"start": v(254.25, 86.7) * mm, "end": v(254.25, 84.75) * mm});
            skLineSegment(sketch, "E413.3.1.63", {"start": v(141.58, 108.8) * mm, "end": v(139.48, 106.7) * mm});
            skLineSegment(sketch, "E413.3.1.64", {"start": v(242.42, 108.8) * mm, "end": v(246.52, 104.7) * mm});
            skLineSegment(sketch, "E413.3.1.65", {"start": v(254.25, 78.7) * mm, "end": v(254.25, 76.75) * mm});
            skLineSegment(sketch, "E413.3.1.66", {"start": v(129.7, 84.75) * mm, "end": v(129.7, 82.7) * mm});
            skLineSegment(sketch, "E413.3.1.67", {"start": v(254.25, 90.7) * mm, "end": v(254.25, 88.75) * mm});
            skLineSegment(sketch, "E413.3.1.68", {"start": v(254.25, 82.7) * mm, "end": v(254.25, 80.75) * mm});
            skLineSegment(sketch, "E413.3.1.69", {"start": v(129.7, 76.75) * mm, "end": v(129.7, 74.75) * mm});
            skLineSegment(sketch, "E413.3.1.70", {"start": v(254.3, 82.75) * mm, "end": v(254.3, 80.7) * mm});
            skLineSegment(sketch, "E413.3.1.71", {"start": v(129.7, 67) * mm, "end": v(129.75, 67) * mm});
            skLineSegment(sketch, "E413.3.1.72", {"start": v(129.5, 97) * mm, "end": v(129.5, 67) * mm});
            skLineSegment(sketch, "E413.3.1.73", {"start": v(129.75, 96.7) * mm, "end": v(129.75, 94.75) * mm});
            skLineSegment(sketch, "E413.3.1.74", {"start": v(254.25, 70.7) * mm, "end": v(254.25, 68.75) * mm});
            skLineSegment(sketch, "E413.3.1.75", {"start": v(129.75, 92.7) * mm, "end": v(129.75, 90.75) * mm});
            skLineSegment(sketch, "E413.3.1.76", {"start": v(254.3, 74.75) * mm, "end": v(254.3, 72.75) * mm});
            skLineSegment(sketch, "E413.3.1.77", {"start": v(129.75, 88.7) * mm, "end": v(129.75, 86.7) * mm});
            skLineSegment(sketch, "E413.3.1.78", {"start": v(129.75, 68.7) * mm, "end": v(129.75, 67) * mm});
            skLineSegment(sketch, "E413.3.1.79", {"start": v(254.3, 90.75) * mm, "end": v(254.3, 88.7) * mm});
            skLineSegment(sketch, "E413.3.1.80", {"start": v(129.75, 76.7) * mm, "end": v(129.75, 74.75) * mm});
            skLineSegment(sketch, "E413.3.1.81", {"start": v(254.3, 86.75) * mm, "end": v(254.3, 84.7) * mm});
            skLineSegment(sketch, "E413.3.1.82", {"start": v(242.4, 108.75) * mm, "end": v(244.4, 106.75) * mm});
            skLineSegment(sketch, "E413.3.1.83", {"start": v(129.75, 84.7) * mm, "end": v(129.75, 82.75) * mm});
            skLineSegment(sketch, "E413.3.1.84", {"start": v(254.3, 94.75) * mm, "end": v(254.3, 92.7) * mm});
            skLineSegment(sketch, "E413.3.1.85", {"start": v(129.75, 72.7) * mm, "end": v(129.75, 70.75) * mm});
            skLineSegment(sketch, "E413.3.1.86", {"start": v(129.7, 80.75) * mm, "end": v(129.7, 78.75) * mm});
            skLineSegment(sketch, "E413.3.1.87", {"start": v(129.7, 96.7) * mm, "end": v(129.7, 94.7) * mm});
            skLineSegment(sketch, "E413.3.1.88", {"start": v(141.6, 108.75) * mm, "end": v(139.6, 106.75) * mm});
            skLineSegment(sketch, "E413.3.1.89", {"start": v(254.3, 78.75) * mm, "end": v(254.3, 76.7) * mm});
            skLineSegment(sketch, "E413.3.1.90", {"start": v(129.7, 74.75) * mm, "end": v(129.7, 74.7) * mm});
            skLineSegment(sketch, "E413.3.1.91", {"start": v(129.7, 90.75) * mm, "end": v(129.7, 90.7) * mm});
            skLineSegment(sketch, "E413.3.1.92", {"start": v(129.75, 80.7) * mm, "end": v(129.75, 78.75) * mm});
            skLineSegment(sketch, "E413.3.1.93", {"start": v(129.7, 78.75) * mm, "end": v(129.7, 78.7) * mm});
            skLineSegment(sketch, "E413.3.1.94", {"start": v(254.3, 96.92) * mm, "end": v(254.3, 96.7) * mm});
            skLineSegment(sketch, "E413.3.1.95", {"start": v(129.7, 96.75) * mm, "end": v(129.75, 96.75) * mm});
            skLineSegment(sketch, "E413.3.1.96", {"start": v(254.3, 72.7) * mm, "end": v(254.25, 72.7) * mm});
            skLineSegment(sketch, "E413.3.1.97", {"start": v(254.25, 96.9) * mm, "end": v(254.25, 96.75) * mm});
            skLineSegment(sketch, "E413.3.1.98", {"start": v(129.7, 96.7) * mm, "end": v(129.7, 96.75) * mm});
            skLineSegment(sketch, "E413.3.1.99", {"start": v(254.3, 72.75) * mm, "end": v(254.3, 72.7) * mm});
            skLineSegment(sketch, "E413.3.2.0", {"start": v(129.75, 8.7) * mm, "end": v(254.3, 8.7) * mm});
            skLineSegment(sketch, "E413.3.2.1", {"start": v(129.7, -5.3) * mm, "end": v(254.25, -5.3) * mm});
            skLineSegment(sketch, "E413.3.2.2", {"start": v(129.7, 6.7) * mm, "end": v(254.25, 6.7) * mm});
            skLineSegment(sketch, "E413.3.2.3", {"start": v(129.75, -7.3) * mm, "end": v(254.3, -7.3) * mm});
            skLineSegment(sketch, "E413.3.2.4", {"start": v(129.7, -9.3) * mm, "end": v(254.25, -9.3) * mm});
            skLineSegment(sketch, "E413.3.2.5", {"start": v(131.48, 10.7) * mm, "end": v(252.45, 10.7) * mm});
            skLineSegment(sketch, "E413.3.2.6", {"start": v(129.75, 4.7) * mm, "end": v(254.3, 4.7) * mm});
            skLineSegment(sketch, "E413.3.2.7", {"start": v(139.48, 18.7) * mm, "end": v(244.45, 18.7) * mm});
            skLineSegment(sketch, "E413.3.2.8", {"start": v(129.75, -15.3) * mm, "end": v(254.25, -15.3) * mm});
            skLineSegment(sketch, "E413.3.2.9", {"start": v(133.55, 12.7) * mm, "end": v(250.52, 12.7) * mm});
            skLineSegment(sketch, "E413.3.2.10", {"start": v(137.55, 16.7) * mm, "end": v(246.52, 16.7) * mm});
            skLineSegment(sketch, "E413.3.2.11", {"start": v(129.75, -11.3) * mm, "end": v(254.3, -11.3) * mm});
            skLineSegment(sketch, "E413.3.2.12", {"start": v(129.7, -13.3) * mm, "end": v(254.25, -13.3) * mm});
            skLineSegment(sketch, "E413.3.2.13", {"start": v(129.7, 2.7) * mm, "end": v(254.25, 2.7) * mm});
            skLineSegment(sketch, "E413.3.2.14", {"start": v(129.75, 0.7) * mm, "end": v(254.3, 0.7) * mm});
            skLineSegment(sketch, "E413.3.2.15", {"start": v(129.7, -1.3) * mm, "end": v(254.25, -1.3) * mm});
            skLineSegment(sketch, "E413.3.2.16", {"start": v(129.7, -17.3) * mm, "end": v(254.25, -17.3) * mm});
            skLineSegment(sketch, "E413.3.2.17", {"start": v(135.48, 14.7) * mm, "end": v(248.45, 14.7) * mm});
            skLineSegment(sketch, "E413.3.2.18", {"start": v(129.75, -19.3) * mm, "end": v(254.3, -19.3) * mm});
            skLineSegment(sketch, "E413.3.2.19", {"start": v(129.75, -3.3) * mm, "end": v(254.3, -3.3) * mm});
            skLineSegment(sketch, "E413.3.2.20", {"start": v(141.6, 20.75) * mm, "end": v(242.4, 20.75) * mm});
            skLineSegment(sketch, "E413.3.2.21", {"start": v(129.75, -5.25) * mm, "end": v(254.3, -5.25) * mm});
            skLineSegment(sketch, "E413.3.2.22", {"start": v(129.7, -7.25) * mm, "end": v(254.25, -7.25) * mm});
            skLineSegment(sketch, "E413.3.2.23", {"start": v(129.75, -9.25) * mm, "end": v(254.3, -9.25) * mm});
            skLineSegment(sketch, "E413.3.2.24", {"start": v(129.75, 8.75) * mm, "end": v(254.25, 8.75) * mm});
            skLineSegment(sketch, "E413.3.2.25", {"start": v(129.75, 6.75) * mm, "end": v(254.3, 6.75) * mm});
            skLineSegment(sketch, "E413.3.2.26", {"start": v(129.7, 4.75) * mm, "end": v(254.25, 4.75) * mm});
            skLineSegment(sketch, "E413.3.2.27", {"start": v(129.7, -15.25) * mm, "end": v(254.25, -15.25) * mm});
            skLineSegment(sketch, "E413.3.2.28", {"start": v(129.7, 0.75) * mm, "end": v(254.25, 0.75) * mm});
            skLineSegment(sketch, "E413.3.2.29", {"start": v(135.6, 14.75) * mm, "end": v(248.47, 14.75) * mm});
            skLineSegment(sketch, "E413.3.2.30", {"start": v(129.75, -1.25) * mm, "end": v(254.3, -1.25) * mm});
            skLineSegment(sketch, "E413.3.2.31", {"start": v(129.7, -19.25) * mm, "end": v(254.25, -19.25) * mm});
            skLineSegment(sketch, "E413.3.2.32", {"start": v(131.6, 10.75) * mm, "end": v(252.47, 10.75) * mm});
            skLineSegment(sketch, "E413.3.2.33", {"start": v(129.7, -11.25) * mm, "end": v(254.25, -11.25) * mm});
            skLineSegment(sketch, "E413.3.2.34", {"start": v(129.75, 2.75) * mm, "end": v(254.3, 2.75) * mm});
            skLineSegment(sketch, "E413.3.2.35", {"start": v(129.75, -13.25) * mm, "end": v(254.3, -13.25) * mm});
            skLineSegment(sketch, "E413.3.2.36", {"start": v(139.6, 18.75) * mm, "end": v(244.4, 18.75) * mm});
            skLineSegment(sketch, "E413.3.2.37", {"start": v(129.75, -17.25) * mm, "end": v(254.3, -17.25) * mm});
            skLineSegment(sketch, "E413.3.2.38", {"start": v(137.53, 16.75) * mm, "end": v(246.4, 16.75) * mm});
            skLineSegment(sketch, "E413.3.2.39", {"start": v(141.58, 20.8) * mm, "end": v(242.42, 20.8) * mm});
            skLineSegment(sketch, "E413.3.2.40", {"start": v(254.5, 9) * mm, "end": v(254.5, -21) * mm});
            skLineSegment(sketch, "E413.3.2.41", {"start": v(133.53, 12.75) * mm, "end": v(250.4, 12.75) * mm});
            skLineSegment(sketch, "E413.3.2.42", {"start": v(129.7, -3.25) * mm, "end": v(254.25, -3.25) * mm});
            skLineSegment(sketch, "E413.3.2.43", {"start": v(248.47, 14.75) * mm, "end": v(250.52, 12.7) * mm});
            skLineSegment(sketch, "E413.3.2.44", {"start": v(248.45, 14.7) * mm, "end": v(250.4, 12.75) * mm});
            skLineSegment(sketch, "E413.3.2.45", {"start": v(137.53, 16.75) * mm, "end": v(135.48, 14.7) * mm});
            skLineSegment(sketch, "E413.3.2.46", {"start": v(141.5, 21) * mm, "end": v(129.5, 9) * mm});
            skLineSegment(sketch, "E413.3.2.47", {"start": v(141.5, 21) * mm, "end": v(242.5, 21) * mm});
            skLineSegment(sketch, "E413.3.2.48", {"start": v(242.5, 21) * mm, "end": v(254.5, 9) * mm});
            skLineSegment(sketch, "E413.3.2.49", {"start": v(137.55, 16.7) * mm, "end": v(135.6, 14.75) * mm});
            skLineSegment(sketch, "E413.3.2.50", {"start": v(129.7, 4.75) * mm, "end": v(129.7, 2.75) * mm});
            skLineSegment(sketch, "E413.3.2.51", {"start": v(133.53, 12.75) * mm, "end": v(131.48, 10.7) * mm});
            skLineSegment(sketch, "E413.3.2.52", {"start": v(244.45, 18.7) * mm, "end": v(246.4, 16.75) * mm});
            skLineSegment(sketch, "E413.3.2.53", {"start": v(129.7, 0.75) * mm, "end": v(129.7, -1.3) * mm});
            skLineSegment(sketch, "E413.3.2.54", {"start": v(252.47, 10.75) * mm, "end": v(254.3, 8.92) * mm});
            skLineSegment(sketch, "E413.3.2.55", {"start": v(254.3, -17.25) * mm, "end": v(254.3, -19.3) * mm});
            skLineSegment(sketch, "E413.3.2.56", {"start": v(254.25, -13.3) * mm, "end": v(254.25, -15.25) * mm});
            skLineSegment(sketch, "E413.3.2.57", {"start": v(252.45, 10.7) * mm, "end": v(254.25, 8.9) * mm});
            skLineSegment(sketch, "E413.3.2.58", {"start": v(133.55, 12.7) * mm, "end": v(131.6, 10.75) * mm});
            skLineSegment(sketch, "E413.3.2.59", {"start": v(254.25, 6.7) * mm, "end": v(254.25, 4.75) * mm});
            skLineSegment(sketch, "E413.3.2.60", {"start": v(129.7, -19.25) * mm, "end": v(129.7, -21) * mm});
            skLineSegment(sketch, "E413.3.2.61", {"start": v(129.7, -15.25) * mm, "end": v(129.7, -17.3) * mm});
            skLineSegment(sketch, "E413.3.2.62", {"start": v(254.25, -1.3) * mm, "end": v(254.25, -3.25) * mm});
            skLineSegment(sketch, "E413.3.2.63", {"start": v(141.58, 20.8) * mm, "end": v(139.48, 18.7) * mm});
            skLineSegment(sketch, "E413.3.2.64", {"start": v(242.42, 20.8) * mm, "end": v(246.52, 16.7) * mm});
            skLineSegment(sketch, "E413.3.2.65", {"start": v(254.25, -9.3) * mm, "end": v(254.25, -11.25) * mm});
            skLineSegment(sketch, "E413.3.2.66", {"start": v(129.7, -3.25) * mm, "end": v(129.7, -5.3) * mm});
            skLineSegment(sketch, "E413.3.2.67", {"start": v(254.25, 2.7) * mm, "end": v(254.25, 0.75) * mm});
            skLineSegment(sketch, "E413.3.2.68", {"start": v(254.25, -5.3) * mm, "end": v(254.25, -7.25) * mm});
            skLineSegment(sketch, "E413.3.2.69", {"start": v(129.7, -11.25) * mm, "end": v(129.7, -13.25) * mm});
            skLineSegment(sketch, "E413.3.2.70", {"start": v(254.3, -5.25) * mm, "end": v(254.3, -7.3) * mm});
            skLineSegment(sketch, "E413.3.2.71", {"start": v(129.7, -21) * mm, "end": v(129.75, -21) * mm});
            skLineSegment(sketch, "E413.3.2.72", {"start": v(129.5, 9) * mm, "end": v(129.5, -21) * mm});
            skLineSegment(sketch, "E413.3.2.73", {"start": v(129.75, 8.7) * mm, "end": v(129.75, 6.75) * mm});
            skLineSegment(sketch, "E413.3.2.74", {"start": v(254.25, -17.3) * mm, "end": v(254.25, -19.25) * mm});
            skLineSegment(sketch, "E413.3.2.75", {"start": v(129.75, 4.7) * mm, "end": v(129.75, 2.75) * mm});
            skLineSegment(sketch, "E413.3.2.76", {"start": v(254.3, -13.25) * mm, "end": v(254.3, -15.25) * mm});
            skLineSegment(sketch, "E413.3.2.77", {"start": v(129.75, 0.7) * mm, "end": v(129.75, -1.3) * mm});
            skLineSegment(sketch, "E413.3.2.78", {"start": v(129.75, -19.3) * mm, "end": v(129.75, -21) * mm});
            skLineSegment(sketch, "E413.3.2.79", {"start": v(254.3, 2.75) * mm, "end": v(254.3, 0.7) * mm});
            skLineSegment(sketch, "E413.3.2.80", {"start": v(129.75, -11.3) * mm, "end": v(129.75, -13.25) * mm});
            skLineSegment(sketch, "E413.3.2.81", {"start": v(254.3, -1.25) * mm, "end": v(254.3, -3.3) * mm});
            skLineSegment(sketch, "E413.3.2.82", {"start": v(242.4, 20.75) * mm, "end": v(244.4, 18.75) * mm});
            skLineSegment(sketch, "E413.3.2.83", {"start": v(129.75, -3.3) * mm, "end": v(129.75, -5.25) * mm});
            skLineSegment(sketch, "E413.3.2.84", {"start": v(254.3, 6.75) * mm, "end": v(254.3, 4.7) * mm});
            skLineSegment(sketch, "E413.3.2.85", {"start": v(129.75, -15.3) * mm, "end": v(129.75, -17.25) * mm});
            skLineSegment(sketch, "E413.3.2.86", {"start": v(129.7, -7.25) * mm, "end": v(129.7, -9.25) * mm});
            skLineSegment(sketch, "E413.3.2.87", {"start": v(129.7, 8.7) * mm, "end": v(129.7, 6.7) * mm});
            skLineSegment(sketch, "E413.3.2.88", {"start": v(141.6, 20.75) * mm, "end": v(139.6, 18.75) * mm});
            skLineSegment(sketch, "E413.3.2.89", {"start": v(254.3, -9.25) * mm, "end": v(254.3, -11.3) * mm});
            skLineSegment(sketch, "E413.3.2.90", {"start": v(129.7, -13.25) * mm, "end": v(129.7, -13.3) * mm});
            skLineSegment(sketch, "E413.3.2.91", {"start": v(129.7, 2.75) * mm, "end": v(129.7, 2.7) * mm});
            skLineSegment(sketch, "E413.3.2.92", {"start": v(129.75, -7.3) * mm, "end": v(129.75, -9.25) * mm});
            skLineSegment(sketch, "E413.3.2.93", {"start": v(129.7, -9.25) * mm, "end": v(129.7, -9.3) * mm});
            skLineSegment(sketch, "E413.3.2.94", {"start": v(254.3, 8.92) * mm, "end": v(254.3, 8.7) * mm});
            skLineSegment(sketch, "E413.3.2.95", {"start": v(129.7, 8.75) * mm, "end": v(129.75, 8.75) * mm});
            skLineSegment(sketch, "E413.3.2.96", {"start": v(254.3, -15.3) * mm, "end": v(254.25, -15.3) * mm});
            skLineSegment(sketch, "E413.3.2.97", {"start": v(254.25, 8.9) * mm, "end": v(254.25, 8.75) * mm});
            skLineSegment(sketch, "E413.3.2.98", {"start": v(129.7, 8.7) * mm, "end": v(129.7, 8.75) * mm});
            skLineSegment(sketch, "E413.3.2.99", {"start": v(254.3, -15.25) * mm, "end": v(254.3, -15.3) * mm});
            skLineSegment(sketch, "E413.3.3.0", {"start": v(129.75, -79.3) * mm, "end": v(254.3, -79.3) * mm});
            skLineSegment(sketch, "E413.3.3.1", {"start": v(129.7, -93.3) * mm, "end": v(254.25, -93.3) * mm});
            skLineSegment(sketch, "E413.3.3.2", {"start": v(129.7, -81.3) * mm, "end": v(254.25, -81.3) * mm});
            skLineSegment(sketch, "E413.3.3.3", {"start": v(129.75, -95.3) * mm, "end": v(254.3, -95.3) * mm});
            skLineSegment(sketch, "E413.3.3.4", {"start": v(129.7, -97.3) * mm, "end": v(254.25, -97.3) * mm});
            skLineSegment(sketch, "E413.3.3.5", {"start": v(131.48, -77.3) * mm, "end": v(252.45, -77.3) * mm});
            skLineSegment(sketch, "E413.3.3.6", {"start": v(129.75, -83.3) * mm, "end": v(254.3, -83.3) * mm});
            skLineSegment(sketch, "E413.3.3.7", {"start": v(139.48, -69.3) * mm, "end": v(244.45, -69.3) * mm});
            skLineSegment(sketch, "E413.3.3.8", {"start": v(129.75, -103.3) * mm, "end": v(254.25, -103.3) * mm});
            skLineSegment(sketch, "E413.3.3.9", {"start": v(133.55, -75.3) * mm, "end": v(250.52, -75.3) * mm});
            skLineSegment(sketch, "E413.3.3.10", {"start": v(137.55, -71.3) * mm, "end": v(246.52, -71.3) * mm});
            skLineSegment(sketch, "E413.3.3.11", {"start": v(129.75, -99.3) * mm, "end": v(254.3, -99.3) * mm});
            skLineSegment(sketch, "E413.3.3.12", {"start": v(129.7, -101.3) * mm, "end": v(254.25, -101.3) * mm});
            skLineSegment(sketch, "E413.3.3.13", {"start": v(129.7, -85.3) * mm, "end": v(254.25, -85.3) * mm});
            skLineSegment(sketch, "E413.3.3.14", {"start": v(129.75, -87.3) * mm, "end": v(254.3, -87.3) * mm});
            skLineSegment(sketch, "E413.3.3.15", {"start": v(129.7, -89.3) * mm, "end": v(254.25, -89.3) * mm});
            skLineSegment(sketch, "E413.3.3.16", {"start": v(129.7, -105.3) * mm, "end": v(254.25, -105.3) * mm});
            skLineSegment(sketch, "E413.3.3.17", {"start": v(135.48, -73.3) * mm, "end": v(248.45, -73.3) * mm});
            skLineSegment(sketch, "E413.3.3.18", {"start": v(129.75, -107.3) * mm, "end": v(254.3, -107.3) * mm});
            skLineSegment(sketch, "E413.3.3.19", {"start": v(129.75, -91.3) * mm, "end": v(254.3, -91.3) * mm});
            skLineSegment(sketch, "E413.3.3.20", {"start": v(141.6, -67.25) * mm, "end": v(242.4, -67.25) * mm});
            skLineSegment(sketch, "E413.3.3.21", {"start": v(129.75, -93.25) * mm, "end": v(254.3, -93.25) * mm});
            skLineSegment(sketch, "E413.3.3.22", {"start": v(129.7, -95.25) * mm, "end": v(254.25, -95.25) * mm});
            skLineSegment(sketch, "E413.3.3.23", {"start": v(129.75, -97.25) * mm, "end": v(254.3, -97.25) * mm});
            skLineSegment(sketch, "E413.3.3.24", {"start": v(129.75, -79.25) * mm, "end": v(254.25, -79.25) * mm});
            skLineSegment(sketch, "E413.3.3.25", {"start": v(129.75, -81.25) * mm, "end": v(254.3, -81.25) * mm});
            skLineSegment(sketch, "E413.3.3.26", {"start": v(129.7, -83.25) * mm, "end": v(254.25, -83.25) * mm});
            skLineSegment(sketch, "E413.3.3.27", {"start": v(129.7, -103.25) * mm, "end": v(254.25, -103.25) * mm});
            skLineSegment(sketch, "E413.3.3.28", {"start": v(129.7, -87.25) * mm, "end": v(254.25, -87.25) * mm});
            skLineSegment(sketch, "E413.3.3.29", {"start": v(135.6, -73.25) * mm, "end": v(248.47, -73.25) * mm});
            skLineSegment(sketch, "E413.3.3.30", {"start": v(129.75, -89.25) * mm, "end": v(254.3, -89.25) * mm});
            skLineSegment(sketch, "E413.3.3.31", {"start": v(129.7, -107.25) * mm, "end": v(254.25, -107.25) * mm});
            skLineSegment(sketch, "E413.3.3.32", {"start": v(131.6, -77.25) * mm, "end": v(252.47, -77.25) * mm});
            skLineSegment(sketch, "E413.3.3.33", {"start": v(129.7, -99.25) * mm, "end": v(254.25, -99.25) * mm});
            skLineSegment(sketch, "E413.3.3.34", {"start": v(129.75, -85.25) * mm, "end": v(254.3, -85.25) * mm});
            skLineSegment(sketch, "E413.3.3.35", {"start": v(129.75, -101.25) * mm, "end": v(254.3, -101.25) * mm});
            skLineSegment(sketch, "E413.3.3.36", {"start": v(139.6, -69.25) * mm, "end": v(244.4, -69.25) * mm});
            skLineSegment(sketch, "E413.3.3.37", {"start": v(129.75, -105.25) * mm, "end": v(254.3, -105.25) * mm});
            skLineSegment(sketch, "E413.3.3.38", {"start": v(137.53, -71.25) * mm, "end": v(246.4, -71.25) * mm});
            skLineSegment(sketch, "E413.3.3.39", {"start": v(141.58, -67.2) * mm, "end": v(242.42, -67.2) * mm});
            skLineSegment(sketch, "E413.3.3.40", {"start": v(254.5, -79) * mm, "end": v(254.5, -109) * mm});
            skLineSegment(sketch, "E413.3.3.41", {"start": v(133.53, -75.25) * mm, "end": v(250.4, -75.25) * mm});
            skLineSegment(sketch, "E413.3.3.42", {"start": v(129.7, -91.25) * mm, "end": v(254.25, -91.25) * mm});
            skLineSegment(sketch, "E413.3.3.43", {"start": v(248.47, -73.25) * mm, "end": v(250.52, -75.3) * mm});
            skLineSegment(sketch, "E413.3.3.44", {"start": v(248.45, -73.3) * mm, "end": v(250.4, -75.25) * mm});
            skLineSegment(sketch, "E413.3.3.45", {"start": v(137.53, -71.25) * mm, "end": v(135.48, -73.3) * mm});
            skLineSegment(sketch, "E413.3.3.46", {"start": v(141.5, -67) * mm, "end": v(129.5, -79) * mm});
            skLineSegment(sketch, "E413.3.3.47", {"start": v(141.5, -67) * mm, "end": v(242.5, -67) * mm});
            skLineSegment(sketch, "E413.3.3.48", {"start": v(242.5, -67) * mm, "end": v(254.5, -79) * mm});
            skLineSegment(sketch, "E413.3.3.49", {"start": v(137.55, -71.3) * mm, "end": v(135.6, -73.25) * mm});
            skLineSegment(sketch, "E413.3.3.50", {"start": v(129.7, -83.25) * mm, "end": v(129.7, -85.25) * mm});
            skLineSegment(sketch, "E413.3.3.51", {"start": v(133.53, -75.25) * mm, "end": v(131.48, -77.3) * mm});
            skLineSegment(sketch, "E413.3.3.52", {"start": v(244.45, -69.3) * mm, "end": v(246.4, -71.25) * mm});
            skLineSegment(sketch, "E413.3.3.53", {"start": v(129.7, -87.25) * mm, "end": v(129.7, -89.3) * mm});
            skLineSegment(sketch, "E413.3.3.54", {"start": v(252.47, -77.25) * mm, "end": v(254.3, -79.08) * mm});
            skLineSegment(sketch, "E413.3.3.55", {"start": v(254.3, -105.25) * mm, "end": v(254.3, -107.3) * mm});
            skLineSegment(sketch, "E413.3.3.56", {"start": v(254.25, -101.3) * mm, "end": v(254.25, -103.25) * mm});
            skLineSegment(sketch, "E413.3.3.57", {"start": v(252.45, -77.3) * mm, "end": v(254.25, -79.1) * mm});
            skLineSegment(sketch, "E413.3.3.58", {"start": v(133.55, -75.3) * mm, "end": v(131.6, -77.25) * mm});
            skLineSegment(sketch, "E413.3.3.59", {"start": v(254.25, -81.3) * mm, "end": v(254.25, -83.25) * mm});
            skLineSegment(sketch, "E413.3.3.60", {"start": v(129.7, -107.25) * mm, "end": v(129.7, -109) * mm});
            skLineSegment(sketch, "E413.3.3.61", {"start": v(129.7, -103.25) * mm, "end": v(129.7, -105.3) * mm});
            skLineSegment(sketch, "E413.3.3.62", {"start": v(254.25, -89.3) * mm, "end": v(254.25, -91.25) * mm});
            skLineSegment(sketch, "E413.3.3.63", {"start": v(141.58, -67.2) * mm, "end": v(139.48, -69.3) * mm});
            skLineSegment(sketch, "E413.3.3.64", {"start": v(242.42, -67.2) * mm, "end": v(246.52, -71.3) * mm});
            skLineSegment(sketch, "E413.3.3.65", {"start": v(254.25, -97.3) * mm, "end": v(254.25, -99.25) * mm});
            skLineSegment(sketch, "E413.3.3.66", {"start": v(129.7, -91.25) * mm, "end": v(129.7, -93.3) * mm});
            skLineSegment(sketch, "E413.3.3.67", {"start": v(254.25, -85.3) * mm, "end": v(254.25, -87.25) * mm});
            skLineSegment(sketch, "E413.3.3.68", {"start": v(254.25, -93.3) * mm, "end": v(254.25, -95.25) * mm});
            skLineSegment(sketch, "E413.3.3.69", {"start": v(129.7, -99.25) * mm, "end": v(129.7, -101.25) * mm});
            skLineSegment(sketch, "E413.3.3.70", {"start": v(254.3, -93.25) * mm, "end": v(254.3, -95.3) * mm});
            skLineSegment(sketch, "E413.3.3.71", {"start": v(129.7, -109) * mm, "end": v(129.75, -109) * mm});
            skLineSegment(sketch, "E413.3.3.72", {"start": v(129.5, -79) * mm, "end": v(129.5, -109) * mm});
            skLineSegment(sketch, "E413.3.3.73", {"start": v(129.75, -79.3) * mm, "end": v(129.75, -81.25) * mm});
            skLineSegment(sketch, "E413.3.3.74", {"start": v(254.25, -105.3) * mm, "end": v(254.25, -107.25) * mm});
            skLineSegment(sketch, "E413.3.3.75", {"start": v(129.75, -83.3) * mm, "end": v(129.75, -85.25) * mm});
            skLineSegment(sketch, "E413.3.3.76", {"start": v(254.3, -101.25) * mm, "end": v(254.3, -103.25) * mm});
            skLineSegment(sketch, "E413.3.3.77", {"start": v(129.75, -87.3) * mm, "end": v(129.75, -89.3) * mm});
            skLineSegment(sketch, "E413.3.3.78", {"start": v(129.75, -107.3) * mm, "end": v(129.75, -109) * mm});
            skLineSegment(sketch, "E413.3.3.79", {"start": v(254.3, -85.25) * mm, "end": v(254.3, -87.3) * mm});
            skLineSegment(sketch, "E413.3.3.80", {"start": v(129.75, -99.3) * mm, "end": v(129.75, -101.25) * mm});
            skLineSegment(sketch, "E413.3.3.81", {"start": v(254.3, -89.25) * mm, "end": v(254.3, -91.3) * mm});
            skLineSegment(sketch, "E413.3.3.82", {"start": v(242.4, -67.25) * mm, "end": v(244.4, -69.25) * mm});
            skLineSegment(sketch, "E413.3.3.83", {"start": v(129.75, -91.3) * mm, "end": v(129.75, -93.25) * mm});
            skLineSegment(sketch, "E413.3.3.84", {"start": v(254.3, -81.25) * mm, "end": v(254.3, -83.3) * mm});
            skLineSegment(sketch, "E413.3.3.85", {"start": v(129.75, -103.3) * mm, "end": v(129.75, -105.25) * mm});
            skLineSegment(sketch, "E413.3.3.86", {"start": v(129.7, -95.25) * mm, "end": v(129.7, -97.25) * mm});
            skLineSegment(sketch, "E413.3.3.87", {"start": v(129.7, -79.3) * mm, "end": v(129.7, -81.3) * mm});
            skLineSegment(sketch, "E413.3.3.88", {"start": v(141.6, -67.25) * mm, "end": v(139.6, -69.25) * mm});
            skLineSegment(sketch, "E413.3.3.89", {"start": v(254.3, -97.25) * mm, "end": v(254.3, -99.3) * mm});
            skLineSegment(sketch, "E413.3.3.90", {"start": v(129.7, -101.25) * mm, "end": v(129.7, -101.3) * mm});
            skLineSegment(sketch, "E413.3.3.91", {"start": v(129.7, -85.25) * mm, "end": v(129.7, -85.3) * mm});
            skLineSegment(sketch, "E413.3.3.92", {"start": v(129.75, -95.3) * mm, "end": v(129.75, -97.25) * mm});
            skLineSegment(sketch, "E413.3.3.93", {"start": v(129.7, -97.25) * mm, "end": v(129.7, -97.3) * mm});
            skLineSegment(sketch, "E413.3.3.94", {"start": v(254.3, -79.08) * mm, "end": v(254.3, -79.3) * mm});
            skLineSegment(sketch, "E413.3.3.95", {"start": v(129.7, -79.25) * mm, "end": v(129.75, -79.25) * mm});
            skLineSegment(sketch, "E413.3.3.96", {"start": v(254.3, -103.3) * mm, "end": v(254.25, -103.3) * mm});
            skLineSegment(sketch, "E413.3.3.97", {"start": v(254.25, -79.1) * mm, "end": v(254.25, -79.25) * mm});
            skLineSegment(sketch, "E413.3.3.98", {"start": v(129.7, -79.3) * mm, "end": v(129.7, -79.25) * mm});
            skLineSegment(sketch, "E413.3.3.99", {"start": v(254.3, -103.25) * mm, "end": v(254.3, -103.3) * mm});
            skLineSegment(sketch, "E413.3.4.0", {"start": v(129.75, -167.3) * mm, "end": v(254.3, -167.3) * mm});
            skLineSegment(sketch, "E413.3.4.1", {"start": v(129.7, -181.3) * mm, "end": v(254.25, -181.3) * mm});
            skLineSegment(sketch, "E413.3.4.2", {"start": v(129.7, -169.3) * mm, "end": v(254.25, -169.3) * mm});
            skLineSegment(sketch, "E413.3.4.3", {"start": v(129.75, -183.3) * mm, "end": v(254.3, -183.3) * mm});
            skLineSegment(sketch, "E413.3.4.4", {"start": v(129.7, -185.3) * mm, "end": v(254.25, -185.3) * mm});
            skLineSegment(sketch, "E413.3.4.5", {"start": v(131.48, -165.3) * mm, "end": v(252.44, -165.3) * mm});
            skLineSegment(sketch, "E413.3.4.6", {"start": v(129.75, -171.3) * mm, "end": v(254.3, -171.3) * mm});
            skLineSegment(sketch, "E413.3.4.7", {"start": v(139.48, -157.3) * mm, "end": v(244.44, -157.3) * mm});
            skLineSegment(sketch, "E413.3.4.8", {"start": v(129.75, -191.3) * mm, "end": v(254.25, -191.3) * mm});
            skLineSegment(sketch, "E413.3.4.9", {"start": v(133.55, -163.3) * mm, "end": v(250.52, -163.3) * mm});
            skLineSegment(sketch, "E413.3.4.10", {"start": v(137.55, -159.3) * mm, "end": v(246.52, -159.3) * mm});
            skLineSegment(sketch, "E413.3.4.11", {"start": v(129.75, -187.3) * mm, "end": v(254.3, -187.3) * mm});
            skLineSegment(sketch, "E413.3.4.12", {"start": v(129.7, -189.3) * mm, "end": v(254.25, -189.3) * mm});
            skLineSegment(sketch, "E413.3.4.13", {"start": v(129.7, -173.3) * mm, "end": v(254.25, -173.3) * mm});
            skLineSegment(sketch, "E413.3.4.14", {"start": v(129.75, -175.3) * mm, "end": v(254.3, -175.3) * mm});
            skLineSegment(sketch, "E413.3.4.15", {"start": v(129.7, -177.3) * mm, "end": v(254.25, -177.3) * mm});
            skLineSegment(sketch, "E413.3.4.16", {"start": v(129.7, -193.3) * mm, "end": v(254.25, -193.3) * mm});
            skLineSegment(sketch, "E413.3.4.17", {"start": v(135.48, -161.3) * mm, "end": v(248.44, -161.3) * mm});
            skLineSegment(sketch, "E413.3.4.18", {"start": v(129.75, -195.3) * mm, "end": v(254.3, -195.3) * mm});
            skLineSegment(sketch, "E413.3.4.19", {"start": v(129.75, -179.3) * mm, "end": v(254.3, -179.3) * mm});
            skLineSegment(sketch, "E413.3.4.20", {"start": v(141.6, -155.25) * mm, "end": v(242.4, -155.25) * mm});
            skLineSegment(sketch, "E413.3.4.21", {"start": v(129.75, -181.25) * mm, "end": v(254.3, -181.25) * mm});
            skLineSegment(sketch, "E413.3.4.22", {"start": v(129.7, -183.25) * mm, "end": v(254.25, -183.25) * mm});
            skLineSegment(sketch, "E413.3.4.23", {"start": v(129.75, -185.25) * mm, "end": v(254.3, -185.25) * mm});
            skLineSegment(sketch, "E413.3.4.24", {"start": v(129.75, -167.25) * mm, "end": v(254.25, -167.25) * mm});
            skLineSegment(sketch, "E413.3.4.25", {"start": v(129.75, -169.25) * mm, "end": v(254.3, -169.25) * mm});
            skLineSegment(sketch, "E413.3.4.26", {"start": v(129.7, -171.25) * mm, "end": v(254.25, -171.25) * mm});
            skLineSegment(sketch, "E413.3.4.27", {"start": v(129.7, -191.25) * mm, "end": v(254.25, -191.25) * mm});
            skLineSegment(sketch, "E413.3.4.28", {"start": v(129.7, -175.25) * mm, "end": v(254.25, -175.25) * mm});
            skLineSegment(sketch, "E413.3.4.29", {"start": v(135.6, -161.25) * mm, "end": v(248.47, -161.25) * mm});
            skLineSegment(sketch, "E413.3.4.30", {"start": v(129.75, -177.25) * mm, "end": v(254.3, -177.25) * mm});
            skLineSegment(sketch, "E413.3.4.31", {"start": v(129.7, -195.25) * mm, "end": v(254.25, -195.25) * mm});
            skLineSegment(sketch, "E413.3.4.32", {"start": v(131.6, -165.25) * mm, "end": v(252.47, -165.25) * mm});
            skLineSegment(sketch, "E413.3.4.33", {"start": v(129.7, -187.25) * mm, "end": v(254.25, -187.25) * mm});
            skLineSegment(sketch, "E413.3.4.34", {"start": v(129.75, -173.25) * mm, "end": v(254.3, -173.25) * mm});
            skLineSegment(sketch, "E413.3.4.35", {"start": v(129.75, -189.25) * mm, "end": v(254.3, -189.25) * mm});
            skLineSegment(sketch, "E413.3.4.36", {"start": v(139.6, -157.25) * mm, "end": v(244.4, -157.25) * mm});
            skLineSegment(sketch, "E413.3.4.37", {"start": v(129.75, -193.25) * mm, "end": v(254.3, -193.25) * mm});
            skLineSegment(sketch, "E413.3.4.38", {"start": v(137.53, -159.25) * mm, "end": v(246.4, -159.25) * mm});
            skLineSegment(sketch, "E413.3.4.39", {"start": v(141.58, -155.2) * mm, "end": v(242.42, -155.2) * mm});
            skLineSegment(sketch, "E413.3.4.40", {"start": v(254.5, -167) * mm, "end": v(254.5, -197) * mm});
            skLineSegment(sketch, "E413.3.4.41", {"start": v(133.53, -163.25) * mm, "end": v(250.4, -163.25) * mm});
            skLineSegment(sketch, "E413.3.4.42", {"start": v(129.7, -179.25) * mm, "end": v(254.25, -179.25) * mm});
            skLineSegment(sketch, "E413.3.4.43", {"start": v(248.47, -161.25) * mm, "end": v(250.52, -163.3) * mm});
            skLineSegment(sketch, "E413.3.4.44", {"start": v(248.44, -161.3) * mm, "end": v(250.4, -163.25) * mm});
            skLineSegment(sketch, "E413.3.4.45", {"start": v(137.53, -159.25) * mm, "end": v(135.48, -161.3) * mm});
            skLineSegment(sketch, "E413.3.4.46", {"start": v(141.5, -155) * mm, "end": v(129.5, -167) * mm});
            skLineSegment(sketch, "E413.3.4.47", {"start": v(141.5, -155) * mm, "end": v(242.5, -155) * mm});
            skLineSegment(sketch, "E413.3.4.48", {"start": v(242.5, -155) * mm, "end": v(254.5, -167) * mm});
            skLineSegment(sketch, "E413.3.4.49", {"start": v(137.55, -159.3) * mm, "end": v(135.6, -161.25) * mm});
            skLineSegment(sketch, "E413.3.4.50", {"start": v(129.7, -171.25) * mm, "end": v(129.7, -173.25) * mm});
            skLineSegment(sketch, "E413.3.4.51", {"start": v(133.53, -163.25) * mm, "end": v(131.48, -165.3) * mm});
            skLineSegment(sketch, "E413.3.4.52", {"start": v(244.44, -157.3) * mm, "end": v(246.4, -159.25) * mm});
            skLineSegment(sketch, "E413.3.4.53", {"start": v(129.7, -175.25) * mm, "end": v(129.7, -177.3) * mm});
            skLineSegment(sketch, "E413.3.4.54", {"start": v(252.47, -165.25) * mm, "end": v(254.3, -167.08) * mm});
            skLineSegment(sketch, "E413.3.4.55", {"start": v(254.3, -193.25) * mm, "end": v(254.3, -195.3) * mm});
            skLineSegment(sketch, "E413.3.4.56", {"start": v(254.25, -189.3) * mm, "end": v(254.25, -191.25) * mm});
            skLineSegment(sketch, "E413.3.4.57", {"start": v(252.44, -165.3) * mm, "end": v(254.25, -167.1) * mm});
            skLineSegment(sketch, "E413.3.4.58", {"start": v(133.55, -163.3) * mm, "end": v(131.6, -165.25) * mm});
            skLineSegment(sketch, "E413.3.4.59", {"start": v(254.25, -169.3) * mm, "end": v(254.25, -171.25) * mm});
            skLineSegment(sketch, "E413.3.4.60", {"start": v(129.7, -195.25) * mm, "end": v(129.7, -197) * mm});
            skLineSegment(sketch, "E413.3.4.61", {"start": v(129.7, -191.25) * mm, "end": v(129.7, -193.3) * mm});
            skLineSegment(sketch, "E413.3.4.62", {"start": v(254.25, -177.3) * mm, "end": v(254.25, -179.25) * mm});
            skLineSegment(sketch, "E413.3.4.63", {"start": v(141.58, -155.2) * mm, "end": v(139.48, -157.3) * mm});
            skLineSegment(sketch, "E413.3.4.64", {"start": v(242.42, -155.2) * mm, "end": v(246.52, -159.3) * mm});
            skLineSegment(sketch, "E413.3.4.65", {"start": v(254.25, -185.3) * mm, "end": v(254.25, -187.25) * mm});
            skLineSegment(sketch, "E413.3.4.66", {"start": v(129.7, -179.25) * mm, "end": v(129.7, -181.3) * mm});
            skLineSegment(sketch, "E413.3.4.67", {"start": v(254.25, -173.3) * mm, "end": v(254.25, -175.25) * mm});
            skLineSegment(sketch, "E413.3.4.68", {"start": v(254.25, -181.3) * mm, "end": v(254.25, -183.25) * mm});
            skLineSegment(sketch, "E413.3.4.69", {"start": v(129.7, -187.25) * mm, "end": v(129.7, -189.25) * mm});
            skLineSegment(sketch, "E413.3.4.70", {"start": v(254.3, -181.25) * mm, "end": v(254.3, -183.3) * mm});
            skLineSegment(sketch, "E413.3.4.71", {"start": v(129.7, -197) * mm, "end": v(129.75, -197) * mm});
            skLineSegment(sketch, "E413.3.4.72", {"start": v(129.5, -167) * mm, "end": v(129.5, -197) * mm});
            skLineSegment(sketch, "E413.3.4.73", {"start": v(129.75, -167.3) * mm, "end": v(129.75, -169.25) * mm});
            skLineSegment(sketch, "E413.3.4.74", {"start": v(254.25, -193.3) * mm, "end": v(254.25, -195.25) * mm});
            skLineSegment(sketch, "E413.3.4.75", {"start": v(129.75, -171.3) * mm, "end": v(129.75, -173.25) * mm});
            skLineSegment(sketch, "E413.3.4.76", {"start": v(254.3, -189.25) * mm, "end": v(254.3, -191.25) * mm});
            skLineSegment(sketch, "E413.3.4.77", {"start": v(129.75, -175.3) * mm, "end": v(129.75, -177.3) * mm});
            skLineSegment(sketch, "E413.3.4.78", {"start": v(129.75, -195.3) * mm, "end": v(129.75, -197) * mm});
            skLineSegment(sketch, "E413.3.4.79", {"start": v(254.3, -173.25) * mm, "end": v(254.3, -175.3) * mm});
            skLineSegment(sketch, "E413.3.4.80", {"start": v(129.75, -187.3) * mm, "end": v(129.75, -189.25) * mm});
            skLineSegment(sketch, "E413.3.4.81", {"start": v(254.3, -177.25) * mm, "end": v(254.3, -179.3) * mm});
            skLineSegment(sketch, "E413.3.4.82", {"start": v(242.4, -155.25) * mm, "end": v(244.4, -157.25) * mm});
            skLineSegment(sketch, "E413.3.4.83", {"start": v(129.75, -179.3) * mm, "end": v(129.75, -181.25) * mm});
            skLineSegment(sketch, "E413.3.4.84", {"start": v(254.3, -169.25) * mm, "end": v(254.3, -171.3) * mm});
            skLineSegment(sketch, "E413.3.4.85", {"start": v(129.75, -191.3) * mm, "end": v(129.75, -193.25) * mm});
            skLineSegment(sketch, "E413.3.4.86", {"start": v(129.7, -183.25) * mm, "end": v(129.7, -185.25) * mm});
            skLineSegment(sketch, "E413.3.4.87", {"start": v(129.7, -167.3) * mm, "end": v(129.7, -169.3) * mm});
            skLineSegment(sketch, "E413.3.4.88", {"start": v(141.6, -155.25) * mm, "end": v(139.6, -157.25) * mm});
            skLineSegment(sketch, "E413.3.4.89", {"start": v(254.3, -185.25) * mm, "end": v(254.3, -187.3) * mm});
            skLineSegment(sketch, "E413.3.4.90", {"start": v(129.7, -189.25) * mm, "end": v(129.7, -189.3) * mm});
            skLineSegment(sketch, "E413.3.4.91", {"start": v(129.7, -173.25) * mm, "end": v(129.7, -173.3) * mm});
            skLineSegment(sketch, "E413.3.4.92", {"start": v(129.75, -183.3) * mm, "end": v(129.75, -185.25) * mm});
            skLineSegment(sketch, "E413.3.4.93", {"start": v(129.7, -185.25) * mm, "end": v(129.7, -185.3) * mm});
            skLineSegment(sketch, "E413.3.4.94", {"start": v(254.3, -167.08) * mm, "end": v(254.3, -167.3) * mm});
            skLineSegment(sketch, "E413.3.4.95", {"start": v(129.7, -167.25) * mm, "end": v(129.75, -167.25) * mm});
            skLineSegment(sketch, "E413.3.4.96", {"start": v(254.3, -191.3) * mm, "end": v(254.25, -191.3) * mm});
            skLineSegment(sketch, "E413.3.4.97", {"start": v(254.25, -167.1) * mm, "end": v(254.25, -167.25) * mm});
            skLineSegment(sketch, "E413.3.4.98", {"start": v(129.7, -167.3) * mm, "end": v(129.7, -167.25) * mm});
            skLineSegment(sketch, "E413.3.4.99", {"start": v(254.3, -191.25) * mm, "end": v(254.3, -191.3) * mm});
            skLineSegment(sketch, "E413.direction1", {"start": v(-256, 155) * mm, "end": v(-127.5, 155) * mm, "construction": true});
            skLineSegment(sketch, "E413.direction2", {"start": v(-256, 155) * mm, "end": v(-256, 67) * mm, "construction": true});
            skLineSegment(sketch, "E414.1.0.0", {"start": v(254.5, -111) * mm, "end": v(126, -111) * mm, "construction": true});
            skLineSegment(sketch, "E414.1.0.1", {"start": v(-143, 111) * mm, "end": v(-244, 111) * mm});
            skLineSegment(sketch, "E414.1.0.2", {"start": v(254.5, -111) * mm, "end": v(254.5, -23) * mm, "construction": true});
            skLineSegment(sketch, "E414.1.0.3", {"start": v(-2.75, -24.7) * mm, "end": v(-127.3, -24.7) * mm});
            skLineSegment(sketch, "E414.1.0.4", {"start": v(-2.7, 55.25) * mm, "end": v(-127.25, 55.25) * mm});
            skLineSegment(sketch, "E414.1.0.5", {"start": v(-14.6, 111.25) * mm, "end": v(-115.4, 111.25) * mm});
            skLineSegment(sketch, "E414.1.0.6", {"start": v(-4.6, -54.75) * mm, "end": v(-125.47, -54.75) * mm});
            skLineSegment(sketch, "E414.1.0.7", {"start": v(-2.7, -26.7) * mm, "end": v(-127.25, -26.7) * mm});
            skLineSegment(sketch, "E414.1.0.8", {"start": v(-6.53, -56.75) * mm, "end": v(-123.4, -56.75) * mm});
            skLineSegment(sketch, "E414.1.0.9", {"start": v(-2.75, -50.75) * mm, "end": v(-127.3, -50.75) * mm});
            skLineSegment(sketch, "E414.1.0.10", {"start": v(-4.48, 33.3) * mm, "end": v(-125.45, 33.3) * mm});
            skLineSegment(sketch, "E414.1.0.11", {"start": v(-131.25, -28.7) * mm, "end": v(-255.75, -28.7) * mm});
            skLineSegment(sketch, "E414.1.0.12", {"start": v(-131.25, -112.7) * mm, "end": v(-255.8, -112.7) * mm});
            skLineSegment(sketch, "E414.1.0.13", {"start": v(-131.25, -114.75) * mm, "end": v(-255.8, -114.75) * mm});
            skLineSegment(sketch, "E414.1.0.14", {"start": v(-131.2, -138.7) * mm, "end": v(-255.75, -138.7) * mm});
            skLineSegment(sketch, "E414.1.0.15", {"start": v(-132.98, -142.7) * mm, "end": v(-253.95, -142.7) * mm});
            skLineSegment(sketch, "E414.1.0.16", {"start": v(-131.25, -52.75) * mm, "end": v(-255.75, -52.75) * mm});
            skLineSegment(sketch, "E414.1.0.17", {"start": v(-131.2, -32.75) * mm, "end": v(-255.75, -32.75) * mm});
            skLineSegment(sketch, "E414.1.0.18", {"start": v(-131.25, 123.3) * mm, "end": v(-255.8, 123.3) * mm});
            skLineSegment(sketch, "E414.1.0.19", {"start": v(-137.1, 29.25) * mm, "end": v(-249.97, 29.25) * mm});
            skLineSegment(sketch, "E414.1.0.20", {"start": v(125.75, 63.3) * mm, "end": v(1.2, 63.3) * mm});
            skLineSegment(sketch, "E414.1.0.21", {"start": v(-2.7, -36.75) * mm, "end": v(-127.25, -36.75) * mm});
            skLineSegment(sketch, "E414.1.0.22", {"start": v(114, 111) * mm, "end": v(13, 111) * mm});
            skLineSegment(sketch, "E414.1.0.23", {"start": v(-8.6, -58.75) * mm, "end": v(-121.47, -58.75) * mm});
            skLineSegment(sketch, "E414.1.0.24", {"start": v(-2.75, -30.75) * mm, "end": v(-127.3, -30.75) * mm});
            skLineSegment(sketch, "E414.1.0.25", {"start": v(-6.55, 31.3) * mm, "end": v(-123.52, 31.3) * mm});
            skLineSegment(sketch, "E414.1.0.26", {"start": v(-2.7, 63.25) * mm, "end": v(-127.25, 63.25) * mm});
            skLineSegment(sketch, "E414.1.0.27", {"start": v(-4.48, 121.3) * mm, "end": v(-125.45, 121.3) * mm});
            skLineSegment(sketch, "E414.1.0.28", {"start": v(-2.7, 45.3) * mm, "end": v(-127.25, 45.3) * mm});
            skLineSegment(sketch, "E414.1.0.29", {"start": v(-2.75, 41.25) * mm, "end": v(-127.3, 41.25) * mm});
            skLineSegment(sketch, "E414.1.0.30", {"start": v(-2.75, 63.3) * mm, "end": v(-127.3, 63.3) * mm});
            skLineSegment(sketch, "E414.1.0.31", {"start": v(-2.7, 37.3) * mm, "end": v(-127.25, 37.3) * mm});
            skLineSegment(sketch, "E414.1.0.32", {"start": v(-2.75, 143.3) * mm, "end": v(-127.3, 143.3) * mm});
            skLineSegment(sketch, "E414.1.0.33", {"start": v(254.3, -118.7) * mm, "end": v(129.75, -118.7) * mm});
            skLineSegment(sketch, "E414.1.0.34", {"start": v(254.3, -134.7) * mm, "end": v(129.75, -134.7) * mm});
            skLineSegment(sketch, "E414.1.0.35", {"start": v(-6.55, -144.7) * mm, "end": v(-123.52, -144.7) * mm});
            skLineSegment(sketch, "E414.1.0.36", {"start": v(-131.25, 63.3) * mm, "end": v(-255.8, 63.3) * mm});
            skLineSegment(sketch, "E414.1.0.37", {"start": v(-14.5, 23) * mm, "end": v(-115.5, 23) * mm});
            skLineSegment(sketch, "E414.1.0.38", {"start": v(-2.75, 137.25) * mm, "end": v(-127.3, 137.25) * mm});
            skLineSegment(sketch, "E414.1.0.39", {"start": v(-131.2, 37.3) * mm, "end": v(-255.75, 37.3) * mm});
            skLineSegment(sketch, "E414.1.0.40", {"start": v(-10.55, -148.7) * mm, "end": v(-119.52, -148.7) * mm});
            skLineSegment(sketch, "E414.1.0.41", {"start": v(-2.7, 147.25) * mm, "end": v(-127.25, 147.25) * mm});
            skLineSegment(sketch, "E414.1.0.42", {"start": v(125.8, 51.25) * mm, "end": v(1.25, 51.25) * mm});
            skLineSegment(sketch, "E414.1.0.43", {"start": v(125.75, 151.3) * mm, "end": v(1.2, 151.3) * mm});
            skLineSegment(sketch, "E414.1.0.44", {"start": v(254.25, -116.7) * mm, "end": v(129.75, -116.7) * mm});
            skLineSegment(sketch, "E414.1.0.45", {"start": v(254.25, -132.7) * mm, "end": v(129.7, -132.7) * mm});
            skLineSegment(sketch, "E414.1.0.46", {"start": v(254.3, 139.25) * mm, "end": v(129.75, 139.25) * mm});
            skLineSegment(sketch, "E414.1.0.47", {"start": v(-131.25, 133.25) * mm, "end": v(-255.8, 133.25) * mm});
            skLineSegment(sketch, "E414.1.0.48", {"start": v(125.8, -130.7) * mm, "end": v(1.25, -130.7) * mm});
            skLineSegment(sketch, "E414.1.0.49", {"start": v(125.75, 53.25) * mm, "end": v(1.2, 53.25) * mm});
            skLineSegment(sketch, "E414.1.0.50", {"start": v(242.42, 111.2) * mm, "end": v(141.58, 111.2) * mm});
            skLineSegment(sketch, "E414.1.0.51", {"start": v(254.25, 141.25) * mm, "end": v(129.7, 141.25) * mm});
            skLineSegment(sketch, "E414.1.0.52", {"start": v(-2.7, -118.7) * mm, "end": v(-127.25, -118.7) * mm});
            skLineSegment(sketch, "E414.1.0.53", {"start": v(254.3, -114.7) * mm, "end": v(129.75, -114.7) * mm});
            skLineSegment(sketch, "E414.1.0.54", {"start": v(254.3, -130.7) * mm, "end": v(129.75, -130.7) * mm});
            skLineSegment(sketch, "E414.1.0.55", {"start": v(125.75, 149.25) * mm, "end": v(1.2, 149.25) * mm});
            skLineSegment(sketch, "E414.1.0.56", {"start": v(242.4, -152.75) * mm, "end": v(141.6, -152.75) * mm});
            skLineSegment(sketch, "E414.1.0.57", {"start": v(248.52, -58.7) * mm, "end": v(135.55, -58.7) * mm});
            skLineSegment(sketch, "E414.1.0.58", {"start": v(-10.55, -60.7) * mm, "end": v(-119.52, -60.7) * mm});
            skLineSegment(sketch, "E414.1.0.59", {"start": v(120.02, -146.7) * mm, "end": v(7.05, -146.7) * mm});
            skLineSegment(sketch, "E414.1.0.60", {"start": v(254.25, -112.7) * mm, "end": v(129.7, -112.7) * mm});
            skLineSegment(sketch, "E414.1.0.61", {"start": v(254.25, -128.7) * mm, "end": v(129.7, -128.7) * mm});
            skLineSegment(sketch, "E414.1.0.62", {"start": v(250.45, -144.7) * mm, "end": v(133.48, -144.7) * mm});
            skLineSegment(sketch, "E414.1.0.63", {"start": v(254.25, -24.7) * mm, "end": v(129.7, -24.7) * mm});
            skLineSegment(sketch, "E414.1.0.64", {"start": v(254.25, -46.75) * mm, "end": v(129.7, -46.75) * mm});
            skLineSegment(sketch, "E414.1.0.65", {"start": v(125.8, 39.25) * mm, "end": v(1.25, 39.25) * mm});
            skLineSegment(sketch, "E414.1.0.66", {"start": v(117.95, 27.3) * mm, "end": v(8.98, 27.3) * mm});
            skLineSegment(sketch, "E414.1.0.67", {"start": v(125.8, 47.25) * mm, "end": v(1.25, 47.25) * mm});
            skLineSegment(sketch, "E414.1.0.68", {"start": v(125.8, 139.25) * mm, "end": v(1.25, 139.25) * mm});
            skLineSegment(sketch, "E414.1.0.69", {"start": v(254.3, 135.25) * mm, "end": v(129.75, 135.25) * mm});
            skLineSegment(sketch, "E414.1.0.70", {"start": v(254.3, 127.25) * mm, "end": v(129.75, 127.25) * mm});
            skLineSegment(sketch, "E414.1.0.71", {"start": v(125.75, -134.75) * mm, "end": v(1.2, -134.75) * mm});
            skLineSegment(sketch, "E414.1.0.72", {"start": v(125.75, -112.7) * mm, "end": v(1.2, -112.7) * mm});
            skLineSegment(sketch, "E414.1.0.73", {"start": v(-2.7, -40.75) * mm, "end": v(-127.25, -40.75) * mm});
            skLineSegment(sketch, "E414.1.0.74", {"start": v(-2.7, -48.75) * mm, "end": v(-127.25, -48.75) * mm});
            skLineSegment(sketch, "E414.1.0.75", {"start": v(246.45, -148.7) * mm, "end": v(137.48, -148.7) * mm});
            skLineSegment(sketch, "E414.1.0.76", {"start": v(254.25, -30.75) * mm, "end": v(129.7, -30.75) * mm});
            skLineSegment(sketch, "E414.1.0.77", {"start": v(254.25, -40.7) * mm, "end": v(129.7, -40.7) * mm});
            skLineSegment(sketch, "E414.1.0.78", {"start": v(254.3, 45.3) * mm, "end": v(129.75, 45.3) * mm});
            skLineSegment(sketch, "E414.1.0.79", {"start": v(254.25, 143.3) * mm, "end": v(129.7, 143.3) * mm});
            skLineSegment(sketch, "E414.1.0.80", {"start": v(-2.7, 125.3) * mm, "end": v(-127.25, 125.3) * mm});
            skLineSegment(sketch, "E414.1.0.81", {"start": v(113.92, 111.2) * mm, "end": v(13.08, 111.2) * mm});
            skLineSegment(sketch, "E414.1.0.82", {"start": v(-2.7, -130.7) * mm, "end": v(-127.25, -130.7) * mm});
            skLineSegment(sketch, "E414.1.0.83", {"start": v(125.75, 141.25) * mm, "end": v(1.2, 141.25) * mm});
            skLineSegment(sketch, "E414.1.0.84", {"start": v(116.02, 113.3) * mm, "end": v(11.05, 113.3) * mm});
            skLineSegment(sketch, "E414.1.0.85", {"start": v(125.75, -118.75) * mm, "end": v(1.2, -118.75) * mm});
            skLineSegment(sketch, "E414.1.0.86", {"start": v(125.75, -128.7) * mm, "end": v(1.2, -128.7) * mm});
            skLineSegment(sketch, "E414.1.0.87", {"start": v(125.75, 55.3) * mm, "end": v(1.2, 55.3) * mm});
            skLineSegment(sketch, "E414.1.0.88", {"start": v(252.52, -142.7) * mm, "end": v(131.55, -142.7) * mm});
            skLineSegment(sketch, "E414.1.0.89", {"start": v(254.3, -126.7) * mm, "end": v(129.75, -126.7) * mm});
            skLineSegment(sketch, "E414.1.0.90", {"start": v(254.3, 61.3) * mm, "end": v(129.75, 61.3) * mm});
            skLineSegment(sketch, "E414.1.0.91", {"start": v(252.4, 33.25) * mm, "end": v(131.53, 33.25) * mm});
            skLineSegment(sketch, "E414.1.0.92", {"start": v(254.3, 145.3) * mm, "end": v(129.75, 145.3) * mm});
            skLineSegment(sketch, "E414.1.0.93", {"start": v(-2.75, -140.7) * mm, "end": v(-127.3, -140.7) * mm});
            skLineSegment(sketch, "E414.1.0.94", {"start": v(123.9, -54.75) * mm, "end": v(3.03, -54.75) * mm});
            skLineSegment(sketch, "E414.1.0.95", {"start": v(125.8, -26.7) * mm, "end": v(1.25, -26.7) * mm});
            skLineSegment(sketch, "E414.1.0.96", {"start": v(125.75, -52.7) * mm, "end": v(1.2, -52.7) * mm});
            skLineSegment(sketch, "E414.1.0.97", {"start": v(-2.75, 129.25) * mm, "end": v(-127.3, 129.25) * mm});
            skLineSegment(sketch, "E414.1.0.98", {"start": v(125.8, 57.3) * mm, "end": v(1.25, 57.3) * mm});
            skLineSegment(sketch, "E414.1.0.99", {"start": v(125.75, 123.25) * mm, "end": v(1.25, 123.25) * mm});
            skLineSegment(sketch, "E414.1.0.100", {"start": v(254.25, -26.75) * mm, "end": v(129.7, -26.75) * mm});
            skLineSegment(sketch, "E414.1.0.101", {"start": v(254.25, -38.75) * mm, "end": v(129.7, -38.75) * mm});
            skLineSegment(sketch, "E414.1.0.102", {"start": v(252.52, -54.7) * mm, "end": v(131.55, -54.7) * mm});
            skLineSegment(sketch, "E414.1.0.103", {"start": v(248.52, 29.3) * mm, "end": v(135.55, 29.3) * mm});
            skLineSegment(sketch, "E414.1.0.104", {"start": v(248.4, 117.25) * mm, "end": v(135.53, 117.25) * mm});
            skLineSegment(sketch, "E414.1.0.105", {"start": v(254.3, 129.3) * mm, "end": v(129.75, 129.3) * mm});
            skLineSegment(sketch, "E414.1.0.106", {"start": v(-8.48, -146.7) * mm, "end": v(-121.45, -146.7) * mm});
            skLineSegment(sketch, "E414.1.0.107", {"start": v(124.02, -142.7) * mm, "end": v(3.05, -142.7) * mm});
            skLineSegment(sketch, "E414.1.0.108", {"start": v(125.75, -114.75) * mm, "end": v(1.2, -114.75) * mm});
            skLineSegment(sketch, "E414.1.0.109", {"start": v(125.75, -126.75) * mm, "end": v(1.2, -126.75) * mm});
            skLineSegment(sketch, "E414.1.0.110", {"start": v(120.02, -58.7) * mm, "end": v(7.05, -58.7) * mm});
            skLineSegment(sketch, "E414.1.0.111", {"start": v(119.9, 29.25) * mm, "end": v(7.03, 29.25) * mm});
            skLineSegment(sketch, "E414.1.0.112", {"start": v(125.8, 41.3) * mm, "end": v(1.25, 41.3) * mm});
            skLineSegment(sketch, "E414.1.0.113", {"start": v(125.75, 125.25) * mm, "end": v(1.2, 125.25) * mm});
            skLineSegment(sketch, "E414.1.0.114", {"start": v(121.95, 119.3) * mm, "end": v(4.98, 119.3) * mm});
            skLineSegment(sketch, "E414.1.0.115", {"start": v(254.25, -124.7) * mm, "end": v(129.7, -124.7) * mm});
            skLineSegment(sketch, "E414.1.0.116", {"start": v(246.47, -60.75) * mm, "end": v(137.6, -60.75) * mm});
            skLineSegment(sketch, "E414.1.0.117", {"start": v(254.3, -36.75) * mm, "end": v(129.75, -36.75) * mm});
            skLineSegment(sketch, "E414.1.0.118", {"start": v(254.25, -48.7) * mm, "end": v(129.7, -48.7) * mm});
            skLineSegment(sketch, "E414.1.0.119", {"start": v(254.25, 63.3) * mm, "end": v(129.7, 63.3) * mm});
            skLineSegment(sketch, "E414.1.0.120", {"start": v(254.3, 37.3) * mm, "end": v(129.75, 37.3) * mm});
            skLineSegment(sketch, "E414.1.0.121", {"start": v(254.25, 41.25) * mm, "end": v(129.7, 41.25) * mm});
            skLineSegment(sketch, "E414.1.0.122", {"start": v(254.25, 131.3) * mm, "end": v(129.7, 131.3) * mm});
            skLineSegment(sketch, "E414.1.0.123", {"start": v(-2.7, -138.7) * mm, "end": v(-127.25, -138.7) * mm});
            skLineSegment(sketch, "E414.1.0.124", {"start": v(125.8, 135.25) * mm, "end": v(1.25, 135.25) * mm});
            skLineSegment(sketch, "E414.1.0.125", {"start": v(-2.75, -112.7) * mm, "end": v(-127.3, -112.7) * mm});
            skLineSegment(sketch, "E414.1.0.126", {"start": v(254.25, -140.7) * mm, "end": v(129.7, -140.7) * mm});
            skLineSegment(sketch, "E414.1.0.127", {"start": v(125.75, -136.7) * mm, "end": v(1.2, -136.7) * mm});
            skLineSegment(sketch, "E414.1.0.128", {"start": v(117.97, -148.75) * mm, "end": v(9.1, -148.75) * mm});
            skLineSegment(sketch, "E414.1.0.129", {"start": v(125.8, -124.75) * mm, "end": v(1.25, -124.75) * mm});
            skLineSegment(sketch, "E414.1.0.130", {"start": v(125.75, -46.75) * mm, "end": v(1.2, -46.75) * mm});
            skLineSegment(sketch, "E414.1.0.131", {"start": v(125.75, -24.7) * mm, "end": v(1.2, -24.7) * mm});
            skLineSegment(sketch, "E414.1.0.132", {"start": v(125.8, -50.7) * mm, "end": v(1.25, -50.7) * mm});
            skLineSegment(sketch, "E414.1.0.133", {"start": v(125.75, 43.3) * mm, "end": v(1.2, 43.3) * mm});
            skLineSegment(sketch, "E414.1.0.134", {"start": v(125.8, 127.25) * mm, "end": v(1.25, 127.25) * mm});
            skLineSegment(sketch, "E414.1.0.135", {"start": v(117.95, 115.3) * mm, "end": v(8.98, 115.3) * mm});
            skLineSegment(sketch, "E414.1.0.136", {"start": v(242.42, -64.8) * mm, "end": v(141.58, -64.8) * mm});
            skLineSegment(sketch, "E414.1.0.137", {"start": v(254.25, -34.75) * mm, "end": v(129.7, -34.75) * mm});
            skLineSegment(sketch, "E414.1.0.138", {"start": v(244.52, -62.7) * mm, "end": v(139.55, -62.7) * mm});
            skLineSegment(sketch, "E414.1.0.139", {"start": v(254.25, 47.3) * mm, "end": v(129.7, 47.3) * mm});
            skLineSegment(sketch, "E414.1.0.140", {"start": v(254.25, 51.3) * mm, "end": v(129.7, 51.3) * mm});
            skLineSegment(sketch, "E414.1.0.141", {"start": v(254.25, 57.25) * mm, "end": v(129.7, 57.25) * mm});
            skLineSegment(sketch, "E414.1.0.142", {"start": v(242.5, 111) * mm, "end": v(141.5, 111) * mm});
            skLineSegment(sketch, "E414.1.0.143", {"start": v(254.3, 151.25) * mm, "end": v(129.75, 151.25) * mm});
            skLineSegment(sketch, "E414.1.0.144", {"start": v(254.3, 133.3) * mm, "end": v(129.75, 133.3) * mm});
            skLineSegment(sketch, "E414.1.0.145", {"start": v(116.02, -150.7) * mm, "end": v(11.05, -150.7) * mm});
            skLineSegment(sketch, "E414.1.0.146", {"start": v(-2.75, -124.7) * mm, "end": v(-127.3, -124.7) * mm});
            skLineSegment(sketch, "E414.1.0.147", {"start": v(-2.75, -128.7) * mm, "end": v(-127.3, -128.7) * mm});
            skLineSegment(sketch, "E414.1.0.148", {"start": v(113.92, -152.8) * mm, "end": v(13.08, -152.8) * mm});
            skLineSegment(sketch, "E414.1.0.149", {"start": v(125.75, -122.75) * mm, "end": v(1.2, -122.75) * mm});
            skLineSegment(sketch, "E414.1.0.150", {"start": v(125.75, -30.75) * mm, "end": v(1.2, -30.75) * mm});
            skLineSegment(sketch, "E414.1.0.151", {"start": v(125.75, -40.7) * mm, "end": v(1.2, -40.7) * mm});
            skLineSegment(sketch, "E414.1.0.152", {"start": v(125.75, -36.7) * mm, "end": v(1.2, -36.7) * mm});
            skLineSegment(sketch, "E414.1.0.153", {"start": v(114, 23) * mm, "end": v(13, 23) * mm});
            skLineSegment(sketch, "E414.1.0.154", {"start": v(125.8, 45.3) * mm, "end": v(1.25, 45.3) * mm});
            skLineSegment(sketch, "E414.1.0.155", {"start": v(125.8, 147.25) * mm, "end": v(1.25, 147.25) * mm});
            skLineSegment(sketch, "E414.1.0.156", {"start": v(125.75, 143.3) * mm, "end": v(1.2, 143.3) * mm});
            skLineSegment(sketch, "E414.1.0.157", {"start": v(242.4, 23.25) * mm, "end": v(141.6, 23.25) * mm});
            skLineSegment(sketch, "E414.1.0.158", {"start": v(254.3, 53.3) * mm, "end": v(129.75, 53.3) * mm});
            skLineSegment(sketch, "E414.1.0.159", {"start": v(244.4, 25.25) * mm, "end": v(139.6, 25.25) * mm});
            skLineSegment(sketch, "E414.1.0.160", {"start": v(252.4, 121.25) * mm, "end": v(131.53, 121.25) * mm});
            skLineSegment(sketch, "E414.1.0.161", {"start": v(254.3, 149.3) * mm, "end": v(129.75, 149.3) * mm});
            skLineSegment(sketch, "E414.1.0.162", {"start": v(254.25, 123.3) * mm, "end": v(129.7, 123.3) * mm});
            skLineSegment(sketch, "E414.1.0.163", {"start": v(125.75, -116.7) * mm, "end": v(1.25, -116.7) * mm});
            skLineSegment(sketch, "E414.1.0.164", {"start": v(125.75, -140.75) * mm, "end": v(1.25, -140.75) * mm});
            skLineSegment(sketch, "E414.1.0.165", {"start": v(-2.7, -122.7) * mm, "end": v(-127.25, -122.7) * mm});
            skLineSegment(sketch, "E414.1.0.166", {"start": v(-14.6, -152.75) * mm, "end": v(-115.4, -152.75) * mm});
            skLineSegment(sketch, "E414.1.0.167", {"start": v(254.3, -138.7) * mm, "end": v(129.75, -138.7) * mm});
            skLineSegment(sketch, "E414.1.0.168", {"start": v(254.3, -122.7) * mm, "end": v(129.75, -122.7) * mm});
            skLineSegment(sketch, "E414.1.0.169", {"start": v(254.25, -52.75) * mm, "end": v(129.75, -52.75) * mm});
            skLineSegment(sketch, "E414.1.0.170", {"start": v(254.25, -28.7) * mm, "end": v(129.75, -28.7) * mm});
            skLineSegment(sketch, "E414.1.0.171", {"start": v(115.9, -62.75) * mm, "end": v(11.1, -62.75) * mm});
            skLineSegment(sketch, "E414.1.0.172", {"start": v(113.9, -64.75) * mm, "end": v(13.1, -64.75) * mm});
            skLineSegment(sketch, "E414.1.0.173", {"start": v(125.8, -34.7) * mm, "end": v(1.25, -34.7) * mm});
            skLineSegment(sketch, "E414.1.0.174", {"start": v(125.75, 35.3) * mm, "end": v(1.2, 35.3) * mm});
            skLineSegment(sketch, "E414.1.0.175", {"start": v(123.9, 33.25) * mm, "end": v(3.03, 33.25) * mm});
            skLineSegment(sketch, "E414.1.0.176", {"start": v(125.8, 61.3) * mm, "end": v(1.25, 61.3) * mm});
            skLineSegment(sketch, "E414.1.0.177", {"start": v(125.8, 131.25) * mm, "end": v(1.25, 131.25) * mm});
            skLineSegment(sketch, "E414.1.0.178", {"start": v(125.8, 145.3) * mm, "end": v(1.25, 145.3) * mm});
            skLineSegment(sketch, "E414.1.0.179", {"start": v(-137.1, -146.75) * mm, "end": v(-249.97, -146.75) * mm});
            skLineSegment(sketch, "E414.1.0.180", {"start": v(-131.25, -118.75) * mm, "end": v(-255.8, -118.75) * mm});
            skLineSegment(sketch, "E414.1.0.181", {"start": v(-131.25, -128.7) * mm, "end": v(-255.8, -128.7) * mm});
            skLineSegment(sketch, "E414.1.0.182", {"start": v(-139.03, -148.75) * mm, "end": v(-247.9, -148.75) * mm});
            skLineSegment(sketch, "E414.1.0.183", {"start": v(-131.2, -124.75) * mm, "end": v(-255.75, -124.75) * mm});
            skLineSegment(sketch, "E414.1.0.184", {"start": v(-131.25, -136.7) * mm, "end": v(-255.8, -136.7) * mm});
            skLineSegment(sketch, "E414.1.0.185", {"start": v(-135.03, -56.75) * mm, "end": v(-251.9, -56.75) * mm});
            skLineSegment(sketch, "E414.1.0.186", {"start": v(-131.25, -50.75) * mm, "end": v(-255.8, -50.75) * mm});
            skLineSegment(sketch, "E414.1.0.187", {"start": v(-143, -65) * mm, "end": v(-244, -65) * mm});
            skLineSegment(sketch, "E414.1.0.188", {"start": v(-131.25, 49.25) * mm, "end": v(-255.8, 49.25) * mm});
            skLineSegment(sketch, "E414.1.0.189", {"start": v(-131.2, -24.75) * mm, "end": v(-255.75, -24.75) * mm});
            skLineSegment(sketch, "E414.1.0.190", {"start": v(-132.98, 33.3) * mm, "end": v(-253.95, 33.3) * mm});
            skLineSegment(sketch, "E414.1.0.191", {"start": v(-131.25, -46.75) * mm, "end": v(-255.8, -46.75) * mm});
            skLineSegment(sketch, "E414.1.0.192", {"start": v(-131.2, 137.3) * mm, "end": v(-255.75, 137.3) * mm});
            skLineSegment(sketch, "E414.1.0.193", {"start": v(-131.2, 59.25) * mm, "end": v(-255.75, 59.25) * mm});
            skLineSegment(sketch, "E414.1.0.194", {"start": v(-131.25, 43.3) * mm, "end": v(-255.8, 43.3) * mm});
            skLineSegment(sketch, "E414.1.0.195", {"start": v(-131.25, 55.3) * mm, "end": v(-255.8, 55.3) * mm});
            skLineSegment(sketch, "E414.1.0.196", {"start": v(-140.98, 113.3) * mm, "end": v(-245.95, 113.3) * mm});
            skLineSegment(sketch, "E414.1.0.197", {"start": v(-136.98, 117.3) * mm, "end": v(-249.95, 117.3) * mm});
            skLineSegment(sketch, "E414.1.0.198", {"start": v(-131.2, 135.25) * mm, "end": v(-255.75, 135.25) * mm});
            skLineSegment(sketch, "E414.1.0.199", {"start": v(-143.08, 111.2) * mm, "end": v(-243.92, 111.2) * mm});
            skLineSegment(sketch, "E414.1.0.200", {"start": v(-131.25, 141.25) * mm, "end": v(-255.8, 141.25) * mm});
            skLineSegment(sketch, "E414.1.0.201", {"start": v(-2.75, -34.75) * mm, "end": v(-127.3, -34.75) * mm});
            skLineSegment(sketch, "E414.1.0.202", {"start": v(-12.48, -62.7) * mm, "end": v(-117.45, -62.7) * mm});
            skLineSegment(sketch, "E414.1.0.203", {"start": v(-2.75, -44.7) * mm, "end": v(-127.3, -44.7) * mm});
            skLineSegment(sketch, "E414.1.0.204", {"start": v(-2.75, -42.75) * mm, "end": v(-127.3, -42.75) * mm});
            skLineSegment(sketch, "E414.1.0.205", {"start": v(-2.7, 39.25) * mm, "end": v(-127.25, 39.25) * mm});
            skLineSegment(sketch, "E414.1.0.206", {"start": v(-10.55, 27.3) * mm, "end": v(-119.52, 27.3) * mm});
            skLineSegment(sketch, "E414.1.0.207", {"start": v(-14.58, -64.8) * mm, "end": v(-115.42, -64.8) * mm});
            skLineSegment(sketch, "E414.1.0.208", {"start": v(-2.75, 127.3) * mm, "end": v(-127.3, 127.3) * mm});
            skLineSegment(sketch, "E414.1.0.209", {"start": v(-2.75, 57.25) * mm, "end": v(-127.3, 57.25) * mm});
            skLineSegment(sketch, "E414.1.0.210", {"start": v(-2.75, 47.3) * mm, "end": v(-127.3, 47.3) * mm});
            skLineSegment(sketch, "E414.1.0.211", {"start": v(-2.75, 51.3) * mm, "end": v(-127.3, 51.3) * mm});
            skLineSegment(sketch, "E414.1.0.212", {"start": v(-2.7, 133.3) * mm, "end": v(-127.25, 133.3) * mm});
            skLineSegment(sketch, "E414.1.0.213", {"start": v(-10.53, 115.25) * mm, "end": v(-119.4, 115.25) * mm});
            skLineSegment(sketch, "E414.1.0.214", {"start": v(-2.7, 139.25) * mm, "end": v(-127.25, 139.25) * mm});
            skLineSegment(sketch, "E414.1.0.215", {"start": v(-14.5, 111) * mm, "end": v(-115.5, 111) * mm});
            skLineSegment(sketch, "E414.1.0.216", {"start": v(-2.7, 151.25) * mm, "end": v(-127.25, 151.25) * mm});
            skLineSegment(sketch, "E414.1.0.217", {"start": v(-131.25, -130.75) * mm, "end": v(-255.8, -130.75) * mm});
            skLineSegment(sketch, "E414.1.0.218", {"start": v(-131.25, -132.7) * mm, "end": v(-255.8, -132.7) * mm});
            skLineSegment(sketch, "E414.1.0.219", {"start": v(-2.75, -134.75) * mm, "end": v(-127.3, -134.75) * mm});
            skLineSegment(sketch, "E414.1.0.220", {"start": v(-2.7, -116.75) * mm, "end": v(-127.25, -116.75) * mm});
            skLineSegment(sketch, "E414.1.0.221", {"start": v(-139.05, -60.7) * mm, "end": v(-248.02, -60.7) * mm});
            skLineSegment(sketch, "E414.1.0.222", {"start": v(-143.08, -152.8) * mm, "end": v(-243.92, -152.8) * mm});
            skLineSegment(sketch, "E414.1.0.223", {"start": v(-131.25, -122.75) * mm, "end": v(-255.8, -122.75) * mm});
            skLineSegment(sketch, "E414.1.0.224", {"start": v(-140.98, -150.7) * mm, "end": v(-245.95, -150.7) * mm});
            skLineSegment(sketch, "E414.1.0.225", {"start": v(-131.25, -36.7) * mm, "end": v(-255.8, -36.7) * mm});
            skLineSegment(sketch, "E414.1.0.226", {"start": v(-131.2, -40.75) * mm, "end": v(-255.75, -40.75) * mm});
            skLineSegment(sketch, "E414.1.0.227", {"start": v(-131.2, -48.75) * mm, "end": v(-255.75, -48.75) * mm});
            skLineSegment(sketch, "E414.1.0.228", {"start": v(-139.03, 27.25) * mm, "end": v(-247.9, 27.25) * mm});
            skLineSegment(sketch, "E414.1.0.229", {"start": v(-131.2, 51.25) * mm, "end": v(-255.75, 51.25) * mm});
            skLineSegment(sketch, "E414.1.0.230", {"start": v(-131.25, 39.3) * mm, "end": v(-255.8, 39.3) * mm});
            skLineSegment(sketch, "E414.1.0.231", {"start": v(-131.25, -30.75) * mm, "end": v(-255.8, -30.75) * mm});
            skLineSegment(sketch, "E414.1.0.232", {"start": v(-131.2, 125.3) * mm, "end": v(-255.75, 125.3) * mm});
            skLineSegment(sketch, "E414.1.0.233", {"start": v(-143, 23) * mm, "end": v(-244, 23) * mm});
            skLineSegment(sketch, "E414.1.0.234", {"start": v(-131.2, 63.25) * mm, "end": v(-255.75, 63.25) * mm});
            skLineSegment(sketch, "E414.1.0.235", {"start": v(-131.2, 45.3) * mm, "end": v(-255.75, 45.3) * mm});
            skLineSegment(sketch, "E414.1.0.236", {"start": v(-131.25, 143.3) * mm, "end": v(-255.8, 143.3) * mm});
            skLineSegment(sketch, "E414.1.0.237", {"start": v(-131.25, 129.25) * mm, "end": v(-255.8, 129.25) * mm});
            skLineSegment(sketch, "E414.1.0.238", {"start": v(-131.25, 151.3) * mm, "end": v(-255.8, 151.3) * mm});
            skLineSegment(sketch, "E414.1.0.239", {"start": v(-131.2, 147.25) * mm, "end": v(-255.75, 147.25) * mm});
            skLineSegment(sketch, "E414.1.0.240", {"start": v(-14.58, 111.2) * mm, "end": v(-115.42, 111.2) * mm});
            skLineSegment(sketch, "E414.1.0.241", {"start": v(-2.7, -112.75) * mm, "end": v(-127.25, -112.75) * mm});
            skLineSegment(sketch, "E414.1.0.242", {"start": v(-131.2, -112.75) * mm, "end": v(-255.75, -112.75) * mm});
            skLineSegment(sketch, "E414.1.0.243", {"start": v(-14.58, 23.2) * mm, "end": v(-115.42, 23.2) * mm});
            skLineSegment(sketch, "E414.1.0.244", {"start": v(-2.7, -32.75) * mm, "end": v(-127.25, -32.75) * mm});
            skLineSegment(sketch, "E414.1.0.245", {"start": v(-12.48, 25.3) * mm, "end": v(-117.45, 25.3) * mm});
            skLineSegment(sketch, "E414.1.0.246", {"start": v(-14.5, -65) * mm, "end": v(-115.5, -65) * mm});
            skLineSegment(sketch, "E414.1.0.247", {"start": v(-2.7, -24.75) * mm, "end": v(-127.25, -24.75) * mm});
            skLineSegment(sketch, "E414.1.0.248", {"start": v(-2.75, 55.3) * mm, "end": v(-127.3, 55.3) * mm});
            skLineSegment(sketch, "E414.1.0.249", {"start": v(-131.2, 151.25) * mm, "end": v(-255.75, 151.25) * mm});
            skLineSegment(sketch, "E414.1.0.250", {"start": v(-133.1, 33.25) * mm, "end": v(-253.97, 33.25) * mm});
            skLineSegment(sketch, "E414.1.0.251", {"start": v(-131.25, 145.25) * mm, "end": v(-255.8, 145.25) * mm});
            skLineSegment(sketch, "E414.1.0.252", {"start": v(-131.25, 135.3) * mm, "end": v(-255.8, 135.3) * mm});
            skLineSegment(sketch, "E414.1.0.253", {"start": v(-143.1, -152.75) * mm, "end": v(-243.9, -152.75) * mm});
            skLineSegment(sketch, "E414.1.0.254", {"start": v(-131.2, -122.7) * mm, "end": v(-255.75, -122.7) * mm});
            skLineSegment(sketch, "E414.1.0.255", {"start": v(-143.08, -64.8) * mm, "end": v(-243.92, -64.8) * mm});
            skLineSegment(sketch, "E414.1.0.256", {"start": v(-131.25, -34.75) * mm, "end": v(-255.8, -34.75) * mm});
            skLineSegment(sketch, "E414.1.0.257", {"start": v(-2.7, 143.25) * mm, "end": v(-127.25, 143.25) * mm});
            skLineSegment(sketch, "E414.1.0.258", {"start": v(-2.7, -30.7) * mm, "end": v(-127.25, -30.7) * mm});
            skLineSegment(sketch, "E414.1.0.259", {"start": v(-131.2, -114.7) * mm, "end": v(-255.75, -114.7) * mm});
            skLineSegment(sketch, "E414.1.0.260", {"start": v(-131.25, -140.7) * mm, "end": v(-255.8, -140.7) * mm});
            skLineSegment(sketch, "E414.1.0.261", {"start": v(-2.75, -138.75) * mm, "end": v(-127.3, -138.75) * mm});
            skLineSegment(sketch, "E414.1.0.262", {"start": v(-131.25, -138.75) * mm, "end": v(-255.8, -138.75) * mm});
            skLineSegment(sketch, "E414.1.0.263", {"start": v(-135.05, -144.7) * mm, "end": v(-252.02, -144.7) * mm});
            skLineSegment(sketch, "E414.1.0.264", {"start": v(-132.98, -54.7) * mm, "end": v(-253.95, -54.7) * mm});
            skLineSegment(sketch, "E414.1.0.265", {"start": v(-2.75, 35.25) * mm, "end": v(-127.25, 35.25) * mm});
            skLineSegment(sketch, "E414.1.0.266", {"start": v(-131.2, -30.7) * mm, "end": v(-255.75, -30.7) * mm});
            skLineSegment(sketch, "E414.1.0.267", {"start": v(-2.75, -26.75) * mm, "end": v(-127.3, -26.75) * mm});
            skLineSegment(sketch, "E414.1.0.268", {"start": v(-2.7, 141.3) * mm, "end": v(-127.25, 141.3) * mm});
            skLineSegment(sketch, "E414.1.0.269", {"start": v(-131.25, 35.25) * mm, "end": v(-255.75, 35.25) * mm});
            skLineSegment(sketch, "E414.1.0.270", {"start": v(-131.25, 59.3) * mm, "end": v(-255.75, 59.3) * mm});
            skLineSegment(sketch, "E414.1.0.271", {"start": v(-131.25, -26.75) * mm, "end": v(-255.8, -26.75) * mm});
            skLineSegment(sketch, "E414.1.0.272", {"start": v(-131.2, 55.25) * mm, "end": v(-255.75, 55.25) * mm});
            skLineSegment(sketch, "E414.1.0.273", {"start": v(-12.6, 113.25) * mm, "end": v(-117.4, 113.25) * mm});
            skLineSegment(sketch, "E414.1.0.274", {"start": v(-136.98, 29.3) * mm, "end": v(-249.95, 29.3) * mm});
            skLineSegment(sketch, "E414.1.0.275", {"start": v(-131.2, 49.3) * mm, "end": v(-255.75, 49.3) * mm});
            skLineSegment(sketch, "E414.1.0.276", {"start": v(-2.75, -52.7) * mm, "end": v(-127.3, -52.7) * mm});
            skLineSegment(sketch, "E414.1.0.277", {"start": v(-8.6, -146.75) * mm, "end": v(-121.47, -146.75) * mm});
            skLineSegment(sketch, "E414.1.0.278", {"start": v(-6.55, -56.7) * mm, "end": v(-123.52, -56.7) * mm});
            skLineSegment(sketch, "E414.1.0.279", {"start": v(-2.7, 43.25) * mm, "end": v(-127.25, 43.25) * mm});
            skLineSegment(sketch, "E414.1.0.280", {"start": v(-2.7, 57.3) * mm, "end": v(-127.25, 57.3) * mm});
            skLineSegment(sketch, "E414.1.0.281", {"start": v(-2.75, 147.3) * mm, "end": v(-127.25, 147.3) * mm});
            skLineSegment(sketch, "E414.1.0.282", {"start": v(-2.75, 61.25) * mm, "end": v(-127.3, 61.25) * mm});
            skLineSegment(sketch, "E414.1.0.283", {"start": v(-8.48, 117.3) * mm, "end": v(-121.45, 117.3) * mm});
            skLineSegment(sketch, "E414.1.0.284", {"start": v(-2.7, 137.3) * mm, "end": v(-127.25, 137.3) * mm});
            skLineSegment(sketch, "E414.1.0.285", {"start": v(-2.75, 123.25) * mm, "end": v(-127.25, 123.25) * mm});
            skLineSegment(sketch, "E414.1.0.286", {"start": v(-133.1, 121.25) * mm, "end": v(-253.97, 121.25) * mm});
            skLineSegment(sketch, "E414.1.0.287", {"start": v(-131.2, 149.3) * mm, "end": v(-255.75, 149.3) * mm});
            skLineSegment(sketch, "E414.1.0.288", {"start": v(-135.03, 119.25) * mm, "end": v(-251.9, 119.25) * mm});
            skLineSegment(sketch, "E414.1.0.289", {"start": v(-131.25, 125.25) * mm, "end": v(-255.8, 125.25) * mm});
            skLineSegment(sketch, "E414.1.0.290", {"start": v(-131.2, 139.25) * mm, "end": v(-255.75, 139.25) * mm});
            skLineSegment(sketch, "E414.1.0.291", {"start": v(-2.7, 135.25) * mm, "end": v(-127.25, 135.25) * mm});
            skLineSegment(sketch, "E414.1.0.292", {"start": v(-8.6, 117.25) * mm, "end": v(-121.47, 117.25) * mm});
            skLineSegment(sketch, "E414.1.0.293", {"start": v(-143.1, 111.25) * mm, "end": v(-243.9, 111.25) * mm});
            skLineSegment(sketch, "E414.1.0.294", {"start": v(-2.7, 127.25) * mm, "end": v(-127.25, 127.25) * mm});
            skLineSegment(sketch, "E414.1.0.295", {"start": v(-131.2, -132.75) * mm, "end": v(-255.75, -132.75) * mm});
            skLineSegment(sketch, "E414.1.0.296", {"start": v(-131.2, -118.7) * mm, "end": v(-255.75, -118.7) * mm});
            skLineSegment(sketch, "E414.1.0.297", {"start": v(-143.1, 23.25) * mm, "end": v(-243.9, 23.25) * mm});
            skLineSegment(sketch, "E414.1.0.298", {"start": v(-131.2, 53.3) * mm, "end": v(-255.75, 53.3) * mm});
            skLineSegment(sketch, "E414.1.0.299", {"start": v(-131.2, 47.25) * mm, "end": v(-255.75, 47.25) * mm});
            skLineSegment(sketch, "E414.1.0.300", {"start": v(-131.2, 39.25) * mm, "end": v(-255.75, 39.25) * mm});
            skLineSegment(sketch, "E414.1.0.301", {"start": v(-139.05, 27.3) * mm, "end": v(-248.02, 27.3) * mm});
            skLineSegment(sketch, "E414.1.0.302", {"start": v(-4.48, -142.7) * mm, "end": v(-125.45, -142.7) * mm});
            skLineSegment(sketch, "E414.1.0.303", {"start": v(-14.58, -152.8) * mm, "end": v(-115.42, -152.8) * mm});
            skLineSegment(sketch, "E414.1.0.304", {"start": v(-2.7, -46.7) * mm, "end": v(-127.25, -46.7) * mm});
            skLineSegment(sketch, "E414.1.0.305", {"start": v(-2.7, -136.75) * mm, "end": v(-127.25, -136.75) * mm});
            skLineSegment(sketch, "E414.1.0.306", {"start": v(-2.75, -36.7) * mm, "end": v(-127.3, -36.7) * mm});
            skLineSegment(sketch, "E414.1.0.307", {"start": v(-131.2, -128.75) * mm, "end": v(-255.75, -128.75) * mm});
            skLineSegment(sketch, "E414.1.0.308", {"start": v(-131.2, -136.75) * mm, "end": v(-255.75, -136.75) * mm});
            skLineSegment(sketch, "E414.1.0.309", {"start": v(254.25, 151.3) * mm, "end": v(129.7, 151.3) * mm});
            skLineSegment(sketch, "E414.1.0.310", {"start": v(-2.75, -48.7) * mm, "end": v(-127.3, -48.7) * mm});
            skLineSegment(sketch, "E414.1.0.311", {"start": v(-2.75, -122.75) * mm, "end": v(-127.3, -122.75) * mm});
            skLineSegment(sketch, "E414.1.0.312", {"start": v(-139.05, -148.7) * mm, "end": v(-248.02, -148.7) * mm});
            skLineSegment(sketch, "E414.1.0.313", {"start": v(254.25, -118.75) * mm, "end": v(129.7, -118.75) * mm});
            skLineSegment(sketch, "E414.1.0.314", {"start": v(254.25, -134.75) * mm, "end": v(129.7, -134.75) * mm});
            skLineSegment(sketch, "E414.1.0.315", {"start": v(-12.48, -150.7) * mm, "end": v(-117.45, -150.7) * mm});
            skLineSegment(sketch, "E414.1.0.316", {"start": v(125.75, -34.75) * mm, "end": v(1.2, -34.75) * mm});
            skLineSegment(sketch, "E414.1.0.317", {"start": v(-131.25, -48.7) * mm, "end": v(-255.8, -48.7) * mm});
            skLineSegment(sketch, "E414.1.0.318", {"start": v(125.75, 57.25) * mm, "end": v(1.2, 57.25) * mm});
            skLineSegment(sketch, "E414.1.0.319", {"start": v(125.8, 151.25) * mm, "end": v(1.25, 151.25) * mm});
            skLineSegment(sketch, "E414.1.0.320", {"start": v(125.8, 133.3) * mm, "end": v(1.25, 133.3) * mm});
            skLineSegment(sketch, "E414.1.0.321", {"start": v(-6.53, 31.25) * mm, "end": v(-123.4, 31.25) * mm});
            skLineSegment(sketch, "E414.1.0.322", {"start": v(254.25, 53.25) * mm, "end": v(129.7, 53.25) * mm});
            skLineSegment(sketch, "E414.1.0.323", {"start": v(254.25, 145.25) * mm, "end": v(129.7, 145.25) * mm});
            skLineSegment(sketch, "E414.1.0.324", {"start": v(-2.75, 37.25) * mm, "end": v(-127.3, 37.25) * mm});
            skLineSegment(sketch, "E414.1.0.325", {"start": v(-2.75, -40.7) * mm, "end": v(-127.3, -40.7) * mm});
            skLineSegment(sketch, "E414.1.0.326", {"start": v(-10.53, -60.75) * mm, "end": v(-119.4, -60.75) * mm});
            skLineSegment(sketch, "E414.1.0.327", {"start": v(-139.03, -60.75) * mm, "end": v(-247.9, -60.75) * mm});
            skLineSegment(sketch, "E414.1.0.328", {"start": v(-2.75, -116.7) * mm, "end": v(-127.25, -116.7) * mm});
            skLineSegment(sketch, "E414.1.0.329", {"start": v(-131.2, -36.75) * mm, "end": v(-255.75, -36.75) * mm});
            skLineSegment(sketch, "E414.1.0.330", {"start": v(242.4, 111.25) * mm, "end": v(141.6, 111.25) * mm});
            skLineSegment(sketch, "E414.1.0.331", {"start": v(-2.75, 131.3) * mm, "end": v(-127.3, 131.3) * mm});
            skLineSegment(sketch, "E414.1.0.332", {"start": v(125.8, -118.7) * mm, "end": v(1.25, -118.7) * mm});
            skLineSegment(sketch, "E414.1.0.333", {"start": v(125.75, -52.75) * mm, "end": v(1.25, -52.75) * mm});
            skLineSegment(sketch, "E414.1.0.334", {"start": v(125.8, 53.3) * mm, "end": v(1.25, 53.3) * mm});
            skLineSegment(sketch, "E414.1.0.335", {"start": v(254.3, -30.7) * mm, "end": v(129.75, -30.7) * mm});
            skLineSegment(sketch, "E414.1.0.336", {"start": v(-131.25, 41.25) * mm, "end": v(-255.8, 41.25) * mm});
            skLineSegment(sketch, "E414.1.0.337", {"start": v(254.3, 141.3) * mm, "end": v(129.75, 141.3) * mm});
            skLineSegment(sketch, "E414.1.0.338", {"start": v(-2.75, 149.25) * mm, "end": v(-127.3, 149.25) * mm});
            skLineSegment(sketch, "E414.1.0.339", {"start": v(125.8, 149.3) * mm, "end": v(1.25, 149.3) * mm});
            skLineSegment(sketch, "E414.1.0.340", {"start": v(119.9, -146.75) * mm, "end": v(7.03, -146.75) * mm});
            skLineSegment(sketch, "E414.1.0.341", {"start": v(125.8, -134.7) * mm, "end": v(1.25, -134.7) * mm});
            skLineSegment(sketch, "E414.1.0.342", {"start": v(125.75, -50.75) * mm, "end": v(1.2, -50.75) * mm});
            skLineSegment(sketch, "E414.1.0.343", {"start": v(121.95, -56.7) * mm, "end": v(4.98, -56.7) * mm});
            skLineSegment(sketch, "E414.1.0.344", {"start": v(125.75, 49.25) * mm, "end": v(1.2, 49.25) * mm});
            skLineSegment(sketch, "E414.1.0.345", {"start": v(-131.25, 131.3) * mm, "end": v(-255.8, 131.3) * mm});
            skLineSegment(sketch, "E414.1.0.346", {"start": v(254.3, -116.75) * mm, "end": v(129.75, -116.75) * mm});
            skLineSegment(sketch, "E414.1.0.347", {"start": v(254.3, -132.75) * mm, "end": v(129.75, -132.75) * mm});
            skLineSegment(sketch, "E414.1.0.348", {"start": v(248.4, -58.75) * mm, "end": v(135.53, -58.75) * mm});
            skLineSegment(sketch, "E414.1.0.349", {"start": v(250.45, 31.3) * mm, "end": v(133.48, 31.3) * mm});
            skLineSegment(sketch, "E414.1.0.350", {"start": v(254.25, 149.25) * mm, "end": v(129.7, 149.25) * mm});
            skLineSegment(sketch, "E414.1.0.351", {"start": v(254.25, 137.25) * mm, "end": v(129.7, 137.25) * mm});
            skLineSegment(sketch, "E414.1.0.352", {"start": v(125.75, 129.25) * mm, "end": v(1.2, 129.25) * mm});
            skLineSegment(sketch, "E414.1.0.353", {"start": v(-2.75, 133.25) * mm, "end": v(-127.3, 133.25) * mm});
            skLineSegment(sketch, "E414.1.0.354", {"start": v(125.75, -130.75) * mm, "end": v(1.2, -130.75) * mm});
            skLineSegment(sketch, "E414.1.0.355", {"start": v(125.75, -132.7) * mm, "end": v(1.2, -132.7) * mm});
            skLineSegment(sketch, "E414.1.0.356", {"start": v(125.8, -48.75) * mm, "end": v(1.25, -48.75) * mm});
            skLineSegment(sketch, "E414.1.0.357", {"start": v(117.95, -60.7) * mm, "end": v(8.98, -60.7) * mm});
            skLineSegment(sketch, "E414.1.0.358", {"start": v(125.75, 39.3) * mm, "end": v(1.2, 39.3) * mm});
            skLineSegment(sketch, "E414.1.0.359", {"start": v(117.97, 27.25) * mm, "end": v(9.1, 27.25) * mm});
            skLineSegment(sketch, "E414.1.0.360", {"start": v(125.8, 125.3) * mm, "end": v(1.25, 125.3) * mm});
            skLineSegment(sketch, "E414.1.0.361", {"start": v(246.47, -148.75) * mm, "end": v(137.6, -148.75) * mm});
            skLineSegment(sketch, "E414.1.0.362", {"start": v(254.25, -44.7) * mm, "end": v(129.7, -44.7) * mm});
            skLineSegment(sketch, "E414.1.0.363", {"start": v(254.3, 39.25) * mm, "end": v(129.75, 39.25) * mm});
            skLineSegment(sketch, "E414.1.0.364", {"start": v(246.45, 27.3) * mm, "end": v(137.48, 27.3) * mm});
            skLineSegment(sketch, "E414.1.0.365", {"start": v(254.25, 127.3) * mm, "end": v(129.7, 127.3) * mm});
            skLineSegment(sketch, "E414.1.0.366", {"start": v(125.75, 145.25) * mm, "end": v(1.2, 145.25) * mm});
            skLineSegment(sketch, "E414.1.0.367", {"start": v(-2.75, -120.7) * mm, "end": v(-127.3, -120.7) * mm});
            skLineSegment(sketch, "E414.1.0.368", {"start": v(125.8, -112.75) * mm, "end": v(1.25, -112.75) * mm});
            skLineSegment(sketch, "E414.1.0.369", {"start": v(125.8, -28.75) * mm, "end": v(1.25, -28.75) * mm});
            skLineSegment(sketch, "E414.1.0.370", {"start": v(116.02, 25.3) * mm, "end": v(11.05, 25.3) * mm});
            skLineSegment(sketch, "E414.1.0.371", {"start": v(113.92, 23.2) * mm, "end": v(13.08, 23.2) * mm});
            skLineSegment(sketch, "E414.1.0.372", {"start": v(125.75, 135.3) * mm, "end": v(1.2, 135.3) * mm});
            skLineSegment(sketch, "E414.1.0.373", {"start": v(254.25, -114.75) * mm, "end": v(129.7, -114.75) * mm});
            skLineSegment(sketch, "E414.1.0.374", {"start": v(254.25, -130.75) * mm, "end": v(129.7, -130.75) * mm});
            skLineSegment(sketch, "E414.1.0.375", {"start": v(254.3, -42.7) * mm, "end": v(129.75, -42.7) * mm});
            skLineSegment(sketch, "E414.1.0.376", {"start": v(254.3, -24.75) * mm, "end": v(129.75, -24.75) * mm});
            skLineSegment(sketch, "E414.1.0.377", {"start": v(244.52, 113.3) * mm, "end": v(139.55, 113.3) * mm});
            skLineSegment(sketch, "E414.1.0.378", {"start": v(248.52, -146.7) * mm, "end": v(135.55, -146.7) * mm});
            skLineSegment(sketch, "E414.1.0.379", {"start": v(123.9, -142.75) * mm, "end": v(3.03, -142.75) * mm});
            skLineSegment(sketch, "E414.1.0.380", {"start": v(125.8, -114.7) * mm, "end": v(1.25, -114.7) * mm});
            skLineSegment(sketch, "E414.1.0.381", {"start": v(125.75, -140.7) * mm, "end": v(1.2, -140.7) * mm});
            skLineSegment(sketch, "E414.1.0.382", {"start": v(125.8, -30.7) * mm, "end": v(1.25, -30.7) * mm});
            skLineSegment(sketch, "E414.1.0.383", {"start": v(125.75, 35.25) * mm, "end": v(1.25, 35.25) * mm});
            skLineSegment(sketch, "E414.1.0.384", {"start": v(113.9, 111.25) * mm, "end": v(13.1, 111.25) * mm});
            skLineSegment(sketch, "E414.1.0.385", {"start": v(125.8, 141.3) * mm, "end": v(1.25, 141.3) * mm});
            skLineSegment(sketch, "E414.1.0.386", {"start": v(254.3, -26.7) * mm, "end": v(129.75, -26.7) * mm});
            skLineSegment(sketch, "E414.1.0.387", {"start": v(252.4, -54.75) * mm, "end": v(131.53, -54.75) * mm});
            skLineSegment(sketch, "E414.1.0.388", {"start": v(-2.75, -130.75) * mm, "end": v(-127.3, -130.75) * mm});
            skLineSegment(sketch, "E414.1.0.389", {"start": v(254.3, 57.3) * mm, "end": v(129.75, 57.3) * mm});
            skLineSegment(sketch, "E414.1.0.390", {"start": v(254.25, 123.25) * mm, "end": v(129.75, 123.25) * mm});
            skLineSegment(sketch, "E414.1.0.391", {"start": v(242.42, -152.8) * mm, "end": v(141.58, -152.8) * mm});
            skLineSegment(sketch, "E414.1.0.392", {"start": v(-2.7, -134.7) * mm, "end": v(-127.25, -134.7) * mm});
            skLineSegment(sketch, "E414.1.0.393", {"start": v(254.3, -112.75) * mm, "end": v(129.75, -112.75) * mm});
            skLineSegment(sketch, "E414.1.0.394", {"start": v(254.3, -128.75) * mm, "end": v(129.75, -128.75) * mm});
            skLineSegment(sketch, "E414.1.0.395", {"start": v(250.47, -144.75) * mm, "end": v(133.6, -144.75) * mm});
            skLineSegment(sketch, "E414.1.0.396", {"start": v(254.3, -38.7) * mm, "end": v(129.75, -38.7) * mm});
            skLineSegment(sketch, "E414.1.0.397", {"start": v(119.9, -58.75) * mm, "end": v(7.03, -58.75) * mm});
            skLineSegment(sketch, "E414.1.0.398", {"start": v(125.75, 37.25) * mm, "end": v(1.2, 37.25) * mm});
            skLineSegment(sketch, "E414.1.0.399", {"start": v(121.97, 31.25) * mm, "end": v(5.1, 31.25) * mm});
            skLineSegment(sketch, "E414.1.0.400", {"start": v(125.75, 137.25) * mm, "end": v(1.2, 137.25) * mm});
            skLineSegment(sketch, "E414.1.0.401", {"start": v(124.02, 121.3) * mm, "end": v(3.05, 121.3) * mm});
            skLineSegment(sketch, "E414.1.0.402", {"start": v(254.3, -32.75) * mm, "end": v(129.75, -32.75) * mm});
            skLineSegment(sketch, "E414.1.0.403", {"start": v(248.4, 29.25) * mm, "end": v(135.53, 29.25) * mm});
            skLineSegment(sketch, "E414.1.0.404", {"start": v(254.3, 41.3) * mm, "end": v(129.75, 41.3) * mm});
            skLineSegment(sketch, "E414.1.0.405", {"start": v(250.47, 119.25) * mm, "end": v(133.6, 119.25) * mm});
            skLineSegment(sketch, "E414.1.0.406", {"start": v(254.25, 125.25) * mm, "end": v(129.7, 125.25) * mm});
            skLineSegment(sketch, "E414.1.0.407", {"start": v(125.8, -120.75) * mm, "end": v(1.25, -120.75) * mm});
            skLineSegment(sketch, "E414.1.0.408", {"start": v(125.8, -126.7) * mm, "end": v(1.25, -126.7) * mm});
            skLineSegment(sketch, "E414.1.0.409", {"start": v(117.97, 115.25) * mm, "end": v(9.1, 115.25) * mm});
            skLineSegment(sketch, "E414.1.0.410", {"start": v(-2.75, -132.7) * mm, "end": v(-127.3, -132.7) * mm});
            skLineSegment(sketch, "E414.1.0.411", {"start": v(254.3, -50.7) * mm, "end": v(129.75, -50.7) * mm});
            skLineSegment(sketch, "E414.1.0.412", {"start": v(125.75, -44.7) * mm, "end": v(1.2, -44.7) * mm});
            skLineSegment(sketch, "E414.1.0.413", {"start": v(125.75, 127.3) * mm, "end": v(1.2, 127.3) * mm});
            skLineSegment(sketch, "E414.1.0.414", {"start": v(254.25, 45.25) * mm, "end": v(129.7, 45.25) * mm});
            skLineSegment(sketch, "E414.1.0.415", {"start": v(254.25, 43.3) * mm, "end": v(129.7, 43.3) * mm});
            skLineSegment(sketch, "E414.1.0.416", {"start": v(246.45, 115.3) * mm, "end": v(137.48, 115.3) * mm});
            skLineSegment(sketch, "E414.1.0.417", {"start": v(125.8, -138.7) * mm, "end": v(1.25, -138.7) * mm});
            skLineSegment(sketch, "E414.1.0.418", {"start": v(-10.53, 27.25) * mm, "end": v(-119.4, 27.25) * mm});
            skLineSegment(sketch, "E414.1.0.419", {"start": v(-2.7, 51.25) * mm, "end": v(-127.25, 51.25) * mm});
            skLineSegment(sketch, "E414.1.0.420", {"start": v(-2.75, 39.3) * mm, "end": v(-127.3, 39.3) * mm});
            skLineSegment(sketch, "E414.1.0.421", {"start": v(252.4, -142.75) * mm, "end": v(131.53, -142.75) * mm});
            skLineSegment(sketch, "E414.1.0.422", {"start": v(254.25, -126.75) * mm, "end": v(129.7, -126.75) * mm});
            skLineSegment(sketch, "E414.1.0.423", {"start": v(254.25, -36.7) * mm, "end": v(129.7, -36.7) * mm});
            skLineSegment(sketch, "E414.1.0.424", {"start": v(242.5, 23) * mm, "end": v(141.5, 23) * mm});
            skLineSegment(sketch, "E414.1.0.425", {"start": v(254.3, 63.25) * mm, "end": v(129.75, 63.25) * mm});
            skLineSegment(sketch, "E414.1.0.426", {"start": v(-2.75, 151.3) * mm, "end": v(-127.3, 151.3) * mm});
            skLineSegment(sketch, "E414.1.0.427", {"start": v(254.3, 147.25) * mm, "end": v(129.75, 147.25) * mm});
            skLineSegment(sketch, "E414.1.0.428", {"start": v(125.75, -124.7) * mm, "end": v(1.2, -124.7) * mm});
            skLineSegment(sketch, "E414.1.0.429", {"start": v(125.8, -24.75) * mm, "end": v(1.25, -24.75) * mm});
            skLineSegment(sketch, "E414.1.0.430", {"start": v(125.8, -42.7) * mm, "end": v(1.25, -42.7) * mm});
            skLineSegment(sketch, "E414.1.0.431", {"start": v(114, -65) * mm, "end": v(13, -65) * mm});
            skLineSegment(sketch, "E414.1.0.432", {"start": v(125.8, 59.25) * mm, "end": v(1.25, 59.25) * mm});
            skLineSegment(sketch, "E414.1.0.433", {"start": v(244.4, -62.75) * mm, "end": v(139.6, -62.75) * mm});
            skLineSegment(sketch, "E414.1.0.434", {"start": v(242.4, -64.75) * mm, "end": v(141.6, -64.75) * mm});
            skLineSegment(sketch, "E414.1.0.435", {"start": v(254.3, -34.7) * mm, "end": v(129.75, -34.7) * mm});
            skLineSegment(sketch, "E414.1.0.436", {"start": v(254.25, 35.3) * mm, "end": v(129.7, 35.3) * mm});
            skLineSegment(sketch, "E414.1.0.437", {"start": v(254.3, 131.25) * mm, "end": v(129.75, 131.25) * mm});
            skLineSegment(sketch, "E414.1.0.438", {"start": v(-2.7, -114.7) * mm, "end": v(-127.25, -114.7) * mm});
            skLineSegment(sketch, "E414.1.0.439", {"start": v(125.8, -122.7) * mm, "end": v(1.25, -122.7) * mm});
            skLineSegment(sketch, "E414.1.0.440", {"start": v(115.9, -150.75) * mm, "end": v(11.1, -150.75) * mm});
            skLineSegment(sketch, "E414.1.0.441", {"start": v(113.9, -152.75) * mm, "end": v(13.1, -152.75) * mm});
            skLineSegment(sketch, "E414.1.0.442", {"start": v(125.8, 43.25) * mm, "end": v(1.25, 43.25) * mm});
            skLineSegment(sketch, "E414.1.0.443", {"start": v(125.75, 147.3) * mm, "end": v(1.25, 147.3) * mm});
            skLineSegment(sketch, "E414.1.0.444", {"start": v(254.25, -140.75) * mm, "end": v(129.75, -140.75) * mm});
            skLineSegment(sketch, "E414.1.0.445", {"start": v(254.3, -124.75) * mm, "end": v(129.75, -124.75) * mm});
            skLineSegment(sketch, "E414.1.0.446", {"start": v(254.3, 49.3) * mm, "end": v(129.75, 49.3) * mm});
            skLineSegment(sketch, "E414.1.0.447", {"start": v(254.3, 55.25) * mm, "end": v(129.75, 55.25) * mm});
            skLineSegment(sketch, "E414.1.0.448", {"start": v(-2.7, -126.7) * mm, "end": v(-127.25, -126.7) * mm});
            skLineSegment(sketch, "E414.1.0.449", {"start": v(121.97, 119.25) * mm, "end": v(5.1, 119.25) * mm});
            skLineSegment(sketch, "E414.1.0.450", {"start": v(125.8, -32.75) * mm, "end": v(1.25, -32.75) * mm});
            skLineSegment(sketch, "E414.1.0.451", {"start": v(125.8, -38.7) * mm, "end": v(1.25, -38.7) * mm});
            skLineSegment(sketch, "E414.1.0.452", {"start": v(254.25, 133.25) * mm, "end": v(129.7, 133.25) * mm});
            skLineSegment(sketch, "E414.1.0.453", {"start": v(125.75, 45.25) * mm, "end": v(1.2, 45.25) * mm});
            skLineSegment(sketch, "E414.1.0.454", {"start": v(254.25, -138.75) * mm, "end": v(129.7, -138.75) * mm});
            skLineSegment(sketch, "E414.1.0.455", {"start": v(254.25, -122.75) * mm, "end": v(129.7, -122.75) * mm});
            skLineSegment(sketch, "E414.1.0.456", {"start": v(125.8, 63.25) * mm, "end": v(1.25, 63.25) * mm});
            skLineSegment(sketch, "E414.1.0.457", {"start": v(-131.2, -134.7) * mm, "end": v(-255.75, -134.7) * mm});
            skLineSegment(sketch, "E414.1.0.458", {"start": v(-135.05, -56.7) * mm, "end": v(-252.02, -56.7) * mm});
            skLineSegment(sketch, "E414.1.0.459", {"start": v(-131.25, -124.7) * mm, "end": v(-255.8, -124.7) * mm});
            skLineSegment(sketch, "E414.1.0.460", {"start": v(-131.25, -24.7) * mm, "end": v(-255.8, -24.7) * mm});
            skLineSegment(sketch, "E414.1.0.461", {"start": v(-131.2, -50.7) * mm, "end": v(-255.75, -50.7) * mm});
            skLineSegment(sketch, "E414.1.0.462", {"start": v(-131.25, 61.25) * mm, "end": v(-255.8, 61.25) * mm});
            skLineSegment(sketch, "E414.1.0.463", {"start": v(-131.2, -42.7) * mm, "end": v(-255.75, -42.7) * mm});
            skLineSegment(sketch, "E414.1.0.464", {"start": v(-131.25, 45.25) * mm, "end": v(-255.8, 45.25) * mm});
            skLineSegment(sketch, "E414.1.0.465", {"start": v(-139.05, 115.3) * mm, "end": v(-248.02, 115.3) * mm});
            skLineSegment(sketch, "E414.1.0.466", {"start": v(-131.2, 143.25) * mm, "end": v(-255.75, 143.25) * mm});
            skLineSegment(sketch, "E414.1.0.467", {"start": v(-131.2, 127.25) * mm, "end": v(-255.75, 127.25) * mm});
            skLineSegment(sketch, "E414.1.0.468", {"start": v(-2.7, 47.25) * mm, "end": v(-127.25, 47.25) * mm});
            skLineSegment(sketch, "E414.1.0.469", {"start": v(-131.25, -40.7) * mm, "end": v(-255.8, -40.7) * mm});
            skLineSegment(sketch, "E414.1.0.470", {"start": v(-12.48, 113.3) * mm, "end": v(-117.45, 113.3) * mm});
            skLineSegment(sketch, "E414.1.0.471", {"start": v(-12.6, 25.25) * mm, "end": v(-117.4, 25.25) * mm});
            skLineSegment(sketch, "E414.1.0.472", {"start": v(-14.6, 23.25) * mm, "end": v(-115.4, 23.25) * mm});
            skLineSegment(sketch, "E414.1.0.473", {"start": v(-2.7, 149.3) * mm, "end": v(-127.25, 149.3) * mm});
            skLineSegment(sketch, "E414.1.0.474", {"start": v(-2.75, 141.25) * mm, "end": v(-127.3, 141.25) * mm});
            skLineSegment(sketch, "E414.1.0.475", {"start": v(-4.6, 121.25) * mm, "end": v(-125.47, 121.25) * mm});
            skLineSegment(sketch, "E414.1.0.476", {"start": v(-14.5, -153) * mm, "end": v(-115.5, -153) * mm});
            skLineSegment(sketch, "E414.1.0.477", {"start": v(-2.75, -114.75) * mm, "end": v(-127.3, -114.75) * mm});
            skLineSegment(sketch, "E414.1.0.478", {"start": v(-2.75, -32.7) * mm, "end": v(-127.3, -32.7) * mm});
            skLineSegment(sketch, "E414.1.0.479", {"start": v(-131.2, -130.7) * mm, "end": v(-255.75, -130.7) * mm});
            skLineSegment(sketch, "E414.1.0.480", {"start": v(-2.75, -140.75) * mm, "end": v(-127.25, -140.75) * mm});
            skLineSegment(sketch, "E414.1.0.481", {"start": v(-14.6, -64.75) * mm, "end": v(-115.4, -64.75) * mm});
            skLineSegment(sketch, "E414.1.0.482", {"start": v(-131.25, -32.7) * mm, "end": v(-255.8, -32.7) * mm});
            skLineSegment(sketch, "E414.1.0.483", {"start": v(-131.25, -140.75) * mm, "end": v(-255.75, -140.75) * mm});
            skLineSegment(sketch, "E414.1.0.484", {"start": v(-2.7, -34.7) * mm, "end": v(-127.25, -34.7) * mm});
            skLineSegment(sketch, "E414.1.0.485", {"start": v(-143, -153) * mm, "end": v(-244, -153) * mm});
            skLineSegment(sketch, "E414.1.0.486", {"start": v(-143.1, -64.75) * mm, "end": v(-243.9, -64.75) * mm});
            skLineSegment(sketch, "E414.1.0.487", {"start": v(-2.75, 53.25) * mm, "end": v(-127.3, 53.25) * mm});
            skLineSegment(sketch, "E414.1.0.488", {"start": v(-131.2, -34.7) * mm, "end": v(-255.75, -34.7) * mm});
            skLineSegment(sketch, "E414.1.0.489", {"start": v(-8.48, -58.7) * mm, "end": v(-121.45, -58.7) * mm});
            skLineSegment(sketch, "E414.1.0.490", {"start": v(-12.6, -62.75) * mm, "end": v(-117.4, -62.75) * mm});
            skLineSegment(sketch, "E414.1.0.491", {"start": v(-131.2, -28.75) * mm, "end": v(-255.75, -28.75) * mm});
            skLineSegment(sketch, "E414.1.0.492", {"start": v(-2.75, -118.75) * mm, "end": v(-127.3, -118.75) * mm});
            skLineSegment(sketch, "E414.1.0.493", {"start": v(-2.7, -132.75) * mm, "end": v(-127.25, -132.75) * mm});
            skLineSegment(sketch, "E414.1.0.494", {"start": v(-2.75, -28.7) * mm, "end": v(-127.25, -28.7) * mm});
            skLineSegment(sketch, "E414.1.0.495", {"start": v(-2.7, -42.7) * mm, "end": v(-127.25, -42.7) * mm});
            skLineSegment(sketch, "E414.1.0.496", {"start": v(-131.25, 47.3) * mm, "end": v(-255.8, 47.3) * mm});
            skLineSegment(sketch, "E414.1.0.497", {"start": v(-131.25, 51.3) * mm, "end": v(-255.8, 51.3) * mm});
            skLineSegment(sketch, "E414.1.0.498", {"start": v(-133.1, -54.75) * mm, "end": v(-253.97, -54.75) * mm});
            skLineSegment(sketch, "E414.1.0.499", {"start": v(-131.2, 43.25) * mm, "end": v(-255.75, 43.25) * mm});
            skLineSegment(sketch, "E414.1.0.500", {"start": v(-131.25, 37.25) * mm, "end": v(-255.8, 37.25) * mm});
            skLineSegment(sketch, "E414.1.0.501", {"start": v(-131.2, 57.3) * mm, "end": v(-255.75, 57.3) * mm});
            skLineSegment(sketch, "E414.1.0.502", {"start": v(-135.05, 31.3) * mm, "end": v(-252.02, 31.3) * mm});
            skLineSegment(sketch, "E414.1.0.503", {"start": v(-131.25, 123.25) * mm, "end": v(-255.75, 123.25) * mm});
            skLineSegment(sketch, "E414.1.0.504", {"start": v(-131.2, 133.3) * mm, "end": v(-255.75, 133.3) * mm});
            skLineSegment(sketch, "E414.1.0.505", {"start": v(-131.25, 149.25) * mm, "end": v(-255.8, 149.25) * mm});
            skLineSegment(sketch, "E414.1.0.506", {"start": v(-131.25, 137.25) * mm, "end": v(-255.8, 137.25) * mm});
            skLineSegment(sketch, "E414.1.0.507", {"start": v(-2.75, 139.3) * mm, "end": v(-127.3, 139.3) * mm});
            skLineSegment(sketch, "E414.1.0.508", {"start": v(-143.08, 23.2) * mm, "end": v(-243.92, 23.2) * mm});
            skLineSegment(sketch, "E414.1.0.509", {"start": v(-4.6, 33.25) * mm, "end": v(-125.47, 33.25) * mm});
            skLineSegment(sketch, "E414.1.0.510", {"start": v(-131.25, 53.25) * mm, "end": v(-255.8, 53.25) * mm});
            skLineSegment(sketch, "E414.1.0.511", {"start": v(-2.7, 61.3) * mm, "end": v(-127.25, 61.3) * mm});
            skLineSegment(sketch, "E414.1.0.512", {"start": v(-2.7, 41.3) * mm, "end": v(-127.25, 41.3) * mm});
            skLineSegment(sketch, "E414.1.0.513", {"start": v(-2.75, 35.3) * mm, "end": v(-127.3, 35.3) * mm});
            skLineSegment(sketch, "E414.1.0.514", {"start": v(-131.25, 139.3) * mm, "end": v(-255.8, 139.3) * mm});
            skLineSegment(sketch, "E414.1.0.515", {"start": v(-2.75, 145.25) * mm, "end": v(-127.3, 145.25) * mm});
            skLineSegment(sketch, "E414.1.0.516", {"start": v(-131.2, 61.3) * mm, "end": v(-255.75, 61.3) * mm});
            skLineSegment(sketch, "E414.1.0.517", {"start": v(-2.75, 135.3) * mm, "end": v(-127.3, 135.3) * mm});
            skLineSegment(sketch, "E414.1.0.518", {"start": v(-131.25, 35.3) * mm, "end": v(-255.8, 35.3) * mm});
            skLineSegment(sketch, "E414.1.0.519", {"start": v(-131.2, 145.3) * mm, "end": v(-255.75, 145.3) * mm});
            skLineSegment(sketch, "E414.1.0.520", {"start": v(-6.53, 119.25) * mm, "end": v(-123.4, 119.25) * mm});
            skLineSegment(sketch, "E414.1.0.521", {"start": v(-2.7, 131.25) * mm, "end": v(-127.25, 131.25) * mm});
            skLineSegment(sketch, "E414.1.0.522", {"start": v(-2.75, 125.25) * mm, "end": v(-127.3, 125.25) * mm});
            skLineSegment(sketch, "E414.1.0.523", {"start": v(-131.2, 131.25) * mm, "end": v(-255.75, 131.25) * mm});
            skLineSegment(sketch, "E414.1.0.524", {"start": v(-131.2, -116.75) * mm, "end": v(-255.75, -116.75) * mm});
            skLineSegment(sketch, "E414.1.0.525", {"start": v(-131.2, -120.75) * mm, "end": v(-255.75, -120.75) * mm});
            skLineSegment(sketch, "E414.1.0.526", {"start": v(-140.98, -62.7) * mm, "end": v(-245.95, -62.7) * mm});
            skLineSegment(sketch, "E414.1.0.527", {"start": v(-136.98, -146.7) * mm, "end": v(-249.95, -146.7) * mm});
            skLineSegment(sketch, "E414.1.0.528", {"start": v(-141.1, -150.75) * mm, "end": v(-245.9, -150.75) * mm});
            skLineSegment(sketch, "E414.1.0.529", {"start": v(-131.2, -26.7) * mm, "end": v(-255.75, -26.7) * mm});
            skLineSegment(sketch, "E414.1.0.530", {"start": v(-131.25, -52.7) * mm, "end": v(-255.8, -52.7) * mm});
            skLineSegment(sketch, "E414.1.0.531", {"start": v(-4.6, -142.75) * mm, "end": v(-125.47, -142.75) * mm});
            skLineSegment(sketch, "E414.1.0.532", {"start": v(-10.53, -148.75) * mm, "end": v(-119.4, -148.75) * mm});
            skLineSegment(sketch, "E414.1.0.533", {"start": v(-133.1, -142.75) * mm, "end": v(-253.97, -142.75) * mm});
            skLineSegment(sketch, "E414.1.0.534", {"start": v(-6.53, -144.75) * mm, "end": v(-123.4, -144.75) * mm});
            skLineSegment(sketch, "E414.1.0.535", {"start": v(-2.7, -50.7) * mm, "end": v(-127.25, -50.7) * mm});
            skLineSegment(sketch, "E414.1.0.536", {"start": v(-135.03, -144.75) * mm, "end": v(-251.9, -144.75) * mm});
            skLineSegment(sketch, "E414.1.0.537", {"start": v(-2.75, -38.75) * mm, "end": v(-127.3, -38.75) * mm});
            skLineSegment(sketch, "E414.1.0.538", {"start": v(-4.48, -54.7) * mm, "end": v(-125.45, -54.7) * mm});
            skLineSegment(sketch, "E414.1.0.539", {"start": v(-2.75, -46.75) * mm, "end": v(-127.3, -46.75) * mm});
            skLineSegment(sketch, "E414.1.0.540", {"start": v(-2.75, 59.3) * mm, "end": v(-127.25, 59.3) * mm});
            skLineSegment(sketch, "E414.1.0.541", {"start": v(-2.75, 45.25) * mm, "end": v(-127.3, 45.25) * mm});
            skLineSegment(sketch, "E414.1.0.542", {"start": v(-8.48, 29.3) * mm, "end": v(-121.45, 29.3) * mm});
            skLineSegment(sketch, "E414.1.0.543", {"start": v(-2.75, 43.3) * mm, "end": v(-127.3, 43.3) * mm});
            skLineSegment(sketch, "E414.1.0.544", {"start": v(-2.7, 129.3) * mm, "end": v(-127.25, 129.3) * mm});
            skLineSegment(sketch, "E414.1.0.545", {"start": v(-131.2, 141.3) * mm, "end": v(-255.75, 141.3) * mm});
            skLineSegment(sketch, "E414.1.0.546", {"start": v(-10.55, 115.3) * mm, "end": v(-119.52, 115.3) * mm});
            skLineSegment(sketch, "E414.1.0.547", {"start": v(-12.6, -150.75) * mm, "end": v(-117.4, -150.75) * mm});
            skLineSegment(sketch, "E414.1.0.548", {"start": v(-2.75, 49.25) * mm, "end": v(-127.3, 49.25) * mm});
            skLineSegment(sketch, "E414.1.0.549", {"start": v(-135.05, 119.3) * mm, "end": v(-252.02, 119.3) * mm});
            skLineSegment(sketch, "E414.1.0.550", {"start": v(-131.25, 127.3) * mm, "end": v(-255.8, 127.3) * mm});
            skLineSegment(sketch, "E414.1.0.551", {"start": v(-131.2, 129.3) * mm, "end": v(-255.75, 129.3) * mm});
            skLineSegment(sketch, "E414.1.0.552", {"start": v(-141.1, 113.25) * mm, "end": v(-245.9, 113.25) * mm});
            skLineSegment(sketch, "E414.1.0.553", {"start": v(-137.1, 117.25) * mm, "end": v(-249.97, 117.25) * mm});
            skLineSegment(sketch, "E414.1.0.554", {"start": v(-131.25, -134.75) * mm, "end": v(-255.8, -134.75) * mm});
            skLineSegment(sketch, "E414.1.0.555", {"start": v(-131.25, -126.75) * mm, "end": v(-255.8, -126.75) * mm});
            skLineSegment(sketch, "E414.1.0.556", {"start": v(-136.98, -58.7) * mm, "end": v(-249.95, -58.7) * mm});
            skLineSegment(sketch, "E414.1.0.557", {"start": v(-131.2, -38.7) * mm, "end": v(-255.75, -38.7) * mm});
            skLineSegment(sketch, "E414.1.0.558", {"start": v(-141.1, 25.25) * mm, "end": v(-245.9, 25.25) * mm});
            skLineSegment(sketch, "E414.1.0.559", {"start": v(-131.25, -44.7) * mm, "end": v(-255.8, -44.7) * mm});
            skLineSegment(sketch, "E414.1.0.560", {"start": v(-131.25, -42.75) * mm, "end": v(-255.8, -42.75) * mm});
            skLineSegment(sketch, "E414.1.0.561", {"start": v(-131.2, 41.3) * mm, "end": v(-255.75, 41.3) * mm});
            skLineSegment(sketch, "E414.1.0.562", {"start": v(-2.7, -120.75) * mm, "end": v(-127.25, -120.75) * mm});
            skLineSegment(sketch, "E414.1.0.563", {"start": v(125.75, -138.75) * mm, "end": v(1.2, -138.75) * mm});
            skLineSegment(sketch, "E414.1.0.564", {"start": v(121.97, -144.75) * mm, "end": v(5.1, -144.75) * mm});
            skLineSegment(sketch, "E414.1.0.565", {"start": v(125.75, -26.75) * mm, "end": v(1.2, -26.75) * mm});
            skLineSegment(sketch, "E414.1.0.566", {"start": v(124.02, -54.7) * mm, "end": v(3.05, -54.7) * mm});
            skLineSegment(sketch, "E414.1.0.567", {"start": v(120.02, 29.3) * mm, "end": v(7.05, 29.3) * mm});
            skLineSegment(sketch, "E414.1.0.568", {"start": v(125.8, 55.25) * mm, "end": v(1.25, 55.25) * mm});
            skLineSegment(sketch, "E414.1.0.569", {"start": v(125.8, 129.3) * mm, "end": v(1.25, 129.3) * mm});
            skLineSegment(sketch, "E414.1.0.570", {"start": v(250.47, -56.75) * mm, "end": v(133.6, -56.75) * mm});
            skLineSegment(sketch, "E414.1.0.571", {"start": v(254.25, 61.25) * mm, "end": v(129.7, 61.25) * mm});
            skLineSegment(sketch, "E414.1.0.572", {"start": v(254.3, 143.25) * mm, "end": v(129.75, 143.25) * mm});
            skLineSegment(sketch, "E414.1.0.573", {"start": v(-2.7, -128.75) * mm, "end": v(-127.25, -128.75) * mm});
            skLineSegment(sketch, "E414.1.0.574", {"start": v(-2.75, -136.7) * mm, "end": v(-127.3, -136.7) * mm});
            skLineSegment(sketch, "E414.1.0.575", {"start": v(-2.7, -124.75) * mm, "end": v(-127.25, -124.75) * mm});
            skLineSegment(sketch, "E414.1.0.576", {"start": v(254.25, -120.7) * mm, "end": v(129.7, -120.7) * mm});
            skLineSegment(sketch, "E414.1.0.577", {"start": v(254.25, -136.7) * mm, "end": v(129.7, -136.7) * mm});
            skLineSegment(sketch, "E414.1.0.578", {"start": v(246.45, -60.7) * mm, "end": v(137.48, -60.7) * mm});
            skLineSegment(sketch, "E414.1.0.579", {"start": v(125.8, -128.75) * mm, "end": v(1.25, -128.75) * mm});
            skLineSegment(sketch, "E414.1.0.580", {"start": v(117.97, -60.75) * mm, "end": v(9.1, -60.75) * mm});
            skLineSegment(sketch, "E414.1.0.581", {"start": v(125.8, -36.75) * mm, "end": v(1.25, -36.75) * mm});
            skLineSegment(sketch, "E414.1.0.582", {"start": v(125.75, -48.7) * mm, "end": v(1.2, -48.7) * mm});
            skLineSegment(sketch, "E414.1.0.583", {"start": v(125.8, 37.3) * mm, "end": v(1.25, 37.3) * mm});
            skLineSegment(sketch, "E414.1.0.584", {"start": v(125.75, 41.25) * mm, "end": v(1.2, 41.25) * mm});
            skLineSegment(sketch, "E414.1.0.585", {"start": v(125.75, 133.25) * mm, "end": v(1.2, 133.25) * mm});
            skLineSegment(sketch, "E414.1.0.586", {"start": v(125.75, 131.3) * mm, "end": v(1.2, 131.3) * mm});
            skLineSegment(sketch, "E414.1.0.587", {"start": v(254.3, -40.75) * mm, "end": v(129.75, -40.75) * mm});
            skLineSegment(sketch, "E414.1.0.588", {"start": v(254.3, -48.75) * mm, "end": v(129.75, -48.75) * mm});
            skLineSegment(sketch, "E414.1.0.589", {"start": v(246.47, 27.25) * mm, "end": v(137.6, 27.25) * mm});
            skLineSegment(sketch, "E414.1.0.590", {"start": v(254.3, 51.25) * mm, "end": v(129.75, 51.25) * mm});
            skLineSegment(sketch, "E414.1.0.591", {"start": v(254.25, 39.3) * mm, "end": v(129.7, 39.3) * mm});
            skLineSegment(sketch, "E414.1.0.592", {"start": v(254.3, 125.3) * mm, "end": v(129.75, 125.3) * mm});
            skLineSegment(sketch, "E414.1.0.593", {"start": v(254.25, 129.25) * mm, "end": v(129.7, 129.25) * mm});
            skLineSegment(sketch, "E414.1.0.594", {"start": v(125.8, -136.75) * mm, "end": v(1.25, -136.75) * mm});
            skLineSegment(sketch, "E414.1.0.595", {"start": v(117.95, -148.7) * mm, "end": v(8.98, -148.7) * mm});
            skLineSegment(sketch, "E414.1.0.596", {"start": v(254.25, -32.7) * mm, "end": v(129.7, -32.7) * mm});
            skLineSegment(sketch, "E414.1.0.597", {"start": v(254.3, -28.75) * mm, "end": v(129.75, -28.75) * mm});
            skLineSegment(sketch, "E414.1.0.598", {"start": v(113.92, -64.8) * mm, "end": v(13.08, -64.8) * mm});
            skLineSegment(sketch, "E414.1.0.599", {"start": v(116.02, -62.7) * mm, "end": v(11.05, -62.7) * mm});
            skLineSegment(sketch, "E414.1.0.600", {"start": v(125.75, 47.3) * mm, "end": v(1.2, 47.3) * mm});
            skLineSegment(sketch, "E414.1.0.601", {"start": v(125.75, 51.3) * mm, "end": v(1.2, 51.3) * mm});
            skLineSegment(sketch, "E414.1.0.602", {"start": v(242.42, 23.2) * mm, "end": v(141.58, 23.2) * mm});
            skLineSegment(sketch, "E414.1.0.603", {"start": v(244.52, 25.3) * mm, "end": v(139.55, 25.3) * mm});
            skLineSegment(sketch, "E414.1.0.604", {"start": v(254.25, 139.3) * mm, "end": v(129.7, 139.3) * mm});
            skLineSegment(sketch, "E414.1.0.605", {"start": v(254.25, 135.3) * mm, "end": v(129.7, 135.3) * mm});
            skLineSegment(sketch, "E414.1.0.606", {"start": v(125.8, -116.75) * mm, "end": v(1.25, -116.75) * mm});
            skLineSegment(sketch, "E414.1.0.607", {"start": v(125.75, -120.7) * mm, "end": v(1.2, -120.7) * mm});
            skLineSegment(sketch, "E414.1.0.608", {"start": v(244.4, 113.25) * mm, "end": v(139.6, 113.25) * mm});
            skLineSegment(sketch, "E414.1.0.609", {"start": v(125.8, -132.75) * mm, "end": v(1.25, -132.75) * mm});
            skLineSegment(sketch, "E414.1.0.610", {"start": v(125.75, -28.7) * mm, "end": v(1.25, -28.7) * mm});
            skLineSegment(sketch, "E414.1.0.611", {"start": v(113.9, 23.25) * mm, "end": v(13.1, 23.25) * mm});
            skLineSegment(sketch, "E414.1.0.612", {"start": v(254.25, 35.25) * mm, "end": v(129.75, 35.25) * mm});
            skLineSegment(sketch, "E414.1.0.613", {"start": v(125.8, 143.25) * mm, "end": v(1.25, 143.25) * mm});
            skLineSegment(sketch, "E414.1.0.614", {"start": v(115.9, 25.25) * mm, "end": v(11.1, 25.25) * mm});
            skLineSegment(sketch, "E414.1.0.615", {"start": v(125.75, 123.3) * mm, "end": v(1.2, 123.3) * mm});
            skLineSegment(sketch, "E414.1.0.616", {"start": v(121.97, -56.75) * mm, "end": v(5.1, -56.75) * mm});
            skLineSegment(sketch, "E414.1.0.617", {"start": v(124.02, 33.3) * mm, "end": v(3.05, 33.3) * mm});
            skLineSegment(sketch, "E414.1.0.618", {"start": v(125.75, 61.25) * mm, "end": v(1.2, 61.25) * mm});
            skLineSegment(sketch, "E414.1.0.619", {"start": v(244.52, -150.7) * mm, "end": v(139.55, -150.7) * mm});
            skLineSegment(sketch, "E414.1.0.620", {"start": v(254.3, -46.7) * mm, "end": v(129.75, -46.7) * mm});
            skLineSegment(sketch, "E414.1.0.621", {"start": v(250.47, 31.25) * mm, "end": v(133.6, 31.25) * mm});
            skLineSegment(sketch, "E414.1.0.622", {"start": v(254.25, 37.25) * mm, "end": v(129.7, 37.25) * mm});
            skLineSegment(sketch, "E414.1.0.623", {"start": v(252.52, 121.3) * mm, "end": v(131.55, 121.3) * mm});
            skLineSegment(sketch, "E414.1.0.624", {"start": v(120.02, 117.3) * mm, "end": v(7.05, 117.3) * mm});
            skLineSegment(sketch, "E414.1.0.625", {"start": v(125.8, 137.3) * mm, "end": v(1.25, 137.3) * mm});
            skLineSegment(sketch, "E414.1.0.626", {"start": v(125.8, -40.75) * mm, "end": v(1.25, -40.75) * mm});
            skLineSegment(sketch, "E414.1.0.627", {"start": v(254.25, -42.75) * mm, "end": v(129.7, -42.75) * mm});
            skLineSegment(sketch, "E414.1.0.628", {"start": v(254.3, 47.25) * mm, "end": v(129.75, 47.25) * mm});
            skLineSegment(sketch, "E414.1.0.629", {"start": v(246.47, 115.25) * mm, "end": v(137.6, 115.25) * mm});
            skLineSegment(sketch, "E414.1.0.630", {"start": v(114, -153) * mm, "end": v(13, -153) * mm});
            skLineSegment(sketch, "E414.1.0.631", {"start": v(125.75, -32.7) * mm, "end": v(1.2, -32.7) * mm});
            skLineSegment(sketch, "E414.1.0.632", {"start": v(125.75, 139.3) * mm, "end": v(1.2, 139.3) * mm});
            skLineSegment(sketch, "E414.1.0.633", {"start": v(248.4, -146.75) * mm, "end": v(135.53, -146.75) * mm});
            skLineSegment(sketch, "E414.1.0.634", {"start": v(242.5, -65) * mm, "end": v(141.5, -65) * mm});
            skLineSegment(sketch, "E414.1.0.635", {"start": v(254.3, 59.25) * mm, "end": v(129.75, 59.25) * mm});
            skLineSegment(sketch, "E414.1.0.636", {"start": v(254.25, 55.3) * mm, "end": v(129.7, 55.3) * mm});
            skLineSegment(sketch, "E414.1.0.637", {"start": v(115.9, 113.25) * mm, "end": v(11.1, 113.25) * mm});
            skLineSegment(sketch, "E414.1.0.638", {"start": v(125.75, 59.3) * mm, "end": v(1.25, 59.3) * mm});
            skLineSegment(sketch, "E414.1.0.639", {"start": v(242.5, -153) * mm, "end": v(141.5, -153) * mm});
            skLineSegment(sketch, "E414.1.0.640", {"start": v(254.25, -52.7) * mm, "end": v(129.7, -52.7) * mm});
            skLineSegment(sketch, "E414.1.0.641", {"start": v(254.3, 43.25) * mm, "end": v(129.75, 43.25) * mm});
            skLineSegment(sketch, "E414.1.0.642", {"start": v(254.25, 147.3) * mm, "end": v(129.75, 147.3) * mm});
            skLineSegment(sketch, "E414.1.0.643", {"start": v(125.8, -46.7) * mm, "end": v(1.25, -46.7) * mm});
            skLineSegment(sketch, "E414.1.0.644", {"start": v(121.95, 31.3) * mm, "end": v(4.98, 31.3) * mm});
            skLineSegment(sketch, "E414.1.0.645", {"start": v(250.45, 119.3) * mm, "end": v(133.48, 119.3) * mm});
            skLineSegment(sketch, "E414.1.0.646", {"start": v(125.75, -42.75) * mm, "end": v(1.2, -42.75) * mm});
            skLineSegment(sketch, "E414.1.0.647", {"start": v(-2.7, 53.3) * mm, "end": v(-127.25, 53.3) * mm});
            skLineSegment(sketch, "E414.1.0.648", {"start": v(-2.75, 123.3) * mm, "end": v(-127.3, 123.3) * mm});
            skLineSegment(sketch, "E414.1.0.649", {"start": v(-2.7, -38.7) * mm, "end": v(-127.25, -38.7) * mm});
            skLineSegment(sketch, "E414.1.0.650", {"start": v(-131.25, -116.7) * mm, "end": v(-255.75, -116.7) * mm});
            skLineSegment(sketch, "E414.1.0.651", {"start": v(-2.7, -28.75) * mm, "end": v(-127.25, -28.75) * mm});
            skLineSegment(sketch, "E414.1.0.652", {"start": v(-2.7, 59.25) * mm, "end": v(-127.25, 59.25) * mm});
            skLineSegment(sketch, "E414.1.0.653", {"start": v(-2.75, -52.75) * mm, "end": v(-127.25, -52.75) * mm});
            skLineSegment(sketch, "E414.1.0.654", {"start": v(-131.25, 57.25) * mm, "end": v(-255.8, 57.25) * mm});
            skLineSegment(sketch, "E414.1.0.655", {"start": v(-137.1, -58.75) * mm, "end": v(-249.97, -58.75) * mm});
            skLineSegment(sketch, "E414.1.0.656", {"start": v(-135.03, 31.25) * mm, "end": v(-251.9, 31.25) * mm});
            skLineSegment(sketch, "E414.1.0.657", {"start": v(-131.25, 147.3) * mm, "end": v(-255.75, 147.3) * mm});
            skLineSegment(sketch, "E414.1.0.658", {"start": v(-132.98, 121.3) * mm, "end": v(-253.95, 121.3) * mm});
            skLineSegment(sketch, "E414.1.0.659", {"start": v(-8.6, 29.25) * mm, "end": v(-121.47, 29.25) * mm});
            skLineSegment(sketch, "E414.1.0.660", {"start": v(-140.98, 25.3) * mm, "end": v(-245.95, 25.3) * mm});
            skLineSegment(sketch, "E414.1.0.661", {"start": v(-141.1, -62.75) * mm, "end": v(-245.9, -62.75) * mm});
            skLineSegment(sketch, "E414.1.0.662", {"start": v(-2.7, 145.3) * mm, "end": v(-127.25, 145.3) * mm});
            skLineSegment(sketch, "E414.1.0.663", {"start": v(-6.55, 119.3) * mm, "end": v(-123.52, 119.3) * mm});
            skLineSegment(sketch, "E414.1.0.664", {"start": v(-131.25, -120.7) * mm, "end": v(-255.8, -120.7) * mm});
            skLineSegment(sketch, "E414.1.0.665", {"start": v(-131.2, -126.7) * mm, "end": v(-255.75, -126.7) * mm});
            skLineSegment(sketch, "E414.1.0.666", {"start": v(-2.7, -44.75) * mm, "end": v(-127.25, -44.75) * mm});
            skLineSegment(sketch, "E414.1.0.667", {"start": v(-131.2, -44.75) * mm, "end": v(-255.75, -44.75) * mm});
            skLineSegment(sketch, "E414.1.0.668", {"start": v(-131.25, -38.75) * mm, "end": v(-255.8, -38.75) * mm});
            skLineSegment(sketch, "E414.1.0.669", {"start": v(-2.7, 49.3) * mm, "end": v(-127.25, 49.3) * mm});
            skLineSegment(sketch, "E414.1.0.670", {"start": v(-139.03, 115.25) * mm, "end": v(-247.9, 115.25) * mm});
            skLineSegment(sketch, "E414.1.0.671", {"start": v(-2.75, -126.75) * mm, "end": v(-127.3, -126.75) * mm});
            skLineSegment(sketch, "E414.1.0.672", {"start": v(254.3, -120.75) * mm, "end": v(129.75, -120.75) * mm});
            skLineSegment(sketch, "E414.1.0.673", {"start": v(254.3, -136.75) * mm, "end": v(129.75, -136.75) * mm});
            skLineSegment(sketch, "E414.1.0.674", {"start": v(121.95, -144.7) * mm, "end": v(4.98, -144.7) * mm});
            skLineSegment(sketch, "E414.1.0.675", {"start": v(125.75, -38.75) * mm, "end": v(1.2, -38.75) * mm});
            skLineSegment(sketch, "E414.1.0.676", {"start": v(125.8, 49.3) * mm, "end": v(1.25, 49.3) * mm});
            skLineSegment(sketch, "E414.1.0.677", {"start": v(119.9, 117.25) * mm, "end": v(7.03, 117.25) * mm});
            skLineSegment(sketch, "E414.1.0.678", {"start": v(250.45, -56.7) * mm, "end": v(133.48, -56.7) * mm});
            skLineSegment(sketch, "E414.1.0.679", {"start": v(254.25, -50.75) * mm, "end": v(129.7, -50.75) * mm});
            skLineSegment(sketch, "E414.1.0.680", {"start": v(254.25, 49.25) * mm, "end": v(129.7, 49.25) * mm});
            skLineSegment(sketch, "E414.1.0.681", {"start": v(252.52, 33.3) * mm, "end": v(131.55, 33.3) * mm});
            skLineSegment(sketch, "E414.1.0.682", {"start": v(254.3, 137.3) * mm, "end": v(129.75, 137.3) * mm});
            skLineSegment(sketch, "E414.1.0.683", {"start": v(248.52, 117.3) * mm, "end": v(135.55, 117.3) * mm});
            skLineSegment(sketch, "E414.1.0.684", {"start": v(123.9, 121.25) * mm, "end": v(3.03, 121.25) * mm});
            skLineSegment(sketch, "E414.1.0.685", {"start": v(244.4, -150.75) * mm, "end": v(139.6, -150.75) * mm});
            skLineSegment(sketch, "E414.1.0.686", {"start": v(254.3, -44.75) * mm, "end": v(129.75, -44.75) * mm});
            skLineSegment(sketch, "E414.1.0.687", {"start": v(254.25, 59.3) * mm, "end": v(129.75, 59.3) * mm});
            skLineSegment(sketch, "E414.1.0.688", {"start": v(125.8, -44.75) * mm, "end": v(1.25, -44.75) * mm});
            skLineSegment(sketch, "E414.1.0.689", {"start": v(-143.1, 111.25) * mm, "end": v(-141.1, 113.25) * mm});
            skLineSegment(sketch, "E414.1.0.690", {"start": v(-115.5, 111) * mm, "end": v(-127.5, 123) * mm});
            skLineSegment(sketch, "E414.1.0.691", {"start": v(-244, 23) * mm, "end": v(-256, 35) * mm});
            skLineSegment(sketch, "E414.1.0.692", {"start": v(-131.2, -46.7) * mm, "end": v(-255.75, -46.7) * mm});
            skLineSegment(sketch, "E414.1.0.693", {"start": v(-14.6, 111.25) * mm, "end": v(-12.6, 113.25) * mm});
            skLineSegment(sketch, "E414.1.0.694", {"start": v(-115.5, -153) * mm, "end": v(-127.5, -141) * mm});
            skLineSegment(sketch, "E414.1.0.695", {"start": v(-244, -153) * mm, "end": v(-256, -141) * mm});
            skLineSegment(sketch, "E414.1.0.696", {"start": v(-249.95, -58.7) * mm, "end": v(-251.9, -56.75) * mm});
            skLineSegment(sketch, "E414.1.0.697", {"start": v(-10.55, 27.3) * mm, "end": v(-8.6, 29.25) * mm});
            skLineSegment(sketch, "E414.1.0.698", {"start": v(-14.5, 23) * mm, "end": v(-2.5, 35) * mm});
            skLineSegment(sketch, "E414.1.0.699", {"start": v(-117.45, 113.3) * mm, "end": v(-119.4, 115.25) * mm});
            skLineSegment(sketch, "E414.1.0.700", {"start": v(-244, 111) * mm, "end": v(-256, 123) * mm});
            skLineSegment(sketch, "E414.1.0.701", {"start": v(-245.95, 113.3) * mm, "end": v(-247.9, 115.25) * mm});
            skLineSegment(sketch, "E414.1.0.702", {"start": v(-143, -65) * mm, "end": v(-131, -53) * mm});
            skLineSegment(sketch, "E414.1.0.703", {"start": v(-139.03, 27.25) * mm, "end": v(-136.98, 29.3) * mm});
            skLineSegment(sketch, "E414.1.0.704", {"start": v(246.45, 115.3) * mm, "end": v(248.4, 117.25) * mm});
            skLineSegment(sketch, "E414.1.0.705", {"start": v(-10.55, -148.7) * mm, "end": v(-8.6, -146.75) * mm});
            skLineSegment(sketch, "E414.1.0.706", {"start": v(113.92, 111.2) * mm, "end": v(116.02, 113.3) * mm});
            skLineSegment(sketch, "E414.1.0.707", {"start": v(13, 111) * mm, "end": v(1, 123) * mm});
            skLineSegment(sketch, "E414.1.0.708", {"start": v(139.55, 113.3) * mm, "end": v(137.6, 115.25) * mm});
            skLineSegment(sketch, "E414.1.0.709", {"start": v(117.95, 115.3) * mm, "end": v(119.9, 117.25) * mm});
            skLineSegment(sketch, "E414.1.0.710", {"start": v(-14.5, 111) * mm, "end": v(-2.5, 123) * mm});
            skLineSegment(sketch, "E414.1.0.711", {"start": v(13.1, 111.25) * mm, "end": v(11.1, 113.25) * mm});
            skLineSegment(sketch, "E414.1.0.712", {"start": v(114, -153) * mm, "end": v(126, -141) * mm});
            skLineSegment(sketch, "E414.1.0.713", {"start": v(242.5, -65) * mm, "end": v(254.5, -53) * mm});
            skLineSegment(sketch, "E414.1.0.714", {"start": v(-143, 111) * mm, "end": v(-131, 123) * mm});
            skLineSegment(sketch, "E414.1.0.715", {"start": v(11.05, 113.3) * mm, "end": v(9.1, 115.25) * mm});
            skLineSegment(sketch, "E414.1.0.716", {"start": v(13, -153) * mm, "end": v(1, -141) * mm});
            skLineSegment(sketch, "E414.1.0.717", {"start": v(-14.5, -153) * mm, "end": v(-2.5, -141) * mm});
            skLineSegment(sketch, "E414.1.0.718", {"start": v(141.5, -65) * mm, "end": v(129.5, -53) * mm});
            skLineSegment(sketch, "E414.1.0.719", {"start": v(242.4, 111.25) * mm, "end": v(244.4, 113.25) * mm});
            skLineSegment(sketch, "E414.1.0.720", {"start": v(117.95, -148.7) * mm, "end": v(119.9, -146.75) * mm});
            skLineSegment(sketch, "E414.1.0.721", {"start": v(114, -65) * mm, "end": v(126, -53) * mm});
            skLineSegment(sketch, "E414.1.0.722", {"start": v(141.5, 23) * mm, "end": v(129.5, 35) * mm});
            skLineSegment(sketch, "E414.1.0.723", {"start": v(-115.4, 111.25) * mm, "end": v(-117.4, 113.25) * mm});
            skLineSegment(sketch, "E414.1.0.724", {"start": v(113.9, 111.25) * mm, "end": v(115.9, 113.25) * mm});
            skLineSegment(sketch, "E414.1.0.725", {"start": v(246.45, 27.3) * mm, "end": v(248.4, 29.25) * mm});
            skLineSegment(sketch, "E414.1.0.726", {"start": v(246.47, 115.25) * mm, "end": v(248.52, 117.3) * mm});
            skLineSegment(sketch, "E414.1.0.727", {"start": v(117.97, 27.25) * mm, "end": v(120.02, 29.3) * mm});
            skLineSegment(sketch, "E414.1.0.728", {"start": v(242.5, 111) * mm, "end": v(254.5, 123) * mm});
            skLineSegment(sketch, "E414.1.0.729", {"start": v(114, 23) * mm, "end": v(126, 35) * mm});
            skLineSegment(sketch, "E414.1.0.730", {"start": v(242.42, 111.2) * mm, "end": v(244.52, 113.3) * mm});
            skLineSegment(sketch, "E414.1.0.731", {"start": v(141.5, 111) * mm, "end": v(129.5, 123) * mm});
            skLineSegment(sketch, "E414.1.0.732", {"start": v(141.58, 111.2) * mm, "end": v(137.48, 115.3) * mm});
            skLineSegment(sketch, "E414.1.0.733", {"start": v(-139.03, -148.75) * mm, "end": v(-136.98, -146.7) * mm});
            skLineSegment(sketch, "E414.1.0.734", {"start": v(-143, 23) * mm, "end": v(-131, 35) * mm});
            skLineSegment(sketch, "E414.1.0.735", {"start": v(-139.05, 115.3) * mm, "end": v(-137.1, 117.25) * mm});
            skLineSegment(sketch, "E414.1.0.736", {"start": v(-14.5, -65) * mm, "end": v(-2.5, -53) * mm});
            skLineSegment(sketch, "E414.1.0.737", {"start": v(-14.58, 111.2) * mm, "end": v(-12.48, 113.3) * mm});
            skLineSegment(sketch, "E414.1.0.738", {"start": v(-143, -153) * mm, "end": v(-131, -141) * mm});
            skLineSegment(sketch, "E414.1.0.739", {"start": v(-243.9, 111.25) * mm, "end": v(-245.9, 113.25) * mm});
            skLineSegment(sketch, "E414.1.0.740", {"start": v(-143.08, 111.2) * mm, "end": v(-140.98, 113.3) * mm});
            skLineSegment(sketch, "E414.1.0.741", {"start": v(-115.42, 111.2) * mm, "end": v(-119.52, 115.3) * mm});
            skLineSegment(sketch, "E414.1.0.742", {"start": v(-244, -65) * mm, "end": v(-256, -53) * mm});
            skLineSegment(sketch, "E414.1.0.743", {"start": v(-10.53, 27.25) * mm, "end": v(-8.48, 29.3) * mm});
            skLineSegment(sketch, "E414.1.0.744", {"start": v(-139.05, -148.7) * mm, "end": v(-137.1, -146.75) * mm});
            skLineSegment(sketch, "E414.1.0.745", {"start": v(-10.55, 115.3) * mm, "end": v(-8.6, 117.25) * mm});
            skLineSegment(sketch, "E414.1.0.746", {"start": v(-139.05, 27.3) * mm, "end": v(-137.1, 29.25) * mm});
            skLineSegment(sketch, "E414.1.0.747", {"start": v(-10.53, -148.75) * mm, "end": v(-8.48, -146.7) * mm});
            skLineSegment(sketch, "E414.1.0.748", {"start": v(-115.5, -65) * mm, "end": v(-127.5, -53) * mm});
            skLineSegment(sketch, "E414.1.0.749", {"start": v(-243.92, 111.2) * mm, "end": v(-248.02, 115.3) * mm});
            skLineSegment(sketch, "E414.1.0.750", {"start": v(-10.53, 115.25) * mm, "end": v(-8.48, 117.3) * mm});
            skLineSegment(sketch, "E414.1.0.751", {"start": v(-139.03, 115.25) * mm, "end": v(-136.98, 117.3) * mm});
            skLineSegment(sketch, "E414.1.0.752", {"start": v(117.97, 115.25) * mm, "end": v(120.02, 117.3) * mm});
            skLineSegment(sketch, "E414.1.0.753", {"start": v(117.95, 27.3) * mm, "end": v(119.9, 29.25) * mm});
            skLineSegment(sketch, "E414.1.0.754", {"start": v(114, 111) * mm, "end": v(126, 123) * mm});
            skLineSegment(sketch, "E414.1.0.755", {"start": v(141.6, 111.25) * mm, "end": v(139.6, 113.25) * mm});
            skLineSegment(sketch, "E414.1.0.756", {"start": v(13.08, 111.2) * mm, "end": v(8.98, 115.3) * mm});
            skLineSegment(sketch, "E414.1.0.757", {"start": v(246.47, -148.75) * mm, "end": v(248.52, -146.7) * mm});
            skLineSegment(sketch, "E414.1.0.758", {"start": v(135.55, -58.7) * mm, "end": v(133.6, -56.75) * mm});
            skLineSegment(sketch, "E414.1.0.759", {"start": v(117.97, -148.75) * mm, "end": v(120.02, -146.7) * mm});
            skLineSegment(sketch, "E414.1.0.760", {"start": v(242.5, -153) * mm, "end": v(254.5, -141) * mm});
            skLineSegment(sketch, "E414.1.0.761", {"start": v(141.5, -153) * mm, "end": v(129.5, -141) * mm});
            skLineSegment(sketch, "E414.1.0.762", {"start": v(246.47, 27.25) * mm, "end": v(248.52, 29.3) * mm});
            skLineSegment(sketch, "E414.1.0.763", {"start": v(242.5, 23) * mm, "end": v(254.5, 35) * mm});
            skLineSegment(sketch, "E414.1.0.764", {"start": v(13, 23) * mm, "end": v(1, 35) * mm});
            skLineSegment(sketch, "E414.1.0.765", {"start": v(-14.58, -152.8) * mm, "end": v(-12.48, -150.7) * mm});
            skLineSegment(sketch, "E414.1.0.766", {"start": v(-14.6, -152.75) * mm, "end": v(-12.6, -150.75) * mm});
            skLineSegment(sketch, "E414.1.0.767", {"start": v(-143.1, -152.75) * mm, "end": v(-141.1, -150.75) * mm});
            skLineSegment(sketch, "E414.1.0.768", {"start": v(-249.97, -58.75) * mm, "end": v(-252.02, -56.7) * mm});
            skLineSegment(sketch, "E414.1.0.769", {"start": v(-14.58, -64.8) * mm, "end": v(-12.48, -62.7) * mm});
            skLineSegment(sketch, "E414.1.0.770", {"start": v(-14.6, -64.75) * mm, "end": v(-12.6, -62.75) * mm});
            skLineSegment(sketch, "E414.1.0.771", {"start": v(-115.5, 23) * mm, "end": v(-127.5, 35) * mm});
            skLineSegment(sketch, "E414.1.0.772", {"start": v(-245.95, -62.7) * mm, "end": v(-247.9, -60.75) * mm});
            skLineSegment(sketch, "E414.1.0.773", {"start": v(-115.42, 23.2) * mm, "end": v(-119.52, 27.3) * mm});
            skLineSegment(sketch, "E414.1.0.774", {"start": v(-243.92, -152.8) * mm, "end": v(-248.02, -148.7) * mm});
            skLineSegment(sketch, "E414.1.0.775", {"start": v(-121.45, -58.7) * mm, "end": v(-123.4, -56.75) * mm});
            skLineSegment(sketch, "E414.1.0.776", {"start": v(-14.6, 23.25) * mm, "end": v(-12.6, 25.25) * mm});
            skLineSegment(sketch, "E414.1.0.777", {"start": v(-115.4, -64.75) * mm, "end": v(-117.4, -62.75) * mm});
            skLineSegment(sketch, "E414.1.0.778", {"start": v(-117.45, -150.7) * mm, "end": v(-119.4, -148.75) * mm});
            skLineSegment(sketch, "E414.1.0.779", {"start": v(-115.42, -64.8) * mm, "end": v(-119.52, -60.7) * mm});
            skLineSegment(sketch, "E414.1.0.780", {"start": v(-243.9, -152.75) * mm, "end": v(-245.9, -150.75) * mm});
            skLineSegment(sketch, "E414.1.0.781", {"start": v(-139.05, -60.7) * mm, "end": v(-137.1, -58.75) * mm});
            skLineSegment(sketch, "E414.1.0.782", {"start": v(-245.95, 25.3) * mm, "end": v(-247.9, 27.25) * mm});
            skLineSegment(sketch, "E414.1.0.783", {"start": v(246.45, -148.7) * mm, "end": v(248.4, -146.75) * mm});
            skLineSegment(sketch, "E414.1.0.784", {"start": v(-10.53, -60.75) * mm, "end": v(-8.48, -58.7) * mm});
            skLineSegment(sketch, "E414.1.0.785", {"start": v(135.53, -58.75) * mm, "end": v(133.48, -56.7) * mm});
            skLineSegment(sketch, "E414.1.0.786", {"start": v(113.9, -64.75) * mm, "end": v(115.9, -62.75) * mm});
            skLineSegment(sketch, "E414.1.0.787", {"start": v(242.4, 23.25) * mm, "end": v(244.4, 25.25) * mm});
            skLineSegment(sketch, "E414.1.0.788", {"start": v(-14.58, 23.2) * mm, "end": v(-12.48, 25.3) * mm});
            skLineSegment(sketch, "E414.1.0.789", {"start": v(-115.4, 23.25) * mm, "end": v(-117.4, 25.25) * mm});
            skLineSegment(sketch, "E414.1.0.790", {"start": v(11.05, 25.3) * mm, "end": v(9.1, 27.25) * mm});
            skLineSegment(sketch, "E414.1.0.791", {"start": v(-243.9, 23.25) * mm, "end": v(-245.9, 25.25) * mm});
            skLineSegment(sketch, "E414.1.0.792", {"start": v(113.92, -152.8) * mm, "end": v(116.02, -150.7) * mm});
            skLineSegment(sketch, "E414.1.0.793", {"start": v(242.42, -64.8) * mm, "end": v(244.52, -62.7) * mm});
            skLineSegment(sketch, "E414.1.0.794", {"start": v(242.4, -152.75) * mm, "end": v(244.4, -150.75) * mm});
            skLineSegment(sketch, "E414.1.0.795", {"start": v(113.9, 23.25) * mm, "end": v(115.9, 25.25) * mm});
            skLineSegment(sketch, "E414.1.0.796", {"start": v(242.42, -152.8) * mm, "end": v(244.52, -150.7) * mm});
            skLineSegment(sketch, "E414.1.0.797", {"start": v(141.58, -152.8) * mm, "end": v(137.48, -148.7) * mm});
            skLineSegment(sketch, "E414.1.0.798", {"start": v(246.45, -60.7) * mm, "end": v(248.4, -58.75) * mm});
            skLineSegment(sketch, "E414.1.0.799", {"start": v(141.6, -64.75) * mm, "end": v(139.6, -62.75) * mm});
            skLineSegment(sketch, "E414.1.0.800", {"start": v(13.1, -152.75) * mm, "end": v(11.1, -150.75) * mm});
            skLineSegment(sketch, "E414.1.0.801", {"start": v(242.42, 23.2) * mm, "end": v(244.52, 25.3) * mm});
            skLineSegment(sketch, "E414.1.0.802", {"start": v(113.92, -64.8) * mm, "end": v(116.02, -62.7) * mm});
            skLineSegment(sketch, "E414.1.0.803", {"start": v(139.55, -150.7) * mm, "end": v(137.6, -148.75) * mm});
            skLineSegment(sketch, "E414.1.0.804", {"start": v(139.55, -62.7) * mm, "end": v(137.6, -60.75) * mm});
            skLineSegment(sketch, "E414.1.0.805", {"start": v(11.05, -150.7) * mm, "end": v(9.1, -148.75) * mm});
            skLineSegment(sketch, "E414.1.0.806", {"start": v(13, -65) * mm, "end": v(1, -53) * mm});
            skLineSegment(sketch, "E414.1.0.807", {"start": v(117.95, -60.7) * mm, "end": v(119.9, -58.75) * mm});
            skLineSegment(sketch, "E414.1.0.808", {"start": v(141.6, 23.25) * mm, "end": v(139.6, 25.25) * mm});
            skLineSegment(sketch, "E414.1.0.809", {"start": v(13.1, -64.75) * mm, "end": v(11.1, -62.75) * mm});
            skLineSegment(sketch, "E414.1.0.810", {"start": v(113.92, 23.2) * mm, "end": v(116.02, 25.3) * mm});
            skLineSegment(sketch, "E414.1.0.811", {"start": v(242.4, -64.75) * mm, "end": v(244.4, -62.75) * mm});
            skLineSegment(sketch, "E414.1.0.812", {"start": v(139.55, 25.3) * mm, "end": v(137.6, 27.25) * mm});
            skLineSegment(sketch, "E414.1.0.813", {"start": v(113.9, -152.75) * mm, "end": v(115.9, -150.75) * mm});
            skLineSegment(sketch, "E414.1.0.814", {"start": v(11.05, -62.7) * mm, "end": v(9.1, -60.75) * mm});
            skLineSegment(sketch, "E414.1.0.815", {"start": v(13.08, 23.2) * mm, "end": v(8.98, 27.3) * mm});
            skLineSegment(sketch, "E414.1.0.816", {"start": v(-143.08, -64.8) * mm, "end": v(-140.98, -62.7) * mm});
            skLineSegment(sketch, "E414.1.0.817", {"start": v(-243.9, -64.75) * mm, "end": v(-245.9, -62.75) * mm});
            skLineSegment(sketch, "E414.1.0.818", {"start": v(-115.4, -152.75) * mm, "end": v(-117.4, -150.75) * mm});
            skLineSegment(sketch, "E414.1.0.819", {"start": v(-143.08, 23.2) * mm, "end": v(-140.98, 25.3) * mm});
            skLineSegment(sketch, "E414.1.0.820", {"start": v(-117.45, 25.3) * mm, "end": v(-119.4, 27.25) * mm});
            skLineSegment(sketch, "E414.1.0.821", {"start": v(-143.08, -152.8) * mm, "end": v(-140.98, -150.7) * mm});
            skLineSegment(sketch, "E414.1.0.822", {"start": v(-121.47, -58.75) * mm, "end": v(-123.52, -56.7) * mm});
            skLineSegment(sketch, "E414.1.0.823", {"start": v(-117.45, -62.7) * mm, "end": v(-119.4, -60.75) * mm});
            skLineSegment(sketch, "E414.1.0.824", {"start": v(-10.55, -60.7) * mm, "end": v(-8.6, -58.75) * mm});
            skLineSegment(sketch, "E414.1.0.825", {"start": v(-243.92, -64.8) * mm, "end": v(-248.02, -60.7) * mm});
            skLineSegment(sketch, "E414.1.0.826", {"start": v(-139.03, -60.75) * mm, "end": v(-136.98, -58.7) * mm});
            skLineSegment(sketch, "E414.1.0.827", {"start": v(-243.92, 23.2) * mm, "end": v(-248.02, 27.3) * mm});
            skLineSegment(sketch, "E414.1.0.828", {"start": v(-245.95, -150.7) * mm, "end": v(-247.9, -148.75) * mm});
            skLineSegment(sketch, "E414.1.0.829", {"start": v(-115.42, -152.8) * mm, "end": v(-119.52, -148.7) * mm});
            skLineSegment(sketch, "E414.1.0.830", {"start": v(-143.1, 23.25) * mm, "end": v(-141.1, 25.25) * mm});
            skLineSegment(sketch, "E414.1.0.831", {"start": v(-143.1, -64.75) * mm, "end": v(-141.1, -62.75) * mm});
            skLineSegment(sketch, "E414.1.0.832", {"start": v(13.1, 23.25) * mm, "end": v(11.1, 25.25) * mm});
            skLineSegment(sketch, "E414.1.0.833", {"start": v(246.47, -60.75) * mm, "end": v(248.52, -58.7) * mm});
            skLineSegment(sketch, "E414.1.0.834", {"start": v(141.6, -152.75) * mm, "end": v(139.6, -150.75) * mm});
            skLineSegment(sketch, "E414.1.0.835", {"start": v(13.08, -152.8) * mm, "end": v(8.98, -148.7) * mm});
            skLineSegment(sketch, "E414.1.0.836", {"start": v(7.05, -58.7) * mm, "end": v(5.1, -56.75) * mm});
            skLineSegment(sketch, "E414.1.0.837", {"start": v(141.58, -64.8) * mm, "end": v(137.48, -60.7) * mm});
            skLineSegment(sketch, "E414.1.0.838", {"start": v(117.97, -60.75) * mm, "end": v(120.02, -58.7) * mm});
            skLineSegment(sketch, "E414.1.0.839", {"start": v(254.25, 63.3) * mm, "end": v(254.25, 65) * mm});
            skLineSegment(sketch, "E414.1.0.840", {"start": v(141.58, 23.2) * mm, "end": v(137.48, 27.3) * mm});
            skLineSegment(sketch, "E414.1.0.841", {"start": v(13.08, -64.8) * mm, "end": v(8.98, -60.7) * mm});
            skLineSegment(sketch, "E414.1.0.842", {"start": v(-249.95, -146.7) * mm, "end": v(-251.9, -144.75) * mm});
            skLineSegment(sketch, "E414.1.0.843", {"start": v(7.03, -58.75) * mm, "end": v(4.98, -56.7) * mm});
            skLineSegment(sketch, "E414.1.0.844", {"start": v(254.3, 63.25) * mm, "end": v(254.3, 65) * mm});
            skLineSegment(sketch, "E414.1.0.845", {"start": v(250.47, -56.75) * mm, "end": v(252.52, -54.7) * mm});
            skLineSegment(sketch, "E414.1.0.846", {"start": v(254.5, -53) * mm, "end": v(254.5, -23) * mm});
            skLineSegment(sketch, "E414.1.0.847", {"start": v(-249.97, 117.25) * mm, "end": v(-252.02, 119.3) * mm});
            skLineSegment(sketch, "E414.1.0.848", {"start": v(-256, -141) * mm, "end": v(-256, -111) * mm});
            skLineSegment(sketch, "E414.1.0.849", {"start": v(-249.95, 117.3) * mm, "end": v(-251.9, 119.25) * mm});
            skLineSegment(sketch, "E414.1.0.850", {"start": v(-249.97, -146.75) * mm, "end": v(-252.02, -144.7) * mm});
            skLineSegment(sketch, "E414.1.0.851", {"start": v(-256, 35) * mm, "end": v(-256, 65) * mm});
            skLineSegment(sketch, "E414.1.0.852", {"start": v(-121.45, 29.3) * mm, "end": v(-123.4, 31.25) * mm});
            skLineSegment(sketch, "E414.1.0.853", {"start": v(-256, -53) * mm, "end": v(-256, -23) * mm});
            skLineSegment(sketch, "E414.1.0.854", {"start": v(-131.25, -24.7) * mm, "end": v(-131.25, -23) * mm});
            skLineSegment(sketch, "E414.1.0.855", {"start": v(250.45, -56.7) * mm, "end": v(252.4, -54.75) * mm});
            skLineSegment(sketch, "E414.1.0.856", {"start": v(1, -53) * mm, "end": v(1, -23) * mm});
            skLineSegment(sketch, "E414.1.0.857", {"start": v(126, -53) * mm, "end": v(126, -23) * mm});
            skLineSegment(sketch, "E414.1.0.858", {"start": v(129.5, 35) * mm, "end": v(129.5, 65) * mm});
            skLineSegment(sketch, "E414.1.0.859", {"start": v(254.5, 35) * mm, "end": v(254.5, 65) * mm});
            skLineSegment(sketch, "E414.1.0.860", {"start": v(-2.75, 151.3) * mm, "end": v(-2.75, 153) * mm});
            skLineSegment(sketch, "E414.1.0.861", {"start": v(-121.47, 117.25) * mm, "end": v(-123.52, 119.3) * mm});
            skLineSegment(sketch, "E414.1.0.862", {"start": v(1.25, -26.7) * mm, "end": v(1.25, -24.75) * mm});
            skLineSegment(sketch, "E414.1.0.863", {"start": v(129.5, -141) * mm, "end": v(129.5, -111) * mm});
            skLineSegment(sketch, "E414.1.0.864", {"start": v(125.8, -28.75) * mm, "end": v(125.8, -26.7) * mm});
            skLineSegment(sketch, "E414.1.0.865", {"start": v(-2.75, -112.7) * mm, "end": v(-2.75, -111) * mm});
            skLineSegment(sketch, "E414.1.0.866", {"start": v(125.75, -24.7) * mm, "end": v(125.75, -23) * mm});
            skLineSegment(sketch, "E414.1.0.867", {"start": v(1, 123) * mm, "end": v(1, 153) * mm});
            skLineSegment(sketch, "E414.1.0.868", {"start": v(125.75, 63.3) * mm, "end": v(125.75, 65) * mm});
            skLineSegment(sketch, "E414.1.0.869", {"start": v(129.7, -26.75) * mm, "end": v(129.7, -24.7) * mm});
            skLineSegment(sketch, "E414.1.0.870", {"start": v(254.3, -52.7) * mm, "end": v(254.3, -50.7) * mm});
            skLineSegment(sketch, "E414.1.0.871", {"start": v(126, -141) * mm, "end": v(126, -111) * mm});
            skLineSegment(sketch, "E414.1.0.872", {"start": v(1, -141) * mm, "end": v(1, -111) * mm});
            skLineSegment(sketch, "E414.1.0.873", {"start": v(129.5, -53) * mm, "end": v(129.5, -23) * mm});
            skLineSegment(sketch, "E414.1.0.874", {"start": v(-253.95, -54.7) * mm, "end": v(-255.75, -52.9) * mm});
            skLineSegment(sketch, "E414.1.0.875", {"start": v(-2.75, -24.7) * mm, "end": v(-2.75, -23) * mm});
            skLineSegment(sketch, "E414.1.0.876", {"start": v(-2.7, -23) * mm, "end": v(-2.75, -23) * mm});
            skLineSegment(sketch, "E414.1.0.877", {"start": v(-127.3, -26.75) * mm, "end": v(-127.3, -24.7) * mm});
            skLineSegment(sketch, "E414.1.0.878", {"start": v(-121.47, -146.75) * mm, "end": v(-123.52, -144.7) * mm});
            skLineSegment(sketch, "E414.1.0.879", {"start": v(-255.75, -26.7) * mm, "end": v(-255.75, -24.75) * mm});
            skLineSegment(sketch, "E414.1.0.880", {"start": v(-127.5, -141) * mm, "end": v(-127.5, -111) * mm});
            skLineSegment(sketch, "E414.1.0.881", {"start": v(-121.45, -146.7) * mm, "end": v(-123.4, -144.75) * mm});
            skLineSegment(sketch, "E414.1.0.882", {"start": v(-2.7, -112.75) * mm, "end": v(-2.7, -111) * mm});
            skLineSegment(sketch, "E414.1.0.883", {"start": v(-121.47, 29.25) * mm, "end": v(-123.52, 31.3) * mm});
            skLineSegment(sketch, "E414.1.0.884", {"start": v(-2.5, -53) * mm, "end": v(-2.5, -23) * mm});
            skLineSegment(sketch, "E414.1.0.885", {"start": v(-256, 123) * mm, "end": v(-256, 153) * mm});
            skLineSegment(sketch, "E414.1.0.886", {"start": v(-127.3, 61.25) * mm, "end": v(-127.3, 63.3) * mm});
            skLineSegment(sketch, "E414.1.0.887", {"start": v(-255.8, 61.25) * mm, "end": v(-255.8, 63.3) * mm});
            skLineSegment(sketch, "E414.1.0.888", {"start": v(-2.7, 151.25) * mm, "end": v(-2.7, 153) * mm});
            skLineSegment(sketch, "E414.1.0.889", {"start": v(-121.45, 117.3) * mm, "end": v(-123.4, 119.25) * mm});
            skLineSegment(sketch, "E414.1.0.890", {"start": v(-255.8, -26.75) * mm, "end": v(-255.8, -24.7) * mm});
            skLineSegment(sketch, "E414.1.0.891", {"start": v(-2.7, -24.75) * mm, "end": v(-2.7, -23) * mm});
            skLineSegment(sketch, "E414.1.0.892", {"start": v(-127.5, 35) * mm, "end": v(-127.5, 65) * mm});
            skLineSegment(sketch, "E414.1.0.893", {"start": v(-131.25, -28.7) * mm, "end": v(-131.25, -26.75) * mm});
            skLineSegment(sketch, "E414.1.0.894", {"start": v(-131, 35) * mm, "end": v(-131, 65) * mm});
            skLineSegment(sketch, "E414.1.0.895", {"start": v(-2.5, 123) * mm, "end": v(-2.5, 153) * mm});
            skLineSegment(sketch, "E414.1.0.896", {"start": v(-127.5, 123) * mm, "end": v(-127.5, 153) * mm});
            skLineSegment(sketch, "E414.1.0.897", {"start": v(-255.75, 61.3) * mm, "end": v(-255.75, 63.25) * mm});
            skLineSegment(sketch, "E414.1.0.898", {"start": v(-253.97, 121.25) * mm, "end": v(-255.8, 123.08) * mm});
            skLineSegment(sketch, "E414.1.0.899", {"start": v(-131.25, 151.3) * mm, "end": v(-131.25, 153) * mm});
            skLineSegment(sketch, "E414.1.0.900", {"start": v(-131, -53) * mm, "end": v(-131, -23) * mm});
            skLineSegment(sketch, "E414.1.0.901", {"start": v(125.75, -28.7) * mm, "end": v(125.75, -26.75) * mm});
            skLineSegment(sketch, "E414.1.0.902", {"start": v(129.75, -26.7) * mm, "end": v(129.75, -24.75) * mm});
            skLineSegment(sketch, "E414.1.0.903", {"start": v(-2.7, -28.75) * mm, "end": v(-2.7, -26.7) * mm});
            skLineSegment(sketch, "E414.1.0.904", {"start": v(-2.7, -111) * mm, "end": v(-2.75, -111) * mm});
            skLineSegment(sketch, "E414.1.0.905", {"start": v(1.2, -26.75) * mm, "end": v(1.2, -24.7) * mm});
            skLineSegment(sketch, "E414.1.0.906", {"start": v(254.3, 65) * mm, "end": v(254.25, 65) * mm});
            skLineSegment(sketch, "E414.1.0.907", {"start": v(129.7, 61.25) * mm, "end": v(129.7, 63.3) * mm});
            skLineSegment(sketch, "E414.1.0.908", {"start": v(-253.97, -54.75) * mm, "end": v(-255.8, -52.92) * mm});
            skLineSegment(sketch, "E414.1.0.909", {"start": v(7.05, -146.7) * mm, "end": v(5.1, -144.75) * mm});
            skLineSegment(sketch, "E414.1.0.910", {"start": v(125.75, -112.7) * mm, "end": v(125.75, -111) * mm});
            skLineSegment(sketch, "E414.1.0.911", {"start": v(129.75, 61.3) * mm, "end": v(129.75, 63.25) * mm});
            skLineSegment(sketch, "E414.1.0.912", {"start": v(125.8, -24.75) * mm, "end": v(125.8, -23) * mm});
            skLineSegment(sketch, "E414.1.0.913", {"start": v(254.5, -141) * mm, "end": v(254.5, -111) * mm});
            skLineSegment(sketch, "E414.1.0.914", {"start": v(254.3, -111) * mm, "end": v(254.25, -111) * mm});
            skLineSegment(sketch, "E414.1.0.915", {"start": v(129.5, 123) * mm, "end": v(129.5, 153) * mm});
            skLineSegment(sketch, "E414.1.0.916", {"start": v(-127.25, -26.7) * mm, "end": v(-127.25, -24.75) * mm});
            skLineSegment(sketch, "E414.1.0.917", {"start": v(121.95, 31.3) * mm, "end": v(123.9, 33.25) * mm});
            skLineSegment(sketch, "E414.1.0.918", {"start": v(-6.55, -56.7) * mm, "end": v(-4.6, -54.75) * mm});
            skLineSegment(sketch, "E414.1.0.919", {"start": v(254.3, -52.7) * mm, "end": v(254.3, -52.75) * mm});
            skLineSegment(sketch, "E414.1.0.920", {"start": v(250.45, 119.3) * mm, "end": v(252.4, 121.25) * mm});
            skLineSegment(sketch, "E414.1.0.921", {"start": v(-131.2, 153) * mm, "end": v(-131.25, 153) * mm});
            skLineSegment(sketch, "E414.1.0.922", {"start": v(-255.75, 123.1) * mm, "end": v(-255.75, 123.25) * mm});
            skLineSegment(sketch, "E414.1.0.923", {"start": v(135.55, 117.3) * mm, "end": v(133.6, 119.25) * mm});
            skLineSegment(sketch, "E414.1.0.924", {"start": v(125.8, 63.25) * mm, "end": v(125.8, 65) * mm});
            skLineSegment(sketch, "E414.1.0.925", {"start": v(125.8, 59.25) * mm, "end": v(125.8, 61.3) * mm});
            skLineSegment(sketch, "E414.1.0.926", {"start": v(254.25, 151.3) * mm, "end": v(254.25, 153) * mm});
            skLineSegment(sketch, "E414.1.0.927", {"start": v(1.25, 149.3) * mm, "end": v(1.25, 151.25) * mm});
            skLineSegment(sketch, "E414.1.0.928", {"start": v(125.8, -111) * mm, "end": v(125.75, -111) * mm});
            skLineSegment(sketch, "E414.1.0.929", {"start": v(1.2, -28.75) * mm, "end": v(1.2, -28.7) * mm});
            skLineSegment(sketch, "E414.1.0.930", {"start": v(121.97, -56.75) * mm, "end": v(124.02, -54.7) * mm});
            skLineSegment(sketch, "E414.1.0.931", {"start": v(125.8, 151.25) * mm, "end": v(125.8, 153) * mm});
            skLineSegment(sketch, "E414.1.0.932", {"start": v(129.75, -30.7) * mm, "end": v(129.75, -28.75) * mm});
            skLineSegment(sketch, "E414.1.0.933", {"start": v(-249.97, 29.25) * mm, "end": v(-252.02, 31.3) * mm});
            skLineSegment(sketch, "E414.1.0.934", {"start": v(-131.25, 63.3) * mm, "end": v(-131.25, 65) * mm});
            skLineSegment(sketch, "E414.1.0.935", {"start": v(-127.25, 61.3) * mm, "end": v(-127.25, 63.25) * mm});
            skLineSegment(sketch, "E414.1.0.936", {"start": v(-131.25, -112.7) * mm, "end": v(-131.25, -111) * mm});
            skLineSegment(sketch, "E414.1.0.937", {"start": v(-131.2, -111) * mm, "end": v(-131.25, -111) * mm});
            skLineSegment(sketch, "E414.1.0.938", {"start": v(-135.03, -56.75) * mm, "end": v(-132.98, -54.7) * mm});
            skLineSegment(sketch, "E414.1.0.939", {"start": v(-2.7, 153) * mm, "end": v(-2.75, 153) * mm});
            skLineSegment(sketch, "E414.1.0.940", {"start": v(-131, 123) * mm, "end": v(-131, 153) * mm});
            skLineSegment(sketch, "E414.1.0.941", {"start": v(-2.5, -141) * mm, "end": v(-2.5, -111) * mm});
            skLineSegment(sketch, "E414.1.0.942", {"start": v(-131, -141) * mm, "end": v(-131, -111) * mm});
            skLineSegment(sketch, "E414.1.0.943", {"start": v(-255.75, 129.3) * mm, "end": v(-255.75, 131.25) * mm});
            skLineSegment(sketch, "E414.1.0.944", {"start": v(-131.2, 151.25) * mm, "end": v(-131.2, 153) * mm});
            skLineSegment(sketch, "E414.1.0.945", {"start": v(-127.5, -53) * mm, "end": v(-127.5, -23) * mm});
            skLineSegment(sketch, "E414.1.0.946", {"start": v(-131.2, -28.75) * mm, "end": v(-131.2, -26.7) * mm});
            skLineSegment(sketch, "E414.1.0.947", {"start": v(-249.95, 29.3) * mm, "end": v(-251.9, 31.25) * mm});
            skLineSegment(sketch, "E414.1.0.948", {"start": v(-131.2, 63.25) * mm, "end": v(-131.2, 65) * mm});
            skLineSegment(sketch, "E414.1.0.949", {"start": v(-255.8, -50.75) * mm, "end": v(-255.8, -48.7) * mm});
            skLineSegment(sketch, "E414.1.0.950", {"start": v(-131.2, 65) * mm, "end": v(-131.25, 65) * mm});
            skLineSegment(sketch, "E414.1.0.951", {"start": v(-255.8, -138.75) * mm, "end": v(-255.8, -136.7) * mm});
            skLineSegment(sketch, "E414.1.0.952", {"start": v(-131.2, -24.75) * mm, "end": v(-131.2, -23) * mm});
            skLineSegment(sketch, "E414.1.0.953", {"start": v(-2.75, -28.7) * mm, "end": v(-2.75, -26.75) * mm});
            skLineSegment(sketch, "E414.1.0.954", {"start": v(-127.3, 57.25) * mm, "end": v(-127.3, 59.25) * mm});
            skLineSegment(sketch, "E414.1.0.955", {"start": v(-2.7, 63.25) * mm, "end": v(-2.7, 65) * mm});
            skLineSegment(sketch, "E414.1.0.956", {"start": v(-253.95, 121.3) * mm, "end": v(-255.75, 123.1) * mm});
            skLineSegment(sketch, "E414.1.0.957", {"start": v(-135.05, 31.3) * mm, "end": v(-133.1, 33.25) * mm});
            skLineSegment(sketch, "E414.1.0.958", {"start": v(-255.8, 123.08) * mm, "end": v(-255.8, 123.3) * mm});
            skLineSegment(sketch, "E414.1.0.959", {"start": v(-127.25, 149.3) * mm, "end": v(-127.25, 151.25) * mm});
            skLineSegment(sketch, "E414.1.0.960", {"start": v(-255.8, -118.75) * mm, "end": v(-255.8, -116.75) * mm});
            skLineSegment(sketch, "E414.1.0.961", {"start": v(-131.2, -112.75) * mm, "end": v(-131.2, -111) * mm});
            skLineSegment(sketch, "E414.1.0.962", {"start": v(-255.75, -30.7) * mm, "end": v(-255.75, -28.75) * mm});
            skLineSegment(sketch, "E414.1.0.963", {"start": v(-255.8, -52.92) * mm, "end": v(-255.8, -52.7) * mm});
            skLineSegment(sketch, "E414.1.0.964", {"start": v(250.47, -144.75) * mm, "end": v(252.52, -142.7) * mm});
            skLineSegment(sketch, "E414.1.0.965", {"start": v(125.75, 151.3) * mm, "end": v(125.75, 153) * mm});
            skLineSegment(sketch, "E414.1.0.966", {"start": v(250.45, -144.7) * mm, "end": v(252.4, -142.75) * mm});
            skLineSegment(sketch, "E414.1.0.967", {"start": v(254.3, -112.75) * mm, "end": v(254.3, -111) * mm});
            skLineSegment(sketch, "E414.1.0.968", {"start": v(-127.25, -114.7) * mm, "end": v(-127.25, -112.75) * mm});
            skLineSegment(sketch, "E414.1.0.969", {"start": v(125.8, -23) * mm, "end": v(125.75, -23) * mm});
            skLineSegment(sketch, "E414.1.0.970", {"start": v(121.97, 31.25) * mm, "end": v(124.02, 33.3) * mm});
            skLineSegment(sketch, "E414.1.0.971", {"start": v(-6.53, -56.75) * mm, "end": v(-4.48, -54.7) * mm});
            skLineSegment(sketch, "E414.1.0.972", {"start": v(250.47, 119.25) * mm, "end": v(252.52, 121.3) * mm});
            skLineSegment(sketch, "E414.1.0.973", {"start": v(7.03, -146.75) * mm, "end": v(4.98, -144.7) * mm});
            skLineSegment(sketch, "E414.1.0.974", {"start": v(-2.7, 143.25) * mm, "end": v(-2.7, 145.25) * mm});
            skLineSegment(sketch, "E414.1.0.975", {"start": v(125.8, -112.75) * mm, "end": v(125.8, -111) * mm});
            skLineSegment(sketch, "E414.1.0.976", {"start": v(129.7, -30.75) * mm, "end": v(129.7, -28.75) * mm});
            skLineSegment(sketch, "E414.1.0.977", {"start": v(3.05, -54.7) * mm, "end": v(1.25, -52.9) * mm});
            skLineSegment(sketch, "E414.1.0.978", {"start": v(125.75, 59.3) * mm, "end": v(125.75, 61.25) * mm});
            skLineSegment(sketch, "E414.1.0.979", {"start": v(-2.75, 147.3) * mm, "end": v(-2.75, 149.25) * mm});
            skLineSegment(sketch, "E414.1.0.980", {"start": v(121.95, -56.7) * mm, "end": v(123.9, -54.75) * mm});
            skLineSegment(sketch, "E414.1.0.981", {"start": v(254.25, -24.7) * mm, "end": v(254.25, -23) * mm});
            skLineSegment(sketch, "E414.1.0.982", {"start": v(254.3, -52.75) * mm, "end": v(254.25, -52.75) * mm});
            skLineSegment(sketch, "E414.1.0.983", {"start": v(1.2, -30.75) * mm, "end": v(1.2, -28.75) * mm});
            skLineSegment(sketch, "E414.1.0.984", {"start": v(126, 35) * mm, "end": v(126, 65) * mm});
            skLineSegment(sketch, "E414.1.0.985", {"start": v(1, 35) * mm, "end": v(1, 65) * mm});
            skLineSegment(sketch, "E414.1.0.986", {"start": v(125.75, 147.3) * mm, "end": v(125.75, 149.25) * mm});
            skLineSegment(sketch, "E414.1.0.987", {"start": v(129.75, -34.7) * mm, "end": v(129.75, -32.75) * mm});
            skLineSegment(sketch, "E414.1.0.988", {"start": v(254.25, 43.3) * mm, "end": v(254.25, 45.3) * mm});
            skLineSegment(sketch, "E414.1.0.989", {"start": v(254.3, 59.25) * mm, "end": v(254.3, 61.3) * mm});
            skLineSegment(sketch, "E414.1.0.990", {"start": v(129.75, 149.3) * mm, "end": v(129.75, 151.25) * mm});
            skLineSegment(sketch, "E414.1.0.991", {"start": v(-2.7, -30.75) * mm, "end": v(-2.7, -30.7) * mm});
            skLineSegment(sketch, "E414.1.0.992", {"start": v(129.7, -28.75) * mm, "end": v(129.7, -28.7) * mm});
            skLineSegment(sketch, "E414.1.0.993", {"start": v(135.53, 117.25) * mm, "end": v(133.48, 119.3) * mm});
            skLineSegment(sketch, "E414.1.0.994", {"start": v(1.2, 149.25) * mm, "end": v(1.2, 151.3) * mm});
            skLineSegment(sketch, "E414.1.0.995", {"start": v(-125.47, 33.25) * mm, "end": v(-127.3, 35.08) * mm});
            skLineSegment(sketch, "E414.1.0.996", {"start": v(254.3, 151.25) * mm, "end": v(254.3, 153) * mm});
            skLineSegment(sketch, "E414.1.0.997", {"start": v(126, 123) * mm, "end": v(126, 153) * mm});
            skLineSegment(sketch, "E414.1.0.998", {"start": v(1.2, -28.7) * mm, "end": v(1.25, -28.7) * mm});
            skLineSegment(sketch, "E414.1.0.999", {"start": v(125.75, -32.7) * mm, "end": v(125.75, -30.75) * mm});
            skLineSegment(sketch, "E414.1.0.1000", {"start": v(7.05, 29.3) * mm, "end": v(5.1, 31.25) * mm});
            skLineSegment(sketch, "E414.1.0.1001", {"start": v(1.2, 141.25) * mm, "end": v(1.2, 143.3) * mm});
            skLineSegment(sketch, "E414.1.0.1002", {"start": v(131.53, -54.75) * mm, "end": v(129.7, -52.92) * mm});
            skLineSegment(sketch, "E414.1.0.1003", {"start": v(125.8, -52.7) * mm, "end": v(125.8, -52.75) * mm});
            skLineSegment(sketch, "E414.1.0.1004", {"start": v(254.3, -23) * mm, "end": v(254.25, -23) * mm});
            skLineSegment(sketch, "E414.1.0.1005", {"start": v(254.25, 47.3) * mm, "end": v(254.25, 49.25) * mm});
            skLineSegment(sketch, "E414.1.0.1006", {"start": v(1.2, 145.25) * mm, "end": v(1.2, 147.25) * mm});
            skLineSegment(sketch, "E414.1.0.1007", {"start": v(-253.97, -142.75) * mm, "end": v(-255.8, -140.92) * mm});
            skLineSegment(sketch, "E414.1.0.1008", {"start": v(-131.2, -116.75) * mm, "end": v(-131.2, -114.7) * mm});
            skLineSegment(sketch, "E414.1.0.1009", {"start": v(-255.8, -116.75) * mm, "end": v(-255.8, -116.7) * mm});
            skLineSegment(sketch, "E414.1.0.1010", {"start": v(-255.75, -134.7) * mm, "end": v(-255.75, -132.75) * mm});
            skLineSegment(sketch, "E414.1.0.1011", {"start": v(-131.25, 59.3) * mm, "end": v(-131.25, 61.25) * mm});
            skLineSegment(sketch, "E414.1.0.1012", {"start": v(-255.8, 149.25) * mm, "end": v(-255.8, 151.3) * mm});
            skLineSegment(sketch, "E414.1.0.1013", {"start": v(-127.3, 59.25) * mm, "end": v(-127.3, 59.3) * mm});
            skLineSegment(sketch, "E414.1.0.1014", {"start": v(-2.7, 139.25) * mm, "end": v(-2.7, 141.25) * mm});
            skLineSegment(sketch, "E414.1.0.1015", {"start": v(-255.75, 125.3) * mm, "end": v(-255.75, 127.25) * mm});
            skLineSegment(sketch, "E414.1.0.1016", {"start": v(-255.8, -114.75) * mm, "end": v(-255.8, -112.7) * mm});
            skLineSegment(sketch, "E414.1.0.1017", {"start": v(-255.8, -140.92) * mm, "end": v(-255.8, -140.7) * mm});
            skLineSegment(sketch, "E414.1.0.1018", {"start": v(-135.05, -56.7) * mm, "end": v(-133.1, -54.75) * mm});
            skLineSegment(sketch, "E414.1.0.1019", {"start": v(-255.8, -28.75) * mm, "end": v(-255.8, -28.7) * mm});
            skLineSegment(sketch, "E414.1.0.1020", {"start": v(-131.2, 35.25) * mm, "end": v(-131.25, 35.25) * mm});
            skLineSegment(sketch, "E414.1.0.1021", {"start": v(-255.8, 129.25) * mm, "end": v(-255.8, 131.3) * mm});
            skLineSegment(sketch, "E414.1.0.1022", {"start": v(-127.3, 149.25) * mm, "end": v(-127.3, 151.3) * mm});
            skLineSegment(sketch, "E414.1.0.1023", {"start": v(-2.75, 143.3) * mm, "end": v(-2.75, 145.25) * mm});
            skLineSegment(sketch, "E414.1.0.1024", {"start": v(-255.8, -134.75) * mm, "end": v(-255.8, -132.7) * mm});
            skLineSegment(sketch, "E414.1.0.1025", {"start": v(-255.75, -50.7) * mm, "end": v(-255.75, -48.75) * mm});
            skLineSegment(sketch, "E414.1.0.1026", {"start": v(-255.75, -118.7) * mm, "end": v(-255.75, -116.75) * mm});
            skLineSegment(sketch, "E414.1.0.1027", {"start": v(-255.8, 145.25) * mm, "end": v(-255.8, 147.25) * mm});
            skLineSegment(sketch, "E414.1.0.1028", {"start": v(-127.3, -118.75) * mm, "end": v(-127.3, -116.75) * mm});
            skLineSegment(sketch, "E414.1.0.1029", {"start": v(-135.03, 31.25) * mm, "end": v(-132.98, 33.3) * mm});
            skLineSegment(sketch, "E414.1.0.1030", {"start": v(-255.8, 125.25) * mm, "end": v(-255.8, 127.3) * mm});
            skLineSegment(sketch, "E414.1.0.1031", {"start": v(-131.2, 35.3) * mm, "end": v(-131.2, 37.3) * mm});
            skLineSegment(sketch, "E414.1.0.1032", {"start": v(-2.75, 123.3) * mm, "end": v(-2.75, 125.25) * mm});
            skLineSegment(sketch, "E414.1.0.1033", {"start": v(-2.75, 139.3) * mm, "end": v(-2.75, 141.25) * mm});
            skLineSegment(sketch, "E414.1.0.1034", {"start": v(-255.75, -138.7) * mm, "end": v(-255.75, -136.75) * mm});
            skLineSegment(sketch, "E414.1.0.1035", {"start": v(-131.2, -23) * mm, "end": v(-131.25, -23) * mm});
            skLineSegment(sketch, "E414.1.0.1036", {"start": v(-127.3, -116.7) * mm, "end": v(-127.25, -116.7) * mm});
            skLineSegment(sketch, "E414.1.0.1037", {"start": v(-255.8, -116.7) * mm, "end": v(-255.75, -116.7) * mm});
            skLineSegment(sketch, "E414.1.0.1038", {"start": v(-255.8, -30.75) * mm, "end": v(-255.8, -28.75) * mm});
            skLineSegment(sketch, "E414.1.0.1039", {"start": v(-255.8, -122.75) * mm, "end": v(-255.8, -120.7) * mm});
            skLineSegment(sketch, "E414.1.0.1040", {"start": v(-253.95, -142.7) * mm, "end": v(-255.75, -140.9) * mm});
            skLineSegment(sketch, "E414.1.0.1041", {"start": v(-2.5, 35) * mm, "end": v(-2.5, 65) * mm});
            skLineSegment(sketch, "E414.1.0.1042", {"start": v(-127.25, 57.3) * mm, "end": v(-127.25, 59.25) * mm});
            skLineSegment(sketch, "E414.1.0.1043", {"start": v(-127.3, 35.08) * mm, "end": v(-127.3, 35.3) * mm});
            skLineSegment(sketch, "E414.1.0.1044", {"start": v(-2.75, 63.3) * mm, "end": v(-2.75, 65) * mm});
            skLineSegment(sketch, "E414.1.0.1045", {"start": v(-127.25, -126.7) * mm, "end": v(-127.25, -124.75) * mm});
            skLineSegment(sketch, "E414.1.0.1046", {"start": v(-2.7, -116.75) * mm, "end": v(-2.7, -114.7) * mm});
            skLineSegment(sketch, "E414.1.0.1047", {"start": v(-2.75, -32.7) * mm, "end": v(-2.75, -30.75) * mm});
            skLineSegment(sketch, "E414.1.0.1048", {"start": v(-255.8, 137.25) * mm, "end": v(-255.8, 139.3) * mm});
            skLineSegment(sketch, "E414.1.0.1049", {"start": v(-255.8, 147.3) * mm, "end": v(-255.75, 147.3) * mm});
            skLineSegment(sketch, "E414.1.0.1050", {"start": v(-131.2, 59.25) * mm, "end": v(-131.2, 61.3) * mm});
            skLineSegment(sketch, "E414.1.0.1051", {"start": v(-2.7, 147.25) * mm, "end": v(-2.7, 149.3) * mm});
            skLineSegment(sketch, "E414.1.0.1052", {"start": v(-6.55, 119.3) * mm, "end": v(-4.6, 121.25) * mm});
            skLineSegment(sketch, "E414.1.0.1053", {"start": v(-2.7, 141.25) * mm, "end": v(-2.7, 141.3) * mm});
            skLineSegment(sketch, "E414.1.0.1054", {"start": v(-2.7, 145.25) * mm, "end": v(-2.7, 145.3) * mm});
            skLineSegment(sketch, "E414.1.0.1055", {"start": v(-131.25, -116.7) * mm, "end": v(-131.25, -114.75) * mm});
            skLineSegment(sketch, "E414.1.0.1056", {"start": v(-131.2, -120.75) * mm, "end": v(-131.2, -118.75) * mm});
            skLineSegment(sketch, "E414.1.0.1057", {"start": v(-255.75, -42.7) * mm, "end": v(-255.75, -40.75) * mm});
            skLineSegment(sketch, "E414.1.0.1058", {"start": v(-255.75, -52.9) * mm, "end": v(-255.75, -52.75) * mm});
            skLineSegment(sketch, "E414.1.0.1059", {"start": v(125.8, 147.25) * mm, "end": v(125.8, 149.3) * mm});
            skLineSegment(sketch, "E414.1.0.1060", {"start": v(125.8, -32.75) * mm, "end": v(125.8, -30.75) * mm});
            skLineSegment(sketch, "E414.1.0.1061", {"start": v(254.25, -112.7) * mm, "end": v(254.25, -111) * mm});
            skLineSegment(sketch, "E414.1.0.1062", {"start": v(254.25, -52.7) * mm, "end": v(254.25, -50.75) * mm});
            skLineSegment(sketch, "E414.1.0.1063", {"start": v(131.55, -54.7) * mm, "end": v(129.75, -52.9) * mm});
            skLineSegment(sketch, "E414.1.0.1064", {"start": v(129.7, -34.75) * mm, "end": v(129.7, -32.7) * mm});
            skLineSegment(sketch, "E414.1.0.1065", {"start": v(254.25, 59.3) * mm, "end": v(254.25, 61.25) * mm});
            skLineSegment(sketch, "E414.1.0.1066", {"start": v(254.3, 43.25) * mm, "end": v(254.3, 45.3) * mm});
            skLineSegment(sketch, "E414.1.0.1067", {"start": v(-127.25, -122.7) * mm, "end": v(-127.25, -120.75) * mm});
            skLineSegment(sketch, "E414.1.0.1068", {"start": v(3.03, -54.75) * mm, "end": v(1.2, -52.92) * mm});
            skLineSegment(sketch, "E414.1.0.1069", {"start": v(-127.3, -114.75) * mm, "end": v(-127.3, -112.7) * mm});
            skLineSegment(sketch, "E414.1.0.1070", {"start": v(-131.2, -118.75) * mm, "end": v(-131.2, -118.7) * mm});
            skLineSegment(sketch, "E414.1.0.1071", {"start": v(-255.75, -114.7) * mm, "end": v(-255.75, -112.75) * mm});
            skLineSegment(sketch, "E414.1.0.1072", {"start": v(-125.47, -54.75) * mm, "end": v(-127.3, -52.92) * mm});
            skLineSegment(sketch, "E414.1.0.1073", {"start": v(-255.8, -38.75) * mm, "end": v(-255.8, -36.7) * mm});
            skLineSegment(sketch, "E414.1.0.1074", {"start": v(-127.3, -28.75) * mm, "end": v(-127.3, -28.7) * mm});
            skLineSegment(sketch, "E414.1.0.1075", {"start": v(-125.45, 33.3) * mm, "end": v(-127.25, 35.1) * mm});
            skLineSegment(sketch, "E414.1.0.1076", {"start": v(1.25, -30.7) * mm, "end": v(1.25, -28.75) * mm});
            skLineSegment(sketch, "E414.1.0.1077", {"start": v(-2.7, 131.25) * mm, "end": v(-2.7, 133.3) * mm});
            skLineSegment(sketch, "E414.1.0.1078", {"start": v(254.3, -116.75) * mm, "end": v(254.3, -114.7) * mm});
            skLineSegment(sketch, "E414.1.0.1079", {"start": v(254.3, -24.75) * mm, "end": v(254.3, -23) * mm});
            skLineSegment(sketch, "E414.1.0.1080", {"start": v(1.2, 133.25) * mm, "end": v(1.2, 135.3) * mm});
            skLineSegment(sketch, "E414.1.0.1081", {"start": v(1.25, 141.3) * mm, "end": v(1.25, 143.25) * mm});
            skLineSegment(sketch, "E414.1.0.1082", {"start": v(254.25, 35.3) * mm, "end": v(254.25, 37.25) * mm});
            skLineSegment(sketch, "E414.1.0.1083", {"start": v(-131.2, 35.3) * mm, "end": v(-131.2, 35.25) * mm});
            skLineSegment(sketch, "E414.1.0.1084", {"start": v(125.8, -30.75) * mm, "end": v(125.8, -30.7) * mm});
            skLineSegment(sketch, "E414.1.0.1085", {"start": v(254.3, -120.75) * mm, "end": v(254.3, -118.75) * mm});
            skLineSegment(sketch, "E414.1.0.1086", {"start": v(1.25, 129.3) * mm, "end": v(1.25, 131.25) * mm});
            skLineSegment(sketch, "E414.1.0.1087", {"start": v(125.8, 65) * mm, "end": v(125.75, 65) * mm});
            skLineSegment(sketch, "E414.1.0.1088", {"start": v(1.2, 61.25) * mm, "end": v(1.2, 63.3) * mm});
            skLineSegment(sketch, "E414.1.0.1089", {"start": v(129.7, 149.25) * mm, "end": v(129.7, 151.3) * mm});
            skLineSegment(sketch, "E414.1.0.1090", {"start": v(135.55, 29.3) * mm, "end": v(133.6, 31.25) * mm});
            skLineSegment(sketch, "E414.1.0.1091", {"start": v(129.7, -28.7) * mm, "end": v(129.75, -28.7) * mm});
            skLineSegment(sketch, "E414.1.0.1092", {"start": v(129.7, 57.25) * mm, "end": v(129.7, 59.25) * mm});
            skLineSegment(sketch, "E414.1.0.1093", {"start": v(254.5, 123) * mm, "end": v(254.5, 153) * mm});
            skLineSegment(sketch, "E414.1.0.1094", {"start": v(125.8, 143.25) * mm, "end": v(125.8, 145.25) * mm});
            skLineSegment(sketch, "E414.1.0.1095", {"start": v(125.8, -34.75) * mm, "end": v(125.8, -34.7) * mm});
            skLineSegment(sketch, "E414.1.0.1096", {"start": v(129.75, -52.9) * mm, "end": v(129.75, -52.75) * mm});
            skLineSegment(sketch, "E414.1.0.1097", {"start": v(129.7, 141.25) * mm, "end": v(129.7, 143.3) * mm});
            skLineSegment(sketch, "E414.1.0.1098", {"start": v(1.2, 137.25) * mm, "end": v(1.2, 139.3) * mm});
            skLineSegment(sketch, "E414.1.0.1099", {"start": v(1.25, 61.3) * mm, "end": v(1.25, 63.25) * mm});
            skLineSegment(sketch, "E414.1.0.1100", {"start": v(-255.8, 133.25) * mm, "end": v(-255.8, 135.3) * mm});
            skLineSegment(sketch, "E414.1.0.1101", {"start": v(-255.75, 141.3) * mm, "end": v(-255.75, 143.25) * mm});
            skLineSegment(sketch, "E414.1.0.1102", {"start": v(-255.75, 149.3) * mm, "end": v(-255.75, 151.25) * mm});
            skLineSegment(sketch, "E414.1.0.1103", {"start": v(125.8, 153) * mm, "end": v(125.75, 153) * mm});
            skLineSegment(sketch, "E414.1.0.1104", {"start": v(-135.05, 119.3) * mm, "end": v(-133.1, 121.25) * mm});
            skLineSegment(sketch, "E414.1.0.1105", {"start": v(121.97, -144.75) * mm, "end": v(124.02, -142.7) * mm});
            skLineSegment(sketch, "E414.1.0.1106", {"start": v(125.8, -52.75) * mm, "end": v(125.75, -52.75) * mm});
            skLineSegment(sketch, "E414.1.0.1107", {"start": v(7.03, 29.25) * mm, "end": v(4.98, 31.3) * mm});
            skLineSegment(sketch, "E414.1.0.1108", {"start": v(129.7, 145.25) * mm, "end": v(129.7, 147.25) * mm});
            skLineSegment(sketch, "E414.1.0.1109", {"start": v(1.25, 145.3) * mm, "end": v(1.25, 147.25) * mm});
            skLineSegment(sketch, "E414.1.0.1110", {"start": v(-2.7, 135.25) * mm, "end": v(-2.7, 137.3) * mm});
            skLineSegment(sketch, "E414.1.0.1111", {"start": v(-2.7, 127.25) * mm, "end": v(-2.7, 129.25) * mm});
            skLineSegment(sketch, "E414.1.0.1112", {"start": v(254.3, 147.25) * mm, "end": v(254.3, 149.3) * mm});
            skLineSegment(sketch, "E414.1.0.1113", {"start": v(3.05, 121.3) * mm, "end": v(1.25, 123.1) * mm});
            skLineSegment(sketch, "E414.1.0.1114", {"start": v(1.25, -52.9) * mm, "end": v(1.25, -52.75) * mm});
            skLineSegment(sketch, "E414.1.0.1115", {"start": v(129.7, -114.75) * mm, "end": v(129.7, -112.7) * mm});
            skLineSegment(sketch, "E414.1.0.1116", {"start": v(135.53, -146.75) * mm, "end": v(133.48, -144.7) * mm});
            skLineSegment(sketch, "E414.1.0.1117", {"start": v(254.3, 47.25) * mm, "end": v(254.3, 49.3) * mm});
            skLineSegment(sketch, "E414.1.0.1118", {"start": v(254.3, 39.25) * mm, "end": v(254.3, 41.25) * mm});
            skLineSegment(sketch, "E414.1.0.1119", {"start": v(254.3, 35.3) * mm, "end": v(254.3, 35.25) * mm});
            skLineSegment(sketch, "E414.1.0.1120", {"start": v(125.8, 145.25) * mm, "end": v(125.8, 145.3) * mm});
            skLineSegment(sketch, "E414.1.0.1121", {"start": v(250.47, 31.25) * mm, "end": v(252.52, 33.3) * mm});
            skLineSegment(sketch, "E414.1.0.1122", {"start": v(129.7, 59.25) * mm, "end": v(129.7, 59.3) * mm});
            skLineSegment(sketch, "E414.1.0.1123", {"start": v(1.25, 125.3) * mm, "end": v(1.25, 127.25) * mm});
            skLineSegment(sketch, "E414.1.0.1124", {"start": v(1.2, -114.75) * mm, "end": v(1.2, -112.7) * mm});
            skLineSegment(sketch, "E414.1.0.1125", {"start": v(129.7, 147.3) * mm, "end": v(129.75, 147.3) * mm});
            skLineSegment(sketch, "E414.1.0.1126", {"start": v(7.05, 117.3) * mm, "end": v(5.1, 119.25) * mm});
            skLineSegment(sketch, "E414.1.0.1127", {"start": v(125.75, 139.3) * mm, "end": v(125.75, 141.25) * mm});
            skLineSegment(sketch, "E414.1.0.1128", {"start": v(-131.2, -124.75) * mm, "end": v(-131.2, -122.75) * mm});
            skLineSegment(sketch, "E414.1.0.1129", {"start": v(-255.8, -126.75) * mm, "end": v(-255.8, -124.7) * mm});
            skLineSegment(sketch, "E414.1.0.1130", {"start": v(-255.8, -34.75) * mm, "end": v(-255.8, -32.7) * mm});
            skLineSegment(sketch, "E414.1.0.1131", {"start": v(-131.2, 55.25) * mm, "end": v(-131.2, 57.25) * mm});
            skLineSegment(sketch, "E414.1.0.1132", {"start": v(-131.2, -52.75) * mm, "end": v(-131.25, -52.75) * mm});
            skLineSegment(sketch, "E414.1.0.1133", {"start": v(-2.7, -52.7) * mm, "end": v(-2.7, -50.7) * mm});
            skLineSegment(sketch, "E414.1.0.1134", {"start": v(-127.3, -52.92) * mm, "end": v(-127.3, -52.7) * mm});
            skLineSegment(sketch, "E414.1.0.1135", {"start": v(-2.7, 123.25) * mm, "end": v(-2.75, 123.25) * mm});
            skLineSegment(sketch, "E414.1.0.1136", {"start": v(-255.75, -130.7) * mm, "end": v(-255.75, -128.75) * mm});
            skLineSegment(sketch, "E414.1.0.1137", {"start": v(-255.75, -46.7) * mm, "end": v(-255.75, -44.75) * mm});
            skLineSegment(sketch, "E414.1.0.1138", {"start": v(-255.75, 145.3) * mm, "end": v(-255.75, 147.25) * mm});
            skLineSegment(sketch, "E414.1.0.1139", {"start": v(-127.3, 37.25) * mm, "end": v(-127.3, 39.3) * mm});
            skLineSegment(sketch, "E414.1.0.1140", {"start": v(-2.7, 123.3) * mm, "end": v(-2.7, 125.3) * mm});
            skLineSegment(sketch, "E414.1.0.1141", {"start": v(-127.25, -118.7) * mm, "end": v(-127.25, -116.75) * mm});
            skLineSegment(sketch, "E414.1.0.1142", {"start": v(-2.75, -116.7) * mm, "end": v(-2.75, -114.75) * mm});
            skLineSegment(sketch, "E414.1.0.1143", {"start": v(-255.8, 147.25) * mm, "end": v(-255.8, 147.3) * mm});
            skLineSegment(sketch, "E414.1.0.1144", {"start": v(-127.3, -116.75) * mm, "end": v(-127.3, -116.7) * mm});
            skLineSegment(sketch, "E414.1.0.1145", {"start": v(-127.25, -134.7) * mm, "end": v(-127.25, -132.75) * mm});
            skLineSegment(sketch, "E414.1.0.1146", {"start": v(-255.8, -28.7) * mm, "end": v(-255.75, -28.7) * mm});
            skLineSegment(sketch, "E414.1.0.1147", {"start": v(-131.25, 35.3) * mm, "end": v(-131.25, 37.25) * mm});
            skLineSegment(sketch, "E414.1.0.1148", {"start": v(-255.75, 137.3) * mm, "end": v(-255.75, 139.25) * mm});
            skLineSegment(sketch, "E414.1.0.1149", {"start": v(-131.25, 131.3) * mm, "end": v(-131.25, 133.3) * mm});
            skLineSegment(sketch, "E414.1.0.1150", {"start": v(-255.75, -38.7) * mm, "end": v(-255.75, -36.75) * mm});
            skLineSegment(sketch, "E414.1.0.1151", {"start": v(-2.7, 65) * mm, "end": v(-2.75, 65) * mm});
            skLineSegment(sketch, "E414.1.0.1152", {"start": v(-127.3, 59.3) * mm, "end": v(-127.25, 59.3) * mm});
            skLineSegment(sketch, "E414.1.0.1153", {"start": v(-6.53, 119.25) * mm, "end": v(-4.48, 121.3) * mm});
            skLineSegment(sketch, "E414.1.0.1154", {"start": v(-135.03, 119.25) * mm, "end": v(-132.98, 121.3) * mm});
            skLineSegment(sketch, "E414.1.0.1155", {"start": v(-131.25, 55.3) * mm, "end": v(-131.25, 57.25) * mm});
            skLineSegment(sketch, "E414.1.0.1156", {"start": v(-2.75, 135.3) * mm, "end": v(-2.75, 137.25) * mm});
            skLineSegment(sketch, "E414.1.0.1157", {"start": v(-255.75, -140.9) * mm, "end": v(-255.75, -140.75) * mm});
            skLineSegment(sketch, "E414.1.0.1158", {"start": v(-255.8, -130.75) * mm, "end": v(-255.8, -128.7) * mm});
            skLineSegment(sketch, "E414.1.0.1159", {"start": v(-255.75, -126.7) * mm, "end": v(-255.75, -124.75) * mm});
            skLineSegment(sketch, "E414.1.0.1160", {"start": v(-255.75, -122.7) * mm, "end": v(-255.75, -120.75) * mm});
            skLineSegment(sketch, "E414.1.0.1161", {"start": v(-2.75, -120.7) * mm, "end": v(-2.75, -118.75) * mm});
            skLineSegment(sketch, "E414.1.0.1162", {"start": v(-127.3, -30.75) * mm, "end": v(-127.3, -28.75) * mm});
            skLineSegment(sketch, "E414.1.0.1163", {"start": v(-2.7, -124.75) * mm, "end": v(-2.7, -122.75) * mm});
            skLineSegment(sketch, "E414.1.0.1164", {"start": v(-131.25, -120.7) * mm, "end": v(-131.25, -118.75) * mm});
            skLineSegment(sketch, "E414.1.0.1165", {"start": v(-127.3, -126.75) * mm, "end": v(-127.3, -124.7) * mm});
            skLineSegment(sketch, "E414.1.0.1166", {"start": v(-127.3, -122.75) * mm, "end": v(-127.3, -120.7) * mm});
            skLineSegment(sketch, "E414.1.0.1167", {"start": v(-125.47, -142.75) * mm, "end": v(-127.3, -140.92) * mm});
            skLineSegment(sketch, "E414.1.0.1168", {"start": v(-2.7, -32.75) * mm, "end": v(-2.7, -30.75) * mm});
            skLineSegment(sketch, "E414.1.0.1169", {"start": v(-131.2, -32.75) * mm, "end": v(-131.2, -30.75) * mm});
            skLineSegment(sketch, "E414.1.0.1170", {"start": v(-127.25, 35.1) * mm, "end": v(-127.25, 35.25) * mm});
            skLineSegment(sketch, "E414.1.0.1171", {"start": v(-127.25, 45.3) * mm, "end": v(-127.25, 47.25) * mm});
            skLineSegment(sketch, "E414.1.0.1172", {"start": v(-255.75, 57.3) * mm, "end": v(-255.75, 59.25) * mm});
            skLineSegment(sketch, "E414.1.0.1173", {"start": v(-2.7, -122.75) * mm, "end": v(-2.7, -122.7) * mm});
            skLineSegment(sketch, "E414.1.0.1174", {"start": v(-2.75, -132.7) * mm, "end": v(-2.75, -130.7) * mm});
            skLineSegment(sketch, "E414.1.0.1175", {"start": v(-2.75, -52.7) * mm, "end": v(-2.75, -50.75) * mm});
            skLineSegment(sketch, "E414.1.0.1176", {"start": v(-125.45, -54.7) * mm, "end": v(-127.25, -52.9) * mm});
            skLineSegment(sketch, "E414.1.0.1177", {"start": v(-127.3, -28.7) * mm, "end": v(-127.25, -28.7) * mm});
            skLineSegment(sketch, "E414.1.0.1178", {"start": v(-127.3, -34.75) * mm, "end": v(-127.3, -32.7) * mm});
            skLineSegment(sketch, "E414.1.0.1179", {"start": v(-255.8, 141.25) * mm, "end": v(-255.8, 143.3) * mm});
            skLineSegment(sketch, "E414.1.0.1180", {"start": v(-131.2, 57.25) * mm, "end": v(-131.2, 57.3) * mm});
            skLineSegment(sketch, "E414.1.0.1181", {"start": v(-255.75, 133.3) * mm, "end": v(-255.75, 135.25) * mm});
            skLineSegment(sketch, "E414.1.0.1182", {"start": v(-2.75, 131.3) * mm, "end": v(-2.75, 133.3) * mm});
            skLineSegment(sketch, "E414.1.0.1183", {"start": v(-255.75, 53.3) * mm, "end": v(-255.75, 55.25) * mm});
            skLineSegment(sketch, "E414.1.0.1184", {"start": v(-131.25, -124.7) * mm, "end": v(-131.25, -122.75) * mm});
            skLineSegment(sketch, "E414.1.0.1185", {"start": v(-131.2, -136.75) * mm, "end": v(-131.2, -134.75) * mm});
            skLineSegment(sketch, "E414.1.0.1186", {"start": v(-255.8, -42.75) * mm, "end": v(-255.8, -40.7) * mm});
            skLineSegment(sketch, "E414.1.0.1187", {"start": v(-255.75, -34.7) * mm, "end": v(-255.75, -32.75) * mm});
            skLineSegment(sketch, "E414.1.0.1188", {"start": v(-6.55, -144.7) * mm, "end": v(-4.6, -142.75) * mm});
            skLineSegment(sketch, "E414.1.0.1189", {"start": v(129.75, 141.3) * mm, "end": v(129.75, 143.25) * mm});
            skLineSegment(sketch, "E414.1.0.1190", {"start": v(1.25, 133.3) * mm, "end": v(1.25, 135.25) * mm});
            skLineSegment(sketch, "E414.1.0.1191", {"start": v(1.25, -114.7) * mm, "end": v(1.25, -112.75) * mm});
            skLineSegment(sketch, "E414.1.0.1192", {"start": v(121.95, -144.7) * mm, "end": v(123.9, -142.75) * mm});
            skLineSegment(sketch, "E414.1.0.1193", {"start": v(-2.7, -140.7) * mm, "end": v(-2.7, -138.7) * mm});
            skLineSegment(sketch, "E414.1.0.1194", {"start": v(1.2, 129.25) * mm, "end": v(1.2, 131.3) * mm});
            skLineSegment(sketch, "E414.1.0.1195", {"start": v(254.25, -116.7) * mm, "end": v(254.25, -114.75) * mm});
            skLineSegment(sketch, "E414.1.0.1196", {"start": v(-2.7, -118.75) * mm, "end": v(-2.7, -118.7) * mm});
            skLineSegment(sketch, "E414.1.0.1197", {"start": v(254.3, 35.3) * mm, "end": v(254.3, 37.3) * mm});
            skLineSegment(sketch, "E414.1.0.1198", {"start": v(-127.3, 53.25) * mm, "end": v(-127.3, 55.3) * mm});
            skLineSegment(sketch, "E414.1.0.1199", {"start": v(125.75, 143.3) * mm, "end": v(125.75, 145.25) * mm});
            skLineSegment(sketch, "E414.1.0.1200", {"start": v(129.75, 57.3) * mm, "end": v(129.75, 59.25) * mm});
            skLineSegment(sketch, "E414.1.0.1201", {"start": v(-131.2, -36.75) * mm, "end": v(-131.2, -34.75) * mm});
            skLineSegment(sketch, "E414.1.0.1202", {"start": v(254.25, 147.3) * mm, "end": v(254.25, 149.25) * mm});
            skLineSegment(sketch, "E414.1.0.1203", {"start": v(125.75, -52.7) * mm, "end": v(125.75, -50.75) * mm});
            skLineSegment(sketch, "E414.1.0.1204", {"start": v(-2.75, 127.3) * mm, "end": v(-2.75, 129.25) * mm});
            skLineSegment(sketch, "E414.1.0.1205", {"start": v(-127.25, 133.3) * mm, "end": v(-127.25, 135.25) * mm});
            skLineSegment(sketch, "E414.1.0.1206", {"start": v(254.25, -120.7) * mm, "end": v(254.25, -118.75) * mm});
            skLineSegment(sketch, "E414.1.0.1207", {"start": v(131.55, 33.3) * mm, "end": v(129.75, 35.1) * mm});
            skLineSegment(sketch, "E414.1.0.1208", {"start": v(-131.2, 47.25) * mm, "end": v(-131.2, 49.3) * mm});
            skLineSegment(sketch, "E414.1.0.1209", {"start": v(254.3, -118.75) * mm, "end": v(254.3, -118.7) * mm});
            skLineSegment(sketch, "E414.1.0.1210", {"start": v(129.7, -52.92) * mm, "end": v(129.7, -52.7) * mm});
            skLineSegment(sketch, "E414.1.0.1211", {"start": v(250.45, 31.3) * mm, "end": v(252.4, 33.25) * mm});
            skLineSegment(sketch, "E414.1.0.1212", {"start": v(129.7, 137.25) * mm, "end": v(129.7, 139.3) * mm});
            skLineSegment(sketch, "E414.1.0.1213", {"start": v(1.2, 147.25) * mm, "end": v(1.2, 147.3) * mm});
            skLineSegment(sketch, "E414.1.0.1214", {"start": v(-2.7, 129.25) * mm, "end": v(-2.7, 129.3) * mm});
            skLineSegment(sketch, "E414.1.0.1215", {"start": v(135.53, 29.25) * mm, "end": v(133.48, 31.3) * mm});
            skLineSegment(sketch, "E414.1.0.1216", {"start": v(254.25, 39.3) * mm, "end": v(254.25, 41.25) * mm});
            skLineSegment(sketch, "E414.1.0.1217", {"start": v(254.3, 153) * mm, "end": v(254.25, 153) * mm});
            skLineSegment(sketch, "E414.1.0.1218", {"start": v(1.2, 125.25) * mm, "end": v(1.2, 127.3) * mm});
            skLineSegment(sketch, "E414.1.0.1219", {"start": v(1.25, 137.3) * mm, "end": v(1.25, 139.25) * mm});
            skLineSegment(sketch, "E414.1.0.1220", {"start": v(125.75, -36.7) * mm, "end": v(125.75, -34.75) * mm});
            skLineSegment(sketch, "E414.1.0.1221", {"start": v(129.7, -126.75) * mm, "end": v(129.7, -124.7) * mm});
            skLineSegment(sketch, "E414.1.0.1222", {"start": v(254.25, 51.3) * mm, "end": v(254.25, 53.25) * mm});
            skLineSegment(sketch, "E414.1.0.1223", {"start": v(129.75, 145.3) * mm, "end": v(129.75, 147.25) * mm});
            skLineSegment(sketch, "E414.1.0.1224", {"start": v(254.25, -140.7) * mm, "end": v(254.25, -138.75) * mm});
            skLineSegment(sketch, "E414.1.0.1225", {"start": v(1.2, -130.75) * mm, "end": v(1.2, -128.7) * mm});
            skLineSegment(sketch, "E414.1.0.1226", {"start": v(1.25, -122.7) * mm, "end": v(1.25, -120.75) * mm});
            skLineSegment(sketch, "E414.1.0.1227", {"start": v(125.75, 35.3) * mm, "end": v(125.75, 37.25) * mm});
            skLineSegment(sketch, "E414.1.0.1228", {"start": v(254.3, 53.25) * mm, "end": v(254.3, 53.3) * mm});
            skLineSegment(sketch, "E414.1.0.1229", {"start": v(-127.3, -140.92) * mm, "end": v(-127.3, -140.7) * mm});
            skLineSegment(sketch, "E414.1.0.1230", {"start": v(125.8, 139.25) * mm, "end": v(125.8, 141.25) * mm});
            skLineSegment(sketch, "E414.1.0.1231", {"start": v(3.03, 121.25) * mm, "end": v(1.2, 123.08) * mm});
            skLineSegment(sketch, "E414.1.0.1232", {"start": v(129.75, -122.7) * mm, "end": v(129.75, -120.75) * mm});
            skLineSegment(sketch, "E414.1.0.1233", {"start": v(-127.25, -130.7) * mm, "end": v(-127.25, -128.75) * mm});
            skLineSegment(sketch, "E414.1.0.1234", {"start": v(1.2, -52.92) * mm, "end": v(1.2, -52.7) * mm});
            skLineSegment(sketch, "E414.1.0.1235", {"start": v(254.3, 145.25) * mm, "end": v(254.3, 145.3) * mm});
            skLineSegment(sketch, "E414.1.0.1236", {"start": v(254.3, 35.25) * mm, "end": v(254.25, 35.25) * mm});
            skLineSegment(sketch, "E414.1.0.1237", {"start": v(125.75, 39.3) * mm, "end": v(125.75, 41.25) * mm});
            skLineSegment(sketch, "E414.1.0.1238", {"start": v(-127.3, 49.25) * mm, "end": v(-127.3, 51.3) * mm});
            skLineSegment(sketch, "E414.1.0.1239", {"start": v(1.25, -134.7) * mm, "end": v(1.25, -132.75) * mm});
            skLineSegment(sketch, "E414.1.0.1240", {"start": v(129.75, -118.7) * mm, "end": v(129.75, -116.75) * mm});
            skLineSegment(sketch, "E414.1.0.1241", {"start": v(254.25, 55.3) * mm, "end": v(254.25, 57.25) * mm});
            skLineSegment(sketch, "E414.1.0.1242", {"start": v(129.7, 59.3) * mm, "end": v(129.75, 59.3) * mm});
            skLineSegment(sketch, "E414.1.0.1243", {"start": v(1.2, -138.75) * mm, "end": v(1.2, -136.7) * mm});
            skLineSegment(sketch, "E414.1.0.1244", {"start": v(129.75, -114.7) * mm, "end": v(129.75, -112.75) * mm});
            skLineSegment(sketch, "E414.1.0.1245", {"start": v(135.55, -146.7) * mm, "end": v(133.6, -144.75) * mm});
            skLineSegment(sketch, "E414.1.0.1246", {"start": v(254.25, -28.7) * mm, "end": v(254.25, -26.75) * mm});
            skLineSegment(sketch, "E414.1.0.1247", {"start": v(254.3, -32.75) * mm, "end": v(254.3, -30.75) * mm});
            skLineSegment(sketch, "E414.1.0.1248", {"start": v(129.7, 45.25) * mm, "end": v(129.7, 47.3) * mm});
            skLineSegment(sketch, "E414.1.0.1249", {"start": v(129.75, 35.1) * mm, "end": v(129.75, 35.25) * mm});
            skLineSegment(sketch, "E414.1.0.1250", {"start": v(125.8, -120.75) * mm, "end": v(125.8, -118.75) * mm});
            skLineSegment(sketch, "E414.1.0.1251", {"start": v(125.75, -116.7) * mm, "end": v(125.75, -114.75) * mm});
            skLineSegment(sketch, "E414.1.0.1252", {"start": v(1.25, -34.7) * mm, "end": v(1.25, -32.75) * mm});
            skLineSegment(sketch, "E414.1.0.1253", {"start": v(125.75, 43.3) * mm, "end": v(125.75, 45.3) * mm});
            skLineSegment(sketch, "E414.1.0.1254", {"start": v(-2.7, 123.3) * mm, "end": v(-2.7, 123.25) * mm});
            skLineSegment(sketch, "E414.1.0.1255", {"start": v(129.7, -38.75) * mm, "end": v(129.7, -36.7) * mm});
            skLineSegment(sketch, "E414.1.0.1256", {"start": v(121.95, 119.3) * mm, "end": v(123.9, 121.25) * mm});
            skLineSegment(sketch, "E414.1.0.1257", {"start": v(1.2, -126.75) * mm, "end": v(1.2, -124.7) * mm});
            skLineSegment(sketch, "E414.1.0.1258", {"start": v(3.03, -142.75) * mm, "end": v(1.2, -140.92) * mm});
            skLineSegment(sketch, "E414.1.0.1259", {"start": v(125.8, -124.75) * mm, "end": v(125.8, -122.75) * mm});
            skLineSegment(sketch, "E414.1.0.1260", {"start": v(129.75, 41.3) * mm, "end": v(129.75, 43.25) * mm});
            skLineSegment(sketch, "E414.1.0.1261", {"start": v(7.03, 117.25) * mm, "end": v(4.98, 119.3) * mm});
            skLineSegment(sketch, "E414.1.0.1262", {"start": v(125.75, -40.7) * mm, "end": v(125.75, -38.75) * mm});
            skLineSegment(sketch, "E414.1.0.1263", {"start": v(125.8, 35.25) * mm, "end": v(125.75, 35.25) * mm});
            skLineSegment(sketch, "E414.1.0.1264", {"start": v(129.7, 37.25) * mm, "end": v(129.7, 39.3) * mm});
            skLineSegment(sketch, "E414.1.0.1265", {"start": v(254.25, 143.3) * mm, "end": v(254.25, 145.25) * mm});
            skLineSegment(sketch, "E414.1.0.1266", {"start": v(1.25, -118.7) * mm, "end": v(1.25, -116.75) * mm});
            skLineSegment(sketch, "E414.1.0.1267", {"start": v(254.3, -140.75) * mm, "end": v(254.25, -140.75) * mm});
            skLineSegment(sketch, "E414.1.0.1268", {"start": v(129.7, -116.7) * mm, "end": v(129.75, -116.7) * mm});
            skLineSegment(sketch, "E414.1.0.1269", {"start": v(-131.2, -122.75) * mm, "end": v(-131.2, -122.7) * mm});
            skLineSegment(sketch, "E414.1.0.1270", {"start": v(-131.25, -132.7) * mm, "end": v(-131.25, -130.7) * mm});
            skLineSegment(sketch, "E414.1.0.1271", {"start": v(-131.25, -128.7) * mm, "end": v(-131.25, -126.75) * mm});
            skLineSegment(sketch, "E414.1.0.1272", {"start": v(-135.03, -144.75) * mm, "end": v(-132.98, -142.7) * mm});
            skLineSegment(sketch, "E414.1.0.1273", {"start": v(-255.8, -46.75) * mm, "end": v(-255.8, -44.7) * mm});
            skLineSegment(sketch, "E414.1.0.1274", {"start": v(-131.2, 43.25) * mm, "end": v(-131.2, 45.3) * mm});
            skLineSegment(sketch, "E414.1.0.1275", {"start": v(-131.2, -52.7) * mm, "end": v(-131.2, -52.75) * mm});
            skLineSegment(sketch, "E414.1.0.1276", {"start": v(-131.25, 39.3) * mm, "end": v(-131.25, 41.25) * mm});
            skLineSegment(sketch, "E414.1.0.1277", {"start": v(-127.25, -138.7) * mm, "end": v(-127.25, -136.75) * mm});
            skLineSegment(sketch, "E414.1.0.1278", {"start": v(-6.55, 31.3) * mm, "end": v(-4.6, 33.25) * mm});
            skLineSegment(sketch, "E414.1.0.1279", {"start": v(-127.25, 41.3) * mm, "end": v(-127.25, 43.25) * mm});
            skLineSegment(sketch, "E414.1.0.1280", {"start": v(-131.2, 135.25) * mm, "end": v(-131.2, 137.3) * mm});
            skLineSegment(sketch, "E414.1.0.1281", {"start": v(-2.7, -140.7) * mm, "end": v(-2.7, -140.75) * mm});
            skLineSegment(sketch, "E414.1.0.1282", {"start": v(-2.7, -128.75) * mm, "end": v(-2.7, -126.7) * mm});
            skLineSegment(sketch, "E414.1.0.1283", {"start": v(-2.7, -136.75) * mm, "end": v(-2.7, -134.75) * mm});
            skLineSegment(sketch, "E414.1.0.1284", {"start": v(-131.2, -140.7) * mm, "end": v(-131.2, -138.7) * mm});
            skLineSegment(sketch, "E414.1.0.1285", {"start": v(-131.2, -30.75) * mm, "end": v(-131.2, -30.7) * mm});
            skLineSegment(sketch, "E414.1.0.1286", {"start": v(-131.2, 51.25) * mm, "end": v(-131.2, 53.25) * mm});
            skLineSegment(sketch, "E414.1.0.1287", {"start": v(-127.25, 37.3) * mm, "end": v(-127.25, 39.25) * mm});
            skLineSegment(sketch, "E414.1.0.1288", {"start": v(-127.25, 49.3) * mm, "end": v(-127.25, 51.25) * mm});
            skLineSegment(sketch, "E414.1.0.1289", {"start": v(-127.3, -134.75) * mm, "end": v(-127.3, -132.7) * mm});
            skLineSegment(sketch, "E414.1.0.1290", {"start": v(-2.7, -120.75) * mm, "end": v(-2.7, -118.75) * mm});
            skLineSegment(sketch, "E414.1.0.1291", {"start": v(-2.7, -132.75) * mm, "end": v(-2.7, -130.7) * mm});
            skLineSegment(sketch, "E414.1.0.1292", {"start": v(-127.3, -50.75) * mm, "end": v(-127.3, -48.7) * mm});
            skLineSegment(sketch, "E414.1.0.1293", {"start": v(-127.25, -34.7) * mm, "end": v(-127.25, -32.75) * mm});
            skLineSegment(sketch, "E414.1.0.1294", {"start": v(-131.25, 135.3) * mm, "end": v(-131.25, 137.25) * mm});
            skLineSegment(sketch, "E414.1.0.1295", {"start": v(-2.75, -128.7) * mm, "end": v(-2.75, -126.75) * mm});
            skLineSegment(sketch, "E414.1.0.1296", {"start": v(-6.53, -144.75) * mm, "end": v(-4.48, -142.7) * mm});
            skLineSegment(sketch, "E414.1.0.1297", {"start": v(-2.75, -124.7) * mm, "end": v(-2.75, -122.75) * mm});
            skLineSegment(sketch, "E414.1.0.1298", {"start": v(-127.25, -30.7) * mm, "end": v(-127.25, -28.75) * mm});
            skLineSegment(sketch, "E414.1.0.1299", {"start": v(-131.25, -32.7) * mm, "end": v(-131.25, -30.75) * mm});
            skLineSegment(sketch, "E414.1.0.1300", {"start": v(-131.25, 47.3) * mm, "end": v(-131.25, 49.25) * mm});
            skLineSegment(sketch, "E414.1.0.1301", {"start": v(-131.25, 51.3) * mm, "end": v(-131.25, 53.25) * mm});
            skLineSegment(sketch, "E414.1.0.1302", {"start": v(-255.8, 53.25) * mm, "end": v(-255.8, 55.3) * mm});
            skLineSegment(sketch, "E414.1.0.1303", {"start": v(-255.8, 57.25) * mm, "end": v(-255.8, 59.25) * mm});
            skLineSegment(sketch, "E414.1.0.1304", {"start": v(-131.2, 131.25) * mm, "end": v(-131.2, 133.3) * mm});
            skLineSegment(sketch, "E414.1.0.1305", {"start": v(-131.2, 147.25) * mm, "end": v(-131.2, 149.3) * mm});
            skLineSegment(sketch, "E414.1.0.1306", {"start": v(-127.25, -52.9) * mm, "end": v(-127.25, -52.75) * mm});
            skLineSegment(sketch, "E414.1.0.1307", {"start": v(-255.8, 59.3) * mm, "end": v(-255.75, 59.3) * mm});
            skLineSegment(sketch, "E414.1.0.1308", {"start": v(-131.25, -136.7) * mm, "end": v(-131.25, -134.75) * mm});
            skLineSegment(sketch, "E414.1.0.1309", {"start": v(-127.3, 133.25) * mm, "end": v(-127.3, 135.3) * mm});
            skLineSegment(sketch, "E414.1.0.1310", {"start": v(-127.25, 141.3) * mm, "end": v(-127.25, 143.25) * mm});
            skLineSegment(sketch, "E414.1.0.1311", {"start": v(-125.45, -142.7) * mm, "end": v(-127.25, -140.9) * mm});
            skLineSegment(sketch, "E414.1.0.1312", {"start": v(-2.75, -140.7) * mm, "end": v(-2.75, -138.75) * mm});
            skLineSegment(sketch, "E414.1.0.1313", {"start": v(-131.25, -140.7) * mm, "end": v(-131.25, -138.75) * mm});
            skLineSegment(sketch, "E414.1.0.1314", {"start": v(-2.7, -52.7) * mm, "end": v(-2.7, -52.75) * mm});
            skLineSegment(sketch, "E414.1.0.1315", {"start": v(-131.2, -44.75) * mm, "end": v(-131.2, -42.7) * mm});
            skLineSegment(sketch, "E414.1.0.1316", {"start": v(-131.25, -36.7) * mm, "end": v(-131.25, -34.75) * mm});
            skLineSegment(sketch, "E414.1.0.1317", {"start": v(-127.3, 45.25) * mm, "end": v(-127.3, 47.3) * mm});
            skLineSegment(sketch, "E414.1.0.1318", {"start": v(-127.25, 53.3) * mm, "end": v(-127.25, 55.25) * mm});
            skLineSegment(sketch, "E414.1.0.1319", {"start": v(-127.3, -138.75) * mm, "end": v(-127.3, -136.7) * mm});
            skLineSegment(sketch, "E414.1.0.1320", {"start": v(-131.25, 143.3) * mm, "end": v(-131.25, 145.25) * mm});
            skLineSegment(sketch, "E414.1.0.1321", {"start": v(-131.2, 139.25) * mm, "end": v(-131.2, 141.25) * mm});
            skLineSegment(sketch, "E414.1.0.1322", {"start": v(-127.25, 145.3) * mm, "end": v(-127.25, 147.25) * mm});
            skLineSegment(sketch, "E414.1.0.1323", {"start": v(-2.75, 59.3) * mm, "end": v(-2.75, 61.25) * mm});
            skLineSegment(sketch, "E414.1.0.1324", {"start": v(-131.2, 53.25) * mm, "end": v(-131.2, 53.3) * mm});
            skLineSegment(sketch, "E414.1.0.1325", {"start": v(-131.25, 43.3) * mm, "end": v(-131.25, 45.3) * mm});
            skLineSegment(sketch, "E414.1.0.1326", {"start": v(-131.2, -132.75) * mm, "end": v(-131.2, -130.7) * mm});
            skLineSegment(sketch, "E414.1.0.1327", {"start": v(-131.2, -140.7) * mm, "end": v(-131.2, -140.75) * mm});
            skLineSegment(sketch, "E414.1.0.1328", {"start": v(-131.2, -128.75) * mm, "end": v(-131.2, -126.7) * mm});
            skLineSegment(sketch, "E414.1.0.1329", {"start": v(125.8, 141.25) * mm, "end": v(125.8, 141.3) * mm});
            skLineSegment(sketch, "E414.1.0.1330", {"start": v(1.2, -122.75) * mm, "end": v(1.2, -120.7) * mm});
            skLineSegment(sketch, "E414.1.0.1331", {"start": v(3.05, -142.7) * mm, "end": v(1.25, -140.9) * mm});
            skLineSegment(sketch, "E414.1.0.1332", {"start": v(254.3, 55.25) * mm, "end": v(254.3, 57.25) * mm});
            skLineSegment(sketch, "E414.1.0.1333", {"start": v(-127.25, -140.9) * mm, "end": v(-127.25, -140.75) * mm});
            skLineSegment(sketch, "E414.1.0.1334", {"start": v(-127.3, -130.75) * mm, "end": v(-127.3, -128.7) * mm});
            skLineSegment(sketch, "E414.1.0.1335", {"start": v(129.75, -138.7) * mm, "end": v(129.75, -136.75) * mm});
            skLineSegment(sketch, "E414.1.0.1336", {"start": v(125.8, -36.75) * mm, "end": v(125.8, -34.75) * mm});
            skLineSegment(sketch, "E414.1.0.1337", {"start": v(125.8, 39.25) * mm, "end": v(125.8, 41.25) * mm});
            skLineSegment(sketch, "E414.1.0.1338", {"start": v(125.8, 35.3) * mm, "end": v(125.8, 35.25) * mm});
            skLineSegment(sketch, "E414.1.0.1339", {"start": v(254.3, 51.25) * mm, "end": v(254.3, 53.25) * mm});
            skLineSegment(sketch, "E414.1.0.1340", {"start": v(131.53, 33.25) * mm, "end": v(129.7, 35.08) * mm});
            skLineSegment(sketch, "E414.1.0.1341", {"start": v(-127.25, -46.7) * mm, "end": v(-127.25, -44.75) * mm});
            skLineSegment(sketch, "E414.1.0.1342", {"start": v(125.8, -52.7) * mm, "end": v(125.8, -50.7) * mm});
            skLineSegment(sketch, "E414.1.0.1343", {"start": v(125.75, 47.3) * mm, "end": v(125.75, 49.25) * mm});
            skLineSegment(sketch, "E414.1.0.1344", {"start": v(-2.7, -36.75) * mm, "end": v(-2.7, -34.75) * mm});
            skLineSegment(sketch, "E414.1.0.1345", {"start": v(129.7, 147.25) * mm, "end": v(129.7, 147.3) * mm});
            skLineSegment(sketch, "E414.1.0.1346", {"start": v(-127.3, -38.75) * mm, "end": v(-127.3, -36.7) * mm});
            skLineSegment(sketch, "E414.1.0.1347", {"start": v(1.25, -138.7) * mm, "end": v(1.25, -136.75) * mm});
            skLineSegment(sketch, "E414.1.0.1348", {"start": v(-135.05, -144.7) * mm, "end": v(-133.1, -142.75) * mm});
            skLineSegment(sketch, "E414.1.0.1349", {"start": v(-2.7, -34.75) * mm, "end": v(-2.7, -34.7) * mm});
            skLineSegment(sketch, "E414.1.0.1350", {"start": v(1.2, 147.3) * mm, "end": v(1.25, 147.3) * mm});
            skLineSegment(sketch, "E414.1.0.1351", {"start": v(-2.75, -40.7) * mm, "end": v(-2.75, -38.75) * mm});
            skLineSegment(sketch, "E414.1.0.1352", {"start": v(129.75, 137.3) * mm, "end": v(129.75, 139.25) * mm});
            skLineSegment(sketch, "E414.1.0.1353", {"start": v(125.75, -124.7) * mm, "end": v(125.75, -122.75) * mm});
            skLineSegment(sketch, "E414.1.0.1354", {"start": v(1.2, -118.75) * mm, "end": v(1.2, -116.75) * mm});
            skLineSegment(sketch, "E414.1.0.1355", {"start": v(-131.2, 39.25) * mm, "end": v(-131.2, 41.25) * mm});
            skLineSegment(sketch, "E414.1.0.1356", {"start": v(129.75, -134.7) * mm, "end": v(129.75, -132.75) * mm});
            skLineSegment(sketch, "E414.1.0.1357", {"start": v(-2.7, 35.25) * mm, "end": v(-2.75, 35.25) * mm});
            skLineSegment(sketch, "E414.1.0.1358", {"start": v(1.25, 123.1) * mm, "end": v(1.25, 123.25) * mm});
            skLineSegment(sketch, "E414.1.0.1359", {"start": v(-127.3, 41.25) * mm, "end": v(-127.3, 43.3) * mm});
            skLineSegment(sketch, "E414.1.0.1360", {"start": v(125.8, -122.75) * mm, "end": v(125.8, -122.7) * mm});
            skLineSegment(sketch, "E414.1.0.1361", {"start": v(125.8, -116.75) * mm, "end": v(125.8, -114.7) * mm});
            skLineSegment(sketch, "E414.1.0.1362", {"start": v(1.2, -34.75) * mm, "end": v(1.2, -32.7) * mm});
            skLineSegment(sketch, "E414.1.0.1363", {"start": v(125.8, 43.25) * mm, "end": v(125.8, 45.3) * mm});
            skLineSegment(sketch, "E414.1.0.1364", {"start": v(254.3, -28.75) * mm, "end": v(254.3, -26.7) * mm});
            skLineSegment(sketch, "E414.1.0.1365", {"start": v(-127.25, 125.3) * mm, "end": v(-127.25, 127.25) * mm});
            skLineSegment(sketch, "E414.1.0.1366", {"start": v(254.3, 143.25) * mm, "end": v(254.3, 145.25) * mm});
            skLineSegment(sketch, "E414.1.0.1367", {"start": v(1.25, -130.7) * mm, "end": v(1.25, -128.75) * mm});
            skLineSegment(sketch, "E414.1.0.1368", {"start": v(129.75, -130.7) * mm, "end": v(129.75, -128.75) * mm});
            skLineSegment(sketch, "E414.1.0.1369", {"start": v(254.3, 57.25) * mm, "end": v(254.3, 57.3) * mm});
            skLineSegment(sketch, "E414.1.0.1370", {"start": v(125.75, 135.3) * mm, "end": v(125.75, 137.25) * mm});
            skLineSegment(sketch, "E414.1.0.1371", {"start": v(121.97, 119.25) * mm, "end": v(124.02, 121.3) * mm});
            skLineSegment(sketch, "E414.1.0.1372", {"start": v(1.2, -134.75) * mm, "end": v(1.2, -132.7) * mm});
            skLineSegment(sketch, "E414.1.0.1373", {"start": v(125.8, 35.3) * mm, "end": v(125.8, 37.3) * mm});
            skLineSegment(sketch, "E414.1.0.1374", {"start": v(129.75, -126.7) * mm, "end": v(129.75, -124.75) * mm});
            skLineSegment(sketch, "E414.1.0.1375", {"start": v(254.3, 41.25) * mm, "end": v(254.3, 41.3) * mm});
            skLineSegment(sketch, "E414.1.0.1376", {"start": v(129.75, 37.3) * mm, "end": v(129.75, 39.25) * mm});
            skLineSegment(sketch, "E414.1.0.1377", {"start": v(125.75, -120.7) * mm, "end": v(125.75, -118.75) * mm});
            skLineSegment(sketch, "E414.1.0.1378", {"start": v(254.25, -32.7) * mm, "end": v(254.25, -30.75) * mm});
            skLineSegment(sketch, "E414.1.0.1379", {"start": v(254.3, -140.7) * mm, "end": v(254.3, -138.7) * mm});
            skLineSegment(sketch, "E414.1.0.1380", {"start": v(125.8, 131.25) * mm, "end": v(125.8, 133.3) * mm});
            skLineSegment(sketch, "E414.1.0.1381", {"start": v(129.7, -122.75) * mm, "end": v(129.7, -120.7) * mm});
            skLineSegment(sketch, "E414.1.0.1382", {"start": v(1.25, -140.9) * mm, "end": v(1.25, -140.75) * mm});
            skLineSegment(sketch, "E414.1.0.1383", {"start": v(125.75, -44.7) * mm, "end": v(125.75, -42.7) * mm});
            skLineSegment(sketch, "E414.1.0.1384", {"start": v(3.05, 33.3) * mm, "end": v(1.25, 35.1) * mm});
            skLineSegment(sketch, "E414.1.0.1385", {"start": v(129.7, -42.75) * mm, "end": v(129.7, -40.7) * mm});
            skLineSegment(sketch, "E414.1.0.1386", {"start": v(254.25, 123.3) * mm, "end": v(254.25, 125.25) * mm});
            skLineSegment(sketch, "E414.1.0.1387", {"start": v(131.55, 121.3) * mm, "end": v(129.75, 123.1) * mm});
            skLineSegment(sketch, "E414.1.0.1388", {"start": v(129.7, 35.08) * mm, "end": v(129.7, 35.3) * mm});
            skLineSegment(sketch, "E414.1.0.1389", {"start": v(129.75, 45.3) * mm, "end": v(129.75, 47.25) * mm});
            skLineSegment(sketch, "E414.1.0.1390", {"start": v(125.8, -136.75) * mm, "end": v(125.8, -134.75) * mm});
            skLineSegment(sketch, "E414.1.0.1391", {"start": v(-131.2, 145.25) * mm, "end": v(-131.2, 145.3) * mm});
            skLineSegment(sketch, "E414.1.0.1392", {"start": v(129.7, -118.75) * mm, "end": v(129.7, -116.75) * mm});
            skLineSegment(sketch, "E414.1.0.1393", {"start": v(254.25, -40.7) * mm, "end": v(254.25, -38.75) * mm});
            skLineSegment(sketch, "E414.1.0.1394", {"start": v(129.75, -46.7) * mm, "end": v(129.75, -44.75) * mm});
            skLineSegment(sketch, "E414.1.0.1395", {"start": v(-131.2, 123.3) * mm, "end": v(-131.2, 125.3) * mm});
            skLineSegment(sketch, "E414.1.0.1396", {"start": v(129.7, 41.25) * mm, "end": v(129.7, 43.3) * mm});
            skLineSegment(sketch, "E414.1.0.1397", {"start": v(125.8, 41.25) * mm, "end": v(125.8, 41.3) * mm});
            skLineSegment(sketch, "E414.1.0.1398", {"start": v(254.25, 127.3) * mm, "end": v(254.25, 129.25) * mm});
            skLineSegment(sketch, "E414.1.0.1399", {"start": v(129.75, 125.3) * mm, "end": v(129.75, 127.25) * mm});
            skLineSegment(sketch, "E414.1.0.1400", {"start": v(1.2, -116.75) * mm, "end": v(1.2, -116.7) * mm});
            skLineSegment(sketch, "E414.1.0.1401", {"start": v(125.75, -128.7) * mm, "end": v(125.75, -126.75) * mm});
            skLineSegment(sketch, "E414.1.0.1402", {"start": v(129.7, -50.75) * mm, "end": v(129.7, -48.7) * mm});
            skLineSegment(sketch, "E414.1.0.1403", {"start": v(129.75, -38.7) * mm, "end": v(129.75, -36.75) * mm});
            skLineSegment(sketch, "E414.1.0.1404", {"start": v(1.25, -126.7) * mm, "end": v(1.25, -124.75) * mm});
            skLineSegment(sketch, "E414.1.0.1405", {"start": v(125.75, 51.3) * mm, "end": v(125.75, 53.25) * mm});
            skLineSegment(sketch, "E414.1.0.1406", {"start": v(129.75, 53.3) * mm, "end": v(129.75, 55.25) * mm});
            skLineSegment(sketch, "E414.1.0.1407", {"start": v(254.3, 141.25) * mm, "end": v(254.3, 141.3) * mm});
            skLineSegment(sketch, "E414.1.0.1408", {"start": v(125.75, 123.3) * mm, "end": v(125.75, 125.25) * mm});
            skLineSegment(sketch, "E414.1.0.1409", {"start": v(125.8, -132.75) * mm, "end": v(125.8, -130.7) * mm});
            skLineSegment(sketch, "E414.1.0.1410", {"start": v(125.8, 53.25) * mm, "end": v(125.8, 53.3) * mm});
            skLineSegment(sketch, "E414.1.0.1411", {"start": v(254.3, -136.75) * mm, "end": v(254.3, -134.75) * mm});
            skLineSegment(sketch, "E414.1.0.1412", {"start": v(254.3, -36.75) * mm, "end": v(254.3, -34.75) * mm});
            skLineSegment(sketch, "E414.1.0.1413", {"start": v(129.7, 123.08) * mm, "end": v(129.7, 123.3) * mm});
            skLineSegment(sketch, "E414.1.0.1414", {"start": v(129.75, 133.3) * mm, "end": v(129.75, 135.25) * mm});
            skLineSegment(sketch, "E414.1.0.1415", {"start": v(125.8, -40.75) * mm, "end": v(125.8, -38.7) * mm});
            skLineSegment(sketch, "E414.1.0.1416", {"start": v(125.8, -48.75) * mm, "end": v(125.8, -46.75) * mm});
            skLineSegment(sketch, "E414.1.0.1417", {"start": v(1.2, 35.08) * mm, "end": v(1.2, 35.3) * mm});
            skLineSegment(sketch, "E414.1.0.1418", {"start": v(254.3, 123.25) * mm, "end": v(254.25, 123.25) * mm});
            skLineSegment(sketch, "E414.1.0.1419", {"start": v(129.7, 129.25) * mm, "end": v(129.7, 131.3) * mm});
            skLineSegment(sketch, "E414.1.0.1420", {"start": v(125.75, 127.3) * mm, "end": v(125.75, 129.25) * mm});
            skLineSegment(sketch, "E414.1.0.1421", {"start": v(125.8, 129.25) * mm, "end": v(125.8, 129.3) * mm});
            skLineSegment(sketch, "E414.1.0.1422", {"start": v(254.3, -140.7) * mm, "end": v(254.3, -140.75) * mm});
            skLineSegment(sketch, "E414.1.0.1423", {"start": v(129.7, -116.75) * mm, "end": v(129.7, -116.7) * mm});
            skLineSegment(sketch, "E414.1.0.1424", {"start": v(125.8, -140.7) * mm, "end": v(125.8, -138.7) * mm});
            skLineSegment(sketch, "E414.1.0.1425", {"start": v(129.75, 49.3) * mm, "end": v(129.75, 51.25) * mm});
            skLineSegment(sketch, "E414.1.0.1426", {"start": v(131.53, -142.75) * mm, "end": v(129.7, -140.92) * mm});
            skLineSegment(sketch, "E414.1.0.1427", {"start": v(1.25, -38.7) * mm, "end": v(1.25, -36.75) * mm});
            skLineSegment(sketch, "E414.1.0.1428", {"start": v(125.75, 55.3) * mm, "end": v(125.75, 57.25) * mm});
            skLineSegment(sketch, "E414.1.0.1429", {"start": v(-131.25, -52.7) * mm, "end": v(-131.25, -50.75) * mm});
            skLineSegment(sketch, "E414.1.0.1430", {"start": v(-131.2, -48.75) * mm, "end": v(-131.2, -46.75) * mm});
            skLineSegment(sketch, "E414.1.0.1431", {"start": v(-131.2, 41.25) * mm, "end": v(-131.2, 41.3) * mm});
            skLineSegment(sketch, "E414.1.0.1432", {"start": v(-255.75, 37.3) * mm, "end": v(-255.75, 39.25) * mm});
            skLineSegment(sketch, "E414.1.0.1433", {"start": v(-127.25, -42.7) * mm, "end": v(-127.25, -40.75) * mm});
            skLineSegment(sketch, "E414.1.0.1434", {"start": v(-2.75, -136.7) * mm, "end": v(-2.75, -134.75) * mm});
            skLineSegment(sketch, "E414.1.0.1435", {"start": v(-2.7, -134.75) * mm, "end": v(-2.7, -134.7) * mm});
            skLineSegment(sketch, "E414.1.0.1436", {"start": v(-6.53, 31.25) * mm, "end": v(-4.48, 33.3) * mm});
            skLineSegment(sketch, "E414.1.0.1437", {"start": v(-127.3, 137.25) * mm, "end": v(-127.3, 139.3) * mm});
            skLineSegment(sketch, "E414.1.0.1438", {"start": v(-125.47, 121.25) * mm, "end": v(-127.3, 123.08) * mm});
            skLineSegment(sketch, "E414.1.0.1439", {"start": v(-127.3, 129.25) * mm, "end": v(-127.3, 131.3) * mm});
            skLineSegment(sketch, "E414.1.0.1440", {"start": v(-131.2, 123.3) * mm, "end": v(-131.2, 123.25) * mm});
            skLineSegment(sketch, "E414.1.0.1441", {"start": v(-131.25, -40.7) * mm, "end": v(-131.25, -38.75) * mm});
            skLineSegment(sketch, "E414.1.0.1442", {"start": v(-253.97, 33.25) * mm, "end": v(-255.8, 35.08) * mm});
            skLineSegment(sketch, "E414.1.0.1443", {"start": v(-131.2, 127.25) * mm, "end": v(-131.2, 129.25) * mm});
            skLineSegment(sketch, "E414.1.0.1444", {"start": v(-131.25, 147.3) * mm, "end": v(-131.25, 149.25) * mm});
            skLineSegment(sketch, "E414.1.0.1445", {"start": v(-131.2, 143.25) * mm, "end": v(-131.2, 145.25) * mm});
            skLineSegment(sketch, "E414.1.0.1446", {"start": v(-2.7, -140.75) * mm, "end": v(-2.75, -140.75) * mm});
            skLineSegment(sketch, "E414.1.0.1447", {"start": v(-131.2, -140.75) * mm, "end": v(-131.25, -140.75) * mm});
            skLineSegment(sketch, "E414.1.0.1448", {"start": v(-127.25, -50.7) * mm, "end": v(-127.25, -48.75) * mm});
            skLineSegment(sketch, "E414.1.0.1449", {"start": v(-127.3, -42.75) * mm, "end": v(-127.3, -40.7) * mm});
            skLineSegment(sketch, "E414.1.0.1450", {"start": v(-131.25, -48.7) * mm, "end": v(-131.25, -46.75) * mm});
            skLineSegment(sketch, "E414.1.0.1451", {"start": v(-127.25, -38.7) * mm, "end": v(-127.25, -36.75) * mm});
            skLineSegment(sketch, "E414.1.0.1452", {"start": v(-131.25, 139.3) * mm, "end": v(-131.25, 141.25) * mm});
            skLineSegment(sketch, "E414.1.0.1453", {"start": v(-127.3, -46.75) * mm, "end": v(-127.3, -44.7) * mm});
            skLineSegment(sketch, "E414.1.0.1454", {"start": v(-2.7, -52.75) * mm, "end": v(-2.75, -52.75) * mm});
            skLineSegment(sketch, "E414.1.0.1455", {"start": v(-131.25, -44.7) * mm, "end": v(-131.25, -42.7) * mm});
            skLineSegment(sketch, "E414.1.0.1456", {"start": v(-131.2, -52.7) * mm, "end": v(-131.2, -50.7) * mm});
            skLineSegment(sketch, "E414.1.0.1457", {"start": v(-255.8, 59.25) * mm, "end": v(-255.8, 59.3) * mm});
            skLineSegment(sketch, "E414.1.0.1458", {"start": v(-131.2, -34.75) * mm, "end": v(-131.2, -34.7) * mm});
            skLineSegment(sketch, "E414.1.0.1459", {"start": v(-253.95, 33.3) * mm, "end": v(-255.75, 35.1) * mm});
            skLineSegment(sketch, "E414.1.0.1460", {"start": v(-131.2, 141.25) * mm, "end": v(-131.2, 141.3) * mm});
            skLineSegment(sketch, "E414.1.0.1461", {"start": v(-131.2, -46.75) * mm, "end": v(-131.2, -46.7) * mm});
            skLineSegment(sketch, "E414.1.0.1462", {"start": v(-127.25, 129.3) * mm, "end": v(-127.25, 131.25) * mm});
            skLineSegment(sketch, "E414.1.0.1463", {"start": v(-2.7, 59.25) * mm, "end": v(-2.7, 61.3) * mm});
            skLineSegment(sketch, "E414.1.0.1464", {"start": v(-127.3, 145.25) * mm, "end": v(-127.3, 147.25) * mm});
            skLineSegment(sketch, "E414.1.0.1465", {"start": v(-125.45, 121.3) * mm, "end": v(-127.25, 123.1) * mm});
            skLineSegment(sketch, "E414.1.0.1466", {"start": v(-127.3, 147.25) * mm, "end": v(-127.3, 147.3) * mm});
            skLineSegment(sketch, "E414.1.0.1467", {"start": v(-127.3, 141.25) * mm, "end": v(-127.3, 143.3) * mm});
            skLineSegment(sketch, "E414.1.0.1468", {"start": v(-131.2, -134.75) * mm, "end": v(-131.2, -134.7) * mm});
            skLineSegment(sketch, "E414.1.0.1469", {"start": v(-2.7, -40.75) * mm, "end": v(-2.7, -38.7) * mm});
            skLineSegment(sketch, "E414.1.0.1470", {"start": v(-2.7, -48.75) * mm, "end": v(-2.7, -46.75) * mm});
            skLineSegment(sketch, "E414.1.0.1471", {"start": v(-2.75, -36.7) * mm, "end": v(-2.75, -34.75) * mm});
            skLineSegment(sketch, "E414.1.0.1472", {"start": v(-127.25, 137.3) * mm, "end": v(-127.25, 139.25) * mm});
            skLineSegment(sketch, "E414.1.0.1473", {"start": v(-131.25, 123.3) * mm, "end": v(-131.25, 125.25) * mm});
            skLineSegment(sketch, "E414.1.0.1474", {"start": v(-2.7, 55.25) * mm, "end": v(-2.7, 57.25) * mm});
            skLineSegment(sketch, "E414.1.0.1475", {"start": v(-127.3, 125.25) * mm, "end": v(-127.3, 127.3) * mm});
            skLineSegment(sketch, "E414.1.0.1476", {"start": v(-255.8, 37.25) * mm, "end": v(-255.8, 39.3) * mm});
            skLineSegment(sketch, "E414.1.0.1477", {"start": v(125.75, 131.3) * mm, "end": v(125.75, 133.3) * mm});
            skLineSegment(sketch, "E414.1.0.1478", {"start": v(125.75, -140.7) * mm, "end": v(125.75, -138.75) * mm});
            skLineSegment(sketch, "E414.1.0.1479", {"start": v(125.8, -44.75) * mm, "end": v(125.8, -42.7) * mm});
            skLineSegment(sketch, "E414.1.0.1480", {"start": v(129.7, -138.75) * mm, "end": v(129.7, -136.7) * mm});
            skLineSegment(sketch, "E414.1.0.1481", {"start": v(129.7, 133.25) * mm, "end": v(129.7, 135.3) * mm});
            skLineSegment(sketch, "E414.1.0.1482", {"start": v(1.2, 123.08) * mm, "end": v(1.2, 123.3) * mm});
            skLineSegment(sketch, "E414.1.0.1483", {"start": v(125.8, -118.75) * mm, "end": v(125.8, -118.7) * mm});
            skLineSegment(sketch, "E414.1.0.1484", {"start": v(1.2, -38.75) * mm, "end": v(1.2, -36.7) * mm});
            skLineSegment(sketch, "E414.1.0.1485", {"start": v(125.8, 47.25) * mm, "end": v(125.8, 49.3) * mm});
            skLineSegment(sketch, "E414.1.0.1486", {"start": v(-2.75, -44.7) * mm, "end": v(-2.75, -42.7) * mm});
            skLineSegment(sketch, "E414.1.0.1487", {"start": v(254.3, -30.75) * mm, "end": v(254.3, -30.7) * mm});
            skLineSegment(sketch, "E414.1.0.1488", {"start": v(129.7, 49.25) * mm, "end": v(129.7, 51.3) * mm});
            skLineSegment(sketch, "E414.1.0.1489", {"start": v(254.3, 127.25) * mm, "end": v(254.3, 129.25) * mm});
            skLineSegment(sketch, "E414.1.0.1490", {"start": v(129.7, -134.75) * mm, "end": v(129.7, -132.7) * mm});
            skLineSegment(sketch, "E414.1.0.1491", {"start": v(129.75, -50.7) * mm, "end": v(129.75, -48.75) * mm});
            skLineSegment(sketch, "E414.1.0.1492", {"start": v(129.75, 129.3) * mm, "end": v(129.75, 131.25) * mm});
            skLineSegment(sketch, "E414.1.0.1493", {"start": v(254.25, 135.3) * mm, "end": v(254.25, 137.25) * mm});
            skLineSegment(sketch, "E414.1.0.1494", {"start": v(125.75, -136.7) * mm, "end": v(125.75, -134.75) * mm});
            skLineSegment(sketch, "E414.1.0.1495", {"start": v(-2.7, 39.25) * mm, "end": v(-2.7, 41.25) * mm});
            skLineSegment(sketch, "E414.1.0.1496", {"start": v(-2.75, 35.3) * mm, "end": v(-2.75, 37.25) * mm});
            skLineSegment(sketch, "E414.1.0.1497", {"start": v(129.7, 125.25) * mm, "end": v(129.7, 127.3) * mm});
            skLineSegment(sketch, "E414.1.0.1498", {"start": v(-2.7, 35.3) * mm, "end": v(-2.7, 35.25) * mm});
            skLineSegment(sketch, "E414.1.0.1499", {"start": v(254.25, -36.7) * mm, "end": v(254.25, -34.75) * mm});
            skLineSegment(sketch, "E414.1.0.1500", {"start": v(125.75, -132.7) * mm, "end": v(125.75, -130.7) * mm});
            skLineSegment(sketch, "E414.1.0.1501", {"start": v(125.8, 55.25) * mm, "end": v(125.8, 57.25) * mm});
            skLineSegment(sketch, "E414.1.0.1502", {"start": v(129.7, -130.75) * mm, "end": v(129.7, -128.7) * mm});
            skLineSegment(sketch, "E414.1.0.1503", {"start": v(254.3, -34.75) * mm, "end": v(254.3, -34.7) * mm});
            skLineSegment(sketch, "E414.1.0.1504", {"start": v(129.7, 53.25) * mm, "end": v(129.7, 55.3) * mm});
            skLineSegment(sketch, "E414.1.0.1505", {"start": v(125.8, 135.25) * mm, "end": v(125.8, 137.3) * mm});
            skLineSegment(sketch, "E414.1.0.1506", {"start": v(125.8, 127.25) * mm, "end": v(125.8, 129.25) * mm});
            skLineSegment(sketch, "E414.1.0.1507", {"start": v(1.2, -140.92) * mm, "end": v(1.2, -140.7) * mm});
            skLineSegment(sketch, "E414.1.0.1508", {"start": v(125.8, 51.25) * mm, "end": v(125.8, 53.25) * mm});
            skLineSegment(sketch, "E414.1.0.1509", {"start": v(3.03, 33.25) * mm, "end": v(1.2, 35.08) * mm});
            skLineSegment(sketch, "E414.1.0.1510", {"start": v(129.75, -42.7) * mm, "end": v(129.75, -40.75) * mm});
            skLineSegment(sketch, "E414.1.0.1511", {"start": v(131.53, 121.25) * mm, "end": v(129.7, 123.08) * mm});
            skLineSegment(sketch, "E414.1.0.1512", {"start": v(-127.3, 123.08) * mm, "end": v(-127.3, 123.3) * mm});
            skLineSegment(sketch, "E414.1.0.1513", {"start": v(125.75, -48.7) * mm, "end": v(125.75, -46.75) * mm});
            skLineSegment(sketch, "E414.1.0.1514", {"start": v(129.7, -46.75) * mm, "end": v(129.7, -44.7) * mm});
            skLineSegment(sketch, "E414.1.0.1515", {"start": v(254.3, 123.3) * mm, "end": v(254.3, 125.3) * mm});
            skLineSegment(sketch, "E414.1.0.1516", {"start": v(1.2, -116.7) * mm, "end": v(1.25, -116.7) * mm});
            skLineSegment(sketch, "E414.1.0.1517", {"start": v(254.25, -124.7) * mm, "end": v(254.25, -122.75) * mm});
            skLineSegment(sketch, "E414.1.0.1518", {"start": v(1.2, 53.25) * mm, "end": v(1.2, 55.3) * mm});
            skLineSegment(sketch, "E414.1.0.1519", {"start": v(254.3, -128.75) * mm, "end": v(254.3, -126.7) * mm});
            skLineSegment(sketch, "E414.1.0.1520", {"start": v(254.3, -40.75) * mm, "end": v(254.3, -38.7) * mm});
            skLineSegment(sketch, "E414.1.0.1521", {"start": v(254.3, -48.75) * mm, "end": v(254.3, -46.75) * mm});
            skLineSegment(sketch, "E414.1.0.1522", {"start": v(125.8, 57.25) * mm, "end": v(125.8, 57.3) * mm});
            skLineSegment(sketch, "E414.1.0.1523", {"start": v(125.8, -140.7) * mm, "end": v(125.8, -140.75) * mm});
            skLineSegment(sketch, "E414.1.0.1524", {"start": v(125.8, -128.75) * mm, "end": v(125.8, -126.7) * mm});
            skLineSegment(sketch, "E414.1.0.1525", {"start": v(125.8, 123.3) * mm, "end": v(125.8, 125.3) * mm});
            skLineSegment(sketch, "E414.1.0.1526", {"start": v(-2.7, 51.25) * mm, "end": v(-2.7, 53.25) * mm});
            skLineSegment(sketch, "E414.1.0.1527", {"start": v(254.3, 129.25) * mm, "end": v(254.3, 129.3) * mm});
            skLineSegment(sketch, "E414.1.0.1528", {"start": v(1.25, 37.3) * mm, "end": v(1.25, 39.25) * mm});
            skLineSegment(sketch, "E414.1.0.1529", {"start": v(254.3, -132.75) * mm, "end": v(254.3, -130.7) * mm});
            skLineSegment(sketch, "E414.1.0.1530", {"start": v(254.25, 139.3) * mm, "end": v(254.25, 141.25) * mm});
            skLineSegment(sketch, "E414.1.0.1531", {"start": v(1.2, 57.25) * mm, "end": v(1.2, 59.25) * mm});
            skLineSegment(sketch, "E414.1.0.1532", {"start": v(254.25, -136.7) * mm, "end": v(254.25, -134.75) * mm});
            skLineSegment(sketch, "E414.1.0.1533", {"start": v(254.3, -44.75) * mm, "end": v(254.3, -42.7) * mm});
            skLineSegment(sketch, "E414.1.0.1534", {"start": v(254.25, 131.3) * mm, "end": v(254.25, 133.3) * mm});
            skLineSegment(sketch, "E414.1.0.1535", {"start": v(1.2, -42.75) * mm, "end": v(1.2, -40.7) * mm});
            skLineSegment(sketch, "E414.1.0.1536", {"start": v(131.55, -142.7) * mm, "end": v(129.75, -140.9) * mm});
            skLineSegment(sketch, "E414.1.0.1537", {"start": v(1.25, -46.7) * mm, "end": v(1.25, -44.75) * mm});
            skLineSegment(sketch, "E414.1.0.1538", {"start": v(1.2, -50.75) * mm, "end": v(1.2, -48.7) * mm});
            skLineSegment(sketch, "E414.1.0.1539", {"start": v(1.2, 59.3) * mm, "end": v(1.25, 59.3) * mm});
            skLineSegment(sketch, "E414.1.0.1540", {"start": v(-131.2, -40.75) * mm, "end": v(-131.2, -38.7) * mm});
            skLineSegment(sketch, "E414.1.0.1541", {"start": v(-255.8, 35.08) * mm, "end": v(-255.8, 35.3) * mm});
            skLineSegment(sketch, "E414.1.0.1542", {"start": v(-255.75, 45.3) * mm, "end": v(-255.75, 47.25) * mm});
            skLineSegment(sketch, "E414.1.0.1543", {"start": v(-2.7, 57.25) * mm, "end": v(-2.7, 57.3) * mm});
            skLineSegment(sketch, "E414.1.0.1544", {"start": v(-131.25, 127.3) * mm, "end": v(-131.25, 129.25) * mm});
            skLineSegment(sketch, "E414.1.0.1545", {"start": v(-255.8, 49.25) * mm, "end": v(-255.8, 51.3) * mm});
            skLineSegment(sketch, "E414.1.0.1546", {"start": v(-255.8, 41.25) * mm, "end": v(-255.8, 43.3) * mm});
            skLineSegment(sketch, "E414.1.0.1547", {"start": v(-2.75, 39.3) * mm, "end": v(-2.75, 41.25) * mm});
            skLineSegment(sketch, "E414.1.0.1548", {"start": v(-131.2, 123.25) * mm, "end": v(-131.25, 123.25) * mm});
            skLineSegment(sketch, "E414.1.0.1549", {"start": v(-127.3, 147.3) * mm, "end": v(-127.25, 147.3) * mm});
            skLineSegment(sketch, "E414.1.0.1550", {"start": v(-2.75, -48.7) * mm, "end": v(-2.75, -46.75) * mm});
            skLineSegment(sketch, "E414.1.0.1551", {"start": v(-2.7, -46.75) * mm, "end": v(-2.7, -46.7) * mm});
            skLineSegment(sketch, "E414.1.0.1552", {"start": v(-255.75, 41.3) * mm, "end": v(-255.75, 43.25) * mm});
            skLineSegment(sketch, "E414.1.0.1553", {"start": v(-2.7, 35.3) * mm, "end": v(-2.7, 37.3) * mm});
            skLineSegment(sketch, "E414.1.0.1554", {"start": v(-2.75, 55.3) * mm, "end": v(-2.75, 57.25) * mm});
            skLineSegment(sketch, "E414.1.0.1555", {"start": v(-127.25, 123.1) * mm, "end": v(-127.25, 123.25) * mm});
            skLineSegment(sketch, "E414.1.0.1556", {"start": v(-2.7, -44.75) * mm, "end": v(-2.7, -42.7) * mm});
            skLineSegment(sketch, "E414.1.0.1557", {"start": v(-2.7, 43.25) * mm, "end": v(-2.7, 45.3) * mm});
            skLineSegment(sketch, "E414.1.0.1558", {"start": v(-2.75, 51.3) * mm, "end": v(-2.75, 53.25) * mm});
            skLineSegment(sketch, "E414.1.0.1559", {"start": v(-255.75, 35.1) * mm, "end": v(-255.75, 35.25) * mm});
            skLineSegment(sketch, "E414.1.0.1560", {"start": v(-255.8, 45.25) * mm, "end": v(-255.8, 47.3) * mm});
            skLineSegment(sketch, "E414.1.0.1561", {"start": v(-255.75, 49.3) * mm, "end": v(-255.75, 51.25) * mm});
            skLineSegment(sketch, "E414.1.0.1562", {"start": v(1.25, 53.3) * mm, "end": v(1.25, 55.25) * mm});
            skLineSegment(sketch, "E414.1.0.1563", {"start": v(1.25, 35.1) * mm, "end": v(1.25, 35.25) * mm});
            skLineSegment(sketch, "E414.1.0.1564", {"start": v(129.75, 123.1) * mm, "end": v(129.75, 123.25) * mm});
            skLineSegment(sketch, "E414.1.0.1565", {"start": v(254.3, 135.25) * mm, "end": v(254.3, 137.3) * mm});
            skLineSegment(sketch, "E414.1.0.1566", {"start": v(254.3, 123.3) * mm, "end": v(254.3, 123.25) * mm});
            skLineSegment(sketch, "E414.1.0.1567", {"start": v(254.25, -48.7) * mm, "end": v(254.25, -46.75) * mm});
            skLineSegment(sketch, "E414.1.0.1568", {"start": v(254.3, -46.75) * mm, "end": v(254.3, -46.7) * mm});
            skLineSegment(sketch, "E414.1.0.1569", {"start": v(125.8, -134.75) * mm, "end": v(125.8, -134.7) * mm});
            skLineSegment(sketch, "E414.1.0.1570", {"start": v(1.2, 37.25) * mm, "end": v(1.2, 39.3) * mm});
            skLineSegment(sketch, "E414.1.0.1571", {"start": v(254.25, -44.7) * mm, "end": v(254.25, -42.7) * mm});
            skLineSegment(sketch, "E414.1.0.1572", {"start": v(254.3, 131.25) * mm, "end": v(254.3, 133.3) * mm});
            skLineSegment(sketch, "E414.1.0.1573", {"start": v(125.8, 123.3) * mm, "end": v(125.8, 123.25) * mm});
            skLineSegment(sketch, "E414.1.0.1574", {"start": v(1.2, 49.25) * mm, "end": v(1.2, 51.3) * mm});
            skLineSegment(sketch, "E414.1.0.1575", {"start": v(254.3, 139.25) * mm, "end": v(254.3, 141.25) * mm});
            skLineSegment(sketch, "E414.1.0.1576", {"start": v(125.8, -140.75) * mm, "end": v(125.75, -140.75) * mm});
            skLineSegment(sketch, "E414.1.0.1577", {"start": v(1.25, -50.7) * mm, "end": v(1.25, -48.75) * mm});
            skLineSegment(sketch, "E414.1.0.1578", {"start": v(125.8, -46.75) * mm, "end": v(125.8, -46.7) * mm});
            skLineSegment(sketch, "E414.1.0.1579", {"start": v(254.3, -134.75) * mm, "end": v(254.3, -134.7) * mm});
            skLineSegment(sketch, "E414.1.0.1580", {"start": v(254.3, -124.75) * mm, "end": v(254.3, -122.75) * mm});
            skLineSegment(sketch, "E414.1.0.1581", {"start": v(1.25, 57.3) * mm, "end": v(1.25, 59.25) * mm});
            skLineSegment(sketch, "E414.1.0.1582", {"start": v(129.7, -140.92) * mm, "end": v(129.7, -140.7) * mm});
            skLineSegment(sketch, "E414.1.0.1583", {"start": v(254.25, -128.7) * mm, "end": v(254.25, -126.75) * mm});
            skLineSegment(sketch, "E414.1.0.1584", {"start": v(1.25, -42.7) * mm, "end": v(1.25, -40.75) * mm});
            skLineSegment(sketch, "E414.1.0.1585", {"start": v(254.25, -132.7) * mm, "end": v(254.25, -130.7) * mm});
            skLineSegment(sketch, "E414.1.0.1586", {"start": v(1.2, -46.75) * mm, "end": v(1.2, -44.7) * mm});
            skLineSegment(sketch, "E414.1.0.1587", {"start": v(1.25, 45.3) * mm, "end": v(1.25, 47.25) * mm});
            skLineSegment(sketch, "E414.1.0.1588", {"start": v(1.2, 41.25) * mm, "end": v(1.2, 43.3) * mm});
            skLineSegment(sketch, "E414.1.0.1589", {"start": v(-2.75, 47.3) * mm, "end": v(-2.75, 49.25) * mm});
            skLineSegment(sketch, "E414.1.0.1590", {"start": v(-131.2, 129.25) * mm, "end": v(-131.2, 129.3) * mm});
            skLineSegment(sketch, "E414.1.0.1591", {"start": v(-2.7, 41.25) * mm, "end": v(-2.7, 41.3) * mm});
            skLineSegment(sketch, "E414.1.0.1592", {"start": v(-2.7, 53.25) * mm, "end": v(-2.7, 53.3) * mm});
            skLineSegment(sketch, "E414.1.0.1593", {"start": v(-2.75, 43.3) * mm, "end": v(-2.75, 45.3) * mm});
            skLineSegment(sketch, "E414.1.0.1594", {"start": v(1.2, 45.25) * mm, "end": v(1.2, 47.3) * mm});
            skLineSegment(sketch, "E414.1.0.1595", {"start": v(125.8, 123.25) * mm, "end": v(125.75, 123.25) * mm});
            skLineSegment(sketch, "E414.1.0.1596", {"start": v(1.25, 41.3) * mm, "end": v(1.25, 43.25) * mm});
            skLineSegment(sketch, "E414.1.0.1597", {"start": v(1.2, 59.25) * mm, "end": v(1.2, 59.3) * mm});
            skLineSegment(sketch, "E414.1.0.1598", {"start": v(1.25, 49.3) * mm, "end": v(1.25, 51.25) * mm});
            skLineSegment(sketch, "E414.1.0.1599", {"start": v(-2.7, 47.25) * mm, "end": v(-2.7, 49.3) * mm});
            skLineSegment(sketch, "E414.1.0.1600", {"start": v(254.3, -122.75) * mm, "end": v(254.3, -122.7) * mm});
            skLineSegment(sketch, "E414.1.0.1601", {"start": v(129.75, -140.9) * mm, "end": v(129.75, -140.75) * mm});
            skLineSegment(sketch, "E414.direction1", {"start": v(-256, -109) * mm, "end": v(296, -109) * mm, "construction": true});
            skSolve(sketch);
        }
        {
            var Q0;
            Q0=makeQuery(id+"F24.opExtrude","CAP_FACE",FACE,{"disambiguationData":[OSD([sQuery(id+"F23.wireOp",EDGE,"E155.MirrorCS"),sQuery(id+"F23.wireOp",EDGE,"E156.MirrorCS"),sQuery(id+"F23.wireOp",EDGE,"E157.MirrorCS"),sQuery(id+"F23.wireOp",EDGE,"E162.MirrorCS"),sQuery(id+"F23.wireOp",EDGE,"E163.MirrorCS"),sQuery(id+"F23.wireOp",EDGE,"E166.MirrorCS")])],"isStart":false});
            var sketch = newSketch(context, id + "F26", { "sketchPlane" : qUnion([Q0])});
            skLineSegment(sketch, "E415.left", {"start": v(-226, 209) * mm, "end": v(-226, -209) * mm});
            skLineSegment(sketch, "E415.right", {"start": v(-224, 203) * mm, "end": v(-224, -203) * mm});
            skLineSegment(sketch, "E416.left", {"start": v(222.5, 203) * mm, "end": v(222.5, -203) * mm});
            skLineSegment(sketch, "E416.right", {"start": v(224.5, 209) * mm, "end": v(224.5, -209) * mm});
            skLineSegment(sketch, "E417.bottom", {"start": v(-226, 209) * mm, "end": v(-111.5, 209) * mm});
            skLineSegment(sketch, "E417.top", {"start": v(-224, 203) * mm, "end": v(-163, 203) * mm});
            skLineSegment(sketch, "E418.bottom", {"start": v(-224, -203) * mm, "end": v(-163, -203) * mm});
            skLineSegment(sketch, "E418.top", {"start": v(-226, -209) * mm, "end": v(-32.5, -209) * mm});
            skLineSegment(sketch, "E419.left", {"start": v(-163, 203) * mm, "end": v(-163, -203) * mm});
            skLineSegment(sketch, "E419.right", {"start": v(-161, 203) * mm, "end": v(-161, -203) * mm});
            skLineSegment(sketch, "E420.left", {"start": v(-97.5, 203) * mm, "end": v(-97.5, -203) * mm});
            skLineSegment(sketch, "E420.right", {"start": v(-95.5, 203) * mm, "end": v(-95.5, -203) * mm});
            skLineSegment(sketch, "E421.left", {"start": v(-34.5, 203) * mm, "end": v(-34.5, -203) * mm});
            skLineSegment(sketch, "E421.right", {"start": v(-32.5, 203) * mm, "end": v(-32.5, -203) * mm});
            skLineSegment(sketch, "E422.left", {"start": v(31, 203) * mm, "end": v(31, -203) * mm});
            skLineSegment(sketch, "E422.right", {"start": v(33, 203) * mm, "end": v(33, -203) * mm});
            skLineSegment(sketch, "E423.left", {"start": v(94, 203) * mm, "end": v(94, -203) * mm});
            skLineSegment(sketch, "E423.right", {"start": v(96, 203) * mm, "end": v(96, -203) * mm});
            skLineSegment(sketch, "E424.top", {"start": v(159.5, -209) * mm, "end": v(161.5, -209) * mm});
            skLineSegment(sketch, "E424.left", {"start": v(159.5, 203) * mm, "end": v(159.5, -203) * mm});
            skLineSegment(sketch, "E424.right", {"start": v(161.5, 203) * mm, "end": v(161.5, -203) * mm});
            skLineSegment(sketch, "E425.trimOffspring", {"start": v(-161, 203) * mm, "end": v(-111.5, 203) * mm});
            skLineSegment(sketch, "E426.trimOffspring", {"start": v(-95.5, 203) * mm, "end": v(-34.5, 203) * mm});
            skLineSegment(sketch, "E427.trimOffspring", {"start": v(-32.5, 203) * mm, "end": v(31, 203) * mm});
            skLineSegment(sketch, "E428.trimOffspring", {"start": v(33, 203) * mm, "end": v(94, 203) * mm});
            skLineSegment(sketch, "E429.trimOffspring", {"start": v(110, 203) * mm, "end": v(159.5, 203) * mm});
            skLineSegment(sketch, "E430.trimOffspring", {"start": v(161.5, 203) * mm, "end": v(222.5, 203) * mm});
            skPoint(sketch, "E419.top.end.orphan", {"position": v(-161, -213.75) * mm});
            skLineSegment(sketch, "E431.trimOffspring", {"start": v(-161, -203) * mm, "end": v(-97.5, -203) * mm});
            skPoint(sketch, "E420.top.end.orphan", {"position": v(-95.5, -213.75) * mm});
            skLineSegment(sketch, "E432.trimOffspring", {"start": v(-95.5, -203) * mm, "end": v(-34.5, -203) * mm});
            skPoint(sketch, "E421.top.end.orphan", {"position": v(-32.5, -213.75) * mm});
            skPoint(sketch, "E422.top.end.orphan", {"position": v(33, -213.75) * mm});
            skLineSegment(sketch, "E433.trimOffspring", {"start": v(33, -203) * mm, "end": v(94, -203) * mm});
            skLineSegment(sketch, "E434.trimOffspring", {"start": v(96, -203) * mm, "end": v(159.5, -203) * mm});
            skLineSegment(sketch, "E435.trimOffspring", {"start": v(161.5, -203) * mm, "end": v(222.5, -203) * mm});
            skLineSegment(sketch, "E436", {"start": v(-32.5, -203) * mm, "end": v(-32.5, -209) * mm});
            skLineSegment(sketch, "E437", {"start": v(31, -203) * mm, "end": v(31, -209) * mm});
            skLineSegment(sketch, "E438.trimOffspring", {"start": v(31, -209) * mm, "end": v(224.5, -209) * mm});
            skLineSegment(sketch, "E439", {"start": v(-97.5, 203) * mm, "end": v(-97.5, 209) * mm});
            skLineSegment(sketch, "E440", {"start": v(-111.5, 209) * mm, "end": v(-111.5, 203) * mm});
            skLineSegment(sketch, "E441.trimOffspring", {"start": v(-97.5, 209) * mm, "end": v(96, 209) * mm});
            skLineSegment(sketch, "E442", {"start": v(96, 203) * mm, "end": v(96, 209) * mm});
            skLineSegment(sketch, "E443", {"start": v(110, 209) * mm, "end": v(110, 203) * mm});
            skLineSegment(sketch, "E444.trimOffspring", {"start": v(110, 209) * mm, "end": v(224.5, 209) * mm});
            skSolve(sketch);
        }
        {
            var Q0;
            Q0 = qSketchRegion(id + "F26", true);
            extrude(context, id + "F27", {"entities" : qUnion([Q0]), "depth" : .1 * mm});
        }
    });
